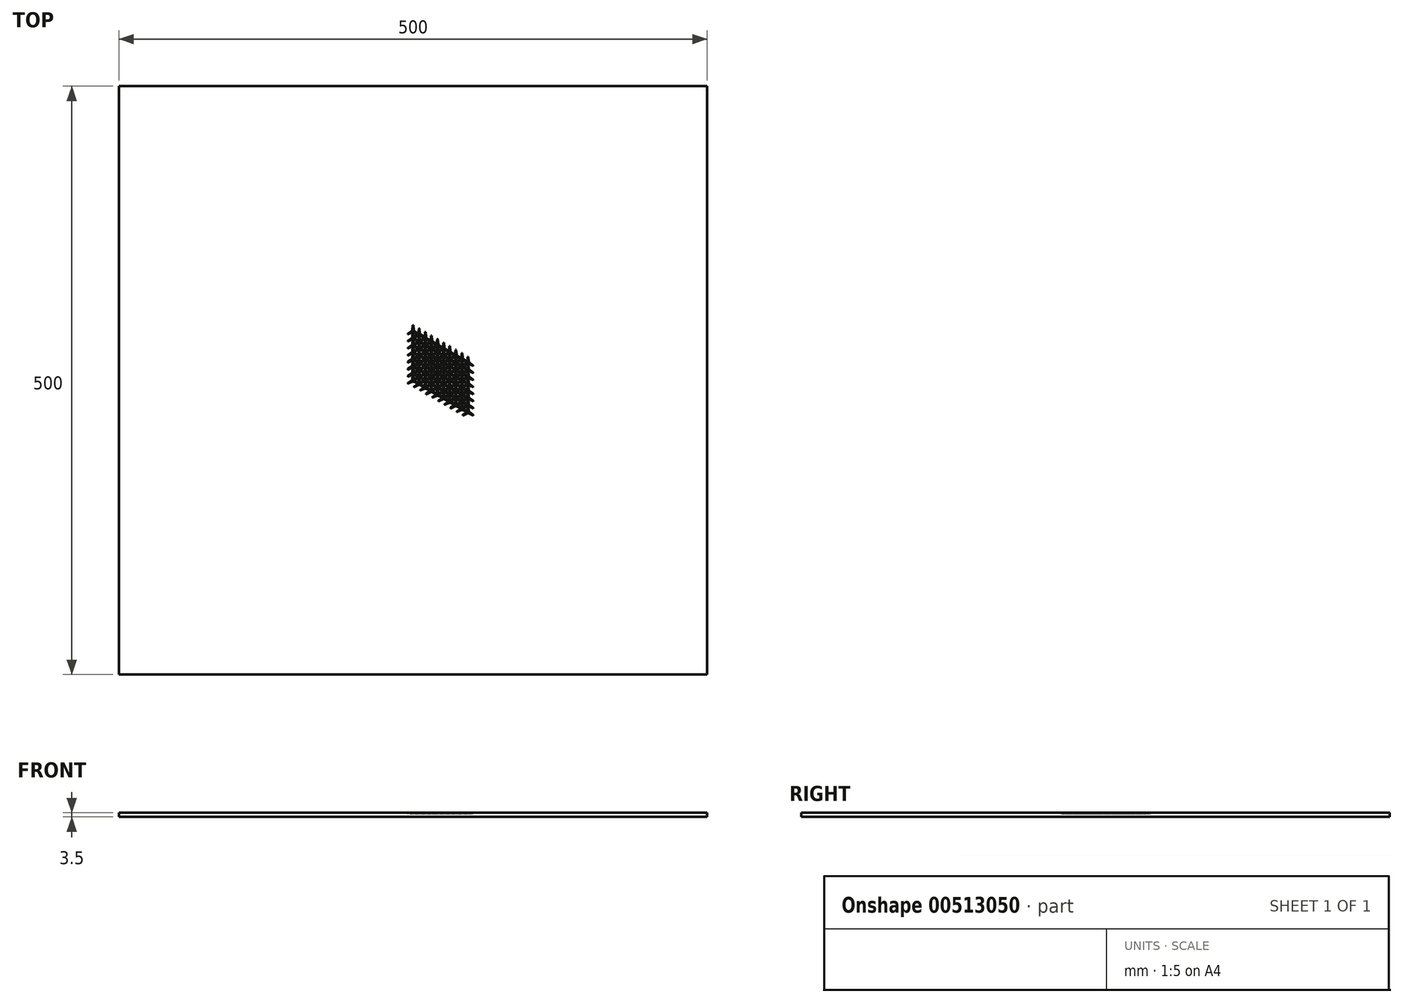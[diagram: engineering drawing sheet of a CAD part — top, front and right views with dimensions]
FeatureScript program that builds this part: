
annotation { "Feature Type Name" : "Feature", "Feature Type Description" : "" }
export const myFeature = defineFeature(function(context is Context, id is Id, definition is map)
    precondition{}
    {
        {
            var Q0;
            Q0=qCreatedBy(makeId("Top.planeOp"),FACE);
            var sketch = newSketch(context, id + "F0", { "sketchPlane" : qUnion([Q0])});
            skLineSegment(sketch, "E0", {"start": v(0, 0) * mm, "end": v(0, 250) * mm, "construction": true});
            skLineSegment(sketch, "E1", {"start": v(250, 0) * mm, "end": v(0, 0) * mm, "construction": true});
            skLineSegment(sketch, "E2.bottom", {"start": v(-250, 250) * mm, "end": v(250, 250) * mm});
            skLineSegment(sketch, "E2.top", {"start": v(-250, -250) * mm, "end": v(250, -250) * mm});
            skLineSegment(sketch, "E2.left", {"start": v(-250, 250) * mm, "end": v(-250, -250) * mm});
            skLineSegment(sketch, "E2.right", {"start": v(250, 250) * mm, "end": v(250, -250) * mm});
            skSolve(sketch);
        }
        {
            var Q0;
            Q0=makeQuery(id+"F0.imprint","IMPRINT",FACE,{"disambiguationData":[TD([[makeQuery(id+"F0.imprint","IMPRINT",EDGE,{"derivedFrom":sQuery(id+"F0.wireOp",EDGE,"E2.bottom")}),-1.0]])]});
            extrude(context, id + "F1", {"entities" : qUnion([Q0]), "depth" : 2.5 * mm});
        }
        {
            var Q0;
            Q0=makeQuery(id+"F1.opExtrude","CAP_FACE",FACE,{"disambiguationData":[OSD([sQuery(id+"F0.wireOp",EDGE,"E2.bottom"),sQuery(id+"F0.wireOp",EDGE,"E2.top"),sQuery(id+"F0.wireOp",EDGE,"E2.left"),sQuery(id+"F0.wireOp",EDGE,"E2.right")])],"isStart":false});
            var sketch = newSketch(context, id + "F2", { "sketchPlane" : qUnion([Q0])});
            skCircle(sketch, "E3", {"center": v(0, 0) * mm, "radius": 50 * mm, "construction": true});
            skLineSegment(sketch, "E4", {"start": v(0, 0) * mm, "end": v(0, 50) * mm, "construction": true});
            skLineSegment(sketch, "E5", {"start": v(0, 0) * mm, "end": v(43.3, -25) * mm, "construction": true});
            skLineSegment(sketch, "E6", {"start": v(0, 0) * mm, "end": v(-43.3, -25) * mm, "construction": true});
            skArc(sketch, "E7", {"start": v(0.5, 2.55) * mm, "mid": v(0, 3) * mm, "end": v(-0.5, 2.55) * mm});
            skCircle(sketch, "E8", {"center": v(0, 0) * mm, "radius": 0.75 * mm, "construction": true});
            skLineSegment(sketch, "E9", {"start": v(-0.5, 2.55) * mm, "end": v(-0.67, 0.86) * mm});
            skLineSegment(sketch, "E10", {"start": v(0.5, 2.55) * mm, "end": v(0.67, 0.86) * mm});
            skArc(sketch, "E11.1.0", {"start": v(-2.46, -0.84) * mm, "mid": v(-2.6, -1.5) * mm, "end": v(-1.96, -1.7) * mm});
            skLineSegment(sketch, "E11.1.1", {"start": v(-1.96, -1.7) * mm, "end": v(-0.41, -1) * mm});
            skLineSegment(sketch, "E11.1.2", {"start": v(-2.46, -0.84) * mm, "end": v(-1.08, 0.15) * mm});
            skArc(sketch, "E11.2.0", {"start": v(1.96, -1.7) * mm, "mid": v(2.6, -1.5) * mm, "end": v(2.46, -0.84) * mm});
            skLineSegment(sketch, "E11.2.1", {"start": v(2.46, -0.84) * mm, "end": v(1.08, 0.15) * mm});
            skLineSegment(sketch, "E11.2.2", {"start": v(1.96, -1.7) * mm, "end": v(0.41, -1) * mm});
            skPoint(sketch, "E12.newPointA", {"position": v(-0.74, 0.14) * mm});
            skPoint(sketch, "E12.newPointB", {"position": v(-0.45, 0.6) * mm});
            skArc(sketch, "E12.filletArc", {"start": v(-1.08, 0.15) * mm, "mid": v(-0.8, 0.46) * mm, "end": v(-0.67, 0.86) * mm});
            skPoint(sketch, "E13.newPointA", {"position": v(0.74, 0.1) * mm});
            skPoint(sketch, "E13.newPointB", {"position": v(0.5, 0.57) * mm});
            skArc(sketch, "E13.filletArc", {"start": v(0.67, 0.86) * mm, "mid": v(0.8, 0.46) * mm, "end": v(1.08, 0.15) * mm});
            skPoint(sketch, "E14.newPointA", {"position": v(-0.29, -0.7) * mm});
            skPoint(sketch, "E14.newPointB", {"position": v(0.25, -0.71) * mm});
            skArc(sketch, "E14.filletArc", {"start": v(0.41, -1) * mm, "mid": v(0, -0.92) * mm, "end": v(-0.41, -1) * mm});
            skPoint(sketch, "E15.0.1.0", {"position": v(0.25, 5.29) * mm});
            skLineSegment(sketch, "E15.0.1.1", {"start": v(2.46, 5.16) * mm, "end": v(1.08, 6.15) * mm});
            skLineSegment(sketch, "E15.0.1.2", {"start": v(1.96, 4.3) * mm, "end": v(0.41, 5) * mm});
            skArc(sketch, "E15.0.1.3", {"start": v(1.96, 4.3) * mm, "mid": v(2.6, 4.5) * mm, "end": v(2.46, 5.16) * mm});
            skLineSegment(sketch, "E15.0.1.4", {"start": v(-1.96, 4.3) * mm, "end": v(-0.41, 5) * mm});
            skArc(sketch, "E15.0.1.5", {"start": v(-2.46, 5.16) * mm, "mid": v(-2.6, 4.5) * mm, "end": v(-1.96, 4.3) * mm});
            skArc(sketch, "E15.0.1.6", {"start": v(0.5, 8.55) * mm, "mid": v(0, 9) * mm, "end": v(-0.5, 8.55) * mm});
            skPoint(sketch, "E15.0.1.7", {"position": v(0.74, 6.1) * mm});
            skPoint(sketch, "E15.0.1.8", {"position": v(-0.45, 6.6) * mm});
            skCircle(sketch, "E15.0.1.9", {"center": v(0, 6) * mm, "radius": 0.75 * mm, "construction": true});
            skPoint(sketch, "E15.0.1.10", {"position": v(0, 6) * mm});
            skLineSegment(sketch, "E15.0.1.11", {"start": v(0.5, 8.55) * mm, "end": v(0.67, 6.86) * mm});
            skPoint(sketch, "E15.0.1.12", {"position": v(-0.29, 5.3) * mm});
            skPoint(sketch, "E15.0.1.13", {"position": v(0.5, 6.57) * mm});
            skPoint(sketch, "E15.0.1.14", {"position": v(-0.74, 6.14) * mm});
            skLineSegment(sketch, "E15.0.1.15", {"start": v(-2.46, 5.16) * mm, "end": v(-1.08, 6.15) * mm});
            skLineSegment(sketch, "E15.0.1.16", {"start": v(-0.5, 8.55) * mm, "end": v(-0.67, 6.86) * mm});
            skArc(sketch, "E15.0.1.17", {"start": v(0.41, 5) * mm, "mid": v(0, 5.08) * mm, "end": v(-0.41, 5) * mm});
            skArc(sketch, "E15.0.1.18", {"start": v(-1.08, 6.15) * mm, "mid": v(-0.8, 6.46) * mm, "end": v(-0.67, 6.86) * mm});
            skArc(sketch, "E15.0.1.19", {"start": v(0.67, 6.86) * mm, "mid": v(0.8, 6.46) * mm, "end": v(1.08, 6.15) * mm});
            skPoint(sketch, "E15.1.0.0", {"position": v(5.44, -3.71) * mm});
            skLineSegment(sketch, "E15.1.0.1", {"start": v(7.65, -3.84) * mm, "end": v(6.27, -2.85) * mm});
            skLineSegment(sketch, "E15.1.0.2", {"start": v(7.16, -4.7) * mm, "end": v(5.6, -4) * mm});
            skArc(sketch, "E15.1.0.3", {"start": v(7.16, -4.7) * mm, "mid": v(7.8, -4.5) * mm, "end": v(7.65, -3.84) * mm});
            skLineSegment(sketch, "E15.1.0.4", {"start": v(3.24, -4.7) * mm, "end": v(4.79, -4) * mm});
            skArc(sketch, "E15.1.0.5", {"start": v(2.74, -3.84) * mm, "mid": v(2.6, -4.5) * mm, "end": v(3.24, -4.7) * mm});
            skArc(sketch, "E15.1.0.6", {"start": v(5.7, -0.45) * mm, "mid": v(5.2, 0) * mm, "end": v(4.7, -0.45) * mm});
            skPoint(sketch, "E15.1.0.7", {"position": v(5.94, -2.9) * mm});
            skPoint(sketch, "E15.1.0.8", {"position": v(4.74, -2.4) * mm});
            skCircle(sketch, "E15.1.0.9", {"center": v(5.2, -3) * mm, "radius": 0.75 * mm, "construction": true});
            skPoint(sketch, "E15.1.0.10", {"position": v(5.2, -3) * mm});
            skLineSegment(sketch, "E15.1.0.11", {"start": v(5.7, -0.45) * mm, "end": v(5.86, -2.14) * mm});
            skPoint(sketch, "E15.1.0.12", {"position": v(4.9, -3.7) * mm});
            skPoint(sketch, "E15.1.0.13", {"position": v(5.69, -2.43) * mm});
            skPoint(sketch, "E15.1.0.14", {"position": v(4.46, -2.86) * mm});
            skLineSegment(sketch, "E15.1.0.15", {"start": v(2.74, -3.84) * mm, "end": v(4.12, -2.85) * mm});
            skLineSegment(sketch, "E15.1.0.16", {"start": v(4.7, -0.45) * mm, "end": v(4.53, -2.14) * mm});
            skArc(sketch, "E15.1.0.17", {"start": v(5.6, -4) * mm, "mid": v(5.2, -3.92) * mm, "end": v(4.79, -4) * mm});
            skArc(sketch, "E15.1.0.18", {"start": v(4.12, -2.85) * mm, "mid": v(4.4, -2.54) * mm, "end": v(4.53, -2.14) * mm});
            skArc(sketch, "E15.1.0.19", {"start": v(5.86, -2.14) * mm, "mid": v(6, -2.54) * mm, "end": v(6.27, -2.85) * mm});
            skPoint(sketch, "E15.1.1.0", {"position": v(5.44, 2.29) * mm});
            skLineSegment(sketch, "E15.1.1.1", {"start": v(7.65, 2.16) * mm, "end": v(6.27, 3.15) * mm});
            skLineSegment(sketch, "E15.1.1.2", {"start": v(7.16, 1.3) * mm, "end": v(5.6, 2) * mm});
            skArc(sketch, "E15.1.1.3", {"start": v(7.16, 1.3) * mm, "mid": v(7.8, 1.5) * mm, "end": v(7.65, 2.16) * mm});
            skLineSegment(sketch, "E15.1.1.4", {"start": v(3.24, 1.3) * mm, "end": v(4.79, 2) * mm});
            skArc(sketch, "E15.1.1.5", {"start": v(2.74, 2.16) * mm, "mid": v(2.6, 1.5) * mm, "end": v(3.24, 1.3) * mm});
            skArc(sketch, "E15.1.1.6", {"start": v(5.7, 5.55) * mm, "mid": v(5.2, 6) * mm, "end": v(4.7, 5.55) * mm});
            skPoint(sketch, "E15.1.1.7", {"position": v(5.94, 3.1) * mm});
            skPoint(sketch, "E15.1.1.8", {"position": v(4.74, 3.6) * mm});
            skCircle(sketch, "E15.1.1.9", {"center": v(5.2, 3) * mm, "radius": 0.75 * mm, "construction": true});
            skPoint(sketch, "E15.1.1.10", {"position": v(5.2, 3) * mm});
            skLineSegment(sketch, "E15.1.1.11", {"start": v(5.7, 5.55) * mm, "end": v(5.86, 3.86) * mm});
            skPoint(sketch, "E15.1.1.12", {"position": v(4.9, 2.3) * mm});
            skPoint(sketch, "E15.1.1.13", {"position": v(5.69, 3.57) * mm});
            skPoint(sketch, "E15.1.1.14", {"position": v(4.46, 3.14) * mm});
            skLineSegment(sketch, "E15.1.1.15", {"start": v(2.74, 2.16) * mm, "end": v(4.12, 3.15) * mm});
            skLineSegment(sketch, "E15.1.1.16", {"start": v(4.7, 5.55) * mm, "end": v(4.53, 3.86) * mm});
            skArc(sketch, "E15.1.1.17", {"start": v(5.6, 2) * mm, "mid": v(5.2, 2.08) * mm, "end": v(4.79, 2) * mm});
            skArc(sketch, "E15.1.1.18", {"start": v(4.12, 3.15) * mm, "mid": v(4.4, 3.46) * mm, "end": v(4.53, 3.86) * mm});
            skArc(sketch, "E15.1.1.19", {"start": v(5.86, 3.86) * mm, "mid": v(6, 3.46) * mm, "end": v(6.27, 3.15) * mm});
            skLineSegment(sketch, "E15.direction1", {"start": v(0, 0) * mm, "end": v(5.2, -3) * mm, "construction": true});
            skLineSegment(sketch, "E15.direction2", {"start": v(0, 0) * mm, "end": v(0, 6) * mm, "construction": true});
            skPoint(sketch, "E16.0.0.2", {"position": v(0.25, 11.29) * mm});
            skLineSegment(sketch, "E16.1.0.2", {"start": v(2.46, 11.16) * mm, "end": v(1.08, 12.15) * mm});
            skLineSegment(sketch, "E16.4.0.2", {"start": v(1.96, 10.3) * mm, "end": v(0.41, 11) * mm});
            skArc(sketch, "E16.7.0.2", {"start": v(1.96, 10.3) * mm, "mid": v(2.6, 10.5) * mm, "end": v(2.46, 11.16) * mm});
            skLineSegment(sketch, "E16.11.0.2", {"start": v(-1.96, 10.3) * mm, "end": v(-0.41, 11) * mm});
            skArc(sketch, "E16.14.0.2", {"start": v(-2.46, 11.16) * mm, "mid": v(-2.6, 10.5) * mm, "end": v(-1.96, 10.3) * mm});
            skArc(sketch, "E16.18.0.2", {"start": v(0.5, 14.55) * mm, "mid": v(0, 15) * mm, "end": v(-0.5, 14.55) * mm});
            skPoint(sketch, "E16.22.0.2", {"position": v(0.74, 12.1) * mm});
            skPoint(sketch, "E16.23.0.2", {"position": v(-0.45, 12.6) * mm});
            skCircle(sketch, "E16.24.0.2", {"center": v(0, 12) * mm, "radius": 0.75 * mm, "construction": true});
            skPoint(sketch, "E16.26.0.2", {"position": v(0, 12) * mm});
            skLineSegment(sketch, "E16.27.0.2", {"start": v(0.5, 14.55) * mm, "end": v(0.67, 12.86) * mm});
            skPoint(sketch, "E16.30.0.2", {"position": v(-0.29, 11.3) * mm});
            skPoint(sketch, "E16.31.0.2", {"position": v(0.5, 12.57) * mm});
            skPoint(sketch, "E16.32.0.2", {"position": v(-0.74, 12.14) * mm});
            skLineSegment(sketch, "E16.33.0.2", {"start": v(-2.46, 11.16) * mm, "end": v(-1.08, 12.15) * mm});
            skLineSegment(sketch, "E16.36.0.2", {"start": v(-0.5, 14.55) * mm, "end": v(-0.67, 12.86) * mm});
            skArc(sketch, "E16.39.0.2", {"start": v(0.41, 11) * mm, "mid": v(0, 11.08) * mm, "end": v(-0.41, 11) * mm});
            skArc(sketch, "E16.43.0.2", {"start": v(-1.08, 12.15) * mm, "mid": v(-0.8, 12.46) * mm, "end": v(-0.67, 12.86) * mm});
            skArc(sketch, "E16.47.0.2", {"start": v(0.67, 12.86) * mm, "mid": v(0.8, 12.46) * mm, "end": v(1.08, 12.15) * mm});
            skPoint(sketch, "E16.0.0.3", {"position": v(0.25, 17.29) * mm});
            skLineSegment(sketch, "E16.1.0.3", {"start": v(2.46, 17.16) * mm, "end": v(1.08, 18.15) * mm});
            skLineSegment(sketch, "E16.4.0.3", {"start": v(1.96, 16.3) * mm, "end": v(0.41, 17) * mm});
            skArc(sketch, "E16.7.0.3", {"start": v(1.96, 16.3) * mm, "mid": v(2.6, 16.5) * mm, "end": v(2.46, 17.16) * mm});
            skLineSegment(sketch, "E16.11.0.3", {"start": v(-1.96, 16.3) * mm, "end": v(-0.41, 17) * mm});
            skArc(sketch, "E16.14.0.3", {"start": v(-2.46, 17.16) * mm, "mid": v(-2.6, 16.5) * mm, "end": v(-1.96, 16.3) * mm});
            skArc(sketch, "E16.18.0.3", {"start": v(0.5, 20.55) * mm, "mid": v(0, 21) * mm, "end": v(-0.5, 20.55) * mm});
            skPoint(sketch, "E16.22.0.3", {"position": v(0.74, 18.1) * mm});
            skPoint(sketch, "E16.23.0.3", {"position": v(-0.45, 18.6) * mm});
            skCircle(sketch, "E16.24.0.3", {"center": v(0, 18) * mm, "radius": 0.75 * mm, "construction": true});
            skPoint(sketch, "E16.26.0.3", {"position": v(0, 18) * mm});
            skLineSegment(sketch, "E16.27.0.3", {"start": v(0.5, 20.55) * mm, "end": v(0.67, 18.86) * mm});
            skPoint(sketch, "E16.30.0.3", {"position": v(-0.29, 17.3) * mm});
            skPoint(sketch, "E16.31.0.3", {"position": v(0.5, 18.57) * mm});
            skPoint(sketch, "E16.32.0.3", {"position": v(-0.74, 18.14) * mm});
            skLineSegment(sketch, "E16.33.0.3", {"start": v(-2.46, 17.16) * mm, "end": v(-1.08, 18.15) * mm});
            skLineSegment(sketch, "E16.36.0.3", {"start": v(-0.5, 20.55) * mm, "end": v(-0.67, 18.86) * mm});
            skArc(sketch, "E16.39.0.3", {"start": v(0.41, 17) * mm, "mid": v(0, 17.08) * mm, "end": v(-0.41, 17) * mm});
            skArc(sketch, "E16.43.0.3", {"start": v(-1.08, 18.15) * mm, "mid": v(-0.8, 18.46) * mm, "end": v(-0.67, 18.86) * mm});
            skArc(sketch, "E16.47.0.3", {"start": v(0.67, 18.86) * mm, "mid": v(0.8, 18.46) * mm, "end": v(1.08, 18.15) * mm});
            skPoint(sketch, "E16.0.0.4", {"position": v(0.25, 23.29) * mm});
            skLineSegment(sketch, "E16.1.0.4", {"start": v(2.46, 23.16) * mm, "end": v(1.08, 24.15) * mm});
            skLineSegment(sketch, "E16.4.0.4", {"start": v(1.96, 22.3) * mm, "end": v(0.41, 23) * mm});
            skArc(sketch, "E16.7.0.4", {"start": v(1.96, 22.3) * mm, "mid": v(2.6, 22.5) * mm, "end": v(2.46, 23.16) * mm});
            skLineSegment(sketch, "E16.11.0.4", {"start": v(-1.96, 22.3) * mm, "end": v(-0.41, 23) * mm});
            skArc(sketch, "E16.14.0.4", {"start": v(-2.46, 23.16) * mm, "mid": v(-2.6, 22.5) * mm, "end": v(-1.96, 22.3) * mm});
            skArc(sketch, "E16.18.0.4", {"start": v(0.5, 26.55) * mm, "mid": v(0, 27) * mm, "end": v(-0.5, 26.55) * mm});
            skPoint(sketch, "E16.22.0.4", {"position": v(0.74, 24.1) * mm});
            skPoint(sketch, "E16.23.0.4", {"position": v(-0.45, 24.6) * mm});
            skCircle(sketch, "E16.24.0.4", {"center": v(0, 24) * mm, "radius": 0.75 * mm, "construction": true});
            skPoint(sketch, "E16.26.0.4", {"position": v(0, 24) * mm});
            skLineSegment(sketch, "E16.27.0.4", {"start": v(0.5, 26.55) * mm, "end": v(0.67, 24.86) * mm});
            skPoint(sketch, "E16.30.0.4", {"position": v(-0.29, 23.3) * mm});
            skPoint(sketch, "E16.31.0.4", {"position": v(0.5, 24.57) * mm});
            skPoint(sketch, "E16.32.0.4", {"position": v(-0.74, 24.14) * mm});
            skLineSegment(sketch, "E16.33.0.4", {"start": v(-2.46, 23.16) * mm, "end": v(-1.08, 24.15) * mm});
            skLineSegment(sketch, "E16.36.0.4", {"start": v(-0.5, 26.55) * mm, "end": v(-0.67, 24.86) * mm});
            skArc(sketch, "E16.39.0.4", {"start": v(0.41, 23) * mm, "mid": v(0, 23.08) * mm, "end": v(-0.41, 23) * mm});
            skArc(sketch, "E16.43.0.4", {"start": v(-1.08, 24.15) * mm, "mid": v(-0.8, 24.46) * mm, "end": v(-0.67, 24.86) * mm});
            skArc(sketch, "E16.47.0.4", {"start": v(0.67, 24.86) * mm, "mid": v(0.8, 24.46) * mm, "end": v(1.08, 24.15) * mm});
            skPoint(sketch, "E16.0.0.5", {"position": v(0.25, 29.29) * mm});
            skLineSegment(sketch, "E16.1.0.5", {"start": v(2.46, 29.16) * mm, "end": v(1.08, 30.15) * mm});
            skLineSegment(sketch, "E16.4.0.5", {"start": v(1.96, 28.3) * mm, "end": v(0.41, 29) * mm});
            skArc(sketch, "E16.7.0.5", {"start": v(1.96, 28.3) * mm, "mid": v(2.6, 28.5) * mm, "end": v(2.46, 29.16) * mm});
            skLineSegment(sketch, "E16.11.0.5", {"start": v(-1.96, 28.3) * mm, "end": v(-0.41, 29) * mm});
            skArc(sketch, "E16.14.0.5", {"start": v(-2.46, 29.16) * mm, "mid": v(-2.6, 28.5) * mm, "end": v(-1.96, 28.3) * mm});
            skArc(sketch, "E16.18.0.5", {"start": v(0.5, 32.55) * mm, "mid": v(0, 33) * mm, "end": v(-0.5, 32.55) * mm});
            skPoint(sketch, "E16.22.0.5", {"position": v(0.74, 30.1) * mm});
            skPoint(sketch, "E16.23.0.5", {"position": v(-0.45, 30.6) * mm});
            skCircle(sketch, "E16.24.0.5", {"center": v(0, 30) * mm, "radius": 0.75 * mm, "construction": true});
            skPoint(sketch, "E16.26.0.5", {"position": v(0, 30) * mm});
            skLineSegment(sketch, "E16.27.0.5", {"start": v(0.5, 32.55) * mm, "end": v(0.67, 30.86) * mm});
            skPoint(sketch, "E16.30.0.5", {"position": v(-0.29, 29.3) * mm});
            skPoint(sketch, "E16.31.0.5", {"position": v(0.5, 30.57) * mm});
            skPoint(sketch, "E16.32.0.5", {"position": v(-0.74, 30.14) * mm});
            skLineSegment(sketch, "E16.33.0.5", {"start": v(-2.46, 29.16) * mm, "end": v(-1.08, 30.15) * mm});
            skLineSegment(sketch, "E16.36.0.5", {"start": v(-0.5, 32.55) * mm, "end": v(-0.67, 30.86) * mm});
            skArc(sketch, "E16.39.0.5", {"start": v(0.41, 29) * mm, "mid": v(0, 29.08) * mm, "end": v(-0.41, 29) * mm});
            skArc(sketch, "E16.43.0.5", {"start": v(-1.08, 30.15) * mm, "mid": v(-0.8, 30.46) * mm, "end": v(-0.67, 30.86) * mm});
            skArc(sketch, "E16.47.0.5", {"start": v(0.67, 30.86) * mm, "mid": v(0.8, 30.46) * mm, "end": v(1.08, 30.15) * mm});
            skPoint(sketch, "E16.0.0.6", {"position": v(0.25, 35.29) * mm});
            skLineSegment(sketch, "E16.1.0.6", {"start": v(2.46, 35.16) * mm, "end": v(1.08, 36.15) * mm});
            skLineSegment(sketch, "E16.4.0.6", {"start": v(1.96, 34.3) * mm, "end": v(0.41, 35) * mm});
            skArc(sketch, "E16.7.0.6", {"start": v(1.96, 34.3) * mm, "mid": v(2.6, 34.5) * mm, "end": v(2.46, 35.16) * mm});
            skLineSegment(sketch, "E16.11.0.6", {"start": v(-1.96, 34.3) * mm, "end": v(-0.41, 35) * mm});
            skArc(sketch, "E16.14.0.6", {"start": v(-2.46, 35.16) * mm, "mid": v(-2.6, 34.5) * mm, "end": v(-1.96, 34.3) * mm});
            skArc(sketch, "E16.18.0.6", {"start": v(0.5, 38.55) * mm, "mid": v(0, 39) * mm, "end": v(-0.5, 38.55) * mm});
            skPoint(sketch, "E16.22.0.6", {"position": v(0.74, 36.1) * mm});
            skPoint(sketch, "E16.23.0.6", {"position": v(-0.45, 36.6) * mm});
            skCircle(sketch, "E16.24.0.6", {"center": v(0, 36) * mm, "radius": 0.75 * mm, "construction": true});
            skPoint(sketch, "E16.26.0.6", {"position": v(0, 36) * mm});
            skLineSegment(sketch, "E16.27.0.6", {"start": v(0.5, 38.55) * mm, "end": v(0.67, 36.86) * mm});
            skPoint(sketch, "E16.30.0.6", {"position": v(-0.29, 35.3) * mm});
            skPoint(sketch, "E16.31.0.6", {"position": v(0.5, 36.57) * mm});
            skPoint(sketch, "E16.32.0.6", {"position": v(-0.74, 36.14) * mm});
            skLineSegment(sketch, "E16.33.0.6", {"start": v(-2.46, 35.16) * mm, "end": v(-1.08, 36.15) * mm});
            skLineSegment(sketch, "E16.36.0.6", {"start": v(-0.5, 38.55) * mm, "end": v(-0.67, 36.86) * mm});
            skArc(sketch, "E16.39.0.6", {"start": v(0.41, 35) * mm, "mid": v(0, 35.08) * mm, "end": v(-0.41, 35) * mm});
            skArc(sketch, "E16.43.0.6", {"start": v(-1.08, 36.15) * mm, "mid": v(-0.8, 36.46) * mm, "end": v(-0.67, 36.86) * mm});
            skArc(sketch, "E16.47.0.6", {"start": v(0.67, 36.86) * mm, "mid": v(0.8, 36.46) * mm, "end": v(1.08, 36.15) * mm});
            skPoint(sketch, "E16.0.0.7", {"position": v(0.25, 41.29) * mm});
            skLineSegment(sketch, "E16.1.0.7", {"start": v(2.46, 41.16) * mm, "end": v(1.08, 42.15) * mm});
            skLineSegment(sketch, "E16.4.0.7", {"start": v(1.96, 40.3) * mm, "end": v(0.41, 41) * mm});
            skArc(sketch, "E16.7.0.7", {"start": v(1.96, 40.3) * mm, "mid": v(2.6, 40.5) * mm, "end": v(2.46, 41.16) * mm});
            skLineSegment(sketch, "E16.11.0.7", {"start": v(-1.96, 40.3) * mm, "end": v(-0.41, 41) * mm});
            skArc(sketch, "E16.14.0.7", {"start": v(-2.46, 41.16) * mm, "mid": v(-2.6, 40.5) * mm, "end": v(-1.96, 40.3) * mm});
            skArc(sketch, "E16.18.0.7", {"start": v(0.5, 44.55) * mm, "mid": v(0, 45) * mm, "end": v(-0.5, 44.55) * mm});
            skPoint(sketch, "E16.22.0.7", {"position": v(0.74, 42.1) * mm});
            skPoint(sketch, "E16.23.0.7", {"position": v(-0.45, 42.6) * mm});
            skCircle(sketch, "E16.24.0.7", {"center": v(0, 42) * mm, "radius": 0.75 * mm, "construction": true});
            skPoint(sketch, "E16.26.0.7", {"position": v(0, 42) * mm});
            skLineSegment(sketch, "E16.27.0.7", {"start": v(0.5, 44.55) * mm, "end": v(0.67, 42.86) * mm});
            skPoint(sketch, "E16.30.0.7", {"position": v(-0.29, 41.3) * mm});
            skPoint(sketch, "E16.31.0.7", {"position": v(0.5, 42.57) * mm});
            skPoint(sketch, "E16.32.0.7", {"position": v(-0.74, 42.14) * mm});
            skLineSegment(sketch, "E16.33.0.7", {"start": v(-2.46, 41.16) * mm, "end": v(-1.08, 42.15) * mm});
            skLineSegment(sketch, "E16.36.0.7", {"start": v(-0.5, 44.55) * mm, "end": v(-0.67, 42.86) * mm});
            skArc(sketch, "E16.39.0.7", {"start": v(0.41, 41) * mm, "mid": v(0, 41.08) * mm, "end": v(-0.41, 41) * mm});
            skArc(sketch, "E16.43.0.7", {"start": v(-1.08, 42.15) * mm, "mid": v(-0.8, 42.46) * mm, "end": v(-0.67, 42.86) * mm});
            skArc(sketch, "E16.47.0.7", {"start": v(0.67, 42.86) * mm, "mid": v(0.8, 42.46) * mm, "end": v(1.08, 42.15) * mm});
            skPoint(sketch, "E16.0.1.2", {"position": v(5.44, 8.29) * mm});
            skLineSegment(sketch, "E16.1.1.2", {"start": v(7.65, 8.16) * mm, "end": v(6.27, 9.15) * mm});
            skLineSegment(sketch, "E16.4.1.2", {"start": v(7.16, 7.3) * mm, "end": v(5.6, 8) * mm});
            skArc(sketch, "E16.7.1.2", {"start": v(7.16, 7.3) * mm, "mid": v(7.8, 7.5) * mm, "end": v(7.65, 8.16) * mm});
            skLineSegment(sketch, "E16.11.1.2", {"start": v(3.24, 7.3) * mm, "end": v(4.79, 8) * mm});
            skArc(sketch, "E16.14.1.2", {"start": v(2.74, 8.16) * mm, "mid": v(2.6, 7.5) * mm, "end": v(3.24, 7.3) * mm});
            skArc(sketch, "E16.18.1.2", {"start": v(5.7, 11.55) * mm, "mid": v(5.2, 12) * mm, "end": v(4.7, 11.55) * mm});
            skPoint(sketch, "E16.22.1.2", {"position": v(5.94, 9.1) * mm});
            skPoint(sketch, "E16.23.1.2", {"position": v(4.74, 9.6) * mm});
            skCircle(sketch, "E16.24.1.2", {"center": v(5.2, 9) * mm, "radius": 0.75 * mm, "construction": true});
            skPoint(sketch, "E16.26.1.2", {"position": v(5.2, 9) * mm});
            skLineSegment(sketch, "E16.27.1.2", {"start": v(5.7, 11.55) * mm, "end": v(5.86, 9.86) * mm});
            skPoint(sketch, "E16.30.1.2", {"position": v(4.9, 8.3) * mm});
            skPoint(sketch, "E16.31.1.2", {"position": v(5.69, 9.57) * mm});
            skPoint(sketch, "E16.32.1.2", {"position": v(4.46, 9.14) * mm});
            skLineSegment(sketch, "E16.33.1.2", {"start": v(2.74, 8.16) * mm, "end": v(4.12, 9.15) * mm});
            skLineSegment(sketch, "E16.36.1.2", {"start": v(4.7, 11.55) * mm, "end": v(4.53, 9.86) * mm});
            skArc(sketch, "E16.39.1.2", {"start": v(5.6, 8) * mm, "mid": v(5.2, 8.08) * mm, "end": v(4.79, 8) * mm});
            skArc(sketch, "E16.43.1.2", {"start": v(4.12, 9.15) * mm, "mid": v(4.4, 9.46) * mm, "end": v(4.53, 9.86) * mm});
            skArc(sketch, "E16.47.1.2", {"start": v(5.86, 9.86) * mm, "mid": v(6, 9.46) * mm, "end": v(6.27, 9.15) * mm});
            skPoint(sketch, "E16.0.1.3", {"position": v(5.44, 14.29) * mm});
            skLineSegment(sketch, "E16.1.1.3", {"start": v(7.65, 14.16) * mm, "end": v(6.27, 15.15) * mm});
            skLineSegment(sketch, "E16.4.1.3", {"start": v(7.16, 13.3) * mm, "end": v(5.6, 14) * mm});
            skArc(sketch, "E16.7.1.3", {"start": v(7.16, 13.3) * mm, "mid": v(7.8, 13.5) * mm, "end": v(7.65, 14.16) * mm});
            skLineSegment(sketch, "E16.11.1.3", {"start": v(3.24, 13.3) * mm, "end": v(4.79, 14) * mm});
            skArc(sketch, "E16.14.1.3", {"start": v(2.74, 14.16) * mm, "mid": v(2.6, 13.5) * mm, "end": v(3.24, 13.3) * mm});
            skArc(sketch, "E16.18.1.3", {"start": v(5.7, 17.55) * mm, "mid": v(5.2, 18) * mm, "end": v(4.7, 17.55) * mm});
            skPoint(sketch, "E16.22.1.3", {"position": v(5.94, 15.1) * mm});
            skPoint(sketch, "E16.23.1.3", {"position": v(4.74, 15.6) * mm});
            skCircle(sketch, "E16.24.1.3", {"center": v(5.2, 15) * mm, "radius": 0.75 * mm, "construction": true});
            skPoint(sketch, "E16.26.1.3", {"position": v(5.2, 15) * mm});
            skLineSegment(sketch, "E16.27.1.3", {"start": v(5.7, 17.55) * mm, "end": v(5.86, 15.86) * mm});
            skPoint(sketch, "E16.30.1.3", {"position": v(4.9, 14.3) * mm});
            skPoint(sketch, "E16.31.1.3", {"position": v(5.69, 15.57) * mm});
            skPoint(sketch, "E16.32.1.3", {"position": v(4.46, 15.14) * mm});
            skLineSegment(sketch, "E16.33.1.3", {"start": v(2.74, 14.16) * mm, "end": v(4.12, 15.15) * mm});
            skLineSegment(sketch, "E16.36.1.3", {"start": v(4.7, 17.55) * mm, "end": v(4.53, 15.86) * mm});
            skArc(sketch, "E16.39.1.3", {"start": v(5.6, 14) * mm, "mid": v(5.2, 14.08) * mm, "end": v(4.79, 14) * mm});
            skArc(sketch, "E16.43.1.3", {"start": v(4.12, 15.15) * mm, "mid": v(4.4, 15.46) * mm, "end": v(4.53, 15.86) * mm});
            skArc(sketch, "E16.47.1.3", {"start": v(5.86, 15.86) * mm, "mid": v(6, 15.46) * mm, "end": v(6.27, 15.15) * mm});
            skPoint(sketch, "E16.0.1.4", {"position": v(5.44, 20.29) * mm});
            skLineSegment(sketch, "E16.1.1.4", {"start": v(7.65, 20.16) * mm, "end": v(6.27, 21.15) * mm});
            skLineSegment(sketch, "E16.4.1.4", {"start": v(7.16, 19.3) * mm, "end": v(5.6, 20) * mm});
            skArc(sketch, "E16.7.1.4", {"start": v(7.16, 19.3) * mm, "mid": v(7.8, 19.5) * mm, "end": v(7.65, 20.16) * mm});
            skLineSegment(sketch, "E16.11.1.4", {"start": v(3.24, 19.3) * mm, "end": v(4.79, 20) * mm});
            skArc(sketch, "E16.14.1.4", {"start": v(2.74, 20.16) * mm, "mid": v(2.6, 19.5) * mm, "end": v(3.24, 19.3) * mm});
            skArc(sketch, "E16.18.1.4", {"start": v(5.7, 23.55) * mm, "mid": v(5.2, 24) * mm, "end": v(4.7, 23.55) * mm});
            skPoint(sketch, "E16.22.1.4", {"position": v(5.94, 21.1) * mm});
            skPoint(sketch, "E16.23.1.4", {"position": v(4.74, 21.6) * mm});
            skCircle(sketch, "E16.24.1.4", {"center": v(5.2, 21) * mm, "radius": 0.75 * mm, "construction": true});
            skPoint(sketch, "E16.26.1.4", {"position": v(5.2, 21) * mm});
            skLineSegment(sketch, "E16.27.1.4", {"start": v(5.7, 23.55) * mm, "end": v(5.86, 21.86) * mm});
            skPoint(sketch, "E16.30.1.4", {"position": v(4.9, 20.3) * mm});
            skPoint(sketch, "E16.31.1.4", {"position": v(5.69, 21.57) * mm});
            skPoint(sketch, "E16.32.1.4", {"position": v(4.46, 21.14) * mm});
            skLineSegment(sketch, "E16.33.1.4", {"start": v(2.74, 20.16) * mm, "end": v(4.12, 21.15) * mm});
            skLineSegment(sketch, "E16.36.1.4", {"start": v(4.7, 23.55) * mm, "end": v(4.53, 21.86) * mm});
            skArc(sketch, "E16.39.1.4", {"start": v(5.6, 20) * mm, "mid": v(5.2, 20.08) * mm, "end": v(4.79, 20) * mm});
            skArc(sketch, "E16.43.1.4", {"start": v(4.12, 21.15) * mm, "mid": v(4.4, 21.46) * mm, "end": v(4.53, 21.86) * mm});
            skArc(sketch, "E16.47.1.4", {"start": v(5.86, 21.86) * mm, "mid": v(6, 21.46) * mm, "end": v(6.27, 21.15) * mm});
            skPoint(sketch, "E16.0.1.5", {"position": v(5.44, 26.29) * mm});
            skLineSegment(sketch, "E16.1.1.5", {"start": v(7.65, 26.16) * mm, "end": v(6.27, 27.15) * mm});
            skLineSegment(sketch, "E16.4.1.5", {"start": v(7.16, 25.3) * mm, "end": v(5.6, 26) * mm});
            skArc(sketch, "E16.7.1.5", {"start": v(7.16, 25.3) * mm, "mid": v(7.8, 25.5) * mm, "end": v(7.65, 26.16) * mm});
            skLineSegment(sketch, "E16.11.1.5", {"start": v(3.24, 25.3) * mm, "end": v(4.79, 26) * mm});
            skArc(sketch, "E16.14.1.5", {"start": v(2.74, 26.16) * mm, "mid": v(2.6, 25.5) * mm, "end": v(3.24, 25.3) * mm});
            skArc(sketch, "E16.18.1.5", {"start": v(5.7, 29.55) * mm, "mid": v(5.2, 30) * mm, "end": v(4.7, 29.55) * mm});
            skPoint(sketch, "E16.22.1.5", {"position": v(5.94, 27.1) * mm});
            skPoint(sketch, "E16.23.1.5", {"position": v(4.74, 27.6) * mm});
            skCircle(sketch, "E16.24.1.5", {"center": v(5.2, 27) * mm, "radius": 0.75 * mm, "construction": true});
            skPoint(sketch, "E16.26.1.5", {"position": v(5.2, 27) * mm});
            skLineSegment(sketch, "E16.27.1.5", {"start": v(5.7, 29.55) * mm, "end": v(5.86, 27.86) * mm});
            skPoint(sketch, "E16.30.1.5", {"position": v(4.9, 26.3) * mm});
            skPoint(sketch, "E16.31.1.5", {"position": v(5.69, 27.57) * mm});
            skPoint(sketch, "E16.32.1.5", {"position": v(4.46, 27.14) * mm});
            skLineSegment(sketch, "E16.33.1.5", {"start": v(2.74, 26.16) * mm, "end": v(4.12, 27.15) * mm});
            skLineSegment(sketch, "E16.36.1.5", {"start": v(4.7, 29.55) * mm, "end": v(4.53, 27.86) * mm});
            skArc(sketch, "E16.39.1.5", {"start": v(5.6, 26) * mm, "mid": v(5.2, 26.08) * mm, "end": v(4.79, 26) * mm});
            skArc(sketch, "E16.43.1.5", {"start": v(4.12, 27.15) * mm, "mid": v(4.4, 27.46) * mm, "end": v(4.53, 27.86) * mm});
            skArc(sketch, "E16.47.1.5", {"start": v(5.86, 27.86) * mm, "mid": v(6, 27.46) * mm, "end": v(6.27, 27.15) * mm});
            skPoint(sketch, "E16.0.1.6", {"position": v(5.44, 32.29) * mm});
            skLineSegment(sketch, "E16.1.1.6", {"start": v(7.65, 32.16) * mm, "end": v(6.27, 33.15) * mm});
            skLineSegment(sketch, "E16.4.1.6", {"start": v(7.16, 31.3) * mm, "end": v(5.6, 32) * mm});
            skArc(sketch, "E16.7.1.6", {"start": v(7.16, 31.3) * mm, "mid": v(7.8, 31.5) * mm, "end": v(7.65, 32.16) * mm});
            skLineSegment(sketch, "E16.11.1.6", {"start": v(3.24, 31.3) * mm, "end": v(4.79, 32) * mm});
            skArc(sketch, "E16.14.1.6", {"start": v(2.74, 32.16) * mm, "mid": v(2.6, 31.5) * mm, "end": v(3.24, 31.3) * mm});
            skArc(sketch, "E16.18.1.6", {"start": v(5.7, 35.55) * mm, "mid": v(5.2, 36) * mm, "end": v(4.7, 35.55) * mm});
            skPoint(sketch, "E16.22.1.6", {"position": v(5.94, 33.1) * mm});
            skPoint(sketch, "E16.23.1.6", {"position": v(4.74, 33.6) * mm});
            skCircle(sketch, "E16.24.1.6", {"center": v(5.2, 33) * mm, "radius": 0.75 * mm, "construction": true});
            skPoint(sketch, "E16.26.1.6", {"position": v(5.2, 33) * mm});
            skLineSegment(sketch, "E16.27.1.6", {"start": v(5.7, 35.55) * mm, "end": v(5.86, 33.86) * mm});
            skPoint(sketch, "E16.30.1.6", {"position": v(4.9, 32.3) * mm});
            skPoint(sketch, "E16.31.1.6", {"position": v(5.69, 33.57) * mm});
            skPoint(sketch, "E16.32.1.6", {"position": v(4.46, 33.14) * mm});
            skLineSegment(sketch, "E16.33.1.6", {"start": v(2.74, 32.16) * mm, "end": v(4.12, 33.15) * mm});
            skLineSegment(sketch, "E16.36.1.6", {"start": v(4.7, 35.55) * mm, "end": v(4.53, 33.86) * mm});
            skArc(sketch, "E16.39.1.6", {"start": v(5.6, 32) * mm, "mid": v(5.2, 32.08) * mm, "end": v(4.79, 32) * mm});
            skArc(sketch, "E16.43.1.6", {"start": v(4.12, 33.15) * mm, "mid": v(4.4, 33.46) * mm, "end": v(4.53, 33.86) * mm});
            skArc(sketch, "E16.47.1.6", {"start": v(5.86, 33.86) * mm, "mid": v(6, 33.46) * mm, "end": v(6.27, 33.15) * mm});
            skPoint(sketch, "E16.0.1.7", {"position": v(5.44, 38.29) * mm});
            skLineSegment(sketch, "E16.1.1.7", {"start": v(7.65, 38.16) * mm, "end": v(6.27, 39.15) * mm});
            skLineSegment(sketch, "E16.4.1.7", {"start": v(7.16, 37.3) * mm, "end": v(5.6, 38) * mm});
            skArc(sketch, "E16.7.1.7", {"start": v(7.16, 37.3) * mm, "mid": v(7.8, 37.5) * mm, "end": v(7.65, 38.16) * mm});
            skLineSegment(sketch, "E16.11.1.7", {"start": v(3.24, 37.3) * mm, "end": v(4.79, 38) * mm});
            skArc(sketch, "E16.14.1.7", {"start": v(2.74, 38.16) * mm, "mid": v(2.6, 37.5) * mm, "end": v(3.24, 37.3) * mm});
            skArc(sketch, "E16.18.1.7", {"start": v(5.7, 41.55) * mm, "mid": v(5.2, 42) * mm, "end": v(4.7, 41.55) * mm});
            skPoint(sketch, "E16.22.1.7", {"position": v(5.94, 39.1) * mm});
            skPoint(sketch, "E16.23.1.7", {"position": v(4.74, 39.6) * mm});
            skCircle(sketch, "E16.24.1.7", {"center": v(5.2, 39) * mm, "radius": 0.75 * mm, "construction": true});
            skPoint(sketch, "E16.26.1.7", {"position": v(5.2, 39) * mm});
            skLineSegment(sketch, "E16.27.1.7", {"start": v(5.7, 41.55) * mm, "end": v(5.86, 39.86) * mm});
            skPoint(sketch, "E16.30.1.7", {"position": v(4.9, 38.3) * mm});
            skPoint(sketch, "E16.31.1.7", {"position": v(5.69, 39.57) * mm});
            skPoint(sketch, "E16.32.1.7", {"position": v(4.46, 39.14) * mm});
            skLineSegment(sketch, "E16.33.1.7", {"start": v(2.74, 38.16) * mm, "end": v(4.12, 39.15) * mm});
            skLineSegment(sketch, "E16.36.1.7", {"start": v(4.7, 41.55) * mm, "end": v(4.53, 39.86) * mm});
            skArc(sketch, "E16.39.1.7", {"start": v(5.6, 38) * mm, "mid": v(5.2, 38.08) * mm, "end": v(4.79, 38) * mm});
            skArc(sketch, "E16.43.1.7", {"start": v(4.12, 39.15) * mm, "mid": v(4.4, 39.46) * mm, "end": v(4.53, 39.86) * mm});
            skArc(sketch, "E16.47.1.7", {"start": v(5.86, 39.86) * mm, "mid": v(6, 39.46) * mm, "end": v(6.27, 39.15) * mm});
            skPoint(sketch, "E17.0.2.0", {"position": v(10.64, -6.71) * mm});
            skLineSegment(sketch, "E17.1.2.0", {"start": v(12.85, -6.84) * mm, "end": v(11.47, -5.85) * mm});
            skLineSegment(sketch, "E17.4.2.0", {"start": v(12.35, -7.7) * mm, "end": v(10.8, -7) * mm});
            skArc(sketch, "E17.7.2.0", {"start": v(12.35, -7.7) * mm, "mid": v(13, -7.5) * mm, "end": v(12.85, -6.84) * mm});
            skLineSegment(sketch, "E17.11.2.0", {"start": v(8.43, -7.7) * mm, "end": v(9.98, -7) * mm});
            skArc(sketch, "E17.14.2.0", {"start": v(7.94, -6.84) * mm, "mid": v(7.8, -7.5) * mm, "end": v(8.43, -7.7) * mm});
            skArc(sketch, "E17.18.2.0", {"start": v(10.89, -3.45) * mm, "mid": v(10.4, -3) * mm, "end": v(9.9, -3.45) * mm});
            skPoint(sketch, "E17.22.2.0", {"position": v(11.14, -5.9) * mm});
            skPoint(sketch, "E17.23.2.0", {"position": v(9.94, -5.4) * mm});
            skCircle(sketch, "E17.24.2.0", {"center": v(10.4, -6) * mm, "radius": 0.75 * mm, "construction": true});
            skPoint(sketch, "E17.26.2.0", {"position": v(10.4, -6) * mm});
            skLineSegment(sketch, "E17.27.2.0", {"start": v(10.89, -3.45) * mm, "end": v(11.06, -5.14) * mm});
            skPoint(sketch, "E17.30.2.0", {"position": v(10.1, -6.7) * mm});
            skPoint(sketch, "E17.31.2.0", {"position": v(10.88, -5.43) * mm});
            skPoint(sketch, "E17.32.2.0", {"position": v(9.65, -5.86) * mm});
            skLineSegment(sketch, "E17.33.2.0", {"start": v(7.94, -6.84) * mm, "end": v(9.31, -5.85) * mm});
            skLineSegment(sketch, "E17.36.2.0", {"start": v(9.9, -3.45) * mm, "end": v(9.72, -5.14) * mm});
            skArc(sketch, "E17.39.2.0", {"start": v(10.8, -7) * mm, "mid": v(10.4, -6.92) * mm, "end": v(9.98, -7) * mm});
            skArc(sketch, "E17.43.2.0", {"start": v(9.31, -5.85) * mm, "mid": v(9.6, -5.54) * mm, "end": v(9.72, -5.14) * mm});
            skArc(sketch, "E17.47.2.0", {"start": v(11.06, -5.14) * mm, "mid": v(11.19, -5.54) * mm, "end": v(11.47, -5.85) * mm});
            skPoint(sketch, "E17.0.2.1", {"position": v(10.64, -0.71) * mm});
            skLineSegment(sketch, "E17.1.2.1", {"start": v(12.85, -0.84) * mm, "end": v(11.47, 0.15) * mm});
            skLineSegment(sketch, "E17.4.2.1", {"start": v(12.35, -1.7) * mm, "end": v(10.8, -1) * mm});
            skArc(sketch, "E17.7.2.1", {"start": v(12.35, -1.7) * mm, "mid": v(13, -1.5) * mm, "end": v(12.85, -0.84) * mm});
            skLineSegment(sketch, "E17.11.2.1", {"start": v(8.43, -1.7) * mm, "end": v(9.98, -1) * mm});
            skArc(sketch, "E17.14.2.1", {"start": v(7.94, -0.84) * mm, "mid": v(7.8, -1.5) * mm, "end": v(8.43, -1.7) * mm});
            skArc(sketch, "E17.18.2.1", {"start": v(10.89, 2.55) * mm, "mid": v(10.4, 3) * mm, "end": v(9.9, 2.55) * mm});
            skPoint(sketch, "E17.22.2.1", {"position": v(11.14, 0.1) * mm});
            skPoint(sketch, "E17.23.2.1", {"position": v(9.94, 0.6) * mm});
            skCircle(sketch, "E17.24.2.1", {"center": v(10.4, 0) * mm, "radius": 0.75 * mm, "construction": true});
            skPoint(sketch, "E17.26.2.1", {"position": v(10.4, 0) * mm});
            skLineSegment(sketch, "E17.27.2.1", {"start": v(10.89, 2.55) * mm, "end": v(11.06, 0.86) * mm});
            skPoint(sketch, "E17.30.2.1", {"position": v(10.1, -0.7) * mm});
            skPoint(sketch, "E17.31.2.1", {"position": v(10.88, 0.57) * mm});
            skPoint(sketch, "E17.32.2.1", {"position": v(9.65, 0.14) * mm});
            skLineSegment(sketch, "E17.33.2.1", {"start": v(7.94, -0.84) * mm, "end": v(9.31, 0.15) * mm});
            skLineSegment(sketch, "E17.36.2.1", {"start": v(9.9, 2.55) * mm, "end": v(9.72, 0.86) * mm});
            skArc(sketch, "E17.39.2.1", {"start": v(10.8, -1) * mm, "mid": v(10.4, -0.92) * mm, "end": v(9.98, -1) * mm});
            skArc(sketch, "E17.43.2.1", {"start": v(9.31, 0.15) * mm, "mid": v(9.6, 0.46) * mm, "end": v(9.72, 0.86) * mm});
            skArc(sketch, "E17.47.2.1", {"start": v(11.06, 0.86) * mm, "mid": v(11.19, 0.46) * mm, "end": v(11.47, 0.15) * mm});
            skPoint(sketch, "E17.0.2.2", {"position": v(10.64, 5.29) * mm});
            skLineSegment(sketch, "E17.1.2.2", {"start": v(12.85, 5.16) * mm, "end": v(11.47, 6.15) * mm});
            skLineSegment(sketch, "E17.4.2.2", {"start": v(12.35, 4.3) * mm, "end": v(10.8, 5) * mm});
            skArc(sketch, "E17.7.2.2", {"start": v(12.35, 4.3) * mm, "mid": v(13, 4.5) * mm, "end": v(12.85, 5.16) * mm});
            skLineSegment(sketch, "E17.11.2.2", {"start": v(8.43, 4.3) * mm, "end": v(9.98, 5) * mm});
            skArc(sketch, "E17.14.2.2", {"start": v(7.94, 5.16) * mm, "mid": v(7.8, 4.5) * mm, "end": v(8.43, 4.3) * mm});
            skArc(sketch, "E17.18.2.2", {"start": v(10.89, 8.55) * mm, "mid": v(10.4, 9) * mm, "end": v(9.9, 8.55) * mm});
            skPoint(sketch, "E17.22.2.2", {"position": v(11.14, 6.1) * mm});
            skPoint(sketch, "E17.23.2.2", {"position": v(9.94, 6.6) * mm});
            skCircle(sketch, "E17.24.2.2", {"center": v(10.4, 6) * mm, "radius": 0.75 * mm, "construction": true});
            skPoint(sketch, "E17.26.2.2", {"position": v(10.4, 6) * mm});
            skLineSegment(sketch, "E17.27.2.2", {"start": v(10.89, 8.55) * mm, "end": v(11.06, 6.86) * mm});
            skPoint(sketch, "E17.30.2.2", {"position": v(10.1, 5.3) * mm});
            skPoint(sketch, "E17.31.2.2", {"position": v(10.88, 6.57) * mm});
            skPoint(sketch, "E17.32.2.2", {"position": v(9.65, 6.14) * mm});
            skLineSegment(sketch, "E17.33.2.2", {"start": v(7.94, 5.16) * mm, "end": v(9.31, 6.15) * mm});
            skLineSegment(sketch, "E17.36.2.2", {"start": v(9.9, 8.55) * mm, "end": v(9.72, 6.86) * mm});
            skArc(sketch, "E17.39.2.2", {"start": v(10.8, 5) * mm, "mid": v(10.4, 5.08) * mm, "end": v(9.98, 5) * mm});
            skArc(sketch, "E17.43.2.2", {"start": v(9.31, 6.15) * mm, "mid": v(9.6, 6.46) * mm, "end": v(9.72, 6.86) * mm});
            skArc(sketch, "E17.47.2.2", {"start": v(11.06, 6.86) * mm, "mid": v(11.19, 6.46) * mm, "end": v(11.47, 6.15) * mm});
            skPoint(sketch, "E17.0.2.3", {"position": v(10.64, 11.29) * mm});
            skLineSegment(sketch, "E17.1.2.3", {"start": v(12.85, 11.16) * mm, "end": v(11.47, 12.15) * mm});
            skLineSegment(sketch, "E17.4.2.3", {"start": v(12.35, 10.3) * mm, "end": v(10.8, 11) * mm});
            skArc(sketch, "E17.7.2.3", {"start": v(12.35, 10.3) * mm, "mid": v(13, 10.5) * mm, "end": v(12.85, 11.16) * mm});
            skLineSegment(sketch, "E17.11.2.3", {"start": v(8.43, 10.3) * mm, "end": v(9.98, 11) * mm});
            skArc(sketch, "E17.14.2.3", {"start": v(7.94, 11.16) * mm, "mid": v(7.8, 10.5) * mm, "end": v(8.43, 10.3) * mm});
            skArc(sketch, "E17.18.2.3", {"start": v(10.89, 14.55) * mm, "mid": v(10.4, 15) * mm, "end": v(9.9, 14.55) * mm});
            skPoint(sketch, "E17.22.2.3", {"position": v(11.14, 12.1) * mm});
            skPoint(sketch, "E17.23.2.3", {"position": v(9.94, 12.6) * mm});
            skCircle(sketch, "E17.24.2.3", {"center": v(10.4, 12) * mm, "radius": 0.75 * mm, "construction": true});
            skPoint(sketch, "E17.26.2.3", {"position": v(10.4, 12) * mm});
            skLineSegment(sketch, "E17.27.2.3", {"start": v(10.89, 14.55) * mm, "end": v(11.06, 12.86) * mm});
            skPoint(sketch, "E17.30.2.3", {"position": v(10.1, 11.3) * mm});
            skPoint(sketch, "E17.31.2.3", {"position": v(10.88, 12.57) * mm});
            skPoint(sketch, "E17.32.2.3", {"position": v(9.65, 12.14) * mm});
            skLineSegment(sketch, "E17.33.2.3", {"start": v(7.94, 11.16) * mm, "end": v(9.31, 12.15) * mm});
            skLineSegment(sketch, "E17.36.2.3", {"start": v(9.9, 14.55) * mm, "end": v(9.72, 12.86) * mm});
            skArc(sketch, "E17.39.2.3", {"start": v(10.8, 11) * mm, "mid": v(10.4, 11.08) * mm, "end": v(9.98, 11) * mm});
            skArc(sketch, "E17.43.2.3", {"start": v(9.31, 12.15) * mm, "mid": v(9.6, 12.46) * mm, "end": v(9.72, 12.86) * mm});
            skArc(sketch, "E17.47.2.3", {"start": v(11.06, 12.86) * mm, "mid": v(11.19, 12.46) * mm, "end": v(11.47, 12.15) * mm});
            skPoint(sketch, "E17.0.2.4", {"position": v(10.64, 17.29) * mm});
            skLineSegment(sketch, "E17.1.2.4", {"start": v(12.85, 17.16) * mm, "end": v(11.47, 18.15) * mm});
            skLineSegment(sketch, "E17.4.2.4", {"start": v(12.35, 16.3) * mm, "end": v(10.8, 17) * mm});
            skArc(sketch, "E17.7.2.4", {"start": v(12.35, 16.3) * mm, "mid": v(13, 16.5) * mm, "end": v(12.85, 17.16) * mm});
            skLineSegment(sketch, "E17.11.2.4", {"start": v(8.43, 16.3) * mm, "end": v(9.98, 17) * mm});
            skArc(sketch, "E17.14.2.4", {"start": v(7.94, 17.16) * mm, "mid": v(7.8, 16.5) * mm, "end": v(8.43, 16.3) * mm});
            skArc(sketch, "E17.18.2.4", {"start": v(10.89, 20.55) * mm, "mid": v(10.4, 21) * mm, "end": v(9.9, 20.55) * mm});
            skPoint(sketch, "E17.22.2.4", {"position": v(11.14, 18.1) * mm});
            skPoint(sketch, "E17.23.2.4", {"position": v(9.94, 18.6) * mm});
            skCircle(sketch, "E17.24.2.4", {"center": v(10.4, 18) * mm, "radius": 0.75 * mm, "construction": true});
            skPoint(sketch, "E17.26.2.4", {"position": v(10.4, 18) * mm});
            skLineSegment(sketch, "E17.27.2.4", {"start": v(10.89, 20.55) * mm, "end": v(11.06, 18.86) * mm});
            skPoint(sketch, "E17.30.2.4", {"position": v(10.1, 17.3) * mm});
            skPoint(sketch, "E17.31.2.4", {"position": v(10.88, 18.57) * mm});
            skPoint(sketch, "E17.32.2.4", {"position": v(9.65, 18.14) * mm});
            skLineSegment(sketch, "E17.33.2.4", {"start": v(7.94, 17.16) * mm, "end": v(9.31, 18.15) * mm});
            skLineSegment(sketch, "E17.36.2.4", {"start": v(9.9, 20.55) * mm, "end": v(9.72, 18.86) * mm});
            skArc(sketch, "E17.39.2.4", {"start": v(10.8, 17) * mm, "mid": v(10.4, 17.08) * mm, "end": v(9.98, 17) * mm});
            skArc(sketch, "E17.43.2.4", {"start": v(9.31, 18.15) * mm, "mid": v(9.6, 18.46) * mm, "end": v(9.72, 18.86) * mm});
            skArc(sketch, "E17.47.2.4", {"start": v(11.06, 18.86) * mm, "mid": v(11.19, 18.46) * mm, "end": v(11.47, 18.15) * mm});
            skPoint(sketch, "E17.0.2.5", {"position": v(10.64, 23.29) * mm});
            skLineSegment(sketch, "E17.1.2.5", {"start": v(12.85, 23.16) * mm, "end": v(11.47, 24.15) * mm});
            skLineSegment(sketch, "E17.4.2.5", {"start": v(12.35, 22.3) * mm, "end": v(10.8, 23) * mm});
            skArc(sketch, "E17.7.2.5", {"start": v(12.35, 22.3) * mm, "mid": v(13, 22.5) * mm, "end": v(12.85, 23.16) * mm});
            skLineSegment(sketch, "E17.11.2.5", {"start": v(8.43, 22.3) * mm, "end": v(9.98, 23) * mm});
            skArc(sketch, "E17.14.2.5", {"start": v(7.94, 23.16) * mm, "mid": v(7.8, 22.5) * mm, "end": v(8.43, 22.3) * mm});
            skArc(sketch, "E17.18.2.5", {"start": v(10.89, 26.55) * mm, "mid": v(10.4, 27) * mm, "end": v(9.9, 26.55) * mm});
            skPoint(sketch, "E17.22.2.5", {"position": v(11.14, 24.1) * mm});
            skPoint(sketch, "E17.23.2.5", {"position": v(9.94, 24.6) * mm});
            skCircle(sketch, "E17.24.2.5", {"center": v(10.4, 24) * mm, "radius": 0.75 * mm, "construction": true});
            skPoint(sketch, "E17.26.2.5", {"position": v(10.4, 24) * mm});
            skLineSegment(sketch, "E17.27.2.5", {"start": v(10.89, 26.55) * mm, "end": v(11.06, 24.86) * mm});
            skPoint(sketch, "E17.30.2.5", {"position": v(10.1, 23.3) * mm});
            skPoint(sketch, "E17.31.2.5", {"position": v(10.88, 24.57) * mm});
            skPoint(sketch, "E17.32.2.5", {"position": v(9.65, 24.14) * mm});
            skLineSegment(sketch, "E17.33.2.5", {"start": v(7.94, 23.16) * mm, "end": v(9.31, 24.15) * mm});
            skLineSegment(sketch, "E17.36.2.5", {"start": v(9.9, 26.55) * mm, "end": v(9.72, 24.86) * mm});
            skArc(sketch, "E17.39.2.5", {"start": v(10.8, 23) * mm, "mid": v(10.4, 23.08) * mm, "end": v(9.98, 23) * mm});
            skArc(sketch, "E17.43.2.5", {"start": v(9.31, 24.15) * mm, "mid": v(9.6, 24.46) * mm, "end": v(9.72, 24.86) * mm});
            skArc(sketch, "E17.47.2.5", {"start": v(11.06, 24.86) * mm, "mid": v(11.19, 24.46) * mm, "end": v(11.47, 24.15) * mm});
            skPoint(sketch, "E17.0.2.6", {"position": v(10.64, 29.29) * mm});
            skLineSegment(sketch, "E17.1.2.6", {"start": v(12.85, 29.16) * mm, "end": v(11.47, 30.15) * mm});
            skLineSegment(sketch, "E17.4.2.6", {"start": v(12.35, 28.3) * mm, "end": v(10.8, 29) * mm});
            skArc(sketch, "E17.7.2.6", {"start": v(12.35, 28.3) * mm, "mid": v(13, 28.5) * mm, "end": v(12.85, 29.16) * mm});
            skLineSegment(sketch, "E17.11.2.6", {"start": v(8.43, 28.3) * mm, "end": v(9.98, 29) * mm});
            skArc(sketch, "E17.14.2.6", {"start": v(7.94, 29.16) * mm, "mid": v(7.8, 28.5) * mm, "end": v(8.43, 28.3) * mm});
            skArc(sketch, "E17.18.2.6", {"start": v(10.89, 32.55) * mm, "mid": v(10.4, 33) * mm, "end": v(9.9, 32.55) * mm});
            skPoint(sketch, "E17.22.2.6", {"position": v(11.14, 30.1) * mm});
            skPoint(sketch, "E17.23.2.6", {"position": v(9.94, 30.6) * mm});
            skCircle(sketch, "E17.24.2.6", {"center": v(10.4, 30) * mm, "radius": 0.75 * mm, "construction": true});
            skPoint(sketch, "E17.26.2.6", {"position": v(10.4, 30) * mm});
            skLineSegment(sketch, "E17.27.2.6", {"start": v(10.89, 32.55) * mm, "end": v(11.06, 30.86) * mm});
            skPoint(sketch, "E17.30.2.6", {"position": v(10.1, 29.3) * mm});
            skPoint(sketch, "E17.31.2.6", {"position": v(10.88, 30.57) * mm});
            skPoint(sketch, "E17.32.2.6", {"position": v(9.65, 30.14) * mm});
            skLineSegment(sketch, "E17.33.2.6", {"start": v(7.94, 29.16) * mm, "end": v(9.31, 30.15) * mm});
            skLineSegment(sketch, "E17.36.2.6", {"start": v(9.9, 32.55) * mm, "end": v(9.72, 30.86) * mm});
            skArc(sketch, "E17.39.2.6", {"start": v(10.8, 29) * mm, "mid": v(10.4, 29.08) * mm, "end": v(9.98, 29) * mm});
            skArc(sketch, "E17.43.2.6", {"start": v(9.31, 30.15) * mm, "mid": v(9.6, 30.46) * mm, "end": v(9.72, 30.86) * mm});
            skArc(sketch, "E17.47.2.6", {"start": v(11.06, 30.86) * mm, "mid": v(11.19, 30.46) * mm, "end": v(11.47, 30.15) * mm});
            skPoint(sketch, "E17.0.2.7", {"position": v(10.64, 35.29) * mm});
            skLineSegment(sketch, "E17.1.2.7", {"start": v(12.85, 35.16) * mm, "end": v(11.47, 36.15) * mm});
            skLineSegment(sketch, "E17.4.2.7", {"start": v(12.35, 34.3) * mm, "end": v(10.8, 35) * mm});
            skArc(sketch, "E17.7.2.7", {"start": v(12.35, 34.3) * mm, "mid": v(13, 34.5) * mm, "end": v(12.85, 35.16) * mm});
            skLineSegment(sketch, "E17.11.2.7", {"start": v(8.43, 34.3) * mm, "end": v(9.98, 35) * mm});
            skArc(sketch, "E17.14.2.7", {"start": v(7.94, 35.16) * mm, "mid": v(7.8, 34.5) * mm, "end": v(8.43, 34.3) * mm});
            skArc(sketch, "E17.18.2.7", {"start": v(10.89, 38.55) * mm, "mid": v(10.4, 39) * mm, "end": v(9.9, 38.55) * mm});
            skPoint(sketch, "E17.22.2.7", {"position": v(11.14, 36.1) * mm});
            skPoint(sketch, "E17.23.2.7", {"position": v(9.94, 36.6) * mm});
            skCircle(sketch, "E17.24.2.7", {"center": v(10.4, 36) * mm, "radius": 0.75 * mm, "construction": true});
            skPoint(sketch, "E17.26.2.7", {"position": v(10.4, 36) * mm});
            skLineSegment(sketch, "E17.27.2.7", {"start": v(10.89, 38.55) * mm, "end": v(11.06, 36.86) * mm});
            skPoint(sketch, "E17.30.2.7", {"position": v(10.1, 35.3) * mm});
            skPoint(sketch, "E17.31.2.7", {"position": v(10.88, 36.57) * mm});
            skPoint(sketch, "E17.32.2.7", {"position": v(9.65, 36.14) * mm});
            skLineSegment(sketch, "E17.33.2.7", {"start": v(7.94, 35.16) * mm, "end": v(9.31, 36.15) * mm});
            skLineSegment(sketch, "E17.36.2.7", {"start": v(9.9, 38.55) * mm, "end": v(9.72, 36.86) * mm});
            skArc(sketch, "E17.39.2.7", {"start": v(10.8, 35) * mm, "mid": v(10.4, 35.08) * mm, "end": v(9.98, 35) * mm});
            skArc(sketch, "E17.43.2.7", {"start": v(9.31, 36.15) * mm, "mid": v(9.6, 36.46) * mm, "end": v(9.72, 36.86) * mm});
            skArc(sketch, "E17.47.2.7", {"start": v(11.06, 36.86) * mm, "mid": v(11.19, 36.46) * mm, "end": v(11.47, 36.15) * mm});
            skPoint(sketch, "E17.0.3.0", {"position": v(15.84, -9.71) * mm});
            skLineSegment(sketch, "E17.1.3.0", {"start": v(18.05, -9.84) * mm, "end": v(16.67, -8.85) * mm});
            skLineSegment(sketch, "E17.4.3.0", {"start": v(17.55, -10.7) * mm, "end": v(16, -10) * mm});
            skArc(sketch, "E17.7.3.0", {"start": v(17.55, -10.7) * mm, "mid": v(18.19, -10.5) * mm, "end": v(18.05, -9.84) * mm});
            skLineSegment(sketch, "E17.11.3.0", {"start": v(13.63, -10.7) * mm, "end": v(15.18, -10) * mm});
            skArc(sketch, "E17.14.3.0", {"start": v(13.13, -9.84) * mm, "mid": v(13, -10.5) * mm, "end": v(13.63, -10.7) * mm});
            skArc(sketch, "E17.18.3.0", {"start": v(16.09, -6.45) * mm, "mid": v(15.59, -6) * mm, "end": v(15.1, -6.45) * mm});
            skPoint(sketch, "E17.22.3.0", {"position": v(16.33, -8.9) * mm});
            skPoint(sketch, "E17.23.3.0", {"position": v(15.13, -8.4) * mm});
            skCircle(sketch, "E17.24.3.0", {"center": v(15.59, -9) * mm, "radius": 0.75 * mm, "construction": true});
            skPoint(sketch, "E17.26.3.0", {"position": v(15.59, -9) * mm});
            skLineSegment(sketch, "E17.27.3.0", {"start": v(16.09, -6.45) * mm, "end": v(16.26, -8.14) * mm});
            skPoint(sketch, "E17.30.3.0", {"position": v(15.3, -9.7) * mm});
            skPoint(sketch, "E17.31.3.0", {"position": v(16.08, -8.43) * mm});
            skPoint(sketch, "E17.32.3.0", {"position": v(14.85, -8.86) * mm});
            skLineSegment(sketch, "E17.33.3.0", {"start": v(13.13, -9.84) * mm, "end": v(14.51, -8.85) * mm});
            skLineSegment(sketch, "E17.36.3.0", {"start": v(15.1, -6.45) * mm, "end": v(14.92, -8.14) * mm});
            skArc(sketch, "E17.39.3.0", {"start": v(16, -10) * mm, "mid": v(15.59, -9.92) * mm, "end": v(15.18, -10) * mm});
            skArc(sketch, "E17.43.3.0", {"start": v(14.51, -8.85) * mm, "mid": v(14.8, -8.54) * mm, "end": v(14.92, -8.14) * mm});
            skArc(sketch, "E17.47.3.0", {"start": v(16.26, -8.14) * mm, "mid": v(16.38, -8.54) * mm, "end": v(16.67, -8.85) * mm});
            skPoint(sketch, "E17.0.3.1", {"position": v(15.84, -3.71) * mm});
            skLineSegment(sketch, "E17.1.3.1", {"start": v(18.05, -3.84) * mm, "end": v(16.67, -2.85) * mm});
            skLineSegment(sketch, "E17.4.3.1", {"start": v(17.55, -4.7) * mm, "end": v(16, -4) * mm});
            skArc(sketch, "E17.7.3.1", {"start": v(17.55, -4.7) * mm, "mid": v(18.19, -4.5) * mm, "end": v(18.05, -3.84) * mm});
            skLineSegment(sketch, "E17.11.3.1", {"start": v(13.63, -4.7) * mm, "end": v(15.18, -4) * mm});
            skArc(sketch, "E17.14.3.1", {"start": v(13.13, -3.84) * mm, "mid": v(13, -4.5) * mm, "end": v(13.63, -4.7) * mm});
            skArc(sketch, "E17.18.3.1", {"start": v(16.09, -0.45) * mm, "mid": v(15.59, 0) * mm, "end": v(15.1, -0.45) * mm});
            skPoint(sketch, "E17.22.3.1", {"position": v(16.33, -2.9) * mm});
            skPoint(sketch, "E17.23.3.1", {"position": v(15.13, -2.4) * mm});
            skCircle(sketch, "E17.24.3.1", {"center": v(15.59, -3) * mm, "radius": 0.75 * mm, "construction": true});
            skPoint(sketch, "E17.26.3.1", {"position": v(15.59, -3) * mm});
            skLineSegment(sketch, "E17.27.3.1", {"start": v(16.09, -0.45) * mm, "end": v(16.26, -2.14) * mm});
            skPoint(sketch, "E17.30.3.1", {"position": v(15.3, -3.7) * mm});
            skPoint(sketch, "E17.31.3.1", {"position": v(16.08, -2.43) * mm});
            skPoint(sketch, "E17.32.3.1", {"position": v(14.85, -2.86) * mm});
            skLineSegment(sketch, "E17.33.3.1", {"start": v(13.13, -3.84) * mm, "end": v(14.51, -2.85) * mm});
            skLineSegment(sketch, "E17.36.3.1", {"start": v(15.1, -0.45) * mm, "end": v(14.92, -2.14) * mm});
            skArc(sketch, "E17.39.3.1", {"start": v(16, -4) * mm, "mid": v(15.59, -3.92) * mm, "end": v(15.18, -4) * mm});
            skArc(sketch, "E17.43.3.1", {"start": v(14.51, -2.85) * mm, "mid": v(14.8, -2.54) * mm, "end": v(14.92, -2.14) * mm});
            skArc(sketch, "E17.47.3.1", {"start": v(16.26, -2.14) * mm, "mid": v(16.38, -2.54) * mm, "end": v(16.67, -2.85) * mm});
            skPoint(sketch, "E17.0.3.2", {"position": v(15.84, 2.29) * mm});
            skLineSegment(sketch, "E17.1.3.2", {"start": v(18.05, 2.16) * mm, "end": v(16.67, 3.15) * mm});
            skLineSegment(sketch, "E17.4.3.2", {"start": v(17.55, 1.3) * mm, "end": v(16, 2) * mm});
            skArc(sketch, "E17.7.3.2", {"start": v(17.55, 1.3) * mm, "mid": v(18.19, 1.5) * mm, "end": v(18.05, 2.16) * mm});
            skLineSegment(sketch, "E17.11.3.2", {"start": v(13.63, 1.3) * mm, "end": v(15.18, 2) * mm});
            skArc(sketch, "E17.14.3.2", {"start": v(13.13, 2.16) * mm, "mid": v(13, 1.5) * mm, "end": v(13.63, 1.3) * mm});
            skArc(sketch, "E17.18.3.2", {"start": v(16.09, 5.55) * mm, "mid": v(15.59, 6) * mm, "end": v(15.1, 5.55) * mm});
            skPoint(sketch, "E17.22.3.2", {"position": v(16.33, 3.1) * mm});
            skPoint(sketch, "E17.23.3.2", {"position": v(15.13, 3.6) * mm});
            skCircle(sketch, "E17.24.3.2", {"center": v(15.59, 3) * mm, "radius": 0.75 * mm, "construction": true});
            skPoint(sketch, "E17.26.3.2", {"position": v(15.59, 3) * mm});
            skLineSegment(sketch, "E17.27.3.2", {"start": v(16.09, 5.55) * mm, "end": v(16.26, 3.86) * mm});
            skPoint(sketch, "E17.30.3.2", {"position": v(15.3, 2.3) * mm});
            skPoint(sketch, "E17.31.3.2", {"position": v(16.08, 3.57) * mm});
            skPoint(sketch, "E17.32.3.2", {"position": v(14.85, 3.14) * mm});
            skLineSegment(sketch, "E17.33.3.2", {"start": v(13.13, 2.16) * mm, "end": v(14.51, 3.15) * mm});
            skLineSegment(sketch, "E17.36.3.2", {"start": v(15.1, 5.55) * mm, "end": v(14.92, 3.86) * mm});
            skArc(sketch, "E17.39.3.2", {"start": v(16, 2) * mm, "mid": v(15.59, 2.08) * mm, "end": v(15.18, 2) * mm});
            skArc(sketch, "E17.43.3.2", {"start": v(14.51, 3.15) * mm, "mid": v(14.8, 3.46) * mm, "end": v(14.92, 3.86) * mm});
            skArc(sketch, "E17.47.3.2", {"start": v(16.26, 3.86) * mm, "mid": v(16.38, 3.46) * mm, "end": v(16.67, 3.15) * mm});
            skPoint(sketch, "E17.0.3.3", {"position": v(15.84, 8.29) * mm});
            skLineSegment(sketch, "E17.1.3.3", {"start": v(18.05, 8.16) * mm, "end": v(16.67, 9.15) * mm});
            skLineSegment(sketch, "E17.4.3.3", {"start": v(17.55, 7.3) * mm, "end": v(16, 8) * mm});
            skArc(sketch, "E17.7.3.3", {"start": v(17.55, 7.3) * mm, "mid": v(18.19, 7.5) * mm, "end": v(18.05, 8.16) * mm});
            skLineSegment(sketch, "E17.11.3.3", {"start": v(13.63, 7.3) * mm, "end": v(15.18, 8) * mm});
            skArc(sketch, "E17.14.3.3", {"start": v(13.13, 8.16) * mm, "mid": v(13, 7.5) * mm, "end": v(13.63, 7.3) * mm});
            skArc(sketch, "E17.18.3.3", {"start": v(16.09, 11.55) * mm, "mid": v(15.59, 12) * mm, "end": v(15.1, 11.55) * mm});
            skPoint(sketch, "E17.22.3.3", {"position": v(16.33, 9.1) * mm});
            skPoint(sketch, "E17.23.3.3", {"position": v(15.13, 9.6) * mm});
            skCircle(sketch, "E17.24.3.3", {"center": v(15.59, 9) * mm, "radius": 0.75 * mm, "construction": true});
            skPoint(sketch, "E17.26.3.3", {"position": v(15.59, 9) * mm});
            skLineSegment(sketch, "E17.27.3.3", {"start": v(16.09, 11.55) * mm, "end": v(16.26, 9.86) * mm});
            skPoint(sketch, "E17.30.3.3", {"position": v(15.3, 8.3) * mm});
            skPoint(sketch, "E17.31.3.3", {"position": v(16.08, 9.57) * mm});
            skPoint(sketch, "E17.32.3.3", {"position": v(14.85, 9.14) * mm});
            skLineSegment(sketch, "E17.33.3.3", {"start": v(13.13, 8.16) * mm, "end": v(14.51, 9.15) * mm});
            skLineSegment(sketch, "E17.36.3.3", {"start": v(15.1, 11.55) * mm, "end": v(14.92, 9.86) * mm});
            skArc(sketch, "E17.39.3.3", {"start": v(16, 8) * mm, "mid": v(15.59, 8.08) * mm, "end": v(15.18, 8) * mm});
            skArc(sketch, "E17.43.3.3", {"start": v(14.51, 9.15) * mm, "mid": v(14.8, 9.46) * mm, "end": v(14.92, 9.86) * mm});
            skArc(sketch, "E17.47.3.3", {"start": v(16.26, 9.86) * mm, "mid": v(16.38, 9.46) * mm, "end": v(16.67, 9.15) * mm});
            skPoint(sketch, "E17.0.3.4", {"position": v(15.84, 14.29) * mm});
            skLineSegment(sketch, "E17.1.3.4", {"start": v(18.05, 14.16) * mm, "end": v(16.67, 15.15) * mm});
            skLineSegment(sketch, "E17.4.3.4", {"start": v(17.55, 13.3) * mm, "end": v(16, 14) * mm});
            skArc(sketch, "E17.7.3.4", {"start": v(17.55, 13.3) * mm, "mid": v(18.19, 13.5) * mm, "end": v(18.05, 14.16) * mm});
            skLineSegment(sketch, "E17.11.3.4", {"start": v(13.63, 13.3) * mm, "end": v(15.18, 14) * mm});
            skArc(sketch, "E17.14.3.4", {"start": v(13.13, 14.16) * mm, "mid": v(13, 13.5) * mm, "end": v(13.63, 13.3) * mm});
            skArc(sketch, "E17.18.3.4", {"start": v(16.09, 17.55) * mm, "mid": v(15.59, 18) * mm, "end": v(15.1, 17.55) * mm});
            skPoint(sketch, "E17.22.3.4", {"position": v(16.33, 15.1) * mm});
            skPoint(sketch, "E17.23.3.4", {"position": v(15.13, 15.6) * mm});
            skCircle(sketch, "E17.24.3.4", {"center": v(15.59, 15) * mm, "radius": 0.75 * mm, "construction": true});
            skPoint(sketch, "E17.26.3.4", {"position": v(15.59, 15) * mm});
            skLineSegment(sketch, "E17.27.3.4", {"start": v(16.09, 17.55) * mm, "end": v(16.26, 15.86) * mm});
            skPoint(sketch, "E17.30.3.4", {"position": v(15.3, 14.3) * mm});
            skPoint(sketch, "E17.31.3.4", {"position": v(16.08, 15.57) * mm});
            skPoint(sketch, "E17.32.3.4", {"position": v(14.85, 15.14) * mm});
            skLineSegment(sketch, "E17.33.3.4", {"start": v(13.13, 14.16) * mm, "end": v(14.51, 15.15) * mm});
            skLineSegment(sketch, "E17.36.3.4", {"start": v(15.1, 17.55) * mm, "end": v(14.92, 15.86) * mm});
            skArc(sketch, "E17.39.3.4", {"start": v(16, 14) * mm, "mid": v(15.59, 14.08) * mm, "end": v(15.18, 14) * mm});
            skArc(sketch, "E17.43.3.4", {"start": v(14.51, 15.15) * mm, "mid": v(14.8, 15.46) * mm, "end": v(14.92, 15.86) * mm});
            skArc(sketch, "E17.47.3.4", {"start": v(16.26, 15.86) * mm, "mid": v(16.38, 15.46) * mm, "end": v(16.67, 15.15) * mm});
            skPoint(sketch, "E17.0.3.5", {"position": v(15.84, 20.29) * mm});
            skLineSegment(sketch, "E17.1.3.5", {"start": v(18.05, 20.16) * mm, "end": v(16.67, 21.15) * mm});
            skLineSegment(sketch, "E17.4.3.5", {"start": v(17.55, 19.3) * mm, "end": v(16, 20) * mm});
            skArc(sketch, "E17.7.3.5", {"start": v(17.55, 19.3) * mm, "mid": v(18.19, 19.5) * mm, "end": v(18.05, 20.16) * mm});
            skLineSegment(sketch, "E17.11.3.5", {"start": v(13.63, 19.3) * mm, "end": v(15.18, 20) * mm});
            skArc(sketch, "E17.14.3.5", {"start": v(13.13, 20.16) * mm, "mid": v(13, 19.5) * mm, "end": v(13.63, 19.3) * mm});
            skArc(sketch, "E17.18.3.5", {"start": v(16.09, 23.55) * mm, "mid": v(15.59, 24) * mm, "end": v(15.1, 23.55) * mm});
            skPoint(sketch, "E17.22.3.5", {"position": v(16.33, 21.1) * mm});
            skPoint(sketch, "E17.23.3.5", {"position": v(15.13, 21.6) * mm});
            skCircle(sketch, "E17.24.3.5", {"center": v(15.59, 21) * mm, "radius": 0.75 * mm, "construction": true});
            skPoint(sketch, "E17.26.3.5", {"position": v(15.59, 21) * mm});
            skLineSegment(sketch, "E17.27.3.5", {"start": v(16.09, 23.55) * mm, "end": v(16.26, 21.86) * mm});
            skPoint(sketch, "E17.30.3.5", {"position": v(15.3, 20.3) * mm});
            skPoint(sketch, "E17.31.3.5", {"position": v(16.08, 21.57) * mm});
            skPoint(sketch, "E17.32.3.5", {"position": v(14.85, 21.14) * mm});
            skLineSegment(sketch, "E17.33.3.5", {"start": v(13.13, 20.16) * mm, "end": v(14.51, 21.15) * mm});
            skLineSegment(sketch, "E17.36.3.5", {"start": v(15.1, 23.55) * mm, "end": v(14.92, 21.86) * mm});
            skArc(sketch, "E17.39.3.5", {"start": v(16, 20) * mm, "mid": v(15.59, 20.08) * mm, "end": v(15.18, 20) * mm});
            skArc(sketch, "E17.43.3.5", {"start": v(14.51, 21.15) * mm, "mid": v(14.8, 21.46) * mm, "end": v(14.92, 21.86) * mm});
            skArc(sketch, "E17.47.3.5", {"start": v(16.26, 21.86) * mm, "mid": v(16.38, 21.46) * mm, "end": v(16.67, 21.15) * mm});
            skPoint(sketch, "E17.0.3.6", {"position": v(15.84, 26.29) * mm});
            skLineSegment(sketch, "E17.1.3.6", {"start": v(18.05, 26.16) * mm, "end": v(16.67, 27.15) * mm});
            skLineSegment(sketch, "E17.4.3.6", {"start": v(17.55, 25.3) * mm, "end": v(16, 26) * mm});
            skArc(sketch, "E17.7.3.6", {"start": v(17.55, 25.3) * mm, "mid": v(18.19, 25.5) * mm, "end": v(18.05, 26.16) * mm});
            skLineSegment(sketch, "E17.11.3.6", {"start": v(13.63, 25.3) * mm, "end": v(15.18, 26) * mm});
            skArc(sketch, "E17.14.3.6", {"start": v(13.13, 26.16) * mm, "mid": v(13, 25.5) * mm, "end": v(13.63, 25.3) * mm});
            skArc(sketch, "E17.18.3.6", {"start": v(16.09, 29.55) * mm, "mid": v(15.59, 30) * mm, "end": v(15.1, 29.55) * mm});
            skPoint(sketch, "E17.22.3.6", {"position": v(16.33, 27.1) * mm});
            skPoint(sketch, "E17.23.3.6", {"position": v(15.13, 27.6) * mm});
            skCircle(sketch, "E17.24.3.6", {"center": v(15.59, 27) * mm, "radius": 0.75 * mm, "construction": true});
            skPoint(sketch, "E17.26.3.6", {"position": v(15.59, 27) * mm});
            skLineSegment(sketch, "E17.27.3.6", {"start": v(16.09, 29.55) * mm, "end": v(16.26, 27.86) * mm});
            skPoint(sketch, "E17.30.3.6", {"position": v(15.3, 26.3) * mm});
            skPoint(sketch, "E17.31.3.6", {"position": v(16.08, 27.57) * mm});
            skPoint(sketch, "E17.32.3.6", {"position": v(14.85, 27.14) * mm});
            skLineSegment(sketch, "E17.33.3.6", {"start": v(13.13, 26.16) * mm, "end": v(14.51, 27.15) * mm});
            skLineSegment(sketch, "E17.36.3.6", {"start": v(15.1, 29.55) * mm, "end": v(14.92, 27.86) * mm});
            skArc(sketch, "E17.39.3.6", {"start": v(16, 26) * mm, "mid": v(15.59, 26.08) * mm, "end": v(15.18, 26) * mm});
            skArc(sketch, "E17.43.3.6", {"start": v(14.51, 27.15) * mm, "mid": v(14.8, 27.46) * mm, "end": v(14.92, 27.86) * mm});
            skArc(sketch, "E17.47.3.6", {"start": v(16.26, 27.86) * mm, "mid": v(16.38, 27.46) * mm, "end": v(16.67, 27.15) * mm});
            skPoint(sketch, "E17.0.3.7", {"position": v(15.84, 32.29) * mm});
            skLineSegment(sketch, "E17.1.3.7", {"start": v(18.05, 32.16) * mm, "end": v(16.67, 33.15) * mm});
            skLineSegment(sketch, "E17.4.3.7", {"start": v(17.55, 31.3) * mm, "end": v(16, 32) * mm});
            skArc(sketch, "E17.7.3.7", {"start": v(17.55, 31.3) * mm, "mid": v(18.19, 31.5) * mm, "end": v(18.05, 32.16) * mm});
            skLineSegment(sketch, "E17.11.3.7", {"start": v(13.63, 31.3) * mm, "end": v(15.18, 32) * mm});
            skArc(sketch, "E17.14.3.7", {"start": v(13.13, 32.16) * mm, "mid": v(13, 31.5) * mm, "end": v(13.63, 31.3) * mm});
            skArc(sketch, "E17.18.3.7", {"start": v(16.09, 35.55) * mm, "mid": v(15.59, 36) * mm, "end": v(15.1, 35.55) * mm});
            skPoint(sketch, "E17.22.3.7", {"position": v(16.33, 33.1) * mm});
            skPoint(sketch, "E17.23.3.7", {"position": v(15.13, 33.6) * mm});
            skCircle(sketch, "E17.24.3.7", {"center": v(15.59, 33) * mm, "radius": 0.75 * mm, "construction": true});
            skPoint(sketch, "E17.26.3.7", {"position": v(15.59, 33) * mm});
            skLineSegment(sketch, "E17.27.3.7", {"start": v(16.09, 35.55) * mm, "end": v(16.26, 33.86) * mm});
            skPoint(sketch, "E17.30.3.7", {"position": v(15.3, 32.3) * mm});
            skPoint(sketch, "E17.31.3.7", {"position": v(16.08, 33.57) * mm});
            skPoint(sketch, "E17.32.3.7", {"position": v(14.85, 33.14) * mm});
            skLineSegment(sketch, "E17.33.3.7", {"start": v(13.13, 32.16) * mm, "end": v(14.51, 33.15) * mm});
            skLineSegment(sketch, "E17.36.3.7", {"start": v(15.1, 35.55) * mm, "end": v(14.92, 33.86) * mm});
            skArc(sketch, "E17.39.3.7", {"start": v(16, 32) * mm, "mid": v(15.59, 32.08) * mm, "end": v(15.18, 32) * mm});
            skArc(sketch, "E17.43.3.7", {"start": v(14.51, 33.15) * mm, "mid": v(14.8, 33.46) * mm, "end": v(14.92, 33.86) * mm});
            skArc(sketch, "E17.47.3.7", {"start": v(16.26, 33.86) * mm, "mid": v(16.38, 33.46) * mm, "end": v(16.67, 33.15) * mm});
            skPoint(sketch, "E17.0.4.0", {"position": v(21.03, -12.71) * mm});
            skLineSegment(sketch, "E17.1.4.0", {"start": v(23.24, -12.84) * mm, "end": v(21.86, -11.85) * mm});
            skLineSegment(sketch, "E17.4.4.0", {"start": v(22.74, -13.7) * mm, "end": v(21.2, -13) * mm});
            skArc(sketch, "E17.7.4.0", {"start": v(22.74, -13.7) * mm, "mid": v(23.38, -13.5) * mm, "end": v(23.24, -12.84) * mm});
            skLineSegment(sketch, "E17.11.4.0", {"start": v(18.82, -13.7) * mm, "end": v(20.37, -13) * mm});
            skArc(sketch, "E17.14.4.0", {"start": v(18.33, -12.84) * mm, "mid": v(18.19, -13.5) * mm, "end": v(18.82, -13.7) * mm});
            skArc(sketch, "E17.18.4.0", {"start": v(21.28, -9.45) * mm, "mid": v(20.78, -9) * mm, "end": v(20.29, -9.45) * mm});
            skPoint(sketch, "E17.22.4.0", {"position": v(21.53, -11.9) * mm});
            skPoint(sketch, "E17.23.4.0", {"position": v(20.33, -11.4) * mm});
            skCircle(sketch, "E17.24.4.0", {"center": v(20.78, -12) * mm, "radius": 0.75 * mm, "construction": true});
            skPoint(sketch, "E17.26.4.0", {"position": v(20.78, -12) * mm});
            skLineSegment(sketch, "E17.27.4.0", {"start": v(21.28, -9.45) * mm, "end": v(21.45, -11.14) * mm});
            skPoint(sketch, "E17.30.4.0", {"position": v(20.5, -12.7) * mm});
            skPoint(sketch, "E17.31.4.0", {"position": v(21.28, -11.43) * mm});
            skPoint(sketch, "E17.32.4.0", {"position": v(20.05, -11.86) * mm});
            skLineSegment(sketch, "E17.33.4.0", {"start": v(18.33, -12.84) * mm, "end": v(19.7, -11.85) * mm});
            skLineSegment(sketch, "E17.36.4.0", {"start": v(20.29, -9.45) * mm, "end": v(20.12, -11.14) * mm});
            skArc(sketch, "E17.39.4.0", {"start": v(21.2, -13) * mm, "mid": v(20.78, -12.92) * mm, "end": v(20.37, -13) * mm});
            skArc(sketch, "E17.43.4.0", {"start": v(19.7, -11.85) * mm, "mid": v(19.99, -11.54) * mm, "end": v(20.12, -11.14) * mm});
            skArc(sketch, "E17.47.4.0", {"start": v(21.45, -11.14) * mm, "mid": v(21.58, -11.54) * mm, "end": v(21.86, -11.85) * mm});
            skPoint(sketch, "E17.0.4.1", {"position": v(21.03, -6.71) * mm});
            skLineSegment(sketch, "E17.1.4.1", {"start": v(23.24, -6.84) * mm, "end": v(21.86, -5.85) * mm});
            skLineSegment(sketch, "E17.4.4.1", {"start": v(22.74, -7.7) * mm, "end": v(21.2, -7) * mm});
            skArc(sketch, "E17.7.4.1", {"start": v(22.74, -7.7) * mm, "mid": v(23.38, -7.5) * mm, "end": v(23.24, -6.84) * mm});
            skLineSegment(sketch, "E17.11.4.1", {"start": v(18.82, -7.7) * mm, "end": v(20.37, -7) * mm});
            skArc(sketch, "E17.14.4.1", {"start": v(18.33, -6.84) * mm, "mid": v(18.19, -7.5) * mm, "end": v(18.82, -7.7) * mm});
            skArc(sketch, "E17.18.4.1", {"start": v(21.28, -3.45) * mm, "mid": v(20.78, -3) * mm, "end": v(20.29, -3.45) * mm});
            skPoint(sketch, "E17.22.4.1", {"position": v(21.53, -5.9) * mm});
            skPoint(sketch, "E17.23.4.1", {"position": v(20.33, -5.4) * mm});
            skCircle(sketch, "E17.24.4.1", {"center": v(20.78, -6) * mm, "radius": 0.75 * mm, "construction": true});
            skPoint(sketch, "E17.26.4.1", {"position": v(20.78, -6) * mm});
            skLineSegment(sketch, "E17.27.4.1", {"start": v(21.28, -3.45) * mm, "end": v(21.45, -5.14) * mm});
            skPoint(sketch, "E17.30.4.1", {"position": v(20.5, -6.7) * mm});
            skPoint(sketch, "E17.31.4.1", {"position": v(21.28, -5.43) * mm});
            skPoint(sketch, "E17.32.4.1", {"position": v(20.05, -5.86) * mm});
            skLineSegment(sketch, "E17.33.4.1", {"start": v(18.33, -6.84) * mm, "end": v(19.7, -5.85) * mm});
            skLineSegment(sketch, "E17.36.4.1", {"start": v(20.29, -3.45) * mm, "end": v(20.12, -5.14) * mm});
            skArc(sketch, "E17.39.4.1", {"start": v(21.2, -7) * mm, "mid": v(20.78, -6.92) * mm, "end": v(20.37, -7) * mm});
            skArc(sketch, "E17.43.4.1", {"start": v(19.7, -5.85) * mm, "mid": v(19.99, -5.54) * mm, "end": v(20.12, -5.14) * mm});
            skArc(sketch, "E17.47.4.1", {"start": v(21.45, -5.14) * mm, "mid": v(21.58, -5.54) * mm, "end": v(21.86, -5.85) * mm});
            skPoint(sketch, "E17.0.4.2", {"position": v(21.03, -0.71) * mm});
            skLineSegment(sketch, "E17.1.4.2", {"start": v(23.24, -0.84) * mm, "end": v(21.86, 0.15) * mm});
            skLineSegment(sketch, "E17.4.4.2", {"start": v(22.74, -1.7) * mm, "end": v(21.2, -1) * mm});
            skArc(sketch, "E17.7.4.2", {"start": v(22.74, -1.7) * mm, "mid": v(23.38, -1.5) * mm, "end": v(23.24, -0.84) * mm});
            skLineSegment(sketch, "E17.11.4.2", {"start": v(18.82, -1.7) * mm, "end": v(20.37, -1) * mm});
            skArc(sketch, "E17.14.4.2", {"start": v(18.33, -0.84) * mm, "mid": v(18.19, -1.5) * mm, "end": v(18.82, -1.7) * mm});
            skArc(sketch, "E17.18.4.2", {"start": v(21.28, 2.55) * mm, "mid": v(20.78, 3) * mm, "end": v(20.29, 2.55) * mm});
            skPoint(sketch, "E17.22.4.2", {"position": v(21.53, 0.1) * mm});
            skPoint(sketch, "E17.23.4.2", {"position": v(20.33, 0.6) * mm});
            skCircle(sketch, "E17.24.4.2", {"center": v(20.78, 0) * mm, "radius": 0.75 * mm, "construction": true});
            skPoint(sketch, "E17.26.4.2", {"position": v(20.78, 0) * mm});
            skLineSegment(sketch, "E17.27.4.2", {"start": v(21.28, 2.55) * mm, "end": v(21.45, 0.86) * mm});
            skPoint(sketch, "E17.30.4.2", {"position": v(20.5, -0.7) * mm});
            skPoint(sketch, "E17.31.4.2", {"position": v(21.28, 0.57) * mm});
            skPoint(sketch, "E17.32.4.2", {"position": v(20.05, 0.14) * mm});
            skLineSegment(sketch, "E17.33.4.2", {"start": v(18.33, -0.84) * mm, "end": v(19.7, 0.15) * mm});
            skLineSegment(sketch, "E17.36.4.2", {"start": v(20.29, 2.55) * mm, "end": v(20.12, 0.86) * mm});
            skArc(sketch, "E17.39.4.2", {"start": v(21.2, -1) * mm, "mid": v(20.78, -0.92) * mm, "end": v(20.37, -1) * mm});
            skArc(sketch, "E17.43.4.2", {"start": v(19.7, 0.15) * mm, "mid": v(19.99, 0.46) * mm, "end": v(20.12, 0.86) * mm});
            skArc(sketch, "E17.47.4.2", {"start": v(21.45, 0.86) * mm, "mid": v(21.58, 0.46) * mm, "end": v(21.86, 0.15) * mm});
            skPoint(sketch, "E17.0.4.3", {"position": v(21.03, 5.29) * mm});
            skLineSegment(sketch, "E17.1.4.3", {"start": v(23.24, 5.16) * mm, "end": v(21.86, 6.15) * mm});
            skLineSegment(sketch, "E17.4.4.3", {"start": v(22.74, 4.3) * mm, "end": v(21.2, 5) * mm});
            skArc(sketch, "E17.7.4.3", {"start": v(22.74, 4.3) * mm, "mid": v(23.38, 4.5) * mm, "end": v(23.24, 5.16) * mm});
            skLineSegment(sketch, "E17.11.4.3", {"start": v(18.82, 4.3) * mm, "end": v(20.37, 5) * mm});
            skArc(sketch, "E17.14.4.3", {"start": v(18.33, 5.16) * mm, "mid": v(18.19, 4.5) * mm, "end": v(18.82, 4.3) * mm});
            skArc(sketch, "E17.18.4.3", {"start": v(21.28, 8.55) * mm, "mid": v(20.78, 9) * mm, "end": v(20.29, 8.55) * mm});
            skPoint(sketch, "E17.22.4.3", {"position": v(21.53, 6.1) * mm});
            skPoint(sketch, "E17.23.4.3", {"position": v(20.33, 6.6) * mm});
            skCircle(sketch, "E17.24.4.3", {"center": v(20.78, 6) * mm, "radius": 0.75 * mm, "construction": true});
            skPoint(sketch, "E17.26.4.3", {"position": v(20.78, 6) * mm});
            skLineSegment(sketch, "E17.27.4.3", {"start": v(21.28, 8.55) * mm, "end": v(21.45, 6.86) * mm});
            skPoint(sketch, "E17.30.4.3", {"position": v(20.5, 5.3) * mm});
            skPoint(sketch, "E17.31.4.3", {"position": v(21.28, 6.57) * mm});
            skPoint(sketch, "E17.32.4.3", {"position": v(20.05, 6.14) * mm});
            skLineSegment(sketch, "E17.33.4.3", {"start": v(18.33, 5.16) * mm, "end": v(19.7, 6.15) * mm});
            skLineSegment(sketch, "E17.36.4.3", {"start": v(20.29, 8.55) * mm, "end": v(20.12, 6.86) * mm});
            skArc(sketch, "E17.39.4.3", {"start": v(21.2, 5) * mm, "mid": v(20.78, 5.08) * mm, "end": v(20.37, 5) * mm});
            skArc(sketch, "E17.43.4.3", {"start": v(19.7, 6.15) * mm, "mid": v(19.99, 6.46) * mm, "end": v(20.12, 6.86) * mm});
            skArc(sketch, "E17.47.4.3", {"start": v(21.45, 6.86) * mm, "mid": v(21.58, 6.46) * mm, "end": v(21.86, 6.15) * mm});
            skPoint(sketch, "E17.0.4.4", {"position": v(21.03, 11.29) * mm});
            skLineSegment(sketch, "E17.1.4.4", {"start": v(23.24, 11.16) * mm, "end": v(21.86, 12.15) * mm});
            skLineSegment(sketch, "E17.4.4.4", {"start": v(22.74, 10.3) * mm, "end": v(21.2, 11) * mm});
            skArc(sketch, "E17.7.4.4", {"start": v(22.74, 10.3) * mm, "mid": v(23.38, 10.5) * mm, "end": v(23.24, 11.16) * mm});
            skLineSegment(sketch, "E17.11.4.4", {"start": v(18.82, 10.3) * mm, "end": v(20.37, 11) * mm});
            skArc(sketch, "E17.14.4.4", {"start": v(18.33, 11.16) * mm, "mid": v(18.19, 10.5) * mm, "end": v(18.82, 10.3) * mm});
            skArc(sketch, "E17.18.4.4", {"start": v(21.28, 14.55) * mm, "mid": v(20.78, 15) * mm, "end": v(20.29, 14.55) * mm});
            skPoint(sketch, "E17.22.4.4", {"position": v(21.53, 12.1) * mm});
            skPoint(sketch, "E17.23.4.4", {"position": v(20.33, 12.6) * mm});
            skCircle(sketch, "E17.24.4.4", {"center": v(20.78, 12) * mm, "radius": 0.75 * mm, "construction": true});
            skPoint(sketch, "E17.26.4.4", {"position": v(20.78, 12) * mm});
            skLineSegment(sketch, "E17.27.4.4", {"start": v(21.28, 14.55) * mm, "end": v(21.45, 12.86) * mm});
            skPoint(sketch, "E17.30.4.4", {"position": v(20.5, 11.3) * mm});
            skPoint(sketch, "E17.31.4.4", {"position": v(21.28, 12.57) * mm});
            skPoint(sketch, "E17.32.4.4", {"position": v(20.05, 12.14) * mm});
            skLineSegment(sketch, "E17.33.4.4", {"start": v(18.33, 11.16) * mm, "end": v(19.7, 12.15) * mm});
            skLineSegment(sketch, "E17.36.4.4", {"start": v(20.29, 14.55) * mm, "end": v(20.12, 12.86) * mm});
            skArc(sketch, "E17.39.4.4", {"start": v(21.2, 11) * mm, "mid": v(20.78, 11.08) * mm, "end": v(20.37, 11) * mm});
            skArc(sketch, "E17.43.4.4", {"start": v(19.7, 12.15) * mm, "mid": v(19.99, 12.46) * mm, "end": v(20.12, 12.86) * mm});
            skArc(sketch, "E17.47.4.4", {"start": v(21.45, 12.86) * mm, "mid": v(21.58, 12.46) * mm, "end": v(21.86, 12.15) * mm});
            skPoint(sketch, "E17.0.4.5", {"position": v(21.03, 17.29) * mm});
            skLineSegment(sketch, "E17.1.4.5", {"start": v(23.24, 17.16) * mm, "end": v(21.86, 18.15) * mm});
            skLineSegment(sketch, "E17.4.4.5", {"start": v(22.74, 16.3) * mm, "end": v(21.2, 17) * mm});
            skArc(sketch, "E17.7.4.5", {"start": v(22.74, 16.3) * mm, "mid": v(23.38, 16.5) * mm, "end": v(23.24, 17.16) * mm});
            skLineSegment(sketch, "E17.11.4.5", {"start": v(18.82, 16.3) * mm, "end": v(20.37, 17) * mm});
            skArc(sketch, "E17.14.4.5", {"start": v(18.33, 17.16) * mm, "mid": v(18.19, 16.5) * mm, "end": v(18.82, 16.3) * mm});
            skArc(sketch, "E17.18.4.5", {"start": v(21.28, 20.55) * mm, "mid": v(20.78, 21) * mm, "end": v(20.29, 20.55) * mm});
            skPoint(sketch, "E17.22.4.5", {"position": v(21.53, 18.1) * mm});
            skPoint(sketch, "E17.23.4.5", {"position": v(20.33, 18.6) * mm});
            skCircle(sketch, "E17.24.4.5", {"center": v(20.78, 18) * mm, "radius": 0.75 * mm, "construction": true});
            skPoint(sketch, "E17.26.4.5", {"position": v(20.78, 18) * mm});
            skLineSegment(sketch, "E17.27.4.5", {"start": v(21.28, 20.55) * mm, "end": v(21.45, 18.86) * mm});
            skPoint(sketch, "E17.30.4.5", {"position": v(20.5, 17.3) * mm});
            skPoint(sketch, "E17.31.4.5", {"position": v(21.28, 18.57) * mm});
            skPoint(sketch, "E17.32.4.5", {"position": v(20.05, 18.14) * mm});
            skLineSegment(sketch, "E17.33.4.5", {"start": v(18.33, 17.16) * mm, "end": v(19.7, 18.15) * mm});
            skLineSegment(sketch, "E17.36.4.5", {"start": v(20.29, 20.55) * mm, "end": v(20.12, 18.86) * mm});
            skArc(sketch, "E17.39.4.5", {"start": v(21.2, 17) * mm, "mid": v(20.78, 17.08) * mm, "end": v(20.37, 17) * mm});
            skArc(sketch, "E17.43.4.5", {"start": v(19.7, 18.15) * mm, "mid": v(19.99, 18.46) * mm, "end": v(20.12, 18.86) * mm});
            skArc(sketch, "E17.47.4.5", {"start": v(21.45, 18.86) * mm, "mid": v(21.58, 18.46) * mm, "end": v(21.86, 18.15) * mm});
            skPoint(sketch, "E17.0.4.6", {"position": v(21.03, 23.29) * mm});
            skLineSegment(sketch, "E17.1.4.6", {"start": v(23.24, 23.16) * mm, "end": v(21.86, 24.15) * mm});
            skLineSegment(sketch, "E17.4.4.6", {"start": v(22.74, 22.3) * mm, "end": v(21.2, 23) * mm});
            skArc(sketch, "E17.7.4.6", {"start": v(22.74, 22.3) * mm, "mid": v(23.38, 22.5) * mm, "end": v(23.24, 23.16) * mm});
            skLineSegment(sketch, "E17.11.4.6", {"start": v(18.82, 22.3) * mm, "end": v(20.37, 23) * mm});
            skArc(sketch, "E17.14.4.6", {"start": v(18.33, 23.16) * mm, "mid": v(18.19, 22.5) * mm, "end": v(18.82, 22.3) * mm});
            skArc(sketch, "E17.18.4.6", {"start": v(21.28, 26.55) * mm, "mid": v(20.78, 27) * mm, "end": v(20.29, 26.55) * mm});
            skPoint(sketch, "E17.22.4.6", {"position": v(21.53, 24.1) * mm});
            skPoint(sketch, "E17.23.4.6", {"position": v(20.33, 24.6) * mm});
            skCircle(sketch, "E17.24.4.6", {"center": v(20.78, 24) * mm, "radius": 0.75 * mm, "construction": true});
            skPoint(sketch, "E17.26.4.6", {"position": v(20.78, 24) * mm});
            skLineSegment(sketch, "E17.27.4.6", {"start": v(21.28, 26.55) * mm, "end": v(21.45, 24.86) * mm});
            skPoint(sketch, "E17.30.4.6", {"position": v(20.5, 23.3) * mm});
            skPoint(sketch, "E17.31.4.6", {"position": v(21.28, 24.57) * mm});
            skPoint(sketch, "E17.32.4.6", {"position": v(20.05, 24.14) * mm});
            skLineSegment(sketch, "E17.33.4.6", {"start": v(18.33, 23.16) * mm, "end": v(19.7, 24.15) * mm});
            skLineSegment(sketch, "E17.36.4.6", {"start": v(20.29, 26.55) * mm, "end": v(20.12, 24.86) * mm});
            skArc(sketch, "E17.39.4.6", {"start": v(21.2, 23) * mm, "mid": v(20.78, 23.08) * mm, "end": v(20.37, 23) * mm});
            skArc(sketch, "E17.43.4.6", {"start": v(19.7, 24.15) * mm, "mid": v(19.99, 24.46) * mm, "end": v(20.12, 24.86) * mm});
            skArc(sketch, "E17.47.4.6", {"start": v(21.45, 24.86) * mm, "mid": v(21.58, 24.46) * mm, "end": v(21.86, 24.15) * mm});
            skPoint(sketch, "E17.0.4.7", {"position": v(21.03, 29.29) * mm});
            skLineSegment(sketch, "E17.1.4.7", {"start": v(23.24, 29.16) * mm, "end": v(21.86, 30.15) * mm});
            skLineSegment(sketch, "E17.4.4.7", {"start": v(22.74, 28.3) * mm, "end": v(21.2, 29) * mm});
            skArc(sketch, "E17.7.4.7", {"start": v(22.74, 28.3) * mm, "mid": v(23.38, 28.5) * mm, "end": v(23.24, 29.16) * mm});
            skLineSegment(sketch, "E17.11.4.7", {"start": v(18.82, 28.3) * mm, "end": v(20.37, 29) * mm});
            skArc(sketch, "E17.14.4.7", {"start": v(18.33, 29.16) * mm, "mid": v(18.19, 28.5) * mm, "end": v(18.82, 28.3) * mm});
            skArc(sketch, "E17.18.4.7", {"start": v(21.28, 32.55) * mm, "mid": v(20.78, 33) * mm, "end": v(20.29, 32.55) * mm});
            skPoint(sketch, "E17.22.4.7", {"position": v(21.53, 30.1) * mm});
            skPoint(sketch, "E17.23.4.7", {"position": v(20.33, 30.6) * mm});
            skCircle(sketch, "E17.24.4.7", {"center": v(20.78, 30) * mm, "radius": 0.75 * mm, "construction": true});
            skPoint(sketch, "E17.26.4.7", {"position": v(20.78, 30) * mm});
            skLineSegment(sketch, "E17.27.4.7", {"start": v(21.28, 32.55) * mm, "end": v(21.45, 30.86) * mm});
            skPoint(sketch, "E17.30.4.7", {"position": v(20.5, 29.3) * mm});
            skPoint(sketch, "E17.31.4.7", {"position": v(21.28, 30.57) * mm});
            skPoint(sketch, "E17.32.4.7", {"position": v(20.05, 30.14) * mm});
            skLineSegment(sketch, "E17.33.4.7", {"start": v(18.33, 29.16) * mm, "end": v(19.7, 30.15) * mm});
            skLineSegment(sketch, "E17.36.4.7", {"start": v(20.29, 32.55) * mm, "end": v(20.12, 30.86) * mm});
            skArc(sketch, "E17.39.4.7", {"start": v(21.2, 29) * mm, "mid": v(20.78, 29.08) * mm, "end": v(20.37, 29) * mm});
            skArc(sketch, "E17.43.4.7", {"start": v(19.7, 30.15) * mm, "mid": v(19.99, 30.46) * mm, "end": v(20.12, 30.86) * mm});
            skArc(sketch, "E17.47.4.7", {"start": v(21.45, 30.86) * mm, "mid": v(21.58, 30.46) * mm, "end": v(21.86, 30.15) * mm});
            skPoint(sketch, "E17.0.5.0", {"position": v(26.23, -15.71) * mm});
            skLineSegment(sketch, "E17.1.5.0", {"start": v(28.44, -15.84) * mm, "end": v(27.06, -14.85) * mm});
            skLineSegment(sketch, "E17.4.5.0", {"start": v(27.94, -16.7) * mm, "end": v(26.4, -16) * mm});
            skArc(sketch, "E17.7.5.0", {"start": v(27.94, -16.7) * mm, "mid": v(28.58, -16.5) * mm, "end": v(28.44, -15.84) * mm});
            skLineSegment(sketch, "E17.11.5.0", {"start": v(24.02, -16.7) * mm, "end": v(25.57, -16) * mm});
            skArc(sketch, "E17.14.5.0", {"start": v(23.52, -15.84) * mm, "mid": v(23.38, -16.5) * mm, "end": v(24.02, -16.7) * mm});
            skArc(sketch, "E17.18.5.0", {"start": v(26.48, -12.45) * mm, "mid": v(25.98, -12) * mm, "end": v(25.48, -12.45) * mm});
            skPoint(sketch, "E17.22.5.0", {"position": v(26.72, -14.9) * mm});
            skPoint(sketch, "E17.23.5.0", {"position": v(25.53, -14.4) * mm});
            skCircle(sketch, "E17.24.5.0", {"center": v(25.98, -15) * mm, "radius": 0.75 * mm, "construction": true});
            skPoint(sketch, "E17.26.5.0", {"position": v(25.98, -15) * mm});
            skLineSegment(sketch, "E17.27.5.0", {"start": v(26.48, -12.45) * mm, "end": v(26.65, -14.14) * mm});
            skPoint(sketch, "E17.30.5.0", {"position": v(25.7, -15.7) * mm});
            skPoint(sketch, "E17.31.5.0", {"position": v(26.47, -14.43) * mm});
            skPoint(sketch, "E17.32.5.0", {"position": v(25.24, -14.86) * mm});
            skLineSegment(sketch, "E17.33.5.0", {"start": v(23.52, -15.84) * mm, "end": v(24.9, -14.85) * mm});
            skLineSegment(sketch, "E17.36.5.0", {"start": v(25.48, -12.45) * mm, "end": v(25.31, -14.14) * mm});
            skArc(sketch, "E17.39.5.0", {"start": v(26.4, -16) * mm, "mid": v(25.98, -15.92) * mm, "end": v(25.57, -16) * mm});
            skArc(sketch, "E17.43.5.0", {"start": v(24.9, -14.85) * mm, "mid": v(25.18, -14.54) * mm, "end": v(25.31, -14.14) * mm});
            skArc(sketch, "E17.47.5.0", {"start": v(26.65, -14.14) * mm, "mid": v(26.78, -14.54) * mm, "end": v(27.06, -14.85) * mm});
            skPoint(sketch, "E17.0.5.1", {"position": v(26.23, -9.71) * mm});
            skLineSegment(sketch, "E17.1.5.1", {"start": v(28.44, -9.84) * mm, "end": v(27.06, -8.85) * mm});
            skLineSegment(sketch, "E17.4.5.1", {"start": v(27.94, -10.7) * mm, "end": v(26.4, -10) * mm});
            skArc(sketch, "E17.7.5.1", {"start": v(27.94, -10.7) * mm, "mid": v(28.58, -10.5) * mm, "end": v(28.44, -9.84) * mm});
            skLineSegment(sketch, "E17.11.5.1", {"start": v(24.02, -10.7) * mm, "end": v(25.57, -10) * mm});
            skArc(sketch, "E17.14.5.1", {"start": v(23.52, -9.84) * mm, "mid": v(23.38, -10.5) * mm, "end": v(24.02, -10.7) * mm});
            skArc(sketch, "E17.18.5.1", {"start": v(26.48, -6.45) * mm, "mid": v(25.98, -6) * mm, "end": v(25.48, -6.45) * mm});
            skPoint(sketch, "E17.22.5.1", {"position": v(26.72, -8.9) * mm});
            skPoint(sketch, "E17.23.5.1", {"position": v(25.53, -8.4) * mm});
            skCircle(sketch, "E17.24.5.1", {"center": v(25.98, -9) * mm, "radius": 0.75 * mm, "construction": true});
            skPoint(sketch, "E17.26.5.1", {"position": v(25.98, -9) * mm});
            skLineSegment(sketch, "E17.27.5.1", {"start": v(26.48, -6.45) * mm, "end": v(26.65, -8.14) * mm});
            skPoint(sketch, "E17.30.5.1", {"position": v(25.7, -9.7) * mm});
            skPoint(sketch, "E17.31.5.1", {"position": v(26.47, -8.43) * mm});
            skPoint(sketch, "E17.32.5.1", {"position": v(25.24, -8.86) * mm});
            skLineSegment(sketch, "E17.33.5.1", {"start": v(23.52, -9.84) * mm, "end": v(24.9, -8.85) * mm});
            skLineSegment(sketch, "E17.36.5.1", {"start": v(25.48, -6.45) * mm, "end": v(25.31, -8.14) * mm});
            skArc(sketch, "E17.39.5.1", {"start": v(26.4, -10) * mm, "mid": v(25.98, -9.92) * mm, "end": v(25.57, -10) * mm});
            skArc(sketch, "E17.43.5.1", {"start": v(24.9, -8.85) * mm, "mid": v(25.18, -8.54) * mm, "end": v(25.31, -8.14) * mm});
            skArc(sketch, "E17.47.5.1", {"start": v(26.65, -8.14) * mm, "mid": v(26.78, -8.54) * mm, "end": v(27.06, -8.85) * mm});
            skPoint(sketch, "E17.0.5.2", {"position": v(26.23, -3.71) * mm});
            skLineSegment(sketch, "E17.1.5.2", {"start": v(28.44, -3.84) * mm, "end": v(27.06, -2.85) * mm});
            skLineSegment(sketch, "E17.4.5.2", {"start": v(27.94, -4.7) * mm, "end": v(26.4, -4) * mm});
            skArc(sketch, "E17.7.5.2", {"start": v(27.94, -4.7) * mm, "mid": v(28.58, -4.5) * mm, "end": v(28.44, -3.84) * mm});
            skLineSegment(sketch, "E17.11.5.2", {"start": v(24.02, -4.7) * mm, "end": v(25.57, -4) * mm});
            skArc(sketch, "E17.14.5.2", {"start": v(23.52, -3.84) * mm, "mid": v(23.38, -4.5) * mm, "end": v(24.02, -4.7) * mm});
            skArc(sketch, "E17.18.5.2", {"start": v(26.48, -0.45) * mm, "mid": v(25.98, 0) * mm, "end": v(25.48, -0.45) * mm});
            skPoint(sketch, "E17.22.5.2", {"position": v(26.72, -2.9) * mm});
            skPoint(sketch, "E17.23.5.2", {"position": v(25.53, -2.4) * mm});
            skCircle(sketch, "E17.24.5.2", {"center": v(25.98, -3) * mm, "radius": 0.75 * mm, "construction": true});
            skPoint(sketch, "E17.26.5.2", {"position": v(25.98, -3) * mm});
            skLineSegment(sketch, "E17.27.5.2", {"start": v(26.48, -0.45) * mm, "end": v(26.65, -2.14) * mm});
            skPoint(sketch, "E17.30.5.2", {"position": v(25.7, -3.7) * mm});
            skPoint(sketch, "E17.31.5.2", {"position": v(26.47, -2.43) * mm});
            skPoint(sketch, "E17.32.5.2", {"position": v(25.24, -2.86) * mm});
            skLineSegment(sketch, "E17.33.5.2", {"start": v(23.52, -3.84) * mm, "end": v(24.9, -2.85) * mm});
            skLineSegment(sketch, "E17.36.5.2", {"start": v(25.48, -0.45) * mm, "end": v(25.31, -2.14) * mm});
            skArc(sketch, "E17.39.5.2", {"start": v(26.4, -4) * mm, "mid": v(25.98, -3.92) * mm, "end": v(25.57, -4) * mm});
            skArc(sketch, "E17.43.5.2", {"start": v(24.9, -2.85) * mm, "mid": v(25.18, -2.54) * mm, "end": v(25.31, -2.14) * mm});
            skArc(sketch, "E17.47.5.2", {"start": v(26.65, -2.14) * mm, "mid": v(26.78, -2.54) * mm, "end": v(27.06, -2.85) * mm});
            skPoint(sketch, "E17.0.5.3", {"position": v(26.23, 2.29) * mm});
            skLineSegment(sketch, "E17.1.5.3", {"start": v(28.44, 2.16) * mm, "end": v(27.06, 3.15) * mm});
            skLineSegment(sketch, "E17.4.5.3", {"start": v(27.94, 1.3) * mm, "end": v(26.4, 2) * mm});
            skArc(sketch, "E17.7.5.3", {"start": v(27.94, 1.3) * mm, "mid": v(28.58, 1.5) * mm, "end": v(28.44, 2.16) * mm});
            skLineSegment(sketch, "E17.11.5.3", {"start": v(24.02, 1.3) * mm, "end": v(25.57, 2) * mm});
            skArc(sketch, "E17.14.5.3", {"start": v(23.52, 2.16) * mm, "mid": v(23.38, 1.5) * mm, "end": v(24.02, 1.3) * mm});
            skArc(sketch, "E17.18.5.3", {"start": v(26.48, 5.55) * mm, "mid": v(25.98, 6) * mm, "end": v(25.48, 5.55) * mm});
            skPoint(sketch, "E17.22.5.3", {"position": v(26.72, 3.1) * mm});
            skPoint(sketch, "E17.23.5.3", {"position": v(25.53, 3.6) * mm});
            skCircle(sketch, "E17.24.5.3", {"center": v(25.98, 3) * mm, "radius": 0.75 * mm, "construction": true});
            skPoint(sketch, "E17.26.5.3", {"position": v(25.98, 3) * mm});
            skLineSegment(sketch, "E17.27.5.3", {"start": v(26.48, 5.55) * mm, "end": v(26.65, 3.86) * mm});
            skPoint(sketch, "E17.30.5.3", {"position": v(25.7, 2.3) * mm});
            skPoint(sketch, "E17.31.5.3", {"position": v(26.47, 3.57) * mm});
            skPoint(sketch, "E17.32.5.3", {"position": v(25.24, 3.14) * mm});
            skLineSegment(sketch, "E17.33.5.3", {"start": v(23.52, 2.16) * mm, "end": v(24.9, 3.15) * mm});
            skLineSegment(sketch, "E17.36.5.3", {"start": v(25.48, 5.55) * mm, "end": v(25.31, 3.86) * mm});
            skArc(sketch, "E17.39.5.3", {"start": v(26.4, 2) * mm, "mid": v(25.98, 2.08) * mm, "end": v(25.57, 2) * mm});
            skArc(sketch, "E17.43.5.3", {"start": v(24.9, 3.15) * mm, "mid": v(25.18, 3.46) * mm, "end": v(25.31, 3.86) * mm});
            skArc(sketch, "E17.47.5.3", {"start": v(26.65, 3.86) * mm, "mid": v(26.78, 3.46) * mm, "end": v(27.06, 3.15) * mm});
            skPoint(sketch, "E17.0.5.4", {"position": v(26.23, 8.29) * mm});
            skLineSegment(sketch, "E17.1.5.4", {"start": v(28.44, 8.16) * mm, "end": v(27.06, 9.15) * mm});
            skLineSegment(sketch, "E17.4.5.4", {"start": v(27.94, 7.3) * mm, "end": v(26.4, 8) * mm});
            skArc(sketch, "E17.7.5.4", {"start": v(27.94, 7.3) * mm, "mid": v(28.58, 7.5) * mm, "end": v(28.44, 8.16) * mm});
            skLineSegment(sketch, "E17.11.5.4", {"start": v(24.02, 7.3) * mm, "end": v(25.57, 8) * mm});
            skArc(sketch, "E17.14.5.4", {"start": v(23.52, 8.16) * mm, "mid": v(23.38, 7.5) * mm, "end": v(24.02, 7.3) * mm});
            skArc(sketch, "E17.18.5.4", {"start": v(26.48, 11.55) * mm, "mid": v(25.98, 12) * mm, "end": v(25.48, 11.55) * mm});
            skPoint(sketch, "E17.22.5.4", {"position": v(26.72, 9.1) * mm});
            skPoint(sketch, "E17.23.5.4", {"position": v(25.53, 9.6) * mm});
            skCircle(sketch, "E17.24.5.4", {"center": v(25.98, 9) * mm, "radius": 0.75 * mm, "construction": true});
            skPoint(sketch, "E17.26.5.4", {"position": v(25.98, 9) * mm});
            skLineSegment(sketch, "E17.27.5.4", {"start": v(26.48, 11.55) * mm, "end": v(26.65, 9.86) * mm});
            skPoint(sketch, "E17.30.5.4", {"position": v(25.7, 8.3) * mm});
            skPoint(sketch, "E17.31.5.4", {"position": v(26.47, 9.57) * mm});
            skPoint(sketch, "E17.32.5.4", {"position": v(25.24, 9.14) * mm});
            skLineSegment(sketch, "E17.33.5.4", {"start": v(23.52, 8.16) * mm, "end": v(24.9, 9.15) * mm});
            skLineSegment(sketch, "E17.36.5.4", {"start": v(25.48, 11.55) * mm, "end": v(25.31, 9.86) * mm});
            skArc(sketch, "E17.39.5.4", {"start": v(26.4, 8) * mm, "mid": v(25.98, 8.08) * mm, "end": v(25.57, 8) * mm});
            skArc(sketch, "E17.43.5.4", {"start": v(24.9, 9.15) * mm, "mid": v(25.18, 9.46) * mm, "end": v(25.31, 9.86) * mm});
            skArc(sketch, "E17.47.5.4", {"start": v(26.65, 9.86) * mm, "mid": v(26.78, 9.46) * mm, "end": v(27.06, 9.15) * mm});
            skPoint(sketch, "E17.0.5.5", {"position": v(26.23, 14.29) * mm});
            skLineSegment(sketch, "E17.1.5.5", {"start": v(28.44, 14.16) * mm, "end": v(27.06, 15.15) * mm});
            skLineSegment(sketch, "E17.4.5.5", {"start": v(27.94, 13.3) * mm, "end": v(26.4, 14) * mm});
            skArc(sketch, "E17.7.5.5", {"start": v(27.94, 13.3) * mm, "mid": v(28.58, 13.5) * mm, "end": v(28.44, 14.16) * mm});
            skLineSegment(sketch, "E17.11.5.5", {"start": v(24.02, 13.3) * mm, "end": v(25.57, 14) * mm});
            skArc(sketch, "E17.14.5.5", {"start": v(23.52, 14.16) * mm, "mid": v(23.38, 13.5) * mm, "end": v(24.02, 13.3) * mm});
            skArc(sketch, "E17.18.5.5", {"start": v(26.48, 17.55) * mm, "mid": v(25.98, 18) * mm, "end": v(25.48, 17.55) * mm});
            skPoint(sketch, "E17.22.5.5", {"position": v(26.72, 15.1) * mm});
            skPoint(sketch, "E17.23.5.5", {"position": v(25.53, 15.6) * mm});
            skCircle(sketch, "E17.24.5.5", {"center": v(25.98, 15) * mm, "radius": 0.75 * mm, "construction": true});
            skPoint(sketch, "E17.26.5.5", {"position": v(25.98, 15) * mm});
            skLineSegment(sketch, "E17.27.5.5", {"start": v(26.48, 17.55) * mm, "end": v(26.65, 15.86) * mm});
            skPoint(sketch, "E17.30.5.5", {"position": v(25.7, 14.3) * mm});
            skPoint(sketch, "E17.31.5.5", {"position": v(26.47, 15.57) * mm});
            skPoint(sketch, "E17.32.5.5", {"position": v(25.24, 15.14) * mm});
            skLineSegment(sketch, "E17.33.5.5", {"start": v(23.52, 14.16) * mm, "end": v(24.9, 15.15) * mm});
            skLineSegment(sketch, "E17.36.5.5", {"start": v(25.48, 17.55) * mm, "end": v(25.31, 15.86) * mm});
            skArc(sketch, "E17.39.5.5", {"start": v(26.4, 14) * mm, "mid": v(25.98, 14.08) * mm, "end": v(25.57, 14) * mm});
            skArc(sketch, "E17.43.5.5", {"start": v(24.9, 15.15) * mm, "mid": v(25.18, 15.46) * mm, "end": v(25.31, 15.86) * mm});
            skArc(sketch, "E17.47.5.5", {"start": v(26.65, 15.86) * mm, "mid": v(26.78, 15.46) * mm, "end": v(27.06, 15.15) * mm});
            skPoint(sketch, "E17.0.5.6", {"position": v(26.23, 20.29) * mm});
            skLineSegment(sketch, "E17.1.5.6", {"start": v(28.44, 20.16) * mm, "end": v(27.06, 21.15) * mm});
            skLineSegment(sketch, "E17.4.5.6", {"start": v(27.94, 19.3) * mm, "end": v(26.4, 20) * mm});
            skArc(sketch, "E17.7.5.6", {"start": v(27.94, 19.3) * mm, "mid": v(28.58, 19.5) * mm, "end": v(28.44, 20.16) * mm});
            skLineSegment(sketch, "E17.11.5.6", {"start": v(24.02, 19.3) * mm, "end": v(25.57, 20) * mm});
            skArc(sketch, "E17.14.5.6", {"start": v(23.52, 20.16) * mm, "mid": v(23.38, 19.5) * mm, "end": v(24.02, 19.3) * mm});
            skArc(sketch, "E17.18.5.6", {"start": v(26.48, 23.55) * mm, "mid": v(25.98, 24) * mm, "end": v(25.48, 23.55) * mm});
            skPoint(sketch, "E17.22.5.6", {"position": v(26.72, 21.1) * mm});
            skPoint(sketch, "E17.23.5.6", {"position": v(25.53, 21.6) * mm});
            skCircle(sketch, "E17.24.5.6", {"center": v(25.98, 21) * mm, "radius": 0.75 * mm, "construction": true});
            skPoint(sketch, "E17.26.5.6", {"position": v(25.98, 21) * mm});
            skLineSegment(sketch, "E17.27.5.6", {"start": v(26.48, 23.55) * mm, "end": v(26.65, 21.86) * mm});
            skPoint(sketch, "E17.30.5.6", {"position": v(25.7, 20.3) * mm});
            skPoint(sketch, "E17.31.5.6", {"position": v(26.47, 21.57) * mm});
            skPoint(sketch, "E17.32.5.6", {"position": v(25.24, 21.14) * mm});
            skLineSegment(sketch, "E17.33.5.6", {"start": v(23.52, 20.16) * mm, "end": v(24.9, 21.15) * mm});
            skLineSegment(sketch, "E17.36.5.6", {"start": v(25.48, 23.55) * mm, "end": v(25.31, 21.86) * mm});
            skArc(sketch, "E17.39.5.6", {"start": v(26.4, 20) * mm, "mid": v(25.98, 20.08) * mm, "end": v(25.57, 20) * mm});
            skArc(sketch, "E17.43.5.6", {"start": v(24.9, 21.15) * mm, "mid": v(25.18, 21.46) * mm, "end": v(25.31, 21.86) * mm});
            skArc(sketch, "E17.47.5.6", {"start": v(26.65, 21.86) * mm, "mid": v(26.78, 21.46) * mm, "end": v(27.06, 21.15) * mm});
            skPoint(sketch, "E17.0.5.7", {"position": v(26.23, 26.29) * mm});
            skLineSegment(sketch, "E17.1.5.7", {"start": v(28.44, 26.16) * mm, "end": v(27.06, 27.15) * mm});
            skLineSegment(sketch, "E17.4.5.7", {"start": v(27.94, 25.3) * mm, "end": v(26.4, 26) * mm});
            skArc(sketch, "E17.7.5.7", {"start": v(27.94, 25.3) * mm, "mid": v(28.58, 25.5) * mm, "end": v(28.44, 26.16) * mm});
            skLineSegment(sketch, "E17.11.5.7", {"start": v(24.02, 25.3) * mm, "end": v(25.57, 26) * mm});
            skArc(sketch, "E17.14.5.7", {"start": v(23.52, 26.16) * mm, "mid": v(23.38, 25.5) * mm, "end": v(24.02, 25.3) * mm});
            skArc(sketch, "E17.18.5.7", {"start": v(26.48, 29.55) * mm, "mid": v(25.98, 30) * mm, "end": v(25.48, 29.55) * mm});
            skPoint(sketch, "E17.22.5.7", {"position": v(26.72, 27.1) * mm});
            skPoint(sketch, "E17.23.5.7", {"position": v(25.53, 27.6) * mm});
            skCircle(sketch, "E17.24.5.7", {"center": v(25.98, 27) * mm, "radius": 0.75 * mm, "construction": true});
            skPoint(sketch, "E17.26.5.7", {"position": v(25.98, 27) * mm});
            skLineSegment(sketch, "E17.27.5.7", {"start": v(26.48, 29.55) * mm, "end": v(26.65, 27.86) * mm});
            skPoint(sketch, "E17.30.5.7", {"position": v(25.7, 26.3) * mm});
            skPoint(sketch, "E17.31.5.7", {"position": v(26.47, 27.57) * mm});
            skPoint(sketch, "E17.32.5.7", {"position": v(25.24, 27.14) * mm});
            skLineSegment(sketch, "E17.33.5.7", {"start": v(23.52, 26.16) * mm, "end": v(24.9, 27.15) * mm});
            skLineSegment(sketch, "E17.36.5.7", {"start": v(25.48, 29.55) * mm, "end": v(25.31, 27.86) * mm});
            skArc(sketch, "E17.39.5.7", {"start": v(26.4, 26) * mm, "mid": v(25.98, 26.08) * mm, "end": v(25.57, 26) * mm});
            skArc(sketch, "E17.43.5.7", {"start": v(24.9, 27.15) * mm, "mid": v(25.18, 27.46) * mm, "end": v(25.31, 27.86) * mm});
            skArc(sketch, "E17.47.5.7", {"start": v(26.65, 27.86) * mm, "mid": v(26.78, 27.46) * mm, "end": v(27.06, 27.15) * mm});
            skPoint(sketch, "E17.0.6.0", {"position": v(31.42, -18.71) * mm});
            skLineSegment(sketch, "E17.1.6.0", {"start": v(33.63, -18.84) * mm, "end": v(32.26, -17.85) * mm});
            skLineSegment(sketch, "E17.4.6.0", {"start": v(33.14, -19.7) * mm, "end": v(31.59, -19) * mm});
            skArc(sketch, "E17.7.6.0", {"start": v(33.14, -19.7) * mm, "mid": v(33.77, -19.5) * mm, "end": v(33.63, -18.84) * mm});
            skLineSegment(sketch, "E17.11.6.0", {"start": v(29.22, -19.7) * mm, "end": v(30.77, -19) * mm});
            skArc(sketch, "E17.14.6.0", {"start": v(28.72, -18.84) * mm, "mid": v(28.58, -19.5) * mm, "end": v(29.22, -19.7) * mm});
            skArc(sketch, "E17.18.6.0", {"start": v(31.67, -15.45) * mm, "mid": v(31.18, -15) * mm, "end": v(30.68, -15.45) * mm});
            skPoint(sketch, "E17.22.6.0", {"position": v(31.92, -17.9) * mm});
            skPoint(sketch, "E17.23.6.0", {"position": v(30.72, -17.4) * mm});
            skCircle(sketch, "E17.24.6.0", {"center": v(31.18, -18) * mm, "radius": 0.75 * mm, "construction": true});
            skPoint(sketch, "E17.26.6.0", {"position": v(31.18, -18) * mm});
            skLineSegment(sketch, "E17.27.6.0", {"start": v(31.67, -15.45) * mm, "end": v(31.84, -17.14) * mm});
            skPoint(sketch, "E17.30.6.0", {"position": v(30.89, -18.7) * mm});
            skPoint(sketch, "E17.31.6.0", {"position": v(31.67, -17.43) * mm});
            skPoint(sketch, "E17.32.6.0", {"position": v(30.44, -17.86) * mm});
            skLineSegment(sketch, "E17.33.6.0", {"start": v(28.72, -18.84) * mm, "end": v(30.1, -17.85) * mm});
            skLineSegment(sketch, "E17.36.6.0", {"start": v(30.68, -15.45) * mm, "end": v(30.5, -17.14) * mm});
            skArc(sketch, "E17.39.6.0", {"start": v(31.59, -19) * mm, "mid": v(31.18, -18.92) * mm, "end": v(30.77, -19) * mm});
            skArc(sketch, "E17.43.6.0", {"start": v(30.1, -17.85) * mm, "mid": v(30.38, -17.54) * mm, "end": v(30.5, -17.14) * mm});
            skArc(sketch, "E17.47.6.0", {"start": v(31.84, -17.14) * mm, "mid": v(31.97, -17.54) * mm, "end": v(32.26, -17.85) * mm});
            skPoint(sketch, "E17.0.6.1", {"position": v(31.42, -12.71) * mm});
            skLineSegment(sketch, "E17.1.6.1", {"start": v(33.63, -12.84) * mm, "end": v(32.26, -11.85) * mm});
            skLineSegment(sketch, "E17.4.6.1", {"start": v(33.14, -13.7) * mm, "end": v(31.59, -13) * mm});
            skArc(sketch, "E17.7.6.1", {"start": v(33.14, -13.7) * mm, "mid": v(33.77, -13.5) * mm, "end": v(33.63, -12.84) * mm});
            skLineSegment(sketch, "E17.11.6.1", {"start": v(29.22, -13.7) * mm, "end": v(30.77, -13) * mm});
            skArc(sketch, "E17.14.6.1", {"start": v(28.72, -12.84) * mm, "mid": v(28.58, -13.5) * mm, "end": v(29.22, -13.7) * mm});
            skArc(sketch, "E17.18.6.1", {"start": v(31.67, -9.45) * mm, "mid": v(31.18, -9) * mm, "end": v(30.68, -9.45) * mm});
            skPoint(sketch, "E17.22.6.1", {"position": v(31.92, -11.9) * mm});
            skPoint(sketch, "E17.23.6.1", {"position": v(30.72, -11.4) * mm});
            skCircle(sketch, "E17.24.6.1", {"center": v(31.18, -12) * mm, "radius": 0.75 * mm, "construction": true});
            skPoint(sketch, "E17.26.6.1", {"position": v(31.18, -12) * mm});
            skLineSegment(sketch, "E17.27.6.1", {"start": v(31.67, -9.45) * mm, "end": v(31.84, -11.14) * mm});
            skPoint(sketch, "E17.30.6.1", {"position": v(30.89, -12.7) * mm});
            skPoint(sketch, "E17.31.6.1", {"position": v(31.67, -11.43) * mm});
            skPoint(sketch, "E17.32.6.1", {"position": v(30.44, -11.86) * mm});
            skLineSegment(sketch, "E17.33.6.1", {"start": v(28.72, -12.84) * mm, "end": v(30.1, -11.85) * mm});
            skLineSegment(sketch, "E17.36.6.1", {"start": v(30.68, -9.45) * mm, "end": v(30.5, -11.14) * mm});
            skArc(sketch, "E17.39.6.1", {"start": v(31.59, -13) * mm, "mid": v(31.18, -12.92) * mm, "end": v(30.77, -13) * mm});
            skArc(sketch, "E17.43.6.1", {"start": v(30.1, -11.85) * mm, "mid": v(30.38, -11.54) * mm, "end": v(30.5, -11.14) * mm});
            skArc(sketch, "E17.47.6.1", {"start": v(31.84, -11.14) * mm, "mid": v(31.97, -11.54) * mm, "end": v(32.26, -11.85) * mm});
            skPoint(sketch, "E17.0.6.2", {"position": v(31.42, -6.71) * mm});
            skLineSegment(sketch, "E17.1.6.2", {"start": v(33.63, -6.84) * mm, "end": v(32.26, -5.85) * mm});
            skLineSegment(sketch, "E17.4.6.2", {"start": v(33.14, -7.7) * mm, "end": v(31.59, -7) * mm});
            skArc(sketch, "E17.7.6.2", {"start": v(33.14, -7.7) * mm, "mid": v(33.77, -7.5) * mm, "end": v(33.63, -6.84) * mm});
            skLineSegment(sketch, "E17.11.6.2", {"start": v(29.22, -7.7) * mm, "end": v(30.77, -7) * mm});
            skArc(sketch, "E17.14.6.2", {"start": v(28.72, -6.84) * mm, "mid": v(28.58, -7.5) * mm, "end": v(29.22, -7.7) * mm});
            skArc(sketch, "E17.18.6.2", {"start": v(31.67, -3.45) * mm, "mid": v(31.18, -3) * mm, "end": v(30.68, -3.45) * mm});
            skPoint(sketch, "E17.22.6.2", {"position": v(31.92, -5.9) * mm});
            skPoint(sketch, "E17.23.6.2", {"position": v(30.72, -5.4) * mm});
            skCircle(sketch, "E17.24.6.2", {"center": v(31.18, -6) * mm, "radius": 0.75 * mm, "construction": true});
            skPoint(sketch, "E17.26.6.2", {"position": v(31.18, -6) * mm});
            skLineSegment(sketch, "E17.27.6.2", {"start": v(31.67, -3.45) * mm, "end": v(31.84, -5.14) * mm});
            skPoint(sketch, "E17.30.6.2", {"position": v(30.89, -6.7) * mm});
            skPoint(sketch, "E17.31.6.2", {"position": v(31.67, -5.43) * mm});
            skPoint(sketch, "E17.32.6.2", {"position": v(30.44, -5.86) * mm});
            skLineSegment(sketch, "E17.33.6.2", {"start": v(28.72, -6.84) * mm, "end": v(30.1, -5.85) * mm});
            skLineSegment(sketch, "E17.36.6.2", {"start": v(30.68, -3.45) * mm, "end": v(30.5, -5.14) * mm});
            skArc(sketch, "E17.39.6.2", {"start": v(31.59, -7) * mm, "mid": v(31.18, -6.92) * mm, "end": v(30.77, -7) * mm});
            skArc(sketch, "E17.43.6.2", {"start": v(30.1, -5.85) * mm, "mid": v(30.38, -5.54) * mm, "end": v(30.5, -5.14) * mm});
            skArc(sketch, "E17.47.6.2", {"start": v(31.84, -5.14) * mm, "mid": v(31.97, -5.54) * mm, "end": v(32.26, -5.85) * mm});
            skPoint(sketch, "E17.0.6.3", {"position": v(31.42, -0.71) * mm});
            skLineSegment(sketch, "E17.1.6.3", {"start": v(33.63, -0.84) * mm, "end": v(32.26, 0.15) * mm});
            skLineSegment(sketch, "E17.4.6.3", {"start": v(33.14, -1.7) * mm, "end": v(31.59, -1) * mm});
            skArc(sketch, "E17.7.6.3", {"start": v(33.14, -1.7) * mm, "mid": v(33.77, -1.5) * mm, "end": v(33.63, -0.84) * mm});
            skLineSegment(sketch, "E17.11.6.3", {"start": v(29.22, -1.7) * mm, "end": v(30.77, -1) * mm});
            skArc(sketch, "E17.14.6.3", {"start": v(28.72, -0.84) * mm, "mid": v(28.58, -1.5) * mm, "end": v(29.22, -1.7) * mm});
            skArc(sketch, "E17.18.6.3", {"start": v(31.67, 2.55) * mm, "mid": v(31.18, 3) * mm, "end": v(30.68, 2.55) * mm});
            skPoint(sketch, "E17.22.6.3", {"position": v(31.92, 0.1) * mm});
            skPoint(sketch, "E17.23.6.3", {"position": v(30.72, 0.6) * mm});
            skCircle(sketch, "E17.24.6.3", {"center": v(31.18, 0) * mm, "radius": 0.75 * mm, "construction": true});
            skPoint(sketch, "E17.26.6.3", {"position": v(31.18, 0) * mm});
            skLineSegment(sketch, "E17.27.6.3", {"start": v(31.67, 2.55) * mm, "end": v(31.84, 0.86) * mm});
            skPoint(sketch, "E17.30.6.3", {"position": v(30.89, -0.7) * mm});
            skPoint(sketch, "E17.31.6.3", {"position": v(31.67, 0.57) * mm});
            skPoint(sketch, "E17.32.6.3", {"position": v(30.44, 0.14) * mm});
            skLineSegment(sketch, "E17.33.6.3", {"start": v(28.72, -0.84) * mm, "end": v(30.1, 0.15) * mm});
            skLineSegment(sketch, "E17.36.6.3", {"start": v(30.68, 2.55) * mm, "end": v(30.5, 0.86) * mm});
            skArc(sketch, "E17.39.6.3", {"start": v(31.59, -1) * mm, "mid": v(31.18, -0.92) * mm, "end": v(30.77, -1) * mm});
            skArc(sketch, "E17.43.6.3", {"start": v(30.1, 0.15) * mm, "mid": v(30.38, 0.46) * mm, "end": v(30.5, 0.86) * mm});
            skArc(sketch, "E17.47.6.3", {"start": v(31.84, 0.86) * mm, "mid": v(31.97, 0.46) * mm, "end": v(32.26, 0.15) * mm});
            skPoint(sketch, "E17.0.6.4", {"position": v(31.42, 5.29) * mm});
            skLineSegment(sketch, "E17.1.6.4", {"start": v(33.63, 5.16) * mm, "end": v(32.26, 6.15) * mm});
            skLineSegment(sketch, "E17.4.6.4", {"start": v(33.14, 4.3) * mm, "end": v(31.59, 5) * mm});
            skArc(sketch, "E17.7.6.4", {"start": v(33.14, 4.3) * mm, "mid": v(33.77, 4.5) * mm, "end": v(33.63, 5.16) * mm});
            skLineSegment(sketch, "E17.11.6.4", {"start": v(29.22, 4.3) * mm, "end": v(30.77, 5) * mm});
            skArc(sketch, "E17.14.6.4", {"start": v(28.72, 5.16) * mm, "mid": v(28.58, 4.5) * mm, "end": v(29.22, 4.3) * mm});
            skArc(sketch, "E17.18.6.4", {"start": v(31.67, 8.55) * mm, "mid": v(31.18, 9) * mm, "end": v(30.68, 8.55) * mm});
            skPoint(sketch, "E17.22.6.4", {"position": v(31.92, 6.1) * mm});
            skPoint(sketch, "E17.23.6.4", {"position": v(30.72, 6.6) * mm});
            skCircle(sketch, "E17.24.6.4", {"center": v(31.18, 6) * mm, "radius": 0.75 * mm, "construction": true});
            skPoint(sketch, "E17.26.6.4", {"position": v(31.18, 6) * mm});
            skLineSegment(sketch, "E17.27.6.4", {"start": v(31.67, 8.55) * mm, "end": v(31.84, 6.86) * mm});
            skPoint(sketch, "E17.30.6.4", {"position": v(30.89, 5.3) * mm});
            skPoint(sketch, "E17.31.6.4", {"position": v(31.67, 6.57) * mm});
            skPoint(sketch, "E17.32.6.4", {"position": v(30.44, 6.14) * mm});
            skLineSegment(sketch, "E17.33.6.4", {"start": v(28.72, 5.16) * mm, "end": v(30.1, 6.15) * mm});
            skLineSegment(sketch, "E17.36.6.4", {"start": v(30.68, 8.55) * mm, "end": v(30.5, 6.86) * mm});
            skArc(sketch, "E17.39.6.4", {"start": v(31.59, 5) * mm, "mid": v(31.18, 5.08) * mm, "end": v(30.77, 5) * mm});
            skArc(sketch, "E17.43.6.4", {"start": v(30.1, 6.15) * mm, "mid": v(30.38, 6.46) * mm, "end": v(30.5, 6.86) * mm});
            skArc(sketch, "E17.47.6.4", {"start": v(31.84, 6.86) * mm, "mid": v(31.97, 6.46) * mm, "end": v(32.26, 6.15) * mm});
            skPoint(sketch, "E17.0.6.5", {"position": v(31.42, 11.29) * mm});
            skLineSegment(sketch, "E17.1.6.5", {"start": v(33.63, 11.16) * mm, "end": v(32.26, 12.15) * mm});
            skLineSegment(sketch, "E17.4.6.5", {"start": v(33.14, 10.3) * mm, "end": v(31.59, 11) * mm});
            skArc(sketch, "E17.7.6.5", {"start": v(33.14, 10.3) * mm, "mid": v(33.77, 10.5) * mm, "end": v(33.63, 11.16) * mm});
            skLineSegment(sketch, "E17.11.6.5", {"start": v(29.22, 10.3) * mm, "end": v(30.77, 11) * mm});
            skArc(sketch, "E17.14.6.5", {"start": v(28.72, 11.16) * mm, "mid": v(28.58, 10.5) * mm, "end": v(29.22, 10.3) * mm});
            skArc(sketch, "E17.18.6.5", {"start": v(31.67, 14.55) * mm, "mid": v(31.18, 15) * mm, "end": v(30.68, 14.55) * mm});
            skPoint(sketch, "E17.22.6.5", {"position": v(31.92, 12.1) * mm});
            skPoint(sketch, "E17.23.6.5", {"position": v(30.72, 12.6) * mm});
            skCircle(sketch, "E17.24.6.5", {"center": v(31.18, 12) * mm, "radius": 0.75 * mm, "construction": true});
            skPoint(sketch, "E17.26.6.5", {"position": v(31.18, 12) * mm});
            skLineSegment(sketch, "E17.27.6.5", {"start": v(31.67, 14.55) * mm, "end": v(31.84, 12.86) * mm});
            skPoint(sketch, "E17.30.6.5", {"position": v(30.89, 11.3) * mm});
            skPoint(sketch, "E17.31.6.5", {"position": v(31.67, 12.57) * mm});
            skPoint(sketch, "E17.32.6.5", {"position": v(30.44, 12.14) * mm});
            skLineSegment(sketch, "E17.33.6.5", {"start": v(28.72, 11.16) * mm, "end": v(30.1, 12.15) * mm});
            skLineSegment(sketch, "E17.36.6.5", {"start": v(30.68, 14.55) * mm, "end": v(30.5, 12.86) * mm});
            skArc(sketch, "E17.39.6.5", {"start": v(31.59, 11) * mm, "mid": v(31.18, 11.08) * mm, "end": v(30.77, 11) * mm});
            skArc(sketch, "E17.43.6.5", {"start": v(30.1, 12.15) * mm, "mid": v(30.38, 12.46) * mm, "end": v(30.5, 12.86) * mm});
            skArc(sketch, "E17.47.6.5", {"start": v(31.84, 12.86) * mm, "mid": v(31.97, 12.46) * mm, "end": v(32.26, 12.15) * mm});
            skPoint(sketch, "E17.0.6.6", {"position": v(31.42, 17.29) * mm});
            skLineSegment(sketch, "E17.1.6.6", {"start": v(33.63, 17.16) * mm, "end": v(32.26, 18.15) * mm});
            skLineSegment(sketch, "E17.4.6.6", {"start": v(33.14, 16.3) * mm, "end": v(31.59, 17) * mm});
            skArc(sketch, "E17.7.6.6", {"start": v(33.14, 16.3) * mm, "mid": v(33.77, 16.5) * mm, "end": v(33.63, 17.16) * mm});
            skLineSegment(sketch, "E17.11.6.6", {"start": v(29.22, 16.3) * mm, "end": v(30.77, 17) * mm});
            skArc(sketch, "E17.14.6.6", {"start": v(28.72, 17.16) * mm, "mid": v(28.58, 16.5) * mm, "end": v(29.22, 16.3) * mm});
            skArc(sketch, "E17.18.6.6", {"start": v(31.67, 20.55) * mm, "mid": v(31.18, 21) * mm, "end": v(30.68, 20.55) * mm});
            skPoint(sketch, "E17.22.6.6", {"position": v(31.92, 18.1) * mm});
            skPoint(sketch, "E17.23.6.6", {"position": v(30.72, 18.6) * mm});
            skCircle(sketch, "E17.24.6.6", {"center": v(31.18, 18) * mm, "radius": 0.75 * mm, "construction": true});
            skPoint(sketch, "E17.26.6.6", {"position": v(31.18, 18) * mm});
            skLineSegment(sketch, "E17.27.6.6", {"start": v(31.67, 20.55) * mm, "end": v(31.84, 18.86) * mm});
            skPoint(sketch, "E17.30.6.6", {"position": v(30.89, 17.3) * mm});
            skPoint(sketch, "E17.31.6.6", {"position": v(31.67, 18.57) * mm});
            skPoint(sketch, "E17.32.6.6", {"position": v(30.44, 18.14) * mm});
            skLineSegment(sketch, "E17.33.6.6", {"start": v(28.72, 17.16) * mm, "end": v(30.1, 18.15) * mm});
            skLineSegment(sketch, "E17.36.6.6", {"start": v(30.68, 20.55) * mm, "end": v(30.5, 18.86) * mm});
            skArc(sketch, "E17.39.6.6", {"start": v(31.59, 17) * mm, "mid": v(31.18, 17.08) * mm, "end": v(30.77, 17) * mm});
            skArc(sketch, "E17.43.6.6", {"start": v(30.1, 18.15) * mm, "mid": v(30.38, 18.46) * mm, "end": v(30.5, 18.86) * mm});
            skArc(sketch, "E17.47.6.6", {"start": v(31.84, 18.86) * mm, "mid": v(31.97, 18.46) * mm, "end": v(32.26, 18.15) * mm});
            skPoint(sketch, "E17.0.6.7", {"position": v(31.42, 23.29) * mm});
            skLineSegment(sketch, "E17.1.6.7", {"start": v(33.63, 23.16) * mm, "end": v(32.26, 24.15) * mm});
            skLineSegment(sketch, "E17.4.6.7", {"start": v(33.14, 22.3) * mm, "end": v(31.59, 23) * mm});
            skArc(sketch, "E17.7.6.7", {"start": v(33.14, 22.3) * mm, "mid": v(33.77, 22.5) * mm, "end": v(33.63, 23.16) * mm});
            skLineSegment(sketch, "E17.11.6.7", {"start": v(29.22, 22.3) * mm, "end": v(30.77, 23) * mm});
            skArc(sketch, "E17.14.6.7", {"start": v(28.72, 23.16) * mm, "mid": v(28.58, 22.5) * mm, "end": v(29.22, 22.3) * mm});
            skArc(sketch, "E17.18.6.7", {"start": v(31.67, 26.55) * mm, "mid": v(31.18, 27) * mm, "end": v(30.68, 26.55) * mm});
            skPoint(sketch, "E17.22.6.7", {"position": v(31.92, 24.1) * mm});
            skPoint(sketch, "E17.23.6.7", {"position": v(30.72, 24.6) * mm});
            skCircle(sketch, "E17.24.6.7", {"center": v(31.18, 24) * mm, "radius": 0.75 * mm, "construction": true});
            skPoint(sketch, "E17.26.6.7", {"position": v(31.18, 24) * mm});
            skLineSegment(sketch, "E17.27.6.7", {"start": v(31.67, 26.55) * mm, "end": v(31.84, 24.86) * mm});
            skPoint(sketch, "E17.30.6.7", {"position": v(30.89, 23.3) * mm});
            skPoint(sketch, "E17.31.6.7", {"position": v(31.67, 24.57) * mm});
            skPoint(sketch, "E17.32.6.7", {"position": v(30.44, 24.14) * mm});
            skLineSegment(sketch, "E17.33.6.7", {"start": v(28.72, 23.16) * mm, "end": v(30.1, 24.15) * mm});
            skLineSegment(sketch, "E17.36.6.7", {"start": v(30.68, 26.55) * mm, "end": v(30.5, 24.86) * mm});
            skArc(sketch, "E17.39.6.7", {"start": v(31.59, 23) * mm, "mid": v(31.18, 23.08) * mm, "end": v(30.77, 23) * mm});
            skArc(sketch, "E17.43.6.7", {"start": v(30.1, 24.15) * mm, "mid": v(30.38, 24.46) * mm, "end": v(30.5, 24.86) * mm});
            skArc(sketch, "E17.47.6.7", {"start": v(31.84, 24.86) * mm, "mid": v(31.97, 24.46) * mm, "end": v(32.26, 24.15) * mm});
            skPoint(sketch, "E17.0.7.0", {"position": v(36.62, -21.71) * mm});
            skLineSegment(sketch, "E17.1.7.0", {"start": v(38.83, -21.84) * mm, "end": v(37.45, -20.85) * mm});
            skLineSegment(sketch, "E17.4.7.0", {"start": v(38.33, -22.7) * mm, "end": v(36.78, -22) * mm});
            skArc(sketch, "E17.7.7.0", {"start": v(38.33, -22.7) * mm, "mid": v(38.97, -22.5) * mm, "end": v(38.83, -21.84) * mm});
            skLineSegment(sketch, "E17.11.7.0", {"start": v(34.41, -22.7) * mm, "end": v(35.96, -22) * mm});
            skArc(sketch, "E17.14.7.0", {"start": v(33.92, -21.84) * mm, "mid": v(33.77, -22.5) * mm, "end": v(34.41, -22.7) * mm});
            skArc(sketch, "E17.18.7.0", {"start": v(36.87, -18.45) * mm, "mid": v(36.37, -18) * mm, "end": v(35.88, -18.45) * mm});
            skPoint(sketch, "E17.22.7.0", {"position": v(37.12, -20.9) * mm});
            skPoint(sketch, "E17.23.7.0", {"position": v(35.92, -20.4) * mm});
            skCircle(sketch, "E17.24.7.0", {"center": v(36.37, -21) * mm, "radius": 0.75 * mm, "construction": true});
            skPoint(sketch, "E17.26.7.0", {"position": v(36.37, -21) * mm});
            skLineSegment(sketch, "E17.27.7.0", {"start": v(36.87, -18.45) * mm, "end": v(37.04, -20.14) * mm});
            skPoint(sketch, "E17.30.7.0", {"position": v(36.08, -21.7) * mm});
            skPoint(sketch, "E17.31.7.0", {"position": v(36.87, -20.43) * mm});
            skPoint(sketch, "E17.32.7.0", {"position": v(35.63, -20.86) * mm});
            skLineSegment(sketch, "E17.33.7.0", {"start": v(33.92, -21.84) * mm, "end": v(35.3, -20.85) * mm});
            skLineSegment(sketch, "E17.36.7.0", {"start": v(35.88, -18.45) * mm, "end": v(35.7, -20.14) * mm});
            skArc(sketch, "E17.39.7.0", {"start": v(36.78, -22) * mm, "mid": v(36.37, -21.92) * mm, "end": v(35.96, -22) * mm});
            skArc(sketch, "E17.43.7.0", {"start": v(35.3, -20.85) * mm, "mid": v(35.58, -20.54) * mm, "end": v(35.7, -20.14) * mm});
            skArc(sketch, "E17.47.7.0", {"start": v(37.04, -20.14) * mm, "mid": v(37.17, -20.54) * mm, "end": v(37.45, -20.85) * mm});
            skPoint(sketch, "E17.0.7.1", {"position": v(36.62, -15.71) * mm});
            skLineSegment(sketch, "E17.1.7.1", {"start": v(38.83, -15.84) * mm, "end": v(37.45, -14.85) * mm});
            skLineSegment(sketch, "E17.4.7.1", {"start": v(38.33, -16.7) * mm, "end": v(36.78, -16) * mm});
            skArc(sketch, "E17.7.7.1", {"start": v(38.33, -16.7) * mm, "mid": v(38.97, -16.5) * mm, "end": v(38.83, -15.84) * mm});
            skLineSegment(sketch, "E17.11.7.1", {"start": v(34.41, -16.7) * mm, "end": v(35.96, -16) * mm});
            skArc(sketch, "E17.14.7.1", {"start": v(33.92, -15.84) * mm, "mid": v(33.77, -16.5) * mm, "end": v(34.41, -16.7) * mm});
            skArc(sketch, "E17.18.7.1", {"start": v(36.87, -12.45) * mm, "mid": v(36.37, -12) * mm, "end": v(35.88, -12.45) * mm});
            skPoint(sketch, "E17.22.7.1", {"position": v(37.12, -14.9) * mm});
            skPoint(sketch, "E17.23.7.1", {"position": v(35.92, -14.4) * mm});
            skCircle(sketch, "E17.24.7.1", {"center": v(36.37, -15) * mm, "radius": 0.75 * mm, "construction": true});
            skPoint(sketch, "E17.26.7.1", {"position": v(36.37, -15) * mm});
            skLineSegment(sketch, "E17.27.7.1", {"start": v(36.87, -12.45) * mm, "end": v(37.04, -14.14) * mm});
            skPoint(sketch, "E17.30.7.1", {"position": v(36.08, -15.7) * mm});
            skPoint(sketch, "E17.31.7.1", {"position": v(36.87, -14.43) * mm});
            skPoint(sketch, "E17.32.7.1", {"position": v(35.63, -14.86) * mm});
            skLineSegment(sketch, "E17.33.7.1", {"start": v(33.92, -15.84) * mm, "end": v(35.3, -14.85) * mm});
            skLineSegment(sketch, "E17.36.7.1", {"start": v(35.88, -12.45) * mm, "end": v(35.7, -14.14) * mm});
            skArc(sketch, "E17.39.7.1", {"start": v(36.78, -16) * mm, "mid": v(36.37, -15.92) * mm, "end": v(35.96, -16) * mm});
            skArc(sketch, "E17.43.7.1", {"start": v(35.3, -14.85) * mm, "mid": v(35.58, -14.54) * mm, "end": v(35.7, -14.14) * mm});
            skArc(sketch, "E17.47.7.1", {"start": v(37.04, -14.14) * mm, "mid": v(37.17, -14.54) * mm, "end": v(37.45, -14.85) * mm});
            skPoint(sketch, "E17.0.7.2", {"position": v(36.62, -9.71) * mm});
            skLineSegment(sketch, "E17.1.7.2", {"start": v(38.83, -9.84) * mm, "end": v(37.45, -8.85) * mm});
            skLineSegment(sketch, "E17.4.7.2", {"start": v(38.33, -10.7) * mm, "end": v(36.78, -10) * mm});
            skArc(sketch, "E17.7.7.2", {"start": v(38.33, -10.7) * mm, "mid": v(38.97, -10.5) * mm, "end": v(38.83, -9.84) * mm});
            skLineSegment(sketch, "E17.11.7.2", {"start": v(34.41, -10.7) * mm, "end": v(35.96, -10) * mm});
            skArc(sketch, "E17.14.7.2", {"start": v(33.92, -9.84) * mm, "mid": v(33.77, -10.5) * mm, "end": v(34.41, -10.7) * mm});
            skArc(sketch, "E17.18.7.2", {"start": v(36.87, -6.45) * mm, "mid": v(36.37, -6) * mm, "end": v(35.88, -6.45) * mm});
            skPoint(sketch, "E17.22.7.2", {"position": v(37.12, -8.9) * mm});
            skPoint(sketch, "E17.23.7.2", {"position": v(35.92, -8.4) * mm});
            skCircle(sketch, "E17.24.7.2", {"center": v(36.37, -9) * mm, "radius": 0.75 * mm, "construction": true});
            skPoint(sketch, "E17.26.7.2", {"position": v(36.37, -9) * mm});
            skLineSegment(sketch, "E17.27.7.2", {"start": v(36.87, -6.45) * mm, "end": v(37.04, -8.14) * mm});
            skPoint(sketch, "E17.30.7.2", {"position": v(36.08, -9.7) * mm});
            skPoint(sketch, "E17.31.7.2", {"position": v(36.87, -8.43) * mm});
            skPoint(sketch, "E17.32.7.2", {"position": v(35.63, -8.86) * mm});
            skLineSegment(sketch, "E17.33.7.2", {"start": v(33.92, -9.84) * mm, "end": v(35.3, -8.85) * mm});
            skLineSegment(sketch, "E17.36.7.2", {"start": v(35.88, -6.45) * mm, "end": v(35.7, -8.14) * mm});
            skArc(sketch, "E17.39.7.2", {"start": v(36.78, -10) * mm, "mid": v(36.37, -9.92) * mm, "end": v(35.96, -10) * mm});
            skArc(sketch, "E17.43.7.2", {"start": v(35.3, -8.85) * mm, "mid": v(35.58, -8.54) * mm, "end": v(35.7, -8.14) * mm});
            skArc(sketch, "E17.47.7.2", {"start": v(37.04, -8.14) * mm, "mid": v(37.17, -8.54) * mm, "end": v(37.45, -8.85) * mm});
            skPoint(sketch, "E17.0.7.3", {"position": v(36.62, -3.71) * mm});
            skLineSegment(sketch, "E17.1.7.3", {"start": v(38.83, -3.84) * mm, "end": v(37.45, -2.85) * mm});
            skLineSegment(sketch, "E17.4.7.3", {"start": v(38.33, -4.7) * mm, "end": v(36.78, -4) * mm});
            skArc(sketch, "E17.7.7.3", {"start": v(38.33, -4.7) * mm, "mid": v(38.97, -4.5) * mm, "end": v(38.83, -3.84) * mm});
            skLineSegment(sketch, "E17.11.7.3", {"start": v(34.41, -4.7) * mm, "end": v(35.96, -4) * mm});
            skArc(sketch, "E17.14.7.3", {"start": v(33.92, -3.84) * mm, "mid": v(33.77, -4.5) * mm, "end": v(34.41, -4.7) * mm});
            skArc(sketch, "E17.18.7.3", {"start": v(36.87, -0.45) * mm, "mid": v(36.37, 0) * mm, "end": v(35.88, -0.45) * mm});
            skPoint(sketch, "E17.22.7.3", {"position": v(37.12, -2.9) * mm});
            skPoint(sketch, "E17.23.7.3", {"position": v(35.92, -2.4) * mm});
            skCircle(sketch, "E17.24.7.3", {"center": v(36.37, -3) * mm, "radius": 0.75 * mm, "construction": true});
            skPoint(sketch, "E17.26.7.3", {"position": v(36.37, -3) * mm});
            skLineSegment(sketch, "E17.27.7.3", {"start": v(36.87, -0.45) * mm, "end": v(37.04, -2.14) * mm});
            skPoint(sketch, "E17.30.7.3", {"position": v(36.08, -3.7) * mm});
            skPoint(sketch, "E17.31.7.3", {"position": v(36.87, -2.43) * mm});
            skPoint(sketch, "E17.32.7.3", {"position": v(35.63, -2.86) * mm});
            skLineSegment(sketch, "E17.33.7.3", {"start": v(33.92, -3.84) * mm, "end": v(35.3, -2.85) * mm});
            skLineSegment(sketch, "E17.36.7.3", {"start": v(35.88, -0.45) * mm, "end": v(35.7, -2.14) * mm});
            skArc(sketch, "E17.39.7.3", {"start": v(36.78, -4) * mm, "mid": v(36.37, -3.92) * mm, "end": v(35.96, -4) * mm});
            skArc(sketch, "E17.43.7.3", {"start": v(35.3, -2.85) * mm, "mid": v(35.58, -2.54) * mm, "end": v(35.7, -2.14) * mm});
            skArc(sketch, "E17.47.7.3", {"start": v(37.04, -2.14) * mm, "mid": v(37.17, -2.54) * mm, "end": v(37.45, -2.85) * mm});
            skPoint(sketch, "E17.0.7.4", {"position": v(36.62, 2.29) * mm});
            skLineSegment(sketch, "E17.1.7.4", {"start": v(38.83, 2.16) * mm, "end": v(37.45, 3.15) * mm});
            skLineSegment(sketch, "E17.4.7.4", {"start": v(38.33, 1.3) * mm, "end": v(36.78, 2) * mm});
            skArc(sketch, "E17.7.7.4", {"start": v(38.33, 1.3) * mm, "mid": v(38.97, 1.5) * mm, "end": v(38.83, 2.16) * mm});
            skLineSegment(sketch, "E17.11.7.4", {"start": v(34.41, 1.3) * mm, "end": v(35.96, 2) * mm});
            skArc(sketch, "E17.14.7.4", {"start": v(33.92, 2.16) * mm, "mid": v(33.77, 1.5) * mm, "end": v(34.41, 1.3) * mm});
            skArc(sketch, "E17.18.7.4", {"start": v(36.87, 5.55) * mm, "mid": v(36.37, 6) * mm, "end": v(35.88, 5.55) * mm});
            skPoint(sketch, "E17.22.7.4", {"position": v(37.12, 3.1) * mm});
            skPoint(sketch, "E17.23.7.4", {"position": v(35.92, 3.6) * mm});
            skCircle(sketch, "E17.24.7.4", {"center": v(36.37, 3) * mm, "radius": 0.75 * mm, "construction": true});
            skPoint(sketch, "E17.26.7.4", {"position": v(36.37, 3) * mm});
            skLineSegment(sketch, "E17.27.7.4", {"start": v(36.87, 5.55) * mm, "end": v(37.04, 3.86) * mm});
            skPoint(sketch, "E17.30.7.4", {"position": v(36.08, 2.3) * mm});
            skPoint(sketch, "E17.31.7.4", {"position": v(36.87, 3.57) * mm});
            skPoint(sketch, "E17.32.7.4", {"position": v(35.63, 3.14) * mm});
            skLineSegment(sketch, "E17.33.7.4", {"start": v(33.92, 2.16) * mm, "end": v(35.3, 3.15) * mm});
            skLineSegment(sketch, "E17.36.7.4", {"start": v(35.88, 5.55) * mm, "end": v(35.7, 3.86) * mm});
            skArc(sketch, "E17.39.7.4", {"start": v(36.78, 2) * mm, "mid": v(36.37, 2.08) * mm, "end": v(35.96, 2) * mm});
            skArc(sketch, "E17.43.7.4", {"start": v(35.3, 3.15) * mm, "mid": v(35.58, 3.46) * mm, "end": v(35.7, 3.86) * mm});
            skArc(sketch, "E17.47.7.4", {"start": v(37.04, 3.86) * mm, "mid": v(37.17, 3.46) * mm, "end": v(37.45, 3.15) * mm});
            skPoint(sketch, "E17.0.7.5", {"position": v(36.62, 8.29) * mm});
            skLineSegment(sketch, "E17.1.7.5", {"start": v(38.83, 8.16) * mm, "end": v(37.45, 9.15) * mm});
            skLineSegment(sketch, "E17.4.7.5", {"start": v(38.33, 7.3) * mm, "end": v(36.78, 8) * mm});
            skArc(sketch, "E17.7.7.5", {"start": v(38.33, 7.3) * mm, "mid": v(38.97, 7.5) * mm, "end": v(38.83, 8.16) * mm});
            skLineSegment(sketch, "E17.11.7.5", {"start": v(34.41, 7.3) * mm, "end": v(35.96, 8) * mm});
            skArc(sketch, "E17.14.7.5", {"start": v(33.92, 8.16) * mm, "mid": v(33.77, 7.5) * mm, "end": v(34.41, 7.3) * mm});
            skArc(sketch, "E17.18.7.5", {"start": v(36.87, 11.55) * mm, "mid": v(36.37, 12) * mm, "end": v(35.88, 11.55) * mm});
            skPoint(sketch, "E17.22.7.5", {"position": v(37.12, 9.1) * mm});
            skPoint(sketch, "E17.23.7.5", {"position": v(35.92, 9.6) * mm});
            skCircle(sketch, "E17.24.7.5", {"center": v(36.37, 9) * mm, "radius": 0.75 * mm, "construction": true});
            skPoint(sketch, "E17.26.7.5", {"position": v(36.37, 9) * mm});
            skLineSegment(sketch, "E17.27.7.5", {"start": v(36.87, 11.55) * mm, "end": v(37.04, 9.86) * mm});
            skPoint(sketch, "E17.30.7.5", {"position": v(36.08, 8.3) * mm});
            skPoint(sketch, "E17.31.7.5", {"position": v(36.87, 9.57) * mm});
            skPoint(sketch, "E17.32.7.5", {"position": v(35.63, 9.14) * mm});
            skLineSegment(sketch, "E17.33.7.5", {"start": v(33.92, 8.16) * mm, "end": v(35.3, 9.15) * mm});
            skLineSegment(sketch, "E17.36.7.5", {"start": v(35.88, 11.55) * mm, "end": v(35.7, 9.86) * mm});
            skArc(sketch, "E17.39.7.5", {"start": v(36.78, 8) * mm, "mid": v(36.37, 8.08) * mm, "end": v(35.96, 8) * mm});
            skArc(sketch, "E17.43.7.5", {"start": v(35.3, 9.15) * mm, "mid": v(35.58, 9.46) * mm, "end": v(35.7, 9.86) * mm});
            skArc(sketch, "E17.47.7.5", {"start": v(37.04, 9.86) * mm, "mid": v(37.17, 9.46) * mm, "end": v(37.45, 9.15) * mm});
            skPoint(sketch, "E17.0.7.6", {"position": v(36.62, 14.29) * mm});
            skLineSegment(sketch, "E17.1.7.6", {"start": v(38.83, 14.16) * mm, "end": v(37.45, 15.15) * mm});
            skLineSegment(sketch, "E17.4.7.6", {"start": v(38.33, 13.3) * mm, "end": v(36.78, 14) * mm});
            skArc(sketch, "E17.7.7.6", {"start": v(38.33, 13.3) * mm, "mid": v(38.97, 13.5) * mm, "end": v(38.83, 14.16) * mm});
            skLineSegment(sketch, "E17.11.7.6", {"start": v(34.41, 13.3) * mm, "end": v(35.96, 14) * mm});
            skArc(sketch, "E17.14.7.6", {"start": v(33.92, 14.16) * mm, "mid": v(33.77, 13.5) * mm, "end": v(34.41, 13.3) * mm});
            skArc(sketch, "E17.18.7.6", {"start": v(36.87, 17.55) * mm, "mid": v(36.37, 18) * mm, "end": v(35.88, 17.55) * mm});
            skPoint(sketch, "E17.22.7.6", {"position": v(37.12, 15.1) * mm});
            skPoint(sketch, "E17.23.7.6", {"position": v(35.92, 15.6) * mm});
            skCircle(sketch, "E17.24.7.6", {"center": v(36.37, 15) * mm, "radius": 0.75 * mm, "construction": true});
            skPoint(sketch, "E17.26.7.6", {"position": v(36.37, 15) * mm});
            skLineSegment(sketch, "E17.27.7.6", {"start": v(36.87, 17.55) * mm, "end": v(37.04, 15.86) * mm});
            skPoint(sketch, "E17.30.7.6", {"position": v(36.08, 14.3) * mm});
            skPoint(sketch, "E17.31.7.6", {"position": v(36.87, 15.57) * mm});
            skPoint(sketch, "E17.32.7.6", {"position": v(35.63, 15.14) * mm});
            skLineSegment(sketch, "E17.33.7.6", {"start": v(33.92, 14.16) * mm, "end": v(35.3, 15.15) * mm});
            skLineSegment(sketch, "E17.36.7.6", {"start": v(35.88, 17.55) * mm, "end": v(35.7, 15.86) * mm});
            skArc(sketch, "E17.39.7.6", {"start": v(36.78, 14) * mm, "mid": v(36.37, 14.08) * mm, "end": v(35.96, 14) * mm});
            skArc(sketch, "E17.43.7.6", {"start": v(35.3, 15.15) * mm, "mid": v(35.58, 15.46) * mm, "end": v(35.7, 15.86) * mm});
            skArc(sketch, "E17.47.7.6", {"start": v(37.04, 15.86) * mm, "mid": v(37.17, 15.46) * mm, "end": v(37.45, 15.15) * mm});
            skPoint(sketch, "E17.0.7.7", {"position": v(36.62, 20.29) * mm});
            skLineSegment(sketch, "E17.1.7.7", {"start": v(38.83, 20.16) * mm, "end": v(37.45, 21.15) * mm});
            skLineSegment(sketch, "E17.4.7.7", {"start": v(38.33, 19.3) * mm, "end": v(36.78, 20) * mm});
            skArc(sketch, "E17.7.7.7", {"start": v(38.33, 19.3) * mm, "mid": v(38.97, 19.5) * mm, "end": v(38.83, 20.16) * mm});
            skLineSegment(sketch, "E17.11.7.7", {"start": v(34.41, 19.3) * mm, "end": v(35.96, 20) * mm});
            skArc(sketch, "E17.14.7.7", {"start": v(33.92, 20.16) * mm, "mid": v(33.77, 19.5) * mm, "end": v(34.41, 19.3) * mm});
            skArc(sketch, "E17.18.7.7", {"start": v(36.87, 23.55) * mm, "mid": v(36.37, 24) * mm, "end": v(35.88, 23.55) * mm});
            skPoint(sketch, "E17.22.7.7", {"position": v(37.12, 21.1) * mm});
            skPoint(sketch, "E17.23.7.7", {"position": v(35.92, 21.6) * mm});
            skCircle(sketch, "E17.24.7.7", {"center": v(36.37, 21) * mm, "radius": 0.75 * mm, "construction": true});
            skPoint(sketch, "E17.26.7.7", {"position": v(36.37, 21) * mm});
            skLineSegment(sketch, "E17.27.7.7", {"start": v(36.87, 23.55) * mm, "end": v(37.04, 21.86) * mm});
            skPoint(sketch, "E17.30.7.7", {"position": v(36.08, 20.3) * mm});
            skPoint(sketch, "E17.31.7.7", {"position": v(36.87, 21.57) * mm});
            skPoint(sketch, "E17.32.7.7", {"position": v(35.63, 21.14) * mm});
            skLineSegment(sketch, "E17.33.7.7", {"start": v(33.92, 20.16) * mm, "end": v(35.3, 21.15) * mm});
            skLineSegment(sketch, "E17.36.7.7", {"start": v(35.88, 23.55) * mm, "end": v(35.7, 21.86) * mm});
            skArc(sketch, "E17.39.7.7", {"start": v(36.78, 20) * mm, "mid": v(36.37, 20.08) * mm, "end": v(35.96, 20) * mm});
            skArc(sketch, "E17.43.7.7", {"start": v(35.3, 21.15) * mm, "mid": v(35.58, 21.46) * mm, "end": v(35.7, 21.86) * mm});
            skArc(sketch, "E17.47.7.7", {"start": v(37.04, 21.86) * mm, "mid": v(37.17, 21.46) * mm, "end": v(37.45, 21.15) * mm});
            skPoint(sketch, "E17.0.8.0", {"position": v(41.82, -24.71) * mm});
            skLineSegment(sketch, "E17.1.8.0", {"start": v(44.03, -24.84) * mm, "end": v(42.65, -23.85) * mm});
            skLineSegment(sketch, "E17.4.8.0", {"start": v(43.53, -25.7) * mm, "end": v(41.98, -25) * mm});
            skArc(sketch, "E17.7.8.0", {"start": v(43.53, -25.7) * mm, "mid": v(44.17, -25.5) * mm, "end": v(44.03, -24.84) * mm});
            skLineSegment(sketch, "E17.11.8.0", {"start": v(39.6, -25.7) * mm, "end": v(41.16, -25) * mm});
            skArc(sketch, "E17.14.8.0", {"start": v(39.11, -24.84) * mm, "mid": v(38.97, -25.5) * mm, "end": v(39.6, -25.7) * mm});
            skArc(sketch, "E17.18.8.0", {"start": v(42.07, -21.45) * mm, "mid": v(41.57, -21) * mm, "end": v(41.07, -21.45) * mm});
            skPoint(sketch, "E17.22.8.0", {"position": v(42.31, -23.9) * mm});
            skPoint(sketch, "E17.23.8.0", {"position": v(41.11, -23.4) * mm});
            skCircle(sketch, "E17.24.8.0", {"center": v(41.57, -24) * mm, "radius": 0.75 * mm, "construction": true});
            skPoint(sketch, "E17.26.8.0", {"position": v(41.57, -24) * mm});
            skLineSegment(sketch, "E17.27.8.0", {"start": v(42.07, -21.45) * mm, "end": v(42.24, -23.14) * mm});
            skPoint(sketch, "E17.30.8.0", {"position": v(41.28, -24.7) * mm});
            skPoint(sketch, "E17.31.8.0", {"position": v(42.06, -23.43) * mm});
            skPoint(sketch, "E17.32.8.0", {"position": v(40.83, -23.86) * mm});
            skLineSegment(sketch, "E17.33.8.0", {"start": v(39.11, -24.84) * mm, "end": v(40.5, -23.85) * mm});
            skLineSegment(sketch, "E17.36.8.0", {"start": v(41.07, -21.45) * mm, "end": v(40.9, -23.14) * mm});
            skArc(sketch, "E17.39.8.0", {"start": v(41.98, -25) * mm, "mid": v(41.57, -24.92) * mm, "end": v(41.16, -25) * mm});
            skArc(sketch, "E17.43.8.0", {"start": v(40.5, -23.85) * mm, "mid": v(40.77, -23.54) * mm, "end": v(40.9, -23.14) * mm});
            skArc(sketch, "E17.47.8.0", {"start": v(42.24, -23.14) * mm, "mid": v(42.37, -23.54) * mm, "end": v(42.65, -23.85) * mm});
            skPoint(sketch, "E17.0.8.1", {"position": v(41.82, -18.71) * mm});
            skLineSegment(sketch, "E17.1.8.1", {"start": v(44.03, -18.84) * mm, "end": v(42.65, -17.85) * mm});
            skLineSegment(sketch, "E17.4.8.1", {"start": v(43.53, -19.7) * mm, "end": v(41.98, -19) * mm});
            skArc(sketch, "E17.7.8.1", {"start": v(43.53, -19.7) * mm, "mid": v(44.17, -19.5) * mm, "end": v(44.03, -18.84) * mm});
            skLineSegment(sketch, "E17.11.8.1", {"start": v(39.6, -19.7) * mm, "end": v(41.16, -19) * mm});
            skArc(sketch, "E17.14.8.1", {"start": v(39.11, -18.84) * mm, "mid": v(38.97, -19.5) * mm, "end": v(39.6, -19.7) * mm});
            skArc(sketch, "E17.18.8.1", {"start": v(42.07, -15.45) * mm, "mid": v(41.57, -15) * mm, "end": v(41.07, -15.45) * mm});
            skPoint(sketch, "E17.22.8.1", {"position": v(42.31, -17.9) * mm});
            skPoint(sketch, "E17.23.8.1", {"position": v(41.11, -17.4) * mm});
            skCircle(sketch, "E17.24.8.1", {"center": v(41.57, -18) * mm, "radius": 0.75 * mm, "construction": true});
            skPoint(sketch, "E17.26.8.1", {"position": v(41.57, -18) * mm});
            skLineSegment(sketch, "E17.27.8.1", {"start": v(42.07, -15.45) * mm, "end": v(42.24, -17.14) * mm});
            skPoint(sketch, "E17.30.8.1", {"position": v(41.28, -18.7) * mm});
            skPoint(sketch, "E17.31.8.1", {"position": v(42.06, -17.43) * mm});
            skPoint(sketch, "E17.32.8.1", {"position": v(40.83, -17.86) * mm});
            skLineSegment(sketch, "E17.33.8.1", {"start": v(39.11, -18.84) * mm, "end": v(40.5, -17.85) * mm});
            skLineSegment(sketch, "E17.36.8.1", {"start": v(41.07, -15.45) * mm, "end": v(40.9, -17.14) * mm});
            skArc(sketch, "E17.39.8.1", {"start": v(41.98, -19) * mm, "mid": v(41.57, -18.92) * mm, "end": v(41.16, -19) * mm});
            skArc(sketch, "E17.43.8.1", {"start": v(40.5, -17.85) * mm, "mid": v(40.77, -17.54) * mm, "end": v(40.9, -17.14) * mm});
            skArc(sketch, "E17.47.8.1", {"start": v(42.24, -17.14) * mm, "mid": v(42.37, -17.54) * mm, "end": v(42.65, -17.85) * mm});
            skPoint(sketch, "E17.0.8.2", {"position": v(41.82, -12.71) * mm});
            skLineSegment(sketch, "E17.1.8.2", {"start": v(44.03, -12.84) * mm, "end": v(42.65, -11.85) * mm});
            skLineSegment(sketch, "E17.4.8.2", {"start": v(43.53, -13.7) * mm, "end": v(41.98, -13) * mm});
            skArc(sketch, "E17.7.8.2", {"start": v(43.53, -13.7) * mm, "mid": v(44.17, -13.5) * mm, "end": v(44.03, -12.84) * mm});
            skLineSegment(sketch, "E17.11.8.2", {"start": v(39.6, -13.7) * mm, "end": v(41.16, -13) * mm});
            skArc(sketch, "E17.14.8.2", {"start": v(39.11, -12.84) * mm, "mid": v(38.97, -13.5) * mm, "end": v(39.6, -13.7) * mm});
            skArc(sketch, "E17.18.8.2", {"start": v(42.07, -9.45) * mm, "mid": v(41.57, -9) * mm, "end": v(41.07, -9.45) * mm});
            skPoint(sketch, "E17.22.8.2", {"position": v(42.31, -11.9) * mm});
            skPoint(sketch, "E17.23.8.2", {"position": v(41.11, -11.4) * mm});
            skCircle(sketch, "E17.24.8.2", {"center": v(41.57, -12) * mm, "radius": 0.75 * mm, "construction": true});
            skPoint(sketch, "E17.26.8.2", {"position": v(41.57, -12) * mm});
            skLineSegment(sketch, "E17.27.8.2", {"start": v(42.07, -9.45) * mm, "end": v(42.24, -11.14) * mm});
            skPoint(sketch, "E17.30.8.2", {"position": v(41.28, -12.7) * mm});
            skPoint(sketch, "E17.31.8.2", {"position": v(42.06, -11.43) * mm});
            skPoint(sketch, "E17.32.8.2", {"position": v(40.83, -11.86) * mm});
            skLineSegment(sketch, "E17.33.8.2", {"start": v(39.11, -12.84) * mm, "end": v(40.5, -11.85) * mm});
            skLineSegment(sketch, "E17.36.8.2", {"start": v(41.07, -9.45) * mm, "end": v(40.9, -11.14) * mm});
            skArc(sketch, "E17.39.8.2", {"start": v(41.98, -13) * mm, "mid": v(41.57, -12.92) * mm, "end": v(41.16, -13) * mm});
            skArc(sketch, "E17.43.8.2", {"start": v(40.5, -11.85) * mm, "mid": v(40.77, -11.54) * mm, "end": v(40.9, -11.14) * mm});
            skArc(sketch, "E17.47.8.2", {"start": v(42.24, -11.14) * mm, "mid": v(42.37, -11.54) * mm, "end": v(42.65, -11.85) * mm});
            skPoint(sketch, "E17.0.8.3", {"position": v(41.82, -6.71) * mm});
            skLineSegment(sketch, "E17.1.8.3", {"start": v(44.03, -6.84) * mm, "end": v(42.65, -5.85) * mm});
            skLineSegment(sketch, "E17.4.8.3", {"start": v(43.53, -7.7) * mm, "end": v(41.98, -7) * mm});
            skArc(sketch, "E17.7.8.3", {"start": v(43.53, -7.7) * mm, "mid": v(44.17, -7.5) * mm, "end": v(44.03, -6.84) * mm});
            skLineSegment(sketch, "E17.11.8.3", {"start": v(39.6, -7.7) * mm, "end": v(41.16, -7) * mm});
            skArc(sketch, "E17.14.8.3", {"start": v(39.11, -6.84) * mm, "mid": v(38.97, -7.5) * mm, "end": v(39.6, -7.7) * mm});
            skArc(sketch, "E17.18.8.3", {"start": v(42.07, -3.45) * mm, "mid": v(41.57, -3) * mm, "end": v(41.07, -3.45) * mm});
            skPoint(sketch, "E17.22.8.3", {"position": v(42.31, -5.9) * mm});
            skPoint(sketch, "E17.23.8.3", {"position": v(41.11, -5.4) * mm});
            skCircle(sketch, "E17.24.8.3", {"center": v(41.57, -6) * mm, "radius": 0.75 * mm, "construction": true});
            skPoint(sketch, "E17.26.8.3", {"position": v(41.57, -6) * mm});
            skLineSegment(sketch, "E17.27.8.3", {"start": v(42.07, -3.45) * mm, "end": v(42.24, -5.14) * mm});
            skPoint(sketch, "E17.30.8.3", {"position": v(41.28, -6.7) * mm});
            skPoint(sketch, "E17.31.8.3", {"position": v(42.06, -5.43) * mm});
            skPoint(sketch, "E17.32.8.3", {"position": v(40.83, -5.86) * mm});
            skLineSegment(sketch, "E17.33.8.3", {"start": v(39.11, -6.84) * mm, "end": v(40.5, -5.85) * mm});
            skLineSegment(sketch, "E17.36.8.3", {"start": v(41.07, -3.45) * mm, "end": v(40.9, -5.14) * mm});
            skArc(sketch, "E17.39.8.3", {"start": v(41.98, -7) * mm, "mid": v(41.57, -6.92) * mm, "end": v(41.16, -7) * mm});
            skArc(sketch, "E17.43.8.3", {"start": v(40.5, -5.85) * mm, "mid": v(40.77, -5.54) * mm, "end": v(40.9, -5.14) * mm});
            skArc(sketch, "E17.47.8.3", {"start": v(42.24, -5.14) * mm, "mid": v(42.37, -5.54) * mm, "end": v(42.65, -5.85) * mm});
            skPoint(sketch, "E17.0.8.4", {"position": v(41.82, -0.71) * mm});
            skLineSegment(sketch, "E17.1.8.4", {"start": v(44.03, -0.84) * mm, "end": v(42.65, 0.15) * mm});
            skLineSegment(sketch, "E17.4.8.4", {"start": v(43.53, -1.7) * mm, "end": v(41.98, -1) * mm});
            skArc(sketch, "E17.7.8.4", {"start": v(43.53, -1.7) * mm, "mid": v(44.17, -1.5) * mm, "end": v(44.03, -0.84) * mm});
            skLineSegment(sketch, "E17.11.8.4", {"start": v(39.6, -1.7) * mm, "end": v(41.16, -1) * mm});
            skArc(sketch, "E17.14.8.4", {"start": v(39.11, -0.84) * mm, "mid": v(38.97, -1.5) * mm, "end": v(39.6, -1.7) * mm});
            skArc(sketch, "E17.18.8.4", {"start": v(42.07, 2.55) * mm, "mid": v(41.57, 3) * mm, "end": v(41.07, 2.55) * mm});
            skPoint(sketch, "E17.22.8.4", {"position": v(42.31, 0.1) * mm});
            skPoint(sketch, "E17.23.8.4", {"position": v(41.11, 0.6) * mm});
            skCircle(sketch, "E17.24.8.4", {"center": v(41.57, 0) * mm, "radius": 0.75 * mm, "construction": true});
            skPoint(sketch, "E17.26.8.4", {"position": v(41.57, 0) * mm});
            skLineSegment(sketch, "E17.27.8.4", {"start": v(42.07, 2.55) * mm, "end": v(42.24, 0.86) * mm});
            skPoint(sketch, "E17.30.8.4", {"position": v(41.28, -0.7) * mm});
            skPoint(sketch, "E17.31.8.4", {"position": v(42.06, 0.57) * mm});
            skPoint(sketch, "E17.32.8.4", {"position": v(40.83, 0.14) * mm});
            skLineSegment(sketch, "E17.33.8.4", {"start": v(39.11, -0.84) * mm, "end": v(40.5, 0.15) * mm});
            skLineSegment(sketch, "E17.36.8.4", {"start": v(41.07, 2.55) * mm, "end": v(40.9, 0.86) * mm});
            skArc(sketch, "E17.39.8.4", {"start": v(41.98, -1) * mm, "mid": v(41.57, -0.92) * mm, "end": v(41.16, -1) * mm});
            skArc(sketch, "E17.43.8.4", {"start": v(40.5, 0.15) * mm, "mid": v(40.77, 0.46) * mm, "end": v(40.9, 0.86) * mm});
            skArc(sketch, "E17.47.8.4", {"start": v(42.24, 0.86) * mm, "mid": v(42.37, 0.46) * mm, "end": v(42.65, 0.15) * mm});
            skPoint(sketch, "E17.0.8.5", {"position": v(41.82, 5.29) * mm});
            skLineSegment(sketch, "E17.1.8.5", {"start": v(44.03, 5.16) * mm, "end": v(42.65, 6.15) * mm});
            skLineSegment(sketch, "E17.4.8.5", {"start": v(43.53, 4.3) * mm, "end": v(41.98, 5) * mm});
            skArc(sketch, "E17.7.8.5", {"start": v(43.53, 4.3) * mm, "mid": v(44.17, 4.5) * mm, "end": v(44.03, 5.16) * mm});
            skLineSegment(sketch, "E17.11.8.5", {"start": v(39.6, 4.3) * mm, "end": v(41.16, 5) * mm});
            skArc(sketch, "E17.14.8.5", {"start": v(39.11, 5.16) * mm, "mid": v(38.97, 4.5) * mm, "end": v(39.6, 4.3) * mm});
            skArc(sketch, "E17.18.8.5", {"start": v(42.07, 8.55) * mm, "mid": v(41.57, 9) * mm, "end": v(41.07, 8.55) * mm});
            skPoint(sketch, "E17.22.8.5", {"position": v(42.31, 6.1) * mm});
            skPoint(sketch, "E17.23.8.5", {"position": v(41.11, 6.6) * mm});
            skCircle(sketch, "E17.24.8.5", {"center": v(41.57, 6) * mm, "radius": 0.75 * mm, "construction": true});
            skPoint(sketch, "E17.26.8.5", {"position": v(41.57, 6) * mm});
            skLineSegment(sketch, "E17.27.8.5", {"start": v(42.07, 8.55) * mm, "end": v(42.24, 6.86) * mm});
            skPoint(sketch, "E17.30.8.5", {"position": v(41.28, 5.3) * mm});
            skPoint(sketch, "E17.31.8.5", {"position": v(42.06, 6.57) * mm});
            skPoint(sketch, "E17.32.8.5", {"position": v(40.83, 6.14) * mm});
            skLineSegment(sketch, "E17.33.8.5", {"start": v(39.11, 5.16) * mm, "end": v(40.5, 6.15) * mm});
            skLineSegment(sketch, "E17.36.8.5", {"start": v(41.07, 8.55) * mm, "end": v(40.9, 6.86) * mm});
            skArc(sketch, "E17.39.8.5", {"start": v(41.98, 5) * mm, "mid": v(41.57, 5.08) * mm, "end": v(41.16, 5) * mm});
            skArc(sketch, "E17.43.8.5", {"start": v(40.5, 6.15) * mm, "mid": v(40.77, 6.46) * mm, "end": v(40.9, 6.86) * mm});
            skArc(sketch, "E17.47.8.5", {"start": v(42.24, 6.86) * mm, "mid": v(42.37, 6.46) * mm, "end": v(42.65, 6.15) * mm});
            skPoint(sketch, "E17.0.8.6", {"position": v(41.82, 11.29) * mm});
            skLineSegment(sketch, "E17.1.8.6", {"start": v(44.03, 11.16) * mm, "end": v(42.65, 12.15) * mm});
            skLineSegment(sketch, "E17.4.8.6", {"start": v(43.53, 10.3) * mm, "end": v(41.98, 11) * mm});
            skArc(sketch, "E17.7.8.6", {"start": v(43.53, 10.3) * mm, "mid": v(44.17, 10.5) * mm, "end": v(44.03, 11.16) * mm});
            skLineSegment(sketch, "E17.11.8.6", {"start": v(39.6, 10.3) * mm, "end": v(41.16, 11) * mm});
            skArc(sketch, "E17.14.8.6", {"start": v(39.11, 11.16) * mm, "mid": v(38.97, 10.5) * mm, "end": v(39.6, 10.3) * mm});
            skArc(sketch, "E17.18.8.6", {"start": v(42.07, 14.55) * mm, "mid": v(41.57, 15) * mm, "end": v(41.07, 14.55) * mm});
            skPoint(sketch, "E17.22.8.6", {"position": v(42.31, 12.1) * mm});
            skPoint(sketch, "E17.23.8.6", {"position": v(41.11, 12.6) * mm});
            skCircle(sketch, "E17.24.8.6", {"center": v(41.57, 12) * mm, "radius": 0.75 * mm, "construction": true});
            skPoint(sketch, "E17.26.8.6", {"position": v(41.57, 12) * mm});
            skLineSegment(sketch, "E17.27.8.6", {"start": v(42.07, 14.55) * mm, "end": v(42.24, 12.86) * mm});
            skPoint(sketch, "E17.30.8.6", {"position": v(41.28, 11.3) * mm});
            skPoint(sketch, "E17.31.8.6", {"position": v(42.06, 12.57) * mm});
            skPoint(sketch, "E17.32.8.6", {"position": v(40.83, 12.14) * mm});
            skLineSegment(sketch, "E17.33.8.6", {"start": v(39.11, 11.16) * mm, "end": v(40.5, 12.15) * mm});
            skLineSegment(sketch, "E17.36.8.6", {"start": v(41.07, 14.55) * mm, "end": v(40.9, 12.86) * mm});
            skArc(sketch, "E17.39.8.6", {"start": v(41.98, 11) * mm, "mid": v(41.57, 11.08) * mm, "end": v(41.16, 11) * mm});
            skArc(sketch, "E17.43.8.6", {"start": v(40.5, 12.15) * mm, "mid": v(40.77, 12.46) * mm, "end": v(40.9, 12.86) * mm});
            skArc(sketch, "E17.47.8.6", {"start": v(42.24, 12.86) * mm, "mid": v(42.37, 12.46) * mm, "end": v(42.65, 12.15) * mm});
            skPoint(sketch, "E17.0.8.7", {"position": v(41.82, 17.29) * mm});
            skLineSegment(sketch, "E17.1.8.7", {"start": v(44.03, 17.16) * mm, "end": v(42.65, 18.15) * mm});
            skLineSegment(sketch, "E17.4.8.7", {"start": v(43.53, 16.3) * mm, "end": v(41.98, 17) * mm});
            skArc(sketch, "E17.7.8.7", {"start": v(43.53, 16.3) * mm, "mid": v(44.17, 16.5) * mm, "end": v(44.03, 17.16) * mm});
            skLineSegment(sketch, "E17.11.8.7", {"start": v(39.6, 16.3) * mm, "end": v(41.16, 17) * mm});
            skArc(sketch, "E17.14.8.7", {"start": v(39.11, 17.16) * mm, "mid": v(38.97, 16.5) * mm, "end": v(39.6, 16.3) * mm});
            skArc(sketch, "E17.18.8.7", {"start": v(42.07, 20.55) * mm, "mid": v(41.57, 21) * mm, "end": v(41.07, 20.55) * mm});
            skPoint(sketch, "E17.22.8.7", {"position": v(42.31, 18.1) * mm});
            skPoint(sketch, "E17.23.8.7", {"position": v(41.11, 18.6) * mm});
            skCircle(sketch, "E17.24.8.7", {"center": v(41.57, 18) * mm, "radius": 0.75 * mm, "construction": true});
            skPoint(sketch, "E17.26.8.7", {"position": v(41.57, 18) * mm});
            skLineSegment(sketch, "E17.27.8.7", {"start": v(42.07, 20.55) * mm, "end": v(42.24, 18.86) * mm});
            skPoint(sketch, "E17.30.8.7", {"position": v(41.28, 17.3) * mm});
            skPoint(sketch, "E17.31.8.7", {"position": v(42.06, 18.57) * mm});
            skPoint(sketch, "E17.32.8.7", {"position": v(40.83, 18.14) * mm});
            skLineSegment(sketch, "E17.33.8.7", {"start": v(39.11, 17.16) * mm, "end": v(40.5, 18.15) * mm});
            skLineSegment(sketch, "E17.36.8.7", {"start": v(41.07, 20.55) * mm, "end": v(40.9, 18.86) * mm});
            skArc(sketch, "E17.39.8.7", {"start": v(41.98, 17) * mm, "mid": v(41.57, 17.08) * mm, "end": v(41.16, 17) * mm});
            skArc(sketch, "E17.43.8.7", {"start": v(40.5, 18.15) * mm, "mid": v(40.77, 18.46) * mm, "end": v(40.9, 18.86) * mm});
            skArc(sketch, "E17.47.8.7", {"start": v(42.24, 18.86) * mm, "mid": v(42.37, 18.46) * mm, "end": v(42.65, 18.15) * mm});
            skPoint(sketch, "E17.0.9.0", {"position": v(47.01, -27.71) * mm});
            skLineSegment(sketch, "E17.1.9.0", {"start": v(49.22, -27.84) * mm, "end": v(47.84, -26.85) * mm});
            skLineSegment(sketch, "E17.4.9.0", {"start": v(48.72, -28.7) * mm, "end": v(47.18, -28) * mm});
            skArc(sketch, "E17.7.9.0", {"start": v(48.72, -28.7) * mm, "mid": v(49.36, -28.5) * mm, "end": v(49.22, -27.84) * mm});
            skLineSegment(sketch, "E17.11.9.0", {"start": v(44.8, -28.7) * mm, "end": v(46.35, -28) * mm});
            skArc(sketch, "E17.14.9.0", {"start": v(44.3, -27.84) * mm, "mid": v(44.17, -28.5) * mm, "end": v(44.8, -28.7) * mm});
            skArc(sketch, "E17.18.9.0", {"start": v(47.26, -24.45) * mm, "mid": v(46.77, -24) * mm, "end": v(46.27, -24.45) * mm});
            skPoint(sketch, "E17.22.9.0", {"position": v(47.5, -26.9) * mm});
            skPoint(sketch, "E17.23.9.0", {"position": v(46.31, -26.4) * mm});
            skCircle(sketch, "E17.24.9.0", {"center": v(46.77, -27) * mm, "radius": 0.75 * mm, "construction": true});
            skPoint(sketch, "E17.26.9.0", {"position": v(46.77, -27) * mm});
            skLineSegment(sketch, "E17.27.9.0", {"start": v(47.26, -24.45) * mm, "end": v(47.43, -26.14) * mm});
            skPoint(sketch, "E17.30.9.0", {"position": v(46.48, -27.7) * mm});
            skPoint(sketch, "E17.31.9.0", {"position": v(47.26, -26.43) * mm});
            skPoint(sketch, "E17.32.9.0", {"position": v(46.03, -26.86) * mm});
            skLineSegment(sketch, "E17.33.9.0", {"start": v(44.3, -27.84) * mm, "end": v(45.69, -26.85) * mm});
            skLineSegment(sketch, "E17.36.9.0", {"start": v(46.27, -24.45) * mm, "end": v(46.1, -26.14) * mm});
            skArc(sketch, "E17.39.9.0", {"start": v(47.18, -28) * mm, "mid": v(46.77, -27.92) * mm, "end": v(46.35, -28) * mm});
            skArc(sketch, "E17.43.9.0", {"start": v(45.69, -26.85) * mm, "mid": v(45.97, -26.54) * mm, "end": v(46.1, -26.14) * mm});
            skArc(sketch, "E17.47.9.0", {"start": v(47.43, -26.14) * mm, "mid": v(47.56, -26.54) * mm, "end": v(47.84, -26.85) * mm});
            skPoint(sketch, "E17.0.9.1", {"position": v(47.01, -21.71) * mm});
            skLineSegment(sketch, "E17.1.9.1", {"start": v(49.22, -21.84) * mm, "end": v(47.84, -20.85) * mm});
            skLineSegment(sketch, "E17.4.9.1", {"start": v(48.72, -22.7) * mm, "end": v(47.18, -22) * mm});
            skArc(sketch, "E17.7.9.1", {"start": v(48.72, -22.7) * mm, "mid": v(49.36, -22.5) * mm, "end": v(49.22, -21.84) * mm});
            skLineSegment(sketch, "E17.11.9.1", {"start": v(44.8, -22.7) * mm, "end": v(46.35, -22) * mm});
            skArc(sketch, "E17.14.9.1", {"start": v(44.3, -21.84) * mm, "mid": v(44.17, -22.5) * mm, "end": v(44.8, -22.7) * mm});
            skArc(sketch, "E17.18.9.1", {"start": v(47.26, -18.45) * mm, "mid": v(46.77, -18) * mm, "end": v(46.27, -18.45) * mm});
            skPoint(sketch, "E17.22.9.1", {"position": v(47.5, -20.9) * mm});
            skPoint(sketch, "E17.23.9.1", {"position": v(46.31, -20.4) * mm});
            skCircle(sketch, "E17.24.9.1", {"center": v(46.77, -21) * mm, "radius": 0.75 * mm, "construction": true});
            skPoint(sketch, "E17.26.9.1", {"position": v(46.77, -21) * mm});
            skLineSegment(sketch, "E17.27.9.1", {"start": v(47.26, -18.45) * mm, "end": v(47.43, -20.14) * mm});
            skPoint(sketch, "E17.30.9.1", {"position": v(46.48, -21.7) * mm});
            skPoint(sketch, "E17.31.9.1", {"position": v(47.26, -20.43) * mm});
            skPoint(sketch, "E17.32.9.1", {"position": v(46.03, -20.86) * mm});
            skLineSegment(sketch, "E17.33.9.1", {"start": v(44.3, -21.84) * mm, "end": v(45.69, -20.85) * mm});
            skLineSegment(sketch, "E17.36.9.1", {"start": v(46.27, -18.45) * mm, "end": v(46.1, -20.14) * mm});
            skArc(sketch, "E17.39.9.1", {"start": v(47.18, -22) * mm, "mid": v(46.77, -21.92) * mm, "end": v(46.35, -22) * mm});
            skArc(sketch, "E17.43.9.1", {"start": v(45.69, -20.85) * mm, "mid": v(45.97, -20.54) * mm, "end": v(46.1, -20.14) * mm});
            skArc(sketch, "E17.47.9.1", {"start": v(47.43, -20.14) * mm, "mid": v(47.56, -20.54) * mm, "end": v(47.84, -20.85) * mm});
            skPoint(sketch, "E17.0.9.2", {"position": v(47.01, -15.71) * mm});
            skLineSegment(sketch, "E17.1.9.2", {"start": v(49.22, -15.84) * mm, "end": v(47.84, -14.85) * mm});
            skLineSegment(sketch, "E17.4.9.2", {"start": v(48.72, -16.7) * mm, "end": v(47.18, -16) * mm});
            skArc(sketch, "E17.7.9.2", {"start": v(48.72, -16.7) * mm, "mid": v(49.36, -16.5) * mm, "end": v(49.22, -15.84) * mm});
            skLineSegment(sketch, "E17.11.9.2", {"start": v(44.8, -16.7) * mm, "end": v(46.35, -16) * mm});
            skArc(sketch, "E17.14.9.2", {"start": v(44.3, -15.84) * mm, "mid": v(44.17, -16.5) * mm, "end": v(44.8, -16.7) * mm});
            skArc(sketch, "E17.18.9.2", {"start": v(47.26, -12.45) * mm, "mid": v(46.77, -12) * mm, "end": v(46.27, -12.45) * mm});
            skPoint(sketch, "E17.22.9.2", {"position": v(47.5, -14.9) * mm});
            skPoint(sketch, "E17.23.9.2", {"position": v(46.31, -14.4) * mm});
            skCircle(sketch, "E17.24.9.2", {"center": v(46.77, -15) * mm, "radius": 0.75 * mm, "construction": true});
            skPoint(sketch, "E17.26.9.2", {"position": v(46.77, -15) * mm});
            skLineSegment(sketch, "E17.27.9.2", {"start": v(47.26, -12.45) * mm, "end": v(47.43, -14.14) * mm});
            skPoint(sketch, "E17.30.9.2", {"position": v(46.48, -15.7) * mm});
            skPoint(sketch, "E17.31.9.2", {"position": v(47.26, -14.43) * mm});
            skPoint(sketch, "E17.32.9.2", {"position": v(46.03, -14.86) * mm});
            skLineSegment(sketch, "E17.33.9.2", {"start": v(44.3, -15.84) * mm, "end": v(45.69, -14.85) * mm});
            skLineSegment(sketch, "E17.36.9.2", {"start": v(46.27, -12.45) * mm, "end": v(46.1, -14.14) * mm});
            skArc(sketch, "E17.39.9.2", {"start": v(47.18, -16) * mm, "mid": v(46.77, -15.92) * mm, "end": v(46.35, -16) * mm});
            skArc(sketch, "E17.43.9.2", {"start": v(45.69, -14.85) * mm, "mid": v(45.97, -14.54) * mm, "end": v(46.1, -14.14) * mm});
            skArc(sketch, "E17.47.9.2", {"start": v(47.43, -14.14) * mm, "mid": v(47.56, -14.54) * mm, "end": v(47.84, -14.85) * mm});
            skPoint(sketch, "E17.0.9.3", {"position": v(47.01, -9.71) * mm});
            skLineSegment(sketch, "E17.1.9.3", {"start": v(49.22, -9.84) * mm, "end": v(47.84, -8.85) * mm});
            skLineSegment(sketch, "E17.4.9.3", {"start": v(48.72, -10.7) * mm, "end": v(47.18, -10) * mm});
            skArc(sketch, "E17.7.9.3", {"start": v(48.72, -10.7) * mm, "mid": v(49.36, -10.5) * mm, "end": v(49.22, -9.84) * mm});
            skLineSegment(sketch, "E17.11.9.3", {"start": v(44.8, -10.7) * mm, "end": v(46.35, -10) * mm});
            skArc(sketch, "E17.14.9.3", {"start": v(44.3, -9.84) * mm, "mid": v(44.17, -10.5) * mm, "end": v(44.8, -10.7) * mm});
            skArc(sketch, "E17.18.9.3", {"start": v(47.26, -6.45) * mm, "mid": v(46.77, -6) * mm, "end": v(46.27, -6.45) * mm});
            skPoint(sketch, "E17.22.9.3", {"position": v(47.5, -8.9) * mm});
            skPoint(sketch, "E17.23.9.3", {"position": v(46.31, -8.4) * mm});
            skCircle(sketch, "E17.24.9.3", {"center": v(46.77, -9) * mm, "radius": 0.75 * mm, "construction": true});
            skPoint(sketch, "E17.26.9.3", {"position": v(46.77, -9) * mm});
            skLineSegment(sketch, "E17.27.9.3", {"start": v(47.26, -6.45) * mm, "end": v(47.43, -8.14) * mm});
            skPoint(sketch, "E17.30.9.3", {"position": v(46.48, -9.7) * mm});
            skPoint(sketch, "E17.31.9.3", {"position": v(47.26, -8.43) * mm});
            skPoint(sketch, "E17.32.9.3", {"position": v(46.03, -8.86) * mm});
            skLineSegment(sketch, "E17.33.9.3", {"start": v(44.3, -9.84) * mm, "end": v(45.69, -8.85) * mm});
            skLineSegment(sketch, "E17.36.9.3", {"start": v(46.27, -6.45) * mm, "end": v(46.1, -8.14) * mm});
            skArc(sketch, "E17.39.9.3", {"start": v(47.18, -10) * mm, "mid": v(46.77, -9.92) * mm, "end": v(46.35, -10) * mm});
            skArc(sketch, "E17.43.9.3", {"start": v(45.69, -8.85) * mm, "mid": v(45.97, -8.54) * mm, "end": v(46.1, -8.14) * mm});
            skArc(sketch, "E17.47.9.3", {"start": v(47.43, -8.14) * mm, "mid": v(47.56, -8.54) * mm, "end": v(47.84, -8.85) * mm});
            skPoint(sketch, "E17.0.9.4", {"position": v(47.01, -3.71) * mm});
            skLineSegment(sketch, "E17.1.9.4", {"start": v(49.22, -3.84) * mm, "end": v(47.84, -2.85) * mm});
            skLineSegment(sketch, "E17.4.9.4", {"start": v(48.72, -4.7) * mm, "end": v(47.18, -4) * mm});
            skArc(sketch, "E17.7.9.4", {"start": v(48.72, -4.7) * mm, "mid": v(49.36, -4.5) * mm, "end": v(49.22, -3.84) * mm});
            skLineSegment(sketch, "E17.11.9.4", {"start": v(44.8, -4.7) * mm, "end": v(46.35, -4) * mm});
            skArc(sketch, "E17.14.9.4", {"start": v(44.3, -3.84) * mm, "mid": v(44.17, -4.5) * mm, "end": v(44.8, -4.7) * mm});
            skArc(sketch, "E17.18.9.4", {"start": v(47.26, -0.45) * mm, "mid": v(46.77, 0) * mm, "end": v(46.27, -0.45) * mm});
            skPoint(sketch, "E17.22.9.4", {"position": v(47.5, -2.9) * mm});
            skPoint(sketch, "E17.23.9.4", {"position": v(46.31, -2.4) * mm});
            skCircle(sketch, "E17.24.9.4", {"center": v(46.77, -3) * mm, "radius": 0.75 * mm, "construction": true});
            skPoint(sketch, "E17.26.9.4", {"position": v(46.77, -3) * mm});
            skLineSegment(sketch, "E17.27.9.4", {"start": v(47.26, -0.45) * mm, "end": v(47.43, -2.14) * mm});
            skPoint(sketch, "E17.30.9.4", {"position": v(46.48, -3.7) * mm});
            skPoint(sketch, "E17.31.9.4", {"position": v(47.26, -2.43) * mm});
            skPoint(sketch, "E17.32.9.4", {"position": v(46.03, -2.86) * mm});
            skLineSegment(sketch, "E17.33.9.4", {"start": v(44.3, -3.84) * mm, "end": v(45.69, -2.85) * mm});
            skLineSegment(sketch, "E17.36.9.4", {"start": v(46.27, -0.45) * mm, "end": v(46.1, -2.14) * mm});
            skArc(sketch, "E17.39.9.4", {"start": v(47.18, -4) * mm, "mid": v(46.77, -3.92) * mm, "end": v(46.35, -4) * mm});
            skArc(sketch, "E17.43.9.4", {"start": v(45.69, -2.85) * mm, "mid": v(45.97, -2.54) * mm, "end": v(46.1, -2.14) * mm});
            skArc(sketch, "E17.47.9.4", {"start": v(47.43, -2.14) * mm, "mid": v(47.56, -2.54) * mm, "end": v(47.84, -2.85) * mm});
            skPoint(sketch, "E17.0.9.5", {"position": v(47.01, 2.29) * mm});
            skLineSegment(sketch, "E17.1.9.5", {"start": v(49.22, 2.16) * mm, "end": v(47.84, 3.15) * mm});
            skLineSegment(sketch, "E17.4.9.5", {"start": v(48.72, 1.3) * mm, "end": v(47.18, 2) * mm});
            skArc(sketch, "E17.7.9.5", {"start": v(48.72, 1.3) * mm, "mid": v(49.36, 1.5) * mm, "end": v(49.22, 2.16) * mm});
            skLineSegment(sketch, "E17.11.9.5", {"start": v(44.8, 1.3) * mm, "end": v(46.35, 2) * mm});
            skArc(sketch, "E17.14.9.5", {"start": v(44.3, 2.16) * mm, "mid": v(44.17, 1.5) * mm, "end": v(44.8, 1.3) * mm});
            skArc(sketch, "E17.18.9.5", {"start": v(47.26, 5.55) * mm, "mid": v(46.77, 6) * mm, "end": v(46.27, 5.55) * mm});
            skPoint(sketch, "E17.22.9.5", {"position": v(47.5, 3.1) * mm});
            skPoint(sketch, "E17.23.9.5", {"position": v(46.31, 3.6) * mm});
            skCircle(sketch, "E17.24.9.5", {"center": v(46.77, 3) * mm, "radius": 0.75 * mm, "construction": true});
            skPoint(sketch, "E17.26.9.5", {"position": v(46.77, 3) * mm});
            skLineSegment(sketch, "E17.27.9.5", {"start": v(47.26, 5.55) * mm, "end": v(47.43, 3.86) * mm});
            skPoint(sketch, "E17.30.9.5", {"position": v(46.48, 2.3) * mm});
            skPoint(sketch, "E17.31.9.5", {"position": v(47.26, 3.57) * mm});
            skPoint(sketch, "E17.32.9.5", {"position": v(46.03, 3.14) * mm});
            skLineSegment(sketch, "E17.33.9.5", {"start": v(44.3, 2.16) * mm, "end": v(45.69, 3.15) * mm});
            skLineSegment(sketch, "E17.36.9.5", {"start": v(46.27, 5.55) * mm, "end": v(46.1, 3.86) * mm});
            skArc(sketch, "E17.39.9.5", {"start": v(47.18, 2) * mm, "mid": v(46.77, 2.08) * mm, "end": v(46.35, 2) * mm});
            skArc(sketch, "E17.43.9.5", {"start": v(45.69, 3.15) * mm, "mid": v(45.97, 3.46) * mm, "end": v(46.1, 3.86) * mm});
            skArc(sketch, "E17.47.9.5", {"start": v(47.43, 3.86) * mm, "mid": v(47.56, 3.46) * mm, "end": v(47.84, 3.15) * mm});
            skPoint(sketch, "E17.0.9.6", {"position": v(47.01, 8.29) * mm});
            skLineSegment(sketch, "E17.1.9.6", {"start": v(49.22, 8.16) * mm, "end": v(47.84, 9.15) * mm});
            skLineSegment(sketch, "E17.4.9.6", {"start": v(48.72, 7.3) * mm, "end": v(47.18, 8) * mm});
            skArc(sketch, "E17.7.9.6", {"start": v(48.72, 7.3) * mm, "mid": v(49.36, 7.5) * mm, "end": v(49.22, 8.16) * mm});
            skLineSegment(sketch, "E17.11.9.6", {"start": v(44.8, 7.3) * mm, "end": v(46.35, 8) * mm});
            skArc(sketch, "E17.14.9.6", {"start": v(44.3, 8.16) * mm, "mid": v(44.17, 7.5) * mm, "end": v(44.8, 7.3) * mm});
            skArc(sketch, "E17.18.9.6", {"start": v(47.26, 11.55) * mm, "mid": v(46.77, 12) * mm, "end": v(46.27, 11.55) * mm});
            skPoint(sketch, "E17.22.9.6", {"position": v(47.5, 9.1) * mm});
            skPoint(sketch, "E17.23.9.6", {"position": v(46.31, 9.6) * mm});
            skCircle(sketch, "E17.24.9.6", {"center": v(46.77, 9) * mm, "radius": 0.75 * mm, "construction": true});
            skPoint(sketch, "E17.26.9.6", {"position": v(46.77, 9) * mm});
            skLineSegment(sketch, "E17.27.9.6", {"start": v(47.26, 11.55) * mm, "end": v(47.43, 9.86) * mm});
            skPoint(sketch, "E17.30.9.6", {"position": v(46.48, 8.3) * mm});
            skPoint(sketch, "E17.31.9.6", {"position": v(47.26, 9.57) * mm});
            skPoint(sketch, "E17.32.9.6", {"position": v(46.03, 9.14) * mm});
            skLineSegment(sketch, "E17.33.9.6", {"start": v(44.3, 8.16) * mm, "end": v(45.69, 9.15) * mm});
            skLineSegment(sketch, "E17.36.9.6", {"start": v(46.27, 11.55) * mm, "end": v(46.1, 9.86) * mm});
            skArc(sketch, "E17.39.9.6", {"start": v(47.18, 8) * mm, "mid": v(46.77, 8.08) * mm, "end": v(46.35, 8) * mm});
            skArc(sketch, "E17.43.9.6", {"start": v(45.69, 9.15) * mm, "mid": v(45.97, 9.46) * mm, "end": v(46.1, 9.86) * mm});
            skArc(sketch, "E17.47.9.6", {"start": v(47.43, 9.86) * mm, "mid": v(47.56, 9.46) * mm, "end": v(47.84, 9.15) * mm});
            skPoint(sketch, "E17.0.9.7", {"position": v(47.01, 14.29) * mm});
            skLineSegment(sketch, "E17.1.9.7", {"start": v(49.22, 14.16) * mm, "end": v(47.84, 15.15) * mm});
            skLineSegment(sketch, "E17.4.9.7", {"start": v(48.72, 13.3) * mm, "end": v(47.18, 14) * mm});
            skArc(sketch, "E17.7.9.7", {"start": v(48.72, 13.3) * mm, "mid": v(49.36, 13.5) * mm, "end": v(49.22, 14.16) * mm});
            skLineSegment(sketch, "E17.11.9.7", {"start": v(44.8, 13.3) * mm, "end": v(46.35, 14) * mm});
            skArc(sketch, "E17.14.9.7", {"start": v(44.3, 14.16) * mm, "mid": v(44.17, 13.5) * mm, "end": v(44.8, 13.3) * mm});
            skArc(sketch, "E17.18.9.7", {"start": v(47.26, 17.55) * mm, "mid": v(46.77, 18) * mm, "end": v(46.27, 17.55) * mm});
            skPoint(sketch, "E17.22.9.7", {"position": v(47.5, 15.1) * mm});
            skPoint(sketch, "E17.23.9.7", {"position": v(46.31, 15.6) * mm});
            skCircle(sketch, "E17.24.9.7", {"center": v(46.77, 15) * mm, "radius": 0.75 * mm, "construction": true});
            skPoint(sketch, "E17.26.9.7", {"position": v(46.77, 15) * mm});
            skLineSegment(sketch, "E17.27.9.7", {"start": v(47.26, 17.55) * mm, "end": v(47.43, 15.86) * mm});
            skPoint(sketch, "E17.30.9.7", {"position": v(46.48, 14.3) * mm});
            skPoint(sketch, "E17.31.9.7", {"position": v(47.26, 15.57) * mm});
            skPoint(sketch, "E17.32.9.7", {"position": v(46.03, 15.14) * mm});
            skLineSegment(sketch, "E17.33.9.7", {"start": v(44.3, 14.16) * mm, "end": v(45.69, 15.15) * mm});
            skLineSegment(sketch, "E17.36.9.7", {"start": v(46.27, 17.55) * mm, "end": v(46.1, 15.86) * mm});
            skArc(sketch, "E17.39.9.7", {"start": v(47.18, 14) * mm, "mid": v(46.77, 14.08) * mm, "end": v(46.35, 14) * mm});
            skArc(sketch, "E17.43.9.7", {"start": v(45.69, 15.15) * mm, "mid": v(45.97, 15.46) * mm, "end": v(46.1, 15.86) * mm});
            skArc(sketch, "E17.47.9.7", {"start": v(47.43, 15.86) * mm, "mid": v(47.56, 15.46) * mm, "end": v(47.84, 15.15) * mm});
            skSolve(sketch);
        }
        {
            var Q0;
            Q0=makeQuery(id+"F2.imprint","IMPRINT",FACE,{"disambiguationData":[TD([[makeQuery(id+"F2.imprint","IMPRINT",EDGE,{"derivedFrom":sQuery(id+"F2.wireOp",EDGE,"E7")}),-1.0]])]});
            extrude(context, id + "F3", {"entities" : qUnion([Q0]), "operationType" : NewBodyOperationType.ADD, "depth" : 1 * mm});
        }
        {
            var Q0;
            Q0=makeQuery(id+"F3.opExtrude","CAP_FACE",FACE,{"disambiguationData":[OSD([sQuery(id+"F0.wireOp",EDGE,"E2.bottom"),sQuery(id+"F0.wireOp",EDGE,"E2.top"),sQuery(id+"F0.wireOp",EDGE,"E2.left"),sQuery(id+"F0.wireOp",EDGE,"E2.right"),sQuery(id+"F2.wireOp",EDGE,"E7"),sQuery(id+"F2.wireOp",EDGE,"E9"),sQuery(id+"F2.wireOp",EDGE,"E10"),sQuery(id+"F2.wireOp",EDGE,"E11.1.0"),sQuery(id+"F2.wireOp",EDGE,"E11.1.1"),sQuery(id+"F2.wireOp",EDGE,"E11.1.2"),sQuery(id+"F2.wireOp",EDGE,"E11.2.0"),sQuery(id+"F2.wireOp",EDGE,"E11.2.1"),sQuery(id+"F2.wireOp",EDGE,"E11.2.2"),sQuery(id+"F2.wireOp",EDGE,"E12.filletArc"),sQuery(id+"F2.wireOp",EDGE,"E13.filletArc"),sQuery(id+"F2.wireOp",EDGE,"E14.filletArc"),sQuery(id+"F2.wireOp",EDGE,"E15.0.1.1"),sQuery(id+"F2.wireOp",EDGE,"E15.0.1.2"),sQuery(id+"F2.wireOp",EDGE,"E15.0.1.3"),sQuery(id+"F2.wireOp",EDGE,"E15.0.1.4"),sQuery(id+"F2.wireOp",EDGE,"E15.0.1.5"),sQuery(id+"F2.wireOp",EDGE,"E15.0.1.6"),sQuery(id+"F2.wireOp",EDGE,"E15.0.1.11"),sQuery(id+"F2.wireOp",EDGE,"E15.0.1.15"),sQuery(id+"F2.wireOp",EDGE,"E15.0.1.16"),sQuery(id+"F2.wireOp",EDGE,"E15.0.1.17"),sQuery(id+"F2.wireOp",EDGE,"E15.0.1.18"),sQuery(id+"F2.wireOp",EDGE,"E15.0.1.19"),sQuery(id+"F2.wireOp",EDGE,"E15.0.2.1"),sQuery(id+"F2.wireOp",EDGE,"E15.0.2.2"),sQuery(id+"F2.wireOp",EDGE,"E15.0.2.3"),sQuery(id+"F2.wireOp",EDGE,"E15.0.2.4"),sQuery(id+"F2.wireOp",EDGE,"E15.0.2.5"),sQuery(id+"F2.wireOp",EDGE,"E15.0.2.6"),sQuery(id+"F2.wireOp",EDGE,"E15.0.2.11"),sQuery(id+"F2.wireOp",EDGE,"E15.0.2.15"),sQuery(id+"F2.wireOp",EDGE,"E15.0.2.16"),sQuery(id+"F2.wireOp",EDGE,"E15.0.2.17"),sQuery(id+"F2.wireOp",EDGE,"E15.0.2.18"),sQuery(id+"F2.wireOp",EDGE,"E15.0.2.19"),sQuery(id+"F2.wireOp",EDGE,"E15.0.3.1"),sQuery(id+"F2.wireOp",EDGE,"E15.0.3.2"),sQuery(id+"F2.wireOp",EDGE,"E15.0.3.3"),sQuery(id+"F2.wireOp",EDGE,"E15.0.3.4"),sQuery(id+"F2.wireOp",EDGE,"E15.0.3.5"),sQuery(id+"F2.wireOp",EDGE,"E15.0.3.6"),sQuery(id+"F2.wireOp",EDGE,"E15.0.3.11"),sQuery(id+"F2.wireOp",EDGE,"E15.0.3.15"),sQuery(id+"F2.wireOp",EDGE,"E15.0.3.16"),sQuery(id+"F2.wireOp",EDGE,"E15.0.3.17"),sQuery(id+"F2.wireOp",EDGE,"E15.0.3.18"),sQuery(id+"F2.wireOp",EDGE,"E15.0.3.19"),sQuery(id+"F2.wireOp",EDGE,"E15.0.4.1"),sQuery(id+"F2.wireOp",EDGE,"E15.0.4.2"),sQuery(id+"F2.wireOp",EDGE,"E15.0.4.3"),sQuery(id+"F2.wireOp",EDGE,"E15.0.4.4"),sQuery(id+"F2.wireOp",EDGE,"E15.0.4.5"),sQuery(id+"F2.wireOp",EDGE,"E15.0.4.6"),sQuery(id+"F2.wireOp",EDGE,"E15.0.4.11"),sQuery(id+"F2.wireOp",EDGE,"E15.0.4.15"),sQuery(id+"F2.wireOp",EDGE,"E15.0.4.16"),sQuery(id+"F2.wireOp",EDGE,"E15.0.4.17"),sQuery(id+"F2.wireOp",EDGE,"E15.0.4.18"),sQuery(id+"F2.wireOp",EDGE,"E15.0.4.19"),sQuery(id+"F2.wireOp",EDGE,"E15.0.5.1"),sQuery(id+"F2.wireOp",EDGE,"E15.0.5.2"),sQuery(id+"F2.wireOp",EDGE,"E15.0.5.3"),sQuery(id+"F2.wireOp",EDGE,"E15.0.5.4"),sQuery(id+"F2.wireOp",EDGE,"E15.0.5.5"),sQuery(id+"F2.wireOp",EDGE,"E15.0.5.6"),sQuery(id+"F2.wireOp",EDGE,"E15.0.5.11"),sQuery(id+"F2.wireOp",EDGE,"E15.0.5.15"),sQuery(id+"F2.wireOp",EDGE,"E15.0.5.16"),sQuery(id+"F2.wireOp",EDGE,"E15.0.5.17"),sQuery(id+"F2.wireOp",EDGE,"E15.0.5.18"),sQuery(id+"F2.wireOp",EDGE,"E15.0.5.19"),sQuery(id+"F2.wireOp",EDGE,"E15.0.6.1"),sQuery(id+"F2.wireOp",EDGE,"E15.0.6.2"),sQuery(id+"F2.wireOp",EDGE,"E15.0.6.3"),sQuery(id+"F2.wireOp",EDGE,"E15.0.6.4"),sQuery(id+"F2.wireOp",EDGE,"E15.0.6.5"),sQuery(id+"F2.wireOp",EDGE,"E15.0.6.6"),sQuery(id+"F2.wireOp",EDGE,"E15.0.6.11"),sQuery(id+"F2.wireOp",EDGE,"E15.0.6.15"),sQuery(id+"F2.wireOp",EDGE,"E15.0.6.16"),sQuery(id+"F2.wireOp",EDGE,"E15.0.6.17"),sQuery(id+"F2.wireOp",EDGE,"E15.0.6.18"),sQuery(id+"F2.wireOp",EDGE,"E15.0.6.19"),sQuery(id+"F2.wireOp",EDGE,"E15.0.7.1"),sQuery(id+"F2.wireOp",EDGE,"E15.0.7.2"),sQuery(id+"F2.wireOp",EDGE,"E15.0.7.3"),sQuery(id+"F2.wireOp",EDGE,"E15.0.7.4"),sQuery(id+"F2.wireOp",EDGE,"E15.0.7.5"),sQuery(id+"F2.wireOp",EDGE,"E15.0.7.6"),sQuery(id+"F2.wireOp",EDGE,"E15.0.7.11"),sQuery(id+"F2.wireOp",EDGE,"E15.0.7.15"),sQuery(id+"F2.wireOp",EDGE,"E15.0.7.16"),sQuery(id+"F2.wireOp",EDGE,"E15.0.7.17"),sQuery(id+"F2.wireOp",EDGE,"E15.0.7.18"),sQuery(id+"F2.wireOp",EDGE,"E15.0.7.19"),sQuery(id+"F2.wireOp",EDGE,"E15.0.8.1"),sQuery(id+"F2.wireOp",EDGE,"E15.0.8.2"),sQuery(id+"F2.wireOp",EDGE,"E15.0.8.3"),sQuery(id+"F2.wireOp",EDGE,"E15.0.8.4"),sQuery(id+"F2.wireOp",EDGE,"E15.0.8.5"),sQuery(id+"F2.wireOp",EDGE,"E15.0.8.6"),sQuery(id+"F2.wireOp",EDGE,"E15.0.8.11"),sQuery(id+"F2.wireOp",EDGE,"E15.0.8.15"),sQuery(id+"F2.wireOp",EDGE,"E15.0.8.16"),sQuery(id+"F2.wireOp",EDGE,"E15.0.8.17"),sQuery(id+"F2.wireOp",EDGE,"E15.0.8.18"),sQuery(id+"F2.wireOp",EDGE,"E15.0.8.19"),sQuery(id+"F2.wireOp",EDGE,"E15.0.9.1"),sQuery(id+"F2.wireOp",EDGE,"E15.0.9.2"),sQuery(id+"F2.wireOp",EDGE,"E15.0.9.3"),sQuery(id+"F2.wireOp",EDGE,"E15.0.9.4"),sQuery(id+"F2.wireOp",EDGE,"E15.0.9.5"),sQuery(id+"F2.wireOp",EDGE,"E15.0.9.6"),sQuery(id+"F2.wireOp",EDGE,"E15.0.9.11"),sQuery(id+"F2.wireOp",EDGE,"E15.0.9.15"),sQuery(id+"F2.wireOp",EDGE,"E15.0.9.16"),sQuery(id+"F2.wireOp",EDGE,"E15.0.9.17"),sQuery(id+"F2.wireOp",EDGE,"E15.0.9.18"),sQuery(id+"F2.wireOp",EDGE,"E15.0.9.19"),sQuery(id+"F2.wireOp",EDGE,"E15.1.0.1"),sQuery(id+"F2.wireOp",EDGE,"E15.1.0.2"),sQuery(id+"F2.wireOp",EDGE,"E15.1.0.3"),sQuery(id+"F2.wireOp",EDGE,"E15.1.0.4"),sQuery(id+"F2.wireOp",EDGE,"E15.1.0.5"),sQuery(id+"F2.wireOp",EDGE,"E15.1.0.6"),sQuery(id+"F2.wireOp",EDGE,"E15.1.0.11"),sQuery(id+"F2.wireOp",EDGE,"E15.1.0.15"),sQuery(id+"F2.wireOp",EDGE,"E15.1.0.16"),sQuery(id+"F2.wireOp",EDGE,"E15.1.0.17"),sQuery(id+"F2.wireOp",EDGE,"E15.1.0.18"),sQuery(id+"F2.wireOp",EDGE,"E15.1.0.19"),sQuery(id+"F2.wireOp",EDGE,"E15.1.1.1"),sQuery(id+"F2.wireOp",EDGE,"E15.1.1.2"),sQuery(id+"F2.wireOp",EDGE,"E15.1.1.3"),sQuery(id+"F2.wireOp",EDGE,"E15.1.1.4"),sQuery(id+"F2.wireOp",EDGE,"E15.1.1.5"),sQuery(id+"F2.wireOp",EDGE,"E15.1.1.6"),sQuery(id+"F2.wireOp",EDGE,"E15.1.1.11"),sQuery(id+"F2.wireOp",EDGE,"E15.1.1.15"),sQuery(id+"F2.wireOp",EDGE,"E15.1.1.16"),sQuery(id+"F2.wireOp",EDGE,"E15.1.1.17"),sQuery(id+"F2.wireOp",EDGE,"E15.1.1.18"),sQuery(id+"F2.wireOp",EDGE,"E15.1.1.19"),sQuery(id+"F2.wireOp",EDGE,"E15.1.2.1"),sQuery(id+"F2.wireOp",EDGE,"E15.1.2.2"),sQuery(id+"F2.wireOp",EDGE,"E15.1.2.3"),sQuery(id+"F2.wireOp",EDGE,"E15.1.2.4"),sQuery(id+"F2.wireOp",EDGE,"E15.1.2.5"),sQuery(id+"F2.wireOp",EDGE,"E15.1.2.6"),sQuery(id+"F2.wireOp",EDGE,"E15.1.2.11"),sQuery(id+"F2.wireOp",EDGE,"E15.1.2.15"),sQuery(id+"F2.wireOp",EDGE,"E15.1.2.16"),sQuery(id+"F2.wireOp",EDGE,"E15.1.2.17"),sQuery(id+"F2.wireOp",EDGE,"E15.1.2.18"),sQuery(id+"F2.wireOp",EDGE,"E15.1.2.19"),sQuery(id+"F2.wireOp",EDGE,"E15.1.3.1"),sQuery(id+"F2.wireOp",EDGE,"E15.1.3.2"),sQuery(id+"F2.wireOp",EDGE,"E15.1.3.3"),sQuery(id+"F2.wireOp",EDGE,"E15.1.3.4"),sQuery(id+"F2.wireOp",EDGE,"E15.1.3.5"),sQuery(id+"F2.wireOp",EDGE,"E15.1.3.6"),sQuery(id+"F2.wireOp",EDGE,"E15.1.3.11"),sQuery(id+"F2.wireOp",EDGE,"E15.1.3.15"),sQuery(id+"F2.wireOp",EDGE,"E15.1.3.16"),sQuery(id+"F2.wireOp",EDGE,"E15.1.3.17"),sQuery(id+"F2.wireOp",EDGE,"E15.1.3.18"),sQuery(id+"F2.wireOp",EDGE,"E15.1.3.19"),sQuery(id+"F2.wireOp",EDGE,"E15.1.4.1"),sQuery(id+"F2.wireOp",EDGE,"E15.1.4.2"),sQuery(id+"F2.wireOp",EDGE,"E15.1.4.3"),sQuery(id+"F2.wireOp",EDGE,"E15.1.4.4"),sQuery(id+"F2.wireOp",EDGE,"E15.1.4.5"),sQuery(id+"F2.wireOp",EDGE,"E15.1.4.6"),sQuery(id+"F2.wireOp",EDGE,"E15.1.4.11"),sQuery(id+"F2.wireOp",EDGE,"E15.1.4.15"),sQuery(id+"F2.wireOp",EDGE,"E15.1.4.16"),sQuery(id+"F2.wireOp",EDGE,"E15.1.4.17"),sQuery(id+"F2.wireOp",EDGE,"E15.1.4.18"),sQuery(id+"F2.wireOp",EDGE,"E15.1.4.19"),sQuery(id+"F2.wireOp",EDGE,"E15.1.5.1"),sQuery(id+"F2.wireOp",EDGE,"E15.1.5.2"),sQuery(id+"F2.wireOp",EDGE,"E15.1.5.3"),sQuery(id+"F2.wireOp",EDGE,"E15.1.5.4"),sQuery(id+"F2.wireOp",EDGE,"E15.1.5.5"),sQuery(id+"F2.wireOp",EDGE,"E15.1.5.6"),sQuery(id+"F2.wireOp",EDGE,"E15.1.5.11"),sQuery(id+"F2.wireOp",EDGE,"E15.1.5.15"),sQuery(id+"F2.wireOp",EDGE,"E15.1.5.16"),sQuery(id+"F2.wireOp",EDGE,"E15.1.5.17"),sQuery(id+"F2.wireOp",EDGE,"E15.1.5.18"),sQuery(id+"F2.wireOp",EDGE,"E15.1.5.19"),sQuery(id+"F2.wireOp",EDGE,"E15.1.6.1"),sQuery(id+"F2.wireOp",EDGE,"E15.1.6.2"),sQuery(id+"F2.wireOp",EDGE,"E15.1.6.3"),sQuery(id+"F2.wireOp",EDGE,"E15.1.6.4"),sQuery(id+"F2.wireOp",EDGE,"E15.1.6.5"),sQuery(id+"F2.wireOp",EDGE,"E15.1.6.6"),sQuery(id+"F2.wireOp",EDGE,"E15.1.6.11"),sQuery(id+"F2.wireOp",EDGE,"E15.1.6.15"),sQuery(id+"F2.wireOp",EDGE,"E15.1.6.16"),sQuery(id+"F2.wireOp",EDGE,"E15.1.6.17"),sQuery(id+"F2.wireOp",EDGE,"E15.1.6.18"),sQuery(id+"F2.wireOp",EDGE,"E15.1.6.19"),sQuery(id+"F2.wireOp",EDGE,"E15.1.7.1"),sQuery(id+"F2.wireOp",EDGE,"E15.1.7.2"),sQuery(id+"F2.wireOp",EDGE,"E15.1.7.3"),sQuery(id+"F2.wireOp",EDGE,"E15.1.7.4"),sQuery(id+"F2.wireOp",EDGE,"E15.1.7.5"),sQuery(id+"F2.wireOp",EDGE,"E15.1.7.6"),sQuery(id+"F2.wireOp",EDGE,"E15.1.7.11"),sQuery(id+"F2.wireOp",EDGE,"E15.1.7.15"),sQuery(id+"F2.wireOp",EDGE,"E15.1.7.16"),sQuery(id+"F2.wireOp",EDGE,"E15.1.7.17"),sQuery(id+"F2.wireOp",EDGE,"E15.1.7.18"),sQuery(id+"F2.wireOp",EDGE,"E15.1.7.19"),sQuery(id+"F2.wireOp",EDGE,"E15.1.8.1"),sQuery(id+"F2.wireOp",EDGE,"E15.1.8.2"),sQuery(id+"F2.wireOp",EDGE,"E15.1.8.3"),sQuery(id+"F2.wireOp",EDGE,"E15.1.8.4"),sQuery(id+"F2.wireOp",EDGE,"E15.1.8.5"),sQuery(id+"F2.wireOp",EDGE,"E15.1.8.6"),sQuery(id+"F2.wireOp",EDGE,"E15.1.8.11"),sQuery(id+"F2.wireOp",EDGE,"E15.1.8.15"),sQuery(id+"F2.wireOp",EDGE,"E15.1.8.16"),sQuery(id+"F2.wireOp",EDGE,"E15.1.8.17"),sQuery(id+"F2.wireOp",EDGE,"E15.1.8.18"),sQuery(id+"F2.wireOp",EDGE,"E15.1.8.19"),sQuery(id+"F2.wireOp",EDGE,"E15.1.9.1"),sQuery(id+"F2.wireOp",EDGE,"E15.1.9.2"),sQuery(id+"F2.wireOp",EDGE,"E15.1.9.3"),sQuery(id+"F2.wireOp",EDGE,"E15.1.9.4"),sQuery(id+"F2.wireOp",EDGE,"E15.1.9.5"),sQuery(id+"F2.wireOp",EDGE,"E15.1.9.6"),sQuery(id+"F2.wireOp",EDGE,"E15.1.9.11"),sQuery(id+"F2.wireOp",EDGE,"E15.1.9.15"),sQuery(id+"F2.wireOp",EDGE,"E15.1.9.16"),sQuery(id+"F2.wireOp",EDGE,"E15.1.9.17"),sQuery(id+"F2.wireOp",EDGE,"E15.1.9.18"),sQuery(id+"F2.wireOp",EDGE,"E15.1.9.19"),sQuery(id+"F2.wireOp",EDGE,"E15.2.0.1"),sQuery(id+"F2.wireOp",EDGE,"E15.2.0.2"),sQuery(id+"F2.wireOp",EDGE,"E15.2.0.3"),sQuery(id+"F2.wireOp",EDGE,"E15.2.0.4"),sQuery(id+"F2.wireOp",EDGE,"E15.2.0.5"),sQuery(id+"F2.wireOp",EDGE,"E15.2.0.6"),sQuery(id+"F2.wireOp",EDGE,"E15.2.0.11"),sQuery(id+"F2.wireOp",EDGE,"E15.2.0.15"),sQuery(id+"F2.wireOp",EDGE,"E15.2.0.16"),sQuery(id+"F2.wireOp",EDGE,"E15.2.0.17"),sQuery(id+"F2.wireOp",EDGE,"E15.2.0.18"),sQuery(id+"F2.wireOp",EDGE,"E15.2.0.19"),sQuery(id+"F2.wireOp",EDGE,"E15.2.1.1"),sQuery(id+"F2.wireOp",EDGE,"E15.2.1.2"),sQuery(id+"F2.wireOp",EDGE,"E15.2.1.3"),sQuery(id+"F2.wireOp",EDGE,"E15.2.1.4"),sQuery(id+"F2.wireOp",EDGE,"E15.2.1.5"),sQuery(id+"F2.wireOp",EDGE,"E15.2.1.6"),sQuery(id+"F2.wireOp",EDGE,"E15.2.1.11"),sQuery(id+"F2.wireOp",EDGE,"E15.2.1.15"),sQuery(id+"F2.wireOp",EDGE,"E15.2.1.16"),sQuery(id+"F2.wireOp",EDGE,"E15.2.1.17"),sQuery(id+"F2.wireOp",EDGE,"E15.2.1.18"),sQuery(id+"F2.wireOp",EDGE,"E15.2.1.19"),sQuery(id+"F2.wireOp",EDGE,"E15.2.2.1"),sQuery(id+"F2.wireOp",EDGE,"E15.2.2.2"),sQuery(id+"F2.wireOp",EDGE,"E15.2.2.3"),sQuery(id+"F2.wireOp",EDGE,"E15.2.2.4"),sQuery(id+"F2.wireOp",EDGE,"E15.2.2.5"),sQuery(id+"F2.wireOp",EDGE,"E15.2.2.6"),sQuery(id+"F2.wireOp",EDGE,"E15.2.2.11"),sQuery(id+"F2.wireOp",EDGE,"E15.2.2.15"),sQuery(id+"F2.wireOp",EDGE,"E15.2.2.16"),sQuery(id+"F2.wireOp",EDGE,"E15.2.2.17"),sQuery(id+"F2.wireOp",EDGE,"E15.2.2.18"),sQuery(id+"F2.wireOp",EDGE,"E15.2.2.19"),sQuery(id+"F2.wireOp",EDGE,"E15.2.3.1"),sQuery(id+"F2.wireOp",EDGE,"E15.2.3.2"),sQuery(id+"F2.wireOp",EDGE,"E15.2.3.3"),sQuery(id+"F2.wireOp",EDGE,"E15.2.3.4"),sQuery(id+"F2.wireOp",EDGE,"E15.2.3.5"),sQuery(id+"F2.wireOp",EDGE,"E15.2.3.6"),sQuery(id+"F2.wireOp",EDGE,"E15.2.3.11"),sQuery(id+"F2.wireOp",EDGE,"E15.2.3.15"),sQuery(id+"F2.wireOp",EDGE,"E15.2.3.16"),sQuery(id+"F2.wireOp",EDGE,"E15.2.3.17"),sQuery(id+"F2.wireOp",EDGE,"E15.2.3.18"),sQuery(id+"F2.wireOp",EDGE,"E15.2.3.19"),sQuery(id+"F2.wireOp",EDGE,"E15.2.4.1"),sQuery(id+"F2.wireOp",EDGE,"E15.2.4.2"),sQuery(id+"F2.wireOp",EDGE,"E15.2.4.3"),sQuery(id+"F2.wireOp",EDGE,"E15.2.4.4"),sQuery(id+"F2.wireOp",EDGE,"E15.2.4.5"),sQuery(id+"F2.wireOp",EDGE,"E15.2.4.6"),sQuery(id+"F2.wireOp",EDGE,"E15.2.4.11"),sQuery(id+"F2.wireOp",EDGE,"E15.2.4.15"),sQuery(id+"F2.wireOp",EDGE,"E15.2.4.16"),sQuery(id+"F2.wireOp",EDGE,"E15.2.4.17"),sQuery(id+"F2.wireOp",EDGE,"E15.2.4.18"),sQuery(id+"F2.wireOp",EDGE,"E15.2.4.19"),sQuery(id+"F2.wireOp",EDGE,"E15.2.5.1"),sQuery(id+"F2.wireOp",EDGE,"E15.2.5.2"),sQuery(id+"F2.wireOp",EDGE,"E15.2.5.3"),sQuery(id+"F2.wireOp",EDGE,"E15.2.5.4"),sQuery(id+"F2.wireOp",EDGE,"E15.2.5.5"),sQuery(id+"F2.wireOp",EDGE,"E15.2.5.6"),sQuery(id+"F2.wireOp",EDGE,"E15.2.5.11"),sQuery(id+"F2.wireOp",EDGE,"E15.2.5.15"),sQuery(id+"F2.wireOp",EDGE,"E15.2.5.16"),sQuery(id+"F2.wireOp",EDGE,"E15.2.5.17"),sQuery(id+"F2.wireOp",EDGE,"E15.2.5.18"),sQuery(id+"F2.wireOp",EDGE,"E15.2.5.19"),sQuery(id+"F2.wireOp",EDGE,"E15.2.6.1"),sQuery(id+"F2.wireOp",EDGE,"E15.2.6.2"),sQuery(id+"F2.wireOp",EDGE,"E15.2.6.3"),sQuery(id+"F2.wireOp",EDGE,"E15.2.6.4"),sQuery(id+"F2.wireOp",EDGE,"E15.2.6.5"),sQuery(id+"F2.wireOp",EDGE,"E15.2.6.6"),sQuery(id+"F2.wireOp",EDGE,"E15.2.6.11"),sQuery(id+"F2.wireOp",EDGE,"E15.2.6.15"),sQuery(id+"F2.wireOp",EDGE,"E15.2.6.16"),sQuery(id+"F2.wireOp",EDGE,"E15.2.6.17"),sQuery(id+"F2.wireOp",EDGE,"E15.2.6.18"),sQuery(id+"F2.wireOp",EDGE,"E15.2.6.19"),sQuery(id+"F2.wireOp",EDGE,"E15.2.7.1"),sQuery(id+"F2.wireOp",EDGE,"E15.2.7.2"),sQuery(id+"F2.wireOp",EDGE,"E15.2.7.3"),sQuery(id+"F2.wireOp",EDGE,"E15.2.7.4"),sQuery(id+"F2.wireOp",EDGE,"E15.2.7.5"),sQuery(id+"F2.wireOp",EDGE,"E15.2.7.6"),sQuery(id+"F2.wireOp",EDGE,"E15.2.7.11"),sQuery(id+"F2.wireOp",EDGE,"E15.2.7.15"),sQuery(id+"F2.wireOp",EDGE,"E15.2.7.16"),sQuery(id+"F2.wireOp",EDGE,"E15.2.7.17"),sQuery(id+"F2.wireOp",EDGE,"E15.2.7.18"),sQuery(id+"F2.wireOp",EDGE,"E15.2.7.19"),sQuery(id+"F2.wireOp",EDGE,"E15.2.8.1"),sQuery(id+"F2.wireOp",EDGE,"E15.2.8.2"),sQuery(id+"F2.wireOp",EDGE,"E15.2.8.3"),sQuery(id+"F2.wireOp",EDGE,"E15.2.8.4"),sQuery(id+"F2.wireOp",EDGE,"E15.2.8.5"),sQuery(id+"F2.wireOp",EDGE,"E15.2.8.6"),sQuery(id+"F2.wireOp",EDGE,"E15.2.8.11"),sQuery(id+"F2.wireOp",EDGE,"E15.2.8.15"),sQuery(id+"F2.wireOp",EDGE,"E15.2.8.16"),sQuery(id+"F2.wireOp",EDGE,"E15.2.8.17"),sQuery(id+"F2.wireOp",EDGE,"E15.2.8.18"),sQuery(id+"F2.wireOp",EDGE,"E15.2.8.19"),sQuery(id+"F2.wireOp",EDGE,"E15.2.9.1"),sQuery(id+"F2.wireOp",EDGE,"E15.2.9.2"),sQuery(id+"F2.wireOp",EDGE,"E15.2.9.3"),sQuery(id+"F2.wireOp",EDGE,"E15.2.9.4"),sQuery(id+"F2.wireOp",EDGE,"E15.2.9.5"),sQuery(id+"F2.wireOp",EDGE,"E15.2.9.6"),sQuery(id+"F2.wireOp",EDGE,"E15.2.9.11"),sQuery(id+"F2.wireOp",EDGE,"E15.2.9.15"),sQuery(id+"F2.wireOp",EDGE,"E15.2.9.16"),sQuery(id+"F2.wireOp",EDGE,"E15.2.9.17"),sQuery(id+"F2.wireOp",EDGE,"E15.2.9.18"),sQuery(id+"F2.wireOp",EDGE,"E15.2.9.19"),sQuery(id+"F2.wireOp",EDGE,"f79f6195-6e67-4fcd-a5d6-908ccd97d016.1.3.0"),sQuery(id+"F2.wireOp",EDGE,"f79f6195-6e67-4fcd-a5d6-908ccd97d016.4.3.0"),sQuery(id+"F2.wireOp",EDGE,"f79f6195-6e67-4fcd-a5d6-908ccd97d016.7.3.0"),sQuery(id+"F2.wireOp",EDGE,"f79f6195-6e67-4fcd-a5d6-908ccd97d016.11.3.0"),sQuery(id+"F2.wireOp",EDGE,"f79f6195-6e67-4fcd-a5d6-908ccd97d016.14.3.0"),sQuery(id+"F2.wireOp",EDGE,"f79f6195-6e67-4fcd-a5d6-908ccd97d016.18.3.0"),sQuery(id+"F2.wireOp",EDGE,"f79f6195-6e67-4fcd-a5d6-908ccd97d016.27.3.0"),sQuery(id+"F2.wireOp",EDGE,"f79f6195-6e67-4fcd-a5d6-908ccd97d016.33.3.0"),sQuery(id+"F2.wireOp",EDGE,"f79f6195-6e67-4fcd-a5d6-908ccd97d016.36.3.0"),sQuery(id+"F2.wireOp",EDGE,"f79f6195-6e67-4fcd-a5d6-908ccd97d016.39.3.0"),sQuery(id+"F2.wireOp",EDGE,"f79f6195-6e67-4fcd-a5d6-908ccd97d016.43.3.0"),sQuery(id+"F2.wireOp",EDGE,"f79f6195-6e67-4fcd-a5d6-908ccd97d016.47.3.0"),sQuery(id+"F2.wireOp",EDGE,"f79f6195-6e67-4fcd-a5d6-908ccd97d016.1.3.1"),sQuery(id+"F2.wireOp",EDGE,"f79f6195-6e67-4fcd-a5d6-908ccd97d016.4.3.1"),sQuery(id+"F2.wireOp",EDGE,"f79f6195-6e67-4fcd-a5d6-908ccd97d016.7.3.1"),sQuery(id+"F2.wireOp",EDGE,"f79f6195-6e67-4fcd-a5d6-908ccd97d016.11.3.1"),sQuery(id+"F2.wireOp",EDGE,"f79f6195-6e67-4fcd-a5d6-908ccd97d016.14.3.1"),sQuery(id+"F2.wireOp",EDGE,"f79f6195-6e67-4fcd-a5d6-908ccd97d016.18.3.1"),sQuery(id+"F2.wireOp",EDGE,"f79f6195-6e67-4fcd-a5d6-908ccd97d016.27.3.1"),sQuery(id+"F2.wireOp",EDGE,"f79f6195-6e67-4fcd-a5d6-908ccd97d016.33.3.1"),sQuery(id+"F2.wireOp",EDGE,"f79f6195-6e67-4fcd-a5d6-908ccd97d016.36.3.1"),sQuery(id+"F2.wireOp",EDGE,"f79f6195-6e67-4fcd-a5d6-908ccd97d016.39.3.1"),sQuery(id+"F2.wireOp",EDGE,"f79f6195-6e67-4fcd-a5d6-908ccd97d016.43.3.1"),sQuery(id+"F2.wireOp",EDGE,"f79f6195-6e67-4fcd-a5d6-908ccd97d016.47.3.1"),sQuery(id+"F2.wireOp",EDGE,"f79f6195-6e67-4fcd-a5d6-908ccd97d016.1.3.2"),sQuery(id+"F2.wireOp",EDGE,"f79f6195-6e67-4fcd-a5d6-908ccd97d016.4.3.2"),sQuery(id+"F2.wireOp",EDGE,"f79f6195-6e67-4fcd-a5d6-908ccd97d016.7.3.2"),sQuery(id+"F2.wireOp",EDGE,"f79f6195-6e67-4fcd-a5d6-908ccd97d016.11.3.2"),sQuery(id+"F2.wireOp",EDGE,"f79f6195-6e67-4fcd-a5d6-908ccd97d016.14.3.2"),sQuery(id+"F2.wireOp",EDGE,"f79f6195-6e67-4fcd-a5d6-908ccd97d016.18.3.2"),sQuery(id+"F2.wireOp",EDGE,"f79f6195-6e67-4fcd-a5d6-908ccd97d016.27.3.2"),sQuery(id+"F2.wireOp",EDGE,"f79f6195-6e67-4fcd-a5d6-908ccd97d016.33.3.2"),sQuery(id+"F2.wireOp",EDGE,"f79f6195-6e67-4fcd-a5d6-908ccd97d016.36.3.2"),sQuery(id+"F2.wireOp",EDGE,"f79f6195-6e67-4fcd-a5d6-908ccd97d016.39.3.2"),sQuery(id+"F2.wireOp",EDGE,"f79f6195-6e67-4fcd-a5d6-908ccd97d016.43.3.2"),sQuery(id+"F2.wireOp",EDGE,"f79f6195-6e67-4fcd-a5d6-908ccd97d016.47.3.2"),sQuery(id+"F2.wireOp",EDGE,"f79f6195-6e67-4fcd-a5d6-908ccd97d016.1.3.3"),sQuery(id+"F2.wireOp",EDGE,"f79f6195-6e67-4fcd-a5d6-908ccd97d016.4.3.3"),sQuery(id+"F2.wireOp",EDGE,"f79f6195-6e67-4fcd-a5d6-908ccd97d016.7.3.3"),sQuery(id+"F2.wireOp",EDGE,"f79f6195-6e67-4fcd-a5d6-908ccd97d016.11.3.3"),sQuery(id+"F2.wireOp",EDGE,"f79f6195-6e67-4fcd-a5d6-908ccd97d016.14.3.3"),sQuery(id+"F2.wireOp",EDGE,"f79f6195-6e67-4fcd-a5d6-908ccd97d016.18.3.3"),sQuery(id+"F2.wireOp",EDGE,"f79f6195-6e67-4fcd-a5d6-908ccd97d016.27.3.3"),sQuery(id+"F2.wireOp",EDGE,"f79f6195-6e67-4fcd-a5d6-908ccd97d016.33.3.3"),sQuery(id+"F2.wireOp",EDGE,"f79f6195-6e67-4fcd-a5d6-908ccd97d016.36.3.3"),sQuery(id+"F2.wireOp",EDGE,"f79f6195-6e67-4fcd-a5d6-908ccd97d016.39.3.3"),sQuery(id+"F2.wireOp",EDGE,"f79f6195-6e67-4fcd-a5d6-908ccd97d016.43.3.3"),sQuery(id+"F2.wireOp",EDGE,"f79f6195-6e67-4fcd-a5d6-908ccd97d016.47.3.3"),sQuery(id+"F2.wireOp",EDGE,"f79f6195-6e67-4fcd-a5d6-908ccd97d016.1.3.4"),sQuery(id+"F2.wireOp",EDGE,"f79f6195-6e67-4fcd-a5d6-908ccd97d016.4.3.4"),sQuery(id+"F2.wireOp",EDGE,"f79f6195-6e67-4fcd-a5d6-908ccd97d016.7.3.4"),sQuery(id+"F2.wireOp",EDGE,"f79f6195-6e67-4fcd-a5d6-908ccd97d016.11.3.4"),sQuery(id+"F2.wireOp",EDGE,"f79f6195-6e67-4fcd-a5d6-908ccd97d016.14.3.4"),sQuery(id+"F2.wireOp",EDGE,"f79f6195-6e67-4fcd-a5d6-908ccd97d016.18.3.4"),sQuery(id+"F2.wireOp",EDGE,"f79f6195-6e67-4fcd-a5d6-908ccd97d016.27.3.4"),sQuery(id+"F2.wireOp",EDGE,"f79f6195-6e67-4fcd-a5d6-908ccd97d016.33.3.4"),sQuery(id+"F2.wireOp",EDGE,"f79f6195-6e67-4fcd-a5d6-908ccd97d016.36.3.4"),sQuery(id+"F2.wireOp",EDGE,"f79f6195-6e67-4fcd-a5d6-908ccd97d016.39.3.4"),sQuery(id+"F2.wireOp",EDGE,"f79f6195-6e67-4fcd-a5d6-908ccd97d016.43.3.4"),sQuery(id+"F2.wireOp",EDGE,"f79f6195-6e67-4fcd-a5d6-908ccd97d016.47.3.4"),sQuery(id+"F2.wireOp",EDGE,"f79f6195-6e67-4fcd-a5d6-908ccd97d016.1.3.5"),sQuery(id+"F2.wireOp",EDGE,"f79f6195-6e67-4fcd-a5d6-908ccd97d016.4.3.5"),sQuery(id+"F2.wireOp",EDGE,"f79f6195-6e67-4fcd-a5d6-908ccd97d016.7.3.5"),sQuery(id+"F2.wireOp",EDGE,"f79f6195-6e67-4fcd-a5d6-908ccd97d016.11.3.5"),sQuery(id+"F2.wireOp",EDGE,"f79f6195-6e67-4fcd-a5d6-908ccd97d016.14.3.5"),sQuery(id+"F2.wireOp",EDGE,"f79f6195-6e67-4fcd-a5d6-908ccd97d016.18.3.5"),sQuery(id+"F2.wireOp",EDGE,"f79f6195-6e67-4fcd-a5d6-908ccd97d016.27.3.5"),sQuery(id+"F2.wireOp",EDGE,"f79f6195-6e67-4fcd-a5d6-908ccd97d016.33.3.5"),sQuery(id+"F2.wireOp",EDGE,"f79f6195-6e67-4fcd-a5d6-908ccd97d016.36.3.5"),sQuery(id+"F2.wireOp",EDGE,"f79f6195-6e67-4fcd-a5d6-908ccd97d016.39.3.5"),sQuery(id+"F2.wireOp",EDGE,"f79f6195-6e67-4fcd-a5d6-908ccd97d016.43.3.5"),sQuery(id+"F2.wireOp",EDGE,"f79f6195-6e67-4fcd-a5d6-908ccd97d016.47.3.5"),sQuery(id+"F2.wireOp",EDGE,"f79f6195-6e67-4fcd-a5d6-908ccd97d016.1.3.6"),sQuery(id+"F2.wireOp",EDGE,"f79f6195-6e67-4fcd-a5d6-908ccd97d016.4.3.6"),sQuery(id+"F2.wireOp",EDGE,"f79f6195-6e67-4fcd-a5d6-908ccd97d016.7.3.6"),sQuery(id+"F2.wireOp",EDGE,"f79f6195-6e67-4fcd-a5d6-908ccd97d016.11.3.6"),sQuery(id+"F2.wireOp",EDGE,"f79f6195-6e67-4fcd-a5d6-908ccd97d016.14.3.6"),sQuery(id+"F2.wireOp",EDGE,"f79f6195-6e67-4fcd-a5d6-908ccd97d016.18.3.6"),sQuery(id+"F2.wireOp",EDGE,"f79f6195-6e67-4fcd-a5d6-908ccd97d016.27.3.6"),sQuery(id+"F2.wireOp",EDGE,"f79f6195-6e67-4fcd-a5d6-908ccd97d016.33.3.6"),sQuery(id+"F2.wireOp",EDGE,"f79f6195-6e67-4fcd-a5d6-908ccd97d016.36.3.6"),sQuery(id+"F2.wireOp",EDGE,"f79f6195-6e67-4fcd-a5d6-908ccd97d016.39.3.6"),sQuery(id+"F2.wireOp",EDGE,"f79f6195-6e67-4fcd-a5d6-908ccd97d016.43.3.6"),sQuery(id+"F2.wireOp",EDGE,"f79f6195-6e67-4fcd-a5d6-908ccd97d016.47.3.6"),sQuery(id+"F2.wireOp",EDGE,"f79f6195-6e67-4fcd-a5d6-908ccd97d016.1.3.7"),sQuery(id+"F2.wireOp",EDGE,"f79f6195-6e67-4fcd-a5d6-908ccd97d016.4.3.7"),sQuery(id+"F2.wireOp",EDGE,"f79f6195-6e67-4fcd-a5d6-908ccd97d016.7.3.7"),sQuery(id+"F2.wireOp",EDGE,"f79f6195-6e67-4fcd-a5d6-908ccd97d016.11.3.7"),sQuery(id+"F2.wireOp",EDGE,"f79f6195-6e67-4fcd-a5d6-908ccd97d016.14.3.7"),sQuery(id+"F2.wireOp",EDGE,"f79f6195-6e67-4fcd-a5d6-908ccd97d016.18.3.7"),sQuery(id+"F2.wireOp",EDGE,"f79f6195-6e67-4fcd-a5d6-908ccd97d016.27.3.7"),sQuery(id+"F2.wireOp",EDGE,"f79f6195-6e67-4fcd-a5d6-908ccd97d016.33.3.7"),sQuery(id+"F2.wireOp",EDGE,"f79f6195-6e67-4fcd-a5d6-908ccd97d016.36.3.7"),sQuery(id+"F2.wireOp",EDGE,"f79f6195-6e67-4fcd-a5d6-908ccd97d016.39.3.7"),sQuery(id+"F2.wireOp",EDGE,"f79f6195-6e67-4fcd-a5d6-908ccd97d016.43.3.7"),sQuery(id+"F2.wireOp",EDGE,"f79f6195-6e67-4fcd-a5d6-908ccd97d016.47.3.7"),sQuery(id+"F2.wireOp",EDGE,"f79f6195-6e67-4fcd-a5d6-908ccd97d016.1.3.8"),sQuery(id+"F2.wireOp",EDGE,"f79f6195-6e67-4fcd-a5d6-908ccd97d016.4.3.8"),sQuery(id+"F2.wireOp",EDGE,"f79f6195-6e67-4fcd-a5d6-908ccd97d016.7.3.8"),sQuery(id+"F2.wireOp",EDGE,"f79f6195-6e67-4fcd-a5d6-908ccd97d016.11.3.8"),sQuery(id+"F2.wireOp",EDGE,"f79f6195-6e67-4fcd-a5d6-908ccd97d016.14.3.8"),sQuery(id+"F2.wireOp",EDGE,"f79f6195-6e67-4fcd-a5d6-908ccd97d016.18.3.8"),sQuery(id+"F2.wireOp",EDGE,"f79f6195-6e67-4fcd-a5d6-908ccd97d016.27.3.8"),sQuery(id+"F2.wireOp",EDGE,"f79f6195-6e67-4fcd-a5d6-908ccd97d016.33.3.8"),sQuery(id+"F2.wireOp",EDGE,"f79f6195-6e67-4fcd-a5d6-908ccd97d016.36.3.8"),sQuery(id+"F2.wireOp",EDGE,"f79f6195-6e67-4fcd-a5d6-908ccd97d016.39.3.8"),sQuery(id+"F2.wireOp",EDGE,"f79f6195-6e67-4fcd-a5d6-908ccd97d016.43.3.8"),sQuery(id+"F2.wireOp",EDGE,"f79f6195-6e67-4fcd-a5d6-908ccd97d016.47.3.8"),sQuery(id+"F2.wireOp",EDGE,"f79f6195-6e67-4fcd-a5d6-908ccd97d016.1.3.9"),sQuery(id+"F2.wireOp",EDGE,"f79f6195-6e67-4fcd-a5d6-908ccd97d016.4.3.9"),sQuery(id+"F2.wireOp",EDGE,"f79f6195-6e67-4fcd-a5d6-908ccd97d016.7.3.9"),sQuery(id+"F2.wireOp",EDGE,"f79f6195-6e67-4fcd-a5d6-908ccd97d016.11.3.9"),sQuery(id+"F2.wireOp",EDGE,"f79f6195-6e67-4fcd-a5d6-908ccd97d016.14.3.9"),sQuery(id+"F2.wireOp",EDGE,"f79f6195-6e67-4fcd-a5d6-908ccd97d016.18.3.9"),sQuery(id+"F2.wireOp",EDGE,"f79f6195-6e67-4fcd-a5d6-908ccd97d016.27.3.9"),sQuery(id+"F2.wireOp",EDGE,"f79f6195-6e67-4fcd-a5d6-908ccd97d016.33.3.9"),sQuery(id+"F2.wireOp",EDGE,"f79f6195-6e67-4fcd-a5d6-908ccd97d016.36.3.9"),sQuery(id+"F2.wireOp",EDGE,"f79f6195-6e67-4fcd-a5d6-908ccd97d016.39.3.9"),sQuery(id+"F2.wireOp",EDGE,"f79f6195-6e67-4fcd-a5d6-908ccd97d016.43.3.9"),sQuery(id+"F2.wireOp",EDGE,"f79f6195-6e67-4fcd-a5d6-908ccd97d016.47.3.9"),sQuery(id+"F2.wireOp",EDGE,"f79f6195-6e67-4fcd-a5d6-908ccd97d016.1.4.0"),sQuery(id+"F2.wireOp",EDGE,"f79f6195-6e67-4fcd-a5d6-908ccd97d016.4.4.0"),sQuery(id+"F2.wireOp",EDGE,"f79f6195-6e67-4fcd-a5d6-908ccd97d016.7.4.0"),sQuery(id+"F2.wireOp",EDGE,"f79f6195-6e67-4fcd-a5d6-908ccd97d016.11.4.0"),sQuery(id+"F2.wireOp",EDGE,"f79f6195-6e67-4fcd-a5d6-908ccd97d016.14.4.0"),sQuery(id+"F2.wireOp",EDGE,"f79f6195-6e67-4fcd-a5d6-908ccd97d016.18.4.0"),sQuery(id+"F2.wireOp",EDGE,"f79f6195-6e67-4fcd-a5d6-908ccd97d016.27.4.0"),sQuery(id+"F2.wireOp",EDGE,"f79f6195-6e67-4fcd-a5d6-908ccd97d016.33.4.0"),sQuery(id+"F2.wireOp",EDGE,"f79f6195-6e67-4fcd-a5d6-908ccd97d016.36.4.0"),sQuery(id+"F2.wireOp",EDGE,"f79f6195-6e67-4fcd-a5d6-908ccd97d016.39.4.0"),sQuery(id+"F2.wireOp",EDGE,"f79f6195-6e67-4fcd-a5d6-908ccd97d016.43.4.0"),sQuery(id+"F2.wireOp",EDGE,"f79f6195-6e67-4fcd-a5d6-908ccd97d016.47.4.0"),sQuery(id+"F2.wireOp",EDGE,"f79f6195-6e67-4fcd-a5d6-908ccd97d016.1.4.1"),sQuery(id+"F2.wireOp",EDGE,"f79f6195-6e67-4fcd-a5d6-908ccd97d016.4.4.1"),sQuery(id+"F2.wireOp",EDGE,"f79f6195-6e67-4fcd-a5d6-908ccd97d016.7.4.1"),sQuery(id+"F2.wireOp",EDGE,"f79f6195-6e67-4fcd-a5d6-908ccd97d016.11.4.1"),sQuery(id+"F2.wireOp",EDGE,"f79f6195-6e67-4fcd-a5d6-908ccd97d016.14.4.1"),sQuery(id+"F2.wireOp",EDGE,"f79f6195-6e67-4fcd-a5d6-908ccd97d016.18.4.1"),sQuery(id+"F2.wireOp",EDGE,"f79f6195-6e67-4fcd-a5d6-908ccd97d016.27.4.1"),sQuery(id+"F2.wireOp",EDGE,"f79f6195-6e67-4fcd-a5d6-908ccd97d016.33.4.1"),sQuery(id+"F2.wireOp",EDGE,"f79f6195-6e67-4fcd-a5d6-908ccd97d016.36.4.1"),sQuery(id+"F2.wireOp",EDGE,"f79f6195-6e67-4fcd-a5d6-908ccd97d016.39.4.1"),sQuery(id+"F2.wireOp",EDGE,"f79f6195-6e67-4fcd-a5d6-908ccd97d016.43.4.1"),sQuery(id+"F2.wireOp",EDGE,"f79f6195-6e67-4fcd-a5d6-908ccd97d016.47.4.1"),sQuery(id+"F2.wireOp",EDGE,"f79f6195-6e67-4fcd-a5d6-908ccd97d016.1.4.2"),sQuery(id+"F2.wireOp",EDGE,"f79f6195-6e67-4fcd-a5d6-908ccd97d016.4.4.2"),sQuery(id+"F2.wireOp",EDGE,"f79f6195-6e67-4fcd-a5d6-908ccd97d016.7.4.2"),sQuery(id+"F2.wireOp",EDGE,"f79f6195-6e67-4fcd-a5d6-908ccd97d016.11.4.2"),sQuery(id+"F2.wireOp",EDGE,"f79f6195-6e67-4fcd-a5d6-908ccd97d016.14.4.2"),sQuery(id+"F2.wireOp",EDGE,"f79f6195-6e67-4fcd-a5d6-908ccd97d016.18.4.2"),sQuery(id+"F2.wireOp",EDGE,"f79f6195-6e67-4fcd-a5d6-908ccd97d016.27.4.2"),sQuery(id+"F2.wireOp",EDGE,"f79f6195-6e67-4fcd-a5d6-908ccd97d016.33.4.2"),sQuery(id+"F2.wireOp",EDGE,"f79f6195-6e67-4fcd-a5d6-908ccd97d016.36.4.2"),sQuery(id+"F2.wireOp",EDGE,"f79f6195-6e67-4fcd-a5d6-908ccd97d016.39.4.2"),sQuery(id+"F2.wireOp",EDGE,"f79f6195-6e67-4fcd-a5d6-908ccd97d016.43.4.2"),sQuery(id+"F2.wireOp",EDGE,"f79f6195-6e67-4fcd-a5d6-908ccd97d016.47.4.2"),sQuery(id+"F2.wireOp",EDGE,"f79f6195-6e67-4fcd-a5d6-908ccd97d016.1.4.3"),sQuery(id+"F2.wireOp",EDGE,"f79f6195-6e67-4fcd-a5d6-908ccd97d016.4.4.3"),sQuery(id+"F2.wireOp",EDGE,"f79f6195-6e67-4fcd-a5d6-908ccd97d016.7.4.3"),sQuery(id+"F2.wireOp",EDGE,"f79f6195-6e67-4fcd-a5d6-908ccd97d016.11.4.3"),sQuery(id+"F2.wireOp",EDGE,"f79f6195-6e67-4fcd-a5d6-908ccd97d016.14.4.3"),sQuery(id+"F2.wireOp",EDGE,"f79f6195-6e67-4fcd-a5d6-908ccd97d016.18.4.3"),sQuery(id+"F2.wireOp",EDGE,"f79f6195-6e67-4fcd-a5d6-908ccd97d016.27.4.3"),sQuery(id+"F2.wireOp",EDGE,"f79f6195-6e67-4fcd-a5d6-908ccd97d016.33.4.3"),sQuery(id+"F2.wireOp",EDGE,"f79f6195-6e67-4fcd-a5d6-908ccd97d016.36.4.3"),sQuery(id+"F2.wireOp",EDGE,"f79f6195-6e67-4fcd-a5d6-908ccd97d016.39.4.3"),sQuery(id+"F2.wireOp",EDGE,"f79f6195-6e67-4fcd-a5d6-908ccd97d016.43.4.3"),sQuery(id+"F2.wireOp",EDGE,"f79f6195-6e67-4fcd-a5d6-908ccd97d016.47.4.3"),sQuery(id+"F2.wireOp",EDGE,"f79f6195-6e67-4fcd-a5d6-908ccd97d016.1.4.4"),sQuery(id+"F2.wireOp",EDGE,"f79f6195-6e67-4fcd-a5d6-908ccd97d016.4.4.4"),sQuery(id+"F2.wireOp",EDGE,"f79f6195-6e67-4fcd-a5d6-908ccd97d016.7.4.4"),sQuery(id+"F2.wireOp",EDGE,"f79f6195-6e67-4fcd-a5d6-908ccd97d016.11.4.4"),sQuery(id+"F2.wireOp",EDGE,"f79f6195-6e67-4fcd-a5d6-908ccd97d016.14.4.4"),sQuery(id+"F2.wireOp",EDGE,"f79f6195-6e67-4fcd-a5d6-908ccd97d016.18.4.4"),sQuery(id+"F2.wireOp",EDGE,"f79f6195-6e67-4fcd-a5d6-908ccd97d016.27.4.4"),sQuery(id+"F2.wireOp",EDGE,"f79f6195-6e67-4fcd-a5d6-908ccd97d016.33.4.4"),sQuery(id+"F2.wireOp",EDGE,"f79f6195-6e67-4fcd-a5d6-908ccd97d016.36.4.4"),sQuery(id+"F2.wireOp",EDGE,"f79f6195-6e67-4fcd-a5d6-908ccd97d016.39.4.4"),sQuery(id+"F2.wireOp",EDGE,"f79f6195-6e67-4fcd-a5d6-908ccd97d016.43.4.4"),sQuery(id+"F2.wireOp",EDGE,"f79f6195-6e67-4fcd-a5d6-908ccd97d016.47.4.4"),sQuery(id+"F2.wireOp",EDGE,"f79f6195-6e67-4fcd-a5d6-908ccd97d016.1.4.5"),sQuery(id+"F2.wireOp",EDGE,"f79f6195-6e67-4fcd-a5d6-908ccd97d016.4.4.5"),sQuery(id+"F2.wireOp",EDGE,"f79f6195-6e67-4fcd-a5d6-908ccd97d016.7.4.5"),sQuery(id+"F2.wireOp",EDGE,"f79f6195-6e67-4fcd-a5d6-908ccd97d016.11.4.5"),sQuery(id+"F2.wireOp",EDGE,"f79f6195-6e67-4fcd-a5d6-908ccd97d016.14.4.5"),sQuery(id+"F2.wireOp",EDGE,"f79f6195-6e67-4fcd-a5d6-908ccd97d016.18.4.5"),sQuery(id+"F2.wireOp",EDGE,"f79f6195-6e67-4fcd-a5d6-908ccd97d016.27.4.5"),sQuery(id+"F2.wireOp",EDGE,"f79f6195-6e67-4fcd-a5d6-908ccd97d016.33.4.5"),sQuery(id+"F2.wireOp",EDGE,"f79f6195-6e67-4fcd-a5d6-908ccd97d016.36.4.5"),sQuery(id+"F2.wireOp",EDGE,"f79f6195-6e67-4fcd-a5d6-908ccd97d016.39.4.5"),sQuery(id+"F2.wireOp",EDGE,"f79f6195-6e67-4fcd-a5d6-908ccd97d016.43.4.5"),sQuery(id+"F2.wireOp",EDGE,"f79f6195-6e67-4fcd-a5d6-908ccd97d016.47.4.5"),sQuery(id+"F2.wireOp",EDGE,"f79f6195-6e67-4fcd-a5d6-908ccd97d016.1.4.6"),sQuery(id+"F2.wireOp",EDGE,"f79f6195-6e67-4fcd-a5d6-908ccd97d016.4.4.6"),sQuery(id+"F2.wireOp",EDGE,"f79f6195-6e67-4fcd-a5d6-908ccd97d016.7.4.6"),sQuery(id+"F2.wireOp",EDGE,"f79f6195-6e67-4fcd-a5d6-908ccd97d016.11.4.6"),sQuery(id+"F2.wireOp",EDGE,"f79f6195-6e67-4fcd-a5d6-908ccd97d016.14.4.6"),sQuery(id+"F2.wireOp",EDGE,"f79f6195-6e67-4fcd-a5d6-908ccd97d016.18.4.6"),sQuery(id+"F2.wireOp",EDGE,"f79f6195-6e67-4fcd-a5d6-908ccd97d016.27.4.6"),sQuery(id+"F2.wireOp",EDGE,"f79f6195-6e67-4fcd-a5d6-908ccd97d016.33.4.6"),sQuery(id+"F2.wireOp",EDGE,"f79f6195-6e67-4fcd-a5d6-908ccd97d016.36.4.6"),sQuery(id+"F2.wireOp",EDGE,"f79f6195-6e67-4fcd-a5d6-908ccd97d016.39.4.6"),sQuery(id+"F2.wireOp",EDGE,"f79f6195-6e67-4fcd-a5d6-908ccd97d016.43.4.6"),sQuery(id+"F2.wireOp",EDGE,"f79f6195-6e67-4fcd-a5d6-908ccd97d016.47.4.6"),sQuery(id+"F2.wireOp",EDGE,"f79f6195-6e67-4fcd-a5d6-908ccd97d016.1.4.7"),sQuery(id+"F2.wireOp",EDGE,"f79f6195-6e67-4fcd-a5d6-908ccd97d016.4.4.7"),sQuery(id+"F2.wireOp",EDGE,"f79f6195-6e67-4fcd-a5d6-908ccd97d016.7.4.7"),sQuery(id+"F2.wireOp",EDGE,"f79f6195-6e67-4fcd-a5d6-908ccd97d016.11.4.7"),sQuery(id+"F2.wireOp",EDGE,"f79f6195-6e67-4fcd-a5d6-908ccd97d016.14.4.7"),sQuery(id+"F2.wireOp",EDGE,"f79f6195-6e67-4fcd-a5d6-908ccd97d016.18.4.7"),sQuery(id+"F2.wireOp",EDGE,"f79f6195-6e67-4fcd-a5d6-908ccd97d016.27.4.7"),sQuery(id+"F2.wireOp",EDGE,"f79f6195-6e67-4fcd-a5d6-908ccd97d016.33.4.7"),sQuery(id+"F2.wireOp",EDGE,"f79f6195-6e67-4fcd-a5d6-908ccd97d016.36.4.7"),sQuery(id+"F2.wireOp",EDGE,"f79f6195-6e67-4fcd-a5d6-908ccd97d016.39.4.7"),sQuery(id+"F2.wireOp",EDGE,"f79f6195-6e67-4fcd-a5d6-908ccd97d016.43.4.7"),sQuery(id+"F2.wireOp",EDGE,"f79f6195-6e67-4fcd-a5d6-908ccd97d016.47.4.7"),sQuery(id+"F2.wireOp",EDGE,"f79f6195-6e67-4fcd-a5d6-908ccd97d016.1.4.8"),sQuery(id+"F2.wireOp",EDGE,"f79f6195-6e67-4fcd-a5d6-908ccd97d016.4.4.8"),sQuery(id+"F2.wireOp",EDGE,"f79f6195-6e67-4fcd-a5d6-908ccd97d016.7.4.8"),sQuery(id+"F2.wireOp",EDGE,"f79f6195-6e67-4fcd-a5d6-908ccd97d016.11.4.8"),sQuery(id+"F2.wireOp",EDGE,"f79f6195-6e67-4fcd-a5d6-908ccd97d016.14.4.8"),sQuery(id+"F2.wireOp",EDGE,"f79f6195-6e67-4fcd-a5d6-908ccd97d016.18.4.8"),sQuery(id+"F2.wireOp",EDGE,"f79f6195-6e67-4fcd-a5d6-908ccd97d016.27.4.8"),sQuery(id+"F2.wireOp",EDGE,"f79f6195-6e67-4fcd-a5d6-908ccd97d016.33.4.8"),sQuery(id+"F2.wireOp",EDGE,"f79f6195-6e67-4fcd-a5d6-908ccd97d016.36.4.8"),sQuery(id+"F2.wireOp",EDGE,"f79f6195-6e67-4fcd-a5d6-908ccd97d016.39.4.8"),sQuery(id+"F2.wireOp",EDGE,"f79f6195-6e67-4fcd-a5d6-908ccd97d016.43.4.8"),sQuery(id+"F2.wireOp",EDGE,"f79f6195-6e67-4fcd-a5d6-908ccd97d016.47.4.8"),sQuery(id+"F2.wireOp",EDGE,"f79f6195-6e67-4fcd-a5d6-908ccd97d016.1.4.9"),sQuery(id+"F2.wireOp",EDGE,"f79f6195-6e67-4fcd-a5d6-908ccd97d016.4.4.9"),sQuery(id+"F2.wireOp",EDGE,"f79f6195-6e67-4fcd-a5d6-908ccd97d016.7.4.9"),sQuery(id+"F2.wireOp",EDGE,"f79f6195-6e67-4fcd-a5d6-908ccd97d016.11.4.9"),sQuery(id+"F2.wireOp",EDGE,"f79f6195-6e67-4fcd-a5d6-908ccd97d016.14.4.9"),sQuery(id+"F2.wireOp",EDGE,"f79f6195-6e67-4fcd-a5d6-908ccd97d016.18.4.9"),sQuery(id+"F2.wireOp",EDGE,"f79f6195-6e67-4fcd-a5d6-908ccd97d016.27.4.9"),sQuery(id+"F2.wireOp",EDGE,"f79f6195-6e67-4fcd-a5d6-908ccd97d016.33.4.9"),sQuery(id+"F2.wireOp",EDGE,"f79f6195-6e67-4fcd-a5d6-908ccd97d016.36.4.9"),sQuery(id+"F2.wireOp",EDGE,"f79f6195-6e67-4fcd-a5d6-908ccd97d016.39.4.9"),sQuery(id+"F2.wireOp",EDGE,"f79f6195-6e67-4fcd-a5d6-908ccd97d016.43.4.9"),sQuery(id+"F2.wireOp",EDGE,"f79f6195-6e67-4fcd-a5d6-908ccd97d016.47.4.9"),sQuery(id+"F2.wireOp",EDGE,"f79f6195-6e67-4fcd-a5d6-908ccd97d016.1.5.0"),sQuery(id+"F2.wireOp",EDGE,"f79f6195-6e67-4fcd-a5d6-908ccd97d016.4.5.0"),sQuery(id+"F2.wireOp",EDGE,"f79f6195-6e67-4fcd-a5d6-908ccd97d016.7.5.0"),sQuery(id+"F2.wireOp",EDGE,"f79f6195-6e67-4fcd-a5d6-908ccd97d016.11.5.0"),sQuery(id+"F2.wireOp",EDGE,"f79f6195-6e67-4fcd-a5d6-908ccd97d016.14.5.0"),sQuery(id+"F2.wireOp",EDGE,"f79f6195-6e67-4fcd-a5d6-908ccd97d016.18.5.0"),sQuery(id+"F2.wireOp",EDGE,"f79f6195-6e67-4fcd-a5d6-908ccd97d016.27.5.0"),sQuery(id+"F2.wireOp",EDGE,"f79f6195-6e67-4fcd-a5d6-908ccd97d016.33.5.0"),sQuery(id+"F2.wireOp",EDGE,"f79f6195-6e67-4fcd-a5d6-908ccd97d016.36.5.0"),sQuery(id+"F2.wireOp",EDGE,"f79f6195-6e67-4fcd-a5d6-908ccd97d016.39.5.0"),sQuery(id+"F2.wireOp",EDGE,"f79f6195-6e67-4fcd-a5d6-908ccd97d016.43.5.0"),sQuery(id+"F2.wireOp",EDGE,"f79f6195-6e67-4fcd-a5d6-908ccd97d016.47.5.0"),sQuery(id+"F2.wireOp",EDGE,"f79f6195-6e67-4fcd-a5d6-908ccd97d016.1.5.1"),sQuery(id+"F2.wireOp",EDGE,"f79f6195-6e67-4fcd-a5d6-908ccd97d016.4.5.1"),sQuery(id+"F2.wireOp",EDGE,"f79f6195-6e67-4fcd-a5d6-908ccd97d016.7.5.1"),sQuery(id+"F2.wireOp",EDGE,"f79f6195-6e67-4fcd-a5d6-908ccd97d016.11.5.1"),sQuery(id+"F2.wireOp",EDGE,"f79f6195-6e67-4fcd-a5d6-908ccd97d016.14.5.1"),sQuery(id+"F2.wireOp",EDGE,"f79f6195-6e67-4fcd-a5d6-908ccd97d016.18.5.1"),sQuery(id+"F2.wireOp",EDGE,"f79f6195-6e67-4fcd-a5d6-908ccd97d016.27.5.1"),sQuery(id+"F2.wireOp",EDGE,"f79f6195-6e67-4fcd-a5d6-908ccd97d016.33.5.1"),sQuery(id+"F2.wireOp",EDGE,"f79f6195-6e67-4fcd-a5d6-908ccd97d016.36.5.1"),sQuery(id+"F2.wireOp",EDGE,"f79f6195-6e67-4fcd-a5d6-908ccd97d016.39.5.1"),sQuery(id+"F2.wireOp",EDGE,"f79f6195-6e67-4fcd-a5d6-908ccd97d016.43.5.1"),sQuery(id+"F2.wireOp",EDGE,"f79f6195-6e67-4fcd-a5d6-908ccd97d016.47.5.1"),sQuery(id+"F2.wireOp",EDGE,"f79f6195-6e67-4fcd-a5d6-908ccd97d016.1.5.2"),sQuery(id+"F2.wireOp",EDGE,"f79f6195-6e67-4fcd-a5d6-908ccd97d016.4.5.2"),sQuery(id+"F2.wireOp",EDGE,"f79f6195-6e67-4fcd-a5d6-908ccd97d016.7.5.2"),sQuery(id+"F2.wireOp",EDGE,"f79f6195-6e67-4fcd-a5d6-908ccd97d016.11.5.2"),sQuery(id+"F2.wireOp",EDGE,"f79f6195-6e67-4fcd-a5d6-908ccd97d016.14.5.2"),sQuery(id+"F2.wireOp",EDGE,"f79f6195-6e67-4fcd-a5d6-908ccd97d016.18.5.2"),sQuery(id+"F2.wireOp",EDGE,"f79f6195-6e67-4fcd-a5d6-908ccd97d016.27.5.2"),sQuery(id+"F2.wireOp",EDGE,"f79f6195-6e67-4fcd-a5d6-908ccd97d016.33.5.2"),sQuery(id+"F2.wireOp",EDGE,"f79f6195-6e67-4fcd-a5d6-908ccd97d016.36.5.2"),sQuery(id+"F2.wireOp",EDGE,"f79f6195-6e67-4fcd-a5d6-908ccd97d016.39.5.2"),sQuery(id+"F2.wireOp",EDGE,"f79f6195-6e67-4fcd-a5d6-908ccd97d016.43.5.2"),sQuery(id+"F2.wireOp",EDGE,"f79f6195-6e67-4fcd-a5d6-908ccd97d016.47.5.2"),sQuery(id+"F2.wireOp",EDGE,"f79f6195-6e67-4fcd-a5d6-908ccd97d016.1.5.3"),sQuery(id+"F2.wireOp",EDGE,"f79f6195-6e67-4fcd-a5d6-908ccd97d016.4.5.3"),sQuery(id+"F2.wireOp",EDGE,"f79f6195-6e67-4fcd-a5d6-908ccd97d016.7.5.3"),sQuery(id+"F2.wireOp",EDGE,"f79f6195-6e67-4fcd-a5d6-908ccd97d016.11.5.3"),sQuery(id+"F2.wireOp",EDGE,"f79f6195-6e67-4fcd-a5d6-908ccd97d016.14.5.3"),sQuery(id+"F2.wireOp",EDGE,"f79f6195-6e67-4fcd-a5d6-908ccd97d016.18.5.3"),sQuery(id+"F2.wireOp",EDGE,"f79f6195-6e67-4fcd-a5d6-908ccd97d016.27.5.3"),sQuery(id+"F2.wireOp",EDGE,"f79f6195-6e67-4fcd-a5d6-908ccd97d016.33.5.3"),sQuery(id+"F2.wireOp",EDGE,"f79f6195-6e67-4fcd-a5d6-908ccd97d016.36.5.3"),sQuery(id+"F2.wireOp",EDGE,"f79f6195-6e67-4fcd-a5d6-908ccd97d016.39.5.3"),sQuery(id+"F2.wireOp",EDGE,"f79f6195-6e67-4fcd-a5d6-908ccd97d016.43.5.3"),sQuery(id+"F2.wireOp",EDGE,"f79f6195-6e67-4fcd-a5d6-908ccd97d016.47.5.3"),sQuery(id+"F2.wireOp",EDGE,"f79f6195-6e67-4fcd-a5d6-908ccd97d016.1.5.4"),sQuery(id+"F2.wireOp",EDGE,"f79f6195-6e67-4fcd-a5d6-908ccd97d016.4.5.4"),sQuery(id+"F2.wireOp",EDGE,"f79f6195-6e67-4fcd-a5d6-908ccd97d016.7.5.4"),sQuery(id+"F2.wireOp",EDGE,"f79f6195-6e67-4fcd-a5d6-908ccd97d016.11.5.4"),sQuery(id+"F2.wireOp",EDGE,"f79f6195-6e67-4fcd-a5d6-908ccd97d016.14.5.4"),sQuery(id+"F2.wireOp",EDGE,"f79f6195-6e67-4fcd-a5d6-908ccd97d016.18.5.4"),sQuery(id+"F2.wireOp",EDGE,"f79f6195-6e67-4fcd-a5d6-908ccd97d016.27.5.4"),sQuery(id+"F2.wireOp",EDGE,"f79f6195-6e67-4fcd-a5d6-908ccd97d016.33.5.4"),sQuery(id+"F2.wireOp",EDGE,"f79f6195-6e67-4fcd-a5d6-908ccd97d016.36.5.4"),sQuery(id+"F2.wireOp",EDGE,"f79f6195-6e67-4fcd-a5d6-908ccd97d016.39.5.4"),sQuery(id+"F2.wireOp",EDGE,"f79f6195-6e67-4fcd-a5d6-908ccd97d016.43.5.4"),sQuery(id+"F2.wireOp",EDGE,"f79f6195-6e67-4fcd-a5d6-908ccd97d016.47.5.4"),sQuery(id+"F2.wireOp",EDGE,"f79f6195-6e67-4fcd-a5d6-908ccd97d016.1.5.5"),sQuery(id+"F2.wireOp",EDGE,"f79f6195-6e67-4fcd-a5d6-908ccd97d016.4.5.5"),sQuery(id+"F2.wireOp",EDGE,"f79f6195-6e67-4fcd-a5d6-908ccd97d016.7.5.5"),sQuery(id+"F2.wireOp",EDGE,"f79f6195-6e67-4fcd-a5d6-908ccd97d016.11.5.5"),sQuery(id+"F2.wireOp",EDGE,"f79f6195-6e67-4fcd-a5d6-908ccd97d016.14.5.5"),sQuery(id+"F2.wireOp",EDGE,"f79f6195-6e67-4fcd-a5d6-908ccd97d016.18.5.5"),sQuery(id+"F2.wireOp",EDGE,"f79f6195-6e67-4fcd-a5d6-908ccd97d016.27.5.5"),sQuery(id+"F2.wireOp",EDGE,"f79f6195-6e67-4fcd-a5d6-908ccd97d016.33.5.5"),sQuery(id+"F2.wireOp",EDGE,"f79f6195-6e67-4fcd-a5d6-908ccd97d016.36.5.5"),sQuery(id+"F2.wireOp",EDGE,"f79f6195-6e67-4fcd-a5d6-908ccd97d016.39.5.5"),sQuery(id+"F2.wireOp",EDGE,"f79f6195-6e67-4fcd-a5d6-908ccd97d016.43.5.5"),sQuery(id+"F2.wireOp",EDGE,"f79f6195-6e67-4fcd-a5d6-908ccd97d016.47.5.5"),sQuery(id+"F2.wireOp",EDGE,"f79f6195-6e67-4fcd-a5d6-908ccd97d016.1.5.6"),sQuery(id+"F2.wireOp",EDGE,"f79f6195-6e67-4fcd-a5d6-908ccd97d016.4.5.6"),sQuery(id+"F2.wireOp",EDGE,"f79f6195-6e67-4fcd-a5d6-908ccd97d016.7.5.6"),sQuery(id+"F2.wireOp",EDGE,"f79f6195-6e67-4fcd-a5d6-908ccd97d016.11.5.6"),sQuery(id+"F2.wireOp",EDGE,"f79f6195-6e67-4fcd-a5d6-908ccd97d016.14.5.6"),sQuery(id+"F2.wireOp",EDGE,"f79f6195-6e67-4fcd-a5d6-908ccd97d016.18.5.6"),sQuery(id+"F2.wireOp",EDGE,"f79f6195-6e67-4fcd-a5d6-908ccd97d016.27.5.6"),sQuery(id+"F2.wireOp",EDGE,"f79f6195-6e67-4fcd-a5d6-908ccd97d016.33.5.6"),sQuery(id+"F2.wireOp",EDGE,"f79f6195-6e67-4fcd-a5d6-908ccd97d016.36.5.6"),sQuery(id+"F2.wireOp",EDGE,"f79f6195-6e67-4fcd-a5d6-908ccd97d016.39.5.6"),sQuery(id+"F2.wireOp",EDGE,"f79f6195-6e67-4fcd-a5d6-908ccd97d016.43.5.6"),sQuery(id+"F2.wireOp",EDGE,"f79f6195-6e67-4fcd-a5d6-908ccd97d016.47.5.6"),sQuery(id+"F2.wireOp",EDGE,"f79f6195-6e67-4fcd-a5d6-908ccd97d016.1.5.7"),sQuery(id+"F2.wireOp",EDGE,"f79f6195-6e67-4fcd-a5d6-908ccd97d016.4.5.7"),sQuery(id+"F2.wireOp",EDGE,"f79f6195-6e67-4fcd-a5d6-908ccd97d016.7.5.7"),sQuery(id+"F2.wireOp",EDGE,"f79f6195-6e67-4fcd-a5d6-908ccd97d016.11.5.7"),sQuery(id+"F2.wireOp",EDGE,"f79f6195-6e67-4fcd-a5d6-908ccd97d016.14.5.7"),sQuery(id+"F2.wireOp",EDGE,"f79f6195-6e67-4fcd-a5d6-908ccd97d016.18.5.7"),sQuery(id+"F2.wireOp",EDGE,"f79f6195-6e67-4fcd-a5d6-908ccd97d016.27.5.7"),sQuery(id+"F2.wireOp",EDGE,"f79f6195-6e67-4fcd-a5d6-908ccd97d016.33.5.7"),sQuery(id+"F2.wireOp",EDGE,"f79f6195-6e67-4fcd-a5d6-908ccd97d016.36.5.7"),sQuery(id+"F2.wireOp",EDGE,"f79f6195-6e67-4fcd-a5d6-908ccd97d016.39.5.7"),sQuery(id+"F2.wireOp",EDGE,"f79f6195-6e67-4fcd-a5d6-908ccd97d016.43.5.7"),sQuery(id+"F2.wireOp",EDGE,"f79f6195-6e67-4fcd-a5d6-908ccd97d016.47.5.7"),sQuery(id+"F2.wireOp",EDGE,"f79f6195-6e67-4fcd-a5d6-908ccd97d016.1.5.8"),sQuery(id+"F2.wireOp",EDGE,"f79f6195-6e67-4fcd-a5d6-908ccd97d016.4.5.8"),sQuery(id+"F2.wireOp",EDGE,"f79f6195-6e67-4fcd-a5d6-908ccd97d016.7.5.8"),sQuery(id+"F2.wireOp",EDGE,"f79f6195-6e67-4fcd-a5d6-908ccd97d016.11.5.8"),sQuery(id+"F2.wireOp",EDGE,"f79f6195-6e67-4fcd-a5d6-908ccd97d016.14.5.8"),sQuery(id+"F2.wireOp",EDGE,"f79f6195-6e67-4fcd-a5d6-908ccd97d016.18.5.8"),sQuery(id+"F2.wireOp",EDGE,"f79f6195-6e67-4fcd-a5d6-908ccd97d016.27.5.8"),sQuery(id+"F2.wireOp",EDGE,"f79f6195-6e67-4fcd-a5d6-908ccd97d016.33.5.8"),sQuery(id+"F2.wireOp",EDGE,"f79f6195-6e67-4fcd-a5d6-908ccd97d016.36.5.8"),sQuery(id+"F2.wireOp",EDGE,"f79f6195-6e67-4fcd-a5d6-908ccd97d016.39.5.8"),sQuery(id+"F2.wireOp",EDGE,"f79f6195-6e67-4fcd-a5d6-908ccd97d016.43.5.8"),sQuery(id+"F2.wireOp",EDGE,"f79f6195-6e67-4fcd-a5d6-908ccd97d016.47.5.8"),sQuery(id+"F2.wireOp",EDGE,"f79f6195-6e67-4fcd-a5d6-908ccd97d016.1.5.9"),sQuery(id+"F2.wireOp",EDGE,"f79f6195-6e67-4fcd-a5d6-908ccd97d016.4.5.9"),sQuery(id+"F2.wireOp",EDGE,"f79f6195-6e67-4fcd-a5d6-908ccd97d016.7.5.9"),sQuery(id+"F2.wireOp",EDGE,"f79f6195-6e67-4fcd-a5d6-908ccd97d016.11.5.9"),sQuery(id+"F2.wireOp",EDGE,"f79f6195-6e67-4fcd-a5d6-908ccd97d016.14.5.9"),sQuery(id+"F2.wireOp",EDGE,"f79f6195-6e67-4fcd-a5d6-908ccd97d016.18.5.9"),sQuery(id+"F2.wireOp",EDGE,"f79f6195-6e67-4fcd-a5d6-908ccd97d016.27.5.9"),sQuery(id+"F2.wireOp",EDGE,"f79f6195-6e67-4fcd-a5d6-908ccd97d016.33.5.9"),sQuery(id+"F2.wireOp",EDGE,"f79f6195-6e67-4fcd-a5d6-908ccd97d016.36.5.9"),sQuery(id+"F2.wireOp",EDGE,"f79f6195-6e67-4fcd-a5d6-908ccd97d016.39.5.9"),sQuery(id+"F2.wireOp",EDGE,"f79f6195-6e67-4fcd-a5d6-908ccd97d016.43.5.9"),sQuery(id+"F2.wireOp",EDGE,"f79f6195-6e67-4fcd-a5d6-908ccd97d016.47.5.9"),sQuery(id+"F2.wireOp",EDGE,"f79f6195-6e67-4fcd-a5d6-908ccd97d016.1.6.0"),sQuery(id+"F2.wireOp",EDGE,"f79f6195-6e67-4fcd-a5d6-908ccd97d016.4.6.0"),sQuery(id+"F2.wireOp",EDGE,"f79f6195-6e67-4fcd-a5d6-908ccd97d016.7.6.0"),sQuery(id+"F2.wireOp",EDGE,"f79f6195-6e67-4fcd-a5d6-908ccd97d016.11.6.0"),sQuery(id+"F2.wireOp",EDGE,"f79f6195-6e67-4fcd-a5d6-908ccd97d016.14.6.0"),sQuery(id+"F2.wireOp",EDGE,"f79f6195-6e67-4fcd-a5d6-908ccd97d016.18.6.0"),sQuery(id+"F2.wireOp",EDGE,"f79f6195-6e67-4fcd-a5d6-908ccd97d016.27.6.0"),sQuery(id+"F2.wireOp",EDGE,"f79f6195-6e67-4fcd-a5d6-908ccd97d016.33.6.0"),sQuery(id+"F2.wireOp",EDGE,"f79f6195-6e67-4fcd-a5d6-908ccd97d016.36.6.0"),sQuery(id+"F2.wireOp",EDGE,"f79f6195-6e67-4fcd-a5d6-908ccd97d016.39.6.0"),sQuery(id+"F2.wireOp",EDGE,"f79f6195-6e67-4fcd-a5d6-908ccd97d016.43.6.0"),sQuery(id+"F2.wireOp",EDGE,"f79f6195-6e67-4fcd-a5d6-908ccd97d016.47.6.0"),sQuery(id+"F2.wireOp",EDGE,"f79f6195-6e67-4fcd-a5d6-908ccd97d016.1.6.1"),sQuery(id+"F2.wireOp",EDGE,"f79f6195-6e67-4fcd-a5d6-908ccd97d016.4.6.1"),sQuery(id+"F2.wireOp",EDGE,"f79f6195-6e67-4fcd-a5d6-908ccd97d016.7.6.1"),sQuery(id+"F2.wireOp",EDGE,"f79f6195-6e67-4fcd-a5d6-908ccd97d016.11.6.1"),sQuery(id+"F2.wireOp",EDGE,"f79f6195-6e67-4fcd-a5d6-908ccd97d016.14.6.1"),sQuery(id+"F2.wireOp",EDGE,"f79f6195-6e67-4fcd-a5d6-908ccd97d016.18.6.1"),sQuery(id+"F2.wireOp",EDGE,"f79f6195-6e67-4fcd-a5d6-908ccd97d016.27.6.1"),sQuery(id+"F2.wireOp",EDGE,"f79f6195-6e67-4fcd-a5d6-908ccd97d016.33.6.1"),sQuery(id+"F2.wireOp",EDGE,"f79f6195-6e67-4fcd-a5d6-908ccd97d016.36.6.1"),sQuery(id+"F2.wireOp",EDGE,"f79f6195-6e67-4fcd-a5d6-908ccd97d016.39.6.1"),sQuery(id+"F2.wireOp",EDGE,"f79f6195-6e67-4fcd-a5d6-908ccd97d016.43.6.1"),sQuery(id+"F2.wireOp",EDGE,"f79f6195-6e67-4fcd-a5d6-908ccd97d016.47.6.1"),sQuery(id+"F2.wireOp",EDGE,"f79f6195-6e67-4fcd-a5d6-908ccd97d016.1.6.2"),sQuery(id+"F2.wireOp",EDGE,"f79f6195-6e67-4fcd-a5d6-908ccd97d016.4.6.2"),sQuery(id+"F2.wireOp",EDGE,"f79f6195-6e67-4fcd-a5d6-908ccd97d016.7.6.2"),sQuery(id+"F2.wireOp",EDGE,"f79f6195-6e67-4fcd-a5d6-908ccd97d016.11.6.2"),sQuery(id+"F2.wireOp",EDGE,"f79f6195-6e67-4fcd-a5d6-908ccd97d016.14.6.2"),sQuery(id+"F2.wireOp",EDGE,"f79f6195-6e67-4fcd-a5d6-908ccd97d016.18.6.2"),sQuery(id+"F2.wireOp",EDGE,"f79f6195-6e67-4fcd-a5d6-908ccd97d016.27.6.2"),sQuery(id+"F2.wireOp",EDGE,"f79f6195-6e67-4fcd-a5d6-908ccd97d016.33.6.2"),sQuery(id+"F2.wireOp",EDGE,"f79f6195-6e67-4fcd-a5d6-908ccd97d016.36.6.2"),sQuery(id+"F2.wireOp",EDGE,"f79f6195-6e67-4fcd-a5d6-908ccd97d016.39.6.2"),sQuery(id+"F2.wireOp",EDGE,"f79f6195-6e67-4fcd-a5d6-908ccd97d016.43.6.2"),sQuery(id+"F2.wireOp",EDGE,"f79f6195-6e67-4fcd-a5d6-908ccd97d016.47.6.2"),sQuery(id+"F2.wireOp",EDGE,"f79f6195-6e67-4fcd-a5d6-908ccd97d016.1.6.3"),sQuery(id+"F2.wireOp",EDGE,"f79f6195-6e67-4fcd-a5d6-908ccd97d016.4.6.3"),sQuery(id+"F2.wireOp",EDGE,"f79f6195-6e67-4fcd-a5d6-908ccd97d016.7.6.3"),sQuery(id+"F2.wireOp",EDGE,"f79f6195-6e67-4fcd-a5d6-908ccd97d016.11.6.3"),sQuery(id+"F2.wireOp",EDGE,"f79f6195-6e67-4fcd-a5d6-908ccd97d016.14.6.3"),sQuery(id+"F2.wireOp",EDGE,"f79f6195-6e67-4fcd-a5d6-908ccd97d016.18.6.3"),sQuery(id+"F2.wireOp",EDGE,"f79f6195-6e67-4fcd-a5d6-908ccd97d016.27.6.3"),sQuery(id+"F2.wireOp",EDGE,"f79f6195-6e67-4fcd-a5d6-908ccd97d016.33.6.3"),sQuery(id+"F2.wireOp",EDGE,"f79f6195-6e67-4fcd-a5d6-908ccd97d016.36.6.3"),sQuery(id+"F2.wireOp",EDGE,"f79f6195-6e67-4fcd-a5d6-908ccd97d016.39.6.3"),sQuery(id+"F2.wireOp",EDGE,"f79f6195-6e67-4fcd-a5d6-908ccd97d016.43.6.3"),sQuery(id+"F2.wireOp",EDGE,"f79f6195-6e67-4fcd-a5d6-908ccd97d016.47.6.3"),sQuery(id+"F2.wireOp",EDGE,"f79f6195-6e67-4fcd-a5d6-908ccd97d016.1.6.4"),sQuery(id+"F2.wireOp",EDGE,"f79f6195-6e67-4fcd-a5d6-908ccd97d016.4.6.4"),sQuery(id+"F2.wireOp",EDGE,"f79f6195-6e67-4fcd-a5d6-908ccd97d016.7.6.4"),sQuery(id+"F2.wireOp",EDGE,"f79f6195-6e67-4fcd-a5d6-908ccd97d016.11.6.4"),sQuery(id+"F2.wireOp",EDGE,"f79f6195-6e67-4fcd-a5d6-908ccd97d016.14.6.4"),sQuery(id+"F2.wireOp",EDGE,"f79f6195-6e67-4fcd-a5d6-908ccd97d016.18.6.4"),sQuery(id+"F2.wireOp",EDGE,"f79f6195-6e67-4fcd-a5d6-908ccd97d016.27.6.4"),sQuery(id+"F2.wireOp",EDGE,"f79f6195-6e67-4fcd-a5d6-908ccd97d016.33.6.4"),sQuery(id+"F2.wireOp",EDGE,"f79f6195-6e67-4fcd-a5d6-908ccd97d016.36.6.4"),sQuery(id+"F2.wireOp",EDGE,"f79f6195-6e67-4fcd-a5d6-908ccd97d016.39.6.4"),sQuery(id+"F2.wireOp",EDGE,"f79f6195-6e67-4fcd-a5d6-908ccd97d016.43.6.4"),sQuery(id+"F2.wireOp",EDGE,"f79f6195-6e67-4fcd-a5d6-908ccd97d016.47.6.4"),sQuery(id+"F2.wireOp",EDGE,"f79f6195-6e67-4fcd-a5d6-908ccd97d016.1.6.5"),sQuery(id+"F2.wireOp",EDGE,"f79f6195-6e67-4fcd-a5d6-908ccd97d016.4.6.5"),sQuery(id+"F2.wireOp",EDGE,"f79f6195-6e67-4fcd-a5d6-908ccd97d016.7.6.5"),sQuery(id+"F2.wireOp",EDGE,"f79f6195-6e67-4fcd-a5d6-908ccd97d016.11.6.5"),sQuery(id+"F2.wireOp",EDGE,"f79f6195-6e67-4fcd-a5d6-908ccd97d016.14.6.5"),sQuery(id+"F2.wireOp",EDGE,"f79f6195-6e67-4fcd-a5d6-908ccd97d016.18.6.5"),sQuery(id+"F2.wireOp",EDGE,"f79f6195-6e67-4fcd-a5d6-908ccd97d016.27.6.5"),sQuery(id+"F2.wireOp",EDGE,"f79f6195-6e67-4fcd-a5d6-908ccd97d016.33.6.5"),sQuery(id+"F2.wireOp",EDGE,"f79f6195-6e67-4fcd-a5d6-908ccd97d016.36.6.5"),sQuery(id+"F2.wireOp",EDGE,"f79f6195-6e67-4fcd-a5d6-908ccd97d016.39.6.5"),sQuery(id+"F2.wireOp",EDGE,"f79f6195-6e67-4fcd-a5d6-908ccd97d016.43.6.5"),sQuery(id+"F2.wireOp",EDGE,"f79f6195-6e67-4fcd-a5d6-908ccd97d016.47.6.5"),sQuery(id+"F2.wireOp",EDGE,"f79f6195-6e67-4fcd-a5d6-908ccd97d016.1.6.6"),sQuery(id+"F2.wireOp",EDGE,"f79f6195-6e67-4fcd-a5d6-908ccd97d016.4.6.6"),sQuery(id+"F2.wireOp",EDGE,"f79f6195-6e67-4fcd-a5d6-908ccd97d016.7.6.6"),sQuery(id+"F2.wireOp",EDGE,"f79f6195-6e67-4fcd-a5d6-908ccd97d016.11.6.6"),sQuery(id+"F2.wireOp",EDGE,"f79f6195-6e67-4fcd-a5d6-908ccd97d016.14.6.6"),sQuery(id+"F2.wireOp",EDGE,"f79f6195-6e67-4fcd-a5d6-908ccd97d016.18.6.6"),sQuery(id+"F2.wireOp",EDGE,"f79f6195-6e67-4fcd-a5d6-908ccd97d016.27.6.6"),sQuery(id+"F2.wireOp",EDGE,"f79f6195-6e67-4fcd-a5d6-908ccd97d016.33.6.6"),sQuery(id+"F2.wireOp",EDGE,"f79f6195-6e67-4fcd-a5d6-908ccd97d016.36.6.6"),sQuery(id+"F2.wireOp",EDGE,"f79f6195-6e67-4fcd-a5d6-908ccd97d016.39.6.6"),sQuery(id+"F2.wireOp",EDGE,"f79f6195-6e67-4fcd-a5d6-908ccd97d016.43.6.6"),sQuery(id+"F2.wireOp",EDGE,"f79f6195-6e67-4fcd-a5d6-908ccd97d016.47.6.6"),sQuery(id+"F2.wireOp",EDGE,"f79f6195-6e67-4fcd-a5d6-908ccd97d016.1.6.7"),sQuery(id+"F2.wireOp",EDGE,"f79f6195-6e67-4fcd-a5d6-908ccd97d016.4.6.7"),sQuery(id+"F2.wireOp",EDGE,"f79f6195-6e67-4fcd-a5d6-908ccd97d016.7.6.7"),sQuery(id+"F2.wireOp",EDGE,"f79f6195-6e67-4fcd-a5d6-908ccd97d016.11.6.7"),sQuery(id+"F2.wireOp",EDGE,"f79f6195-6e67-4fcd-a5d6-908ccd97d016.14.6.7"),sQuery(id+"F2.wireOp",EDGE,"f79f6195-6e67-4fcd-a5d6-908ccd97d016.18.6.7"),sQuery(id+"F2.wireOp",EDGE,"f79f6195-6e67-4fcd-a5d6-908ccd97d016.27.6.7"),sQuery(id+"F2.wireOp",EDGE,"f79f6195-6e67-4fcd-a5d6-908ccd97d016.33.6.7"),sQuery(id+"F2.wireOp",EDGE,"f79f6195-6e67-4fcd-a5d6-908ccd97d016.36.6.7"),sQuery(id+"F2.wireOp",EDGE,"f79f6195-6e67-4fcd-a5d6-908ccd97d016.39.6.7"),sQuery(id+"F2.wireOp",EDGE,"f79f6195-6e67-4fcd-a5d6-908ccd97d016.43.6.7"),sQuery(id+"F2.wireOp",EDGE,"f79f6195-6e67-4fcd-a5d6-908ccd97d016.47.6.7"),sQuery(id+"F2.wireOp",EDGE,"f79f6195-6e67-4fcd-a5d6-908ccd97d016.1.6.8"),sQuery(id+"F2.wireOp",EDGE,"f79f6195-6e67-4fcd-a5d6-908ccd97d016.4.6.8"),sQuery(id+"F2.wireOp",EDGE,"f79f6195-6e67-4fcd-a5d6-908ccd97d016.7.6.8"),sQuery(id+"F2.wireOp",EDGE,"f79f6195-6e67-4fcd-a5d6-908ccd97d016.11.6.8"),sQuery(id+"F2.wireOp",EDGE,"f79f6195-6e67-4fcd-a5d6-908ccd97d016.14.6.8"),sQuery(id+"F2.wireOp",EDGE,"f79f6195-6e67-4fcd-a5d6-908ccd97d016.18.6.8"),sQuery(id+"F2.wireOp",EDGE,"f79f6195-6e67-4fcd-a5d6-908ccd97d016.27.6.8"),sQuery(id+"F2.wireOp",EDGE,"f79f6195-6e67-4fcd-a5d6-908ccd97d016.33.6.8"),sQuery(id+"F2.wireOp",EDGE,"f79f6195-6e67-4fcd-a5d6-908ccd97d016.36.6.8"),sQuery(id+"F2.wireOp",EDGE,"f79f6195-6e67-4fcd-a5d6-908ccd97d016.39.6.8"),sQuery(id+"F2.wireOp",EDGE,"f79f6195-6e67-4fcd-a5d6-908ccd97d016.43.6.8"),sQuery(id+"F2.wireOp",EDGE,"f79f6195-6e67-4fcd-a5d6-908ccd97d016.47.6.8"),sQuery(id+"F2.wireOp",EDGE,"f79f6195-6e67-4fcd-a5d6-908ccd97d016.1.6.9"),sQuery(id+"F2.wireOp",EDGE,"f79f6195-6e67-4fcd-a5d6-908ccd97d016.4.6.9"),sQuery(id+"F2.wireOp",EDGE,"f79f6195-6e67-4fcd-a5d6-908ccd97d016.7.6.9"),sQuery(id+"F2.wireOp",EDGE,"f79f6195-6e67-4fcd-a5d6-908ccd97d016.11.6.9"),sQuery(id+"F2.wireOp",EDGE,"f79f6195-6e67-4fcd-a5d6-908ccd97d016.14.6.9"),sQuery(id+"F2.wireOp",EDGE,"f79f6195-6e67-4fcd-a5d6-908ccd97d016.18.6.9"),sQuery(id+"F2.wireOp",EDGE,"f79f6195-6e67-4fcd-a5d6-908ccd97d016.27.6.9"),sQuery(id+"F2.wireOp",EDGE,"f79f6195-6e67-4fcd-a5d6-908ccd97d016.33.6.9"),sQuery(id+"F2.wireOp",EDGE,"f79f6195-6e67-4fcd-a5d6-908ccd97d016.36.6.9"),sQuery(id+"F2.wireOp",EDGE,"f79f6195-6e67-4fcd-a5d6-908ccd97d016.39.6.9"),sQuery(id+"F2.wireOp",EDGE,"f79f6195-6e67-4fcd-a5d6-908ccd97d016.43.6.9"),sQuery(id+"F2.wireOp",EDGE,"f79f6195-6e67-4fcd-a5d6-908ccd97d016.47.6.9"),sQuery(id+"F2.wireOp",EDGE,"f79f6195-6e67-4fcd-a5d6-908ccd97d016.1.7.0"),sQuery(id+"F2.wireOp",EDGE,"f79f6195-6e67-4fcd-a5d6-908ccd97d016.4.7.0"),sQuery(id+"F2.wireOp",EDGE,"f79f6195-6e67-4fcd-a5d6-908ccd97d016.7.7.0"),sQuery(id+"F2.wireOp",EDGE,"f79f6195-6e67-4fcd-a5d6-908ccd97d016.11.7.0"),sQuery(id+"F2.wireOp",EDGE,"f79f6195-6e67-4fcd-a5d6-908ccd97d016.14.7.0"),sQuery(id+"F2.wireOp",EDGE,"f79f6195-6e67-4fcd-a5d6-908ccd97d016.18.7.0"),sQuery(id+"F2.wireOp",EDGE,"f79f6195-6e67-4fcd-a5d6-908ccd97d016.27.7.0"),sQuery(id+"F2.wireOp",EDGE,"f79f6195-6e67-4fcd-a5d6-908ccd97d016.33.7.0"),sQuery(id+"F2.wireOp",EDGE,"f79f6195-6e67-4fcd-a5d6-908ccd97d016.36.7.0"),sQuery(id+"F2.wireOp",EDGE,"f79f6195-6e67-4fcd-a5d6-908ccd97d016.39.7.0"),sQuery(id+"F2.wireOp",EDGE,"f79f6195-6e67-4fcd-a5d6-908ccd97d016.43.7.0"),sQuery(id+"F2.wireOp",EDGE,"f79f6195-6e67-4fcd-a5d6-908ccd97d016.47.7.0"),sQuery(id+"F2.wireOp",EDGE,"f79f6195-6e67-4fcd-a5d6-908ccd97d016.1.7.1"),sQuery(id+"F2.wireOp",EDGE,"f79f6195-6e67-4fcd-a5d6-908ccd97d016.4.7.1"),sQuery(id+"F2.wireOp",EDGE,"f79f6195-6e67-4fcd-a5d6-908ccd97d016.7.7.1"),sQuery(id+"F2.wireOp",EDGE,"f79f6195-6e67-4fcd-a5d6-908ccd97d016.11.7.1"),sQuery(id+"F2.wireOp",EDGE,"f79f6195-6e67-4fcd-a5d6-908ccd97d016.14.7.1"),sQuery(id+"F2.wireOp",EDGE,"f79f6195-6e67-4fcd-a5d6-908ccd97d016.18.7.1"),sQuery(id+"F2.wireOp",EDGE,"f79f6195-6e67-4fcd-a5d6-908ccd97d016.27.7.1"),sQuery(id+"F2.wireOp",EDGE,"f79f6195-6e67-4fcd-a5d6-908ccd97d016.33.7.1"),sQuery(id+"F2.wireOp",EDGE,"f79f6195-6e67-4fcd-a5d6-908ccd97d016.36.7.1"),sQuery(id+"F2.wireOp",EDGE,"f79f6195-6e67-4fcd-a5d6-908ccd97d016.39.7.1"),sQuery(id+"F2.wireOp",EDGE,"f79f6195-6e67-4fcd-a5d6-908ccd97d016.43.7.1"),sQuery(id+"F2.wireOp",EDGE,"f79f6195-6e67-4fcd-a5d6-908ccd97d016.47.7.1"),sQuery(id+"F2.wireOp",EDGE,"f79f6195-6e67-4fcd-a5d6-908ccd97d016.1.7.2"),sQuery(id+"F2.wireOp",EDGE,"f79f6195-6e67-4fcd-a5d6-908ccd97d016.4.7.2"),sQuery(id+"F2.wireOp",EDGE,"f79f6195-6e67-4fcd-a5d6-908ccd97d016.7.7.2"),sQuery(id+"F2.wireOp",EDGE,"f79f6195-6e67-4fcd-a5d6-908ccd97d016.11.7.2"),sQuery(id+"F2.wireOp",EDGE,"f79f6195-6e67-4fcd-a5d6-908ccd97d016.14.7.2"),sQuery(id+"F2.wireOp",EDGE,"f79f6195-6e67-4fcd-a5d6-908ccd97d016.18.7.2"),sQuery(id+"F2.wireOp",EDGE,"f79f6195-6e67-4fcd-a5d6-908ccd97d016.27.7.2"),sQuery(id+"F2.wireOp",EDGE,"f79f6195-6e67-4fcd-a5d6-908ccd97d016.33.7.2"),sQuery(id+"F2.wireOp",EDGE,"f79f6195-6e67-4fcd-a5d6-908ccd97d016.36.7.2"),sQuery(id+"F2.wireOp",EDGE,"f79f6195-6e67-4fcd-a5d6-908ccd97d016.39.7.2"),sQuery(id+"F2.wireOp",EDGE,"f79f6195-6e67-4fcd-a5d6-908ccd97d016.43.7.2"),sQuery(id+"F2.wireOp",EDGE,"f79f6195-6e67-4fcd-a5d6-908ccd97d016.47.7.2"),sQuery(id+"F2.wireOp",EDGE,"f79f6195-6e67-4fcd-a5d6-908ccd97d016.1.7.3"),sQuery(id+"F2.wireOp",EDGE,"f79f6195-6e67-4fcd-a5d6-908ccd97d016.4.7.3"),sQuery(id+"F2.wireOp",EDGE,"f79f6195-6e67-4fcd-a5d6-908ccd97d016.7.7.3"),sQuery(id+"F2.wireOp",EDGE,"f79f6195-6e67-4fcd-a5d6-908ccd97d016.11.7.3"),sQuery(id+"F2.wireOp",EDGE,"f79f6195-6e67-4fcd-a5d6-908ccd97d016.14.7.3"),sQuery(id+"F2.wireOp",EDGE,"f79f6195-6e67-4fcd-a5d6-908ccd97d016.18.7.3"),sQuery(id+"F2.wireOp",EDGE,"f79f6195-6e67-4fcd-a5d6-908ccd97d016.27.7.3"),sQuery(id+"F2.wireOp",EDGE,"f79f6195-6e67-4fcd-a5d6-908ccd97d016.33.7.3"),sQuery(id+"F2.wireOp",EDGE,"f79f6195-6e67-4fcd-a5d6-908ccd97d016.36.7.3"),sQuery(id+"F2.wireOp",EDGE,"f79f6195-6e67-4fcd-a5d6-908ccd97d016.39.7.3"),sQuery(id+"F2.wireOp",EDGE,"f79f6195-6e67-4fcd-a5d6-908ccd97d016.43.7.3"),sQuery(id+"F2.wireOp",EDGE,"f79f6195-6e67-4fcd-a5d6-908ccd97d016.47.7.3"),sQuery(id+"F2.wireOp",EDGE,"f79f6195-6e67-4fcd-a5d6-908ccd97d016.1.7.4"),sQuery(id+"F2.wireOp",EDGE,"f79f6195-6e67-4fcd-a5d6-908ccd97d016.4.7.4"),sQuery(id+"F2.wireOp",EDGE,"f79f6195-6e67-4fcd-a5d6-908ccd97d016.7.7.4"),sQuery(id+"F2.wireOp",EDGE,"f79f6195-6e67-4fcd-a5d6-908ccd97d016.11.7.4"),sQuery(id+"F2.wireOp",EDGE,"f79f6195-6e67-4fcd-a5d6-908ccd97d016.14.7.4"),sQuery(id+"F2.wireOp",EDGE,"f79f6195-6e67-4fcd-a5d6-908ccd97d016.18.7.4"),sQuery(id+"F2.wireOp",EDGE,"f79f6195-6e67-4fcd-a5d6-908ccd97d016.27.7.4"),sQuery(id+"F2.wireOp",EDGE,"f79f6195-6e67-4fcd-a5d6-908ccd97d016.33.7.4"),sQuery(id+"F2.wireOp",EDGE,"f79f6195-6e67-4fcd-a5d6-908ccd97d016.36.7.4"),sQuery(id+"F2.wireOp",EDGE,"f79f6195-6e67-4fcd-a5d6-908ccd97d016.39.7.4"),sQuery(id+"F2.wireOp",EDGE,"f79f6195-6e67-4fcd-a5d6-908ccd97d016.43.7.4"),sQuery(id+"F2.wireOp",EDGE,"f79f6195-6e67-4fcd-a5d6-908ccd97d016.47.7.4"),sQuery(id+"F2.wireOp",EDGE,"f79f6195-6e67-4fcd-a5d6-908ccd97d016.1.7.5"),sQuery(id+"F2.wireOp",EDGE,"f79f6195-6e67-4fcd-a5d6-908ccd97d016.4.7.5"),sQuery(id+"F2.wireOp",EDGE,"f79f6195-6e67-4fcd-a5d6-908ccd97d016.7.7.5"),sQuery(id+"F2.wireOp",EDGE,"f79f6195-6e67-4fcd-a5d6-908ccd97d016.11.7.5"),sQuery(id+"F2.wireOp",EDGE,"f79f6195-6e67-4fcd-a5d6-908ccd97d016.14.7.5"),sQuery(id+"F2.wireOp",EDGE,"f79f6195-6e67-4fcd-a5d6-908ccd97d016.18.7.5"),sQuery(id+"F2.wireOp",EDGE,"f79f6195-6e67-4fcd-a5d6-908ccd97d016.27.7.5"),sQuery(id+"F2.wireOp",EDGE,"f79f6195-6e67-4fcd-a5d6-908ccd97d016.33.7.5"),sQuery(id+"F2.wireOp",EDGE,"f79f6195-6e67-4fcd-a5d6-908ccd97d016.36.7.5"),sQuery(id+"F2.wireOp",EDGE,"f79f6195-6e67-4fcd-a5d6-908ccd97d016.39.7.5"),sQuery(id+"F2.wireOp",EDGE,"f79f6195-6e67-4fcd-a5d6-908ccd97d016.43.7.5"),sQuery(id+"F2.wireOp",EDGE,"f79f6195-6e67-4fcd-a5d6-908ccd97d016.47.7.5"),sQuery(id+"F2.wireOp",EDGE,"f79f6195-6e67-4fcd-a5d6-908ccd97d016.1.7.6"),sQuery(id+"F2.wireOp",EDGE,"f79f6195-6e67-4fcd-a5d6-908ccd97d016.4.7.6"),sQuery(id+"F2.wireOp",EDGE,"f79f6195-6e67-4fcd-a5d6-908ccd97d016.7.7.6"),sQuery(id+"F2.wireOp",EDGE,"f79f6195-6e67-4fcd-a5d6-908ccd97d016.11.7.6"),sQuery(id+"F2.wireOp",EDGE,"f79f6195-6e67-4fcd-a5d6-908ccd97d016.14.7.6"),sQuery(id+"F2.wireOp",EDGE,"f79f6195-6e67-4fcd-a5d6-908ccd97d016.18.7.6"),sQuery(id+"F2.wireOp",EDGE,"f79f6195-6e67-4fcd-a5d6-908ccd97d016.27.7.6"),sQuery(id+"F2.wireOp",EDGE,"f79f6195-6e67-4fcd-a5d6-908ccd97d016.33.7.6"),sQuery(id+"F2.wireOp",EDGE,"f79f6195-6e67-4fcd-a5d6-908ccd97d016.36.7.6"),sQuery(id+"F2.wireOp",EDGE,"f79f6195-6e67-4fcd-a5d6-908ccd97d016.39.7.6"),sQuery(id+"F2.wireOp",EDGE,"f79f6195-6e67-4fcd-a5d6-908ccd97d016.43.7.6"),sQuery(id+"F2.wireOp",EDGE,"f79f6195-6e67-4fcd-a5d6-908ccd97d016.47.7.6"),sQuery(id+"F2.wireOp",EDGE,"f79f6195-6e67-4fcd-a5d6-908ccd97d016.1.7.7"),sQuery(id+"F2.wireOp",EDGE,"f79f6195-6e67-4fcd-a5d6-908ccd97d016.4.7.7"),sQuery(id+"F2.wireOp",EDGE,"f79f6195-6e67-4fcd-a5d6-908ccd97d016.7.7.7"),sQuery(id+"F2.wireOp",EDGE,"f79f6195-6e67-4fcd-a5d6-908ccd97d016.11.7.7"),sQuery(id+"F2.wireOp",EDGE,"f79f6195-6e67-4fcd-a5d6-908ccd97d016.14.7.7"),sQuery(id+"F2.wireOp",EDGE,"f79f6195-6e67-4fcd-a5d6-908ccd97d016.18.7.7"),sQuery(id+"F2.wireOp",EDGE,"f79f6195-6e67-4fcd-a5d6-908ccd97d016.27.7.7"),sQuery(id+"F2.wireOp",EDGE,"f79f6195-6e67-4fcd-a5d6-908ccd97d016.33.7.7"),sQuery(id+"F2.wireOp",EDGE,"f79f6195-6e67-4fcd-a5d6-908ccd97d016.36.7.7"),sQuery(id+"F2.wireOp",EDGE,"f79f6195-6e67-4fcd-a5d6-908ccd97d016.39.7.7"),sQuery(id+"F2.wireOp",EDGE,"f79f6195-6e67-4fcd-a5d6-908ccd97d016.43.7.7"),sQuery(id+"F2.wireOp",EDGE,"f79f6195-6e67-4fcd-a5d6-908ccd97d016.47.7.7"),sQuery(id+"F2.wireOp",EDGE,"f79f6195-6e67-4fcd-a5d6-908ccd97d016.1.7.8"),sQuery(id+"F2.wireOp",EDGE,"f79f6195-6e67-4fcd-a5d6-908ccd97d016.4.7.8"),sQuery(id+"F2.wireOp",EDGE,"f79f6195-6e67-4fcd-a5d6-908ccd97d016.7.7.8"),sQuery(id+"F2.wireOp",EDGE,"f79f6195-6e67-4fcd-a5d6-908ccd97d016.11.7.8"),sQuery(id+"F2.wireOp",EDGE,"f79f6195-6e67-4fcd-a5d6-908ccd97d016.14.7.8"),sQuery(id+"F2.wireOp",EDGE,"f79f6195-6e67-4fcd-a5d6-908ccd97d016.18.7.8"),sQuery(id+"F2.wireOp",EDGE,"f79f6195-6e67-4fcd-a5d6-908ccd97d016.27.7.8"),sQuery(id+"F2.wireOp",EDGE,"f79f6195-6e67-4fcd-a5d6-908ccd97d016.33.7.8"),sQuery(id+"F2.wireOp",EDGE,"f79f6195-6e67-4fcd-a5d6-908ccd97d016.36.7.8"),sQuery(id+"F2.wireOp",EDGE,"f79f6195-6e67-4fcd-a5d6-908ccd97d016.39.7.8"),sQuery(id+"F2.wireOp",EDGE,"f79f6195-6e67-4fcd-a5d6-908ccd97d016.43.7.8"),sQuery(id+"F2.wireOp",EDGE,"f79f6195-6e67-4fcd-a5d6-908ccd97d016.47.7.8"),sQuery(id+"F2.wireOp",EDGE,"f79f6195-6e67-4fcd-a5d6-908ccd97d016.1.7.9"),sQuery(id+"F2.wireOp",EDGE,"f79f6195-6e67-4fcd-a5d6-908ccd97d016.4.7.9"),sQuery(id+"F2.wireOp",EDGE,"f79f6195-6e67-4fcd-a5d6-908ccd97d016.7.7.9"),sQuery(id+"F2.wireOp",EDGE,"f79f6195-6e67-4fcd-a5d6-908ccd97d016.11.7.9"),sQuery(id+"F2.wireOp",EDGE,"f79f6195-6e67-4fcd-a5d6-908ccd97d016.14.7.9"),sQuery(id+"F2.wireOp",EDGE,"f79f6195-6e67-4fcd-a5d6-908ccd97d016.18.7.9"),sQuery(id+"F2.wireOp",EDGE,"f79f6195-6e67-4fcd-a5d6-908ccd97d016.27.7.9"),sQuery(id+"F2.wireOp",EDGE,"f79f6195-6e67-4fcd-a5d6-908ccd97d016.33.7.9"),sQuery(id+"F2.wireOp",EDGE,"f79f6195-6e67-4fcd-a5d6-908ccd97d016.36.7.9"),sQuery(id+"F2.wireOp",EDGE,"f79f6195-6e67-4fcd-a5d6-908ccd97d016.39.7.9"),sQuery(id+"F2.wireOp",EDGE,"f79f6195-6e67-4fcd-a5d6-908ccd97d016.43.7.9"),sQuery(id+"F2.wireOp",EDGE,"f79f6195-6e67-4fcd-a5d6-908ccd97d016.47.7.9"),sQuery(id+"F2.wireOp",EDGE,"f79f6195-6e67-4fcd-a5d6-908ccd97d016.1.8.0"),sQuery(id+"F2.wireOp",EDGE,"f79f6195-6e67-4fcd-a5d6-908ccd97d016.4.8.0"),sQuery(id+"F2.wireOp",EDGE,"f79f6195-6e67-4fcd-a5d6-908ccd97d016.7.8.0"),sQuery(id+"F2.wireOp",EDGE,"f79f6195-6e67-4fcd-a5d6-908ccd97d016.11.8.0"),sQuery(id+"F2.wireOp",EDGE,"f79f6195-6e67-4fcd-a5d6-908ccd97d016.14.8.0"),sQuery(id+"F2.wireOp",EDGE,"f79f6195-6e67-4fcd-a5d6-908ccd97d016.18.8.0"),sQuery(id+"F2.wireOp",EDGE,"f79f6195-6e67-4fcd-a5d6-908ccd97d016.27.8.0"),sQuery(id+"F2.wireOp",EDGE,"f79f6195-6e67-4fcd-a5d6-908ccd97d016.33.8.0"),sQuery(id+"F2.wireOp",EDGE,"f79f6195-6e67-4fcd-a5d6-908ccd97d016.36.8.0"),sQuery(id+"F2.wireOp",EDGE,"f79f6195-6e67-4fcd-a5d6-908ccd97d016.39.8.0"),sQuery(id+"F2.wireOp",EDGE,"f79f6195-6e67-4fcd-a5d6-908ccd97d016.43.8.0"),sQuery(id+"F2.wireOp",EDGE,"f79f6195-6e67-4fcd-a5d6-908ccd97d016.47.8.0"),sQuery(id+"F2.wireOp",EDGE,"f79f6195-6e67-4fcd-a5d6-908ccd97d016.1.8.1"),sQuery(id+"F2.wireOp",EDGE,"f79f6195-6e67-4fcd-a5d6-908ccd97d016.4.8.1"),sQuery(id+"F2.wireOp",EDGE,"f79f6195-6e67-4fcd-a5d6-908ccd97d016.7.8.1"),sQuery(id+"F2.wireOp",EDGE,"f79f6195-6e67-4fcd-a5d6-908ccd97d016.11.8.1"),sQuery(id+"F2.wireOp",EDGE,"f79f6195-6e67-4fcd-a5d6-908ccd97d016.14.8.1"),sQuery(id+"F2.wireOp",EDGE,"f79f6195-6e67-4fcd-a5d6-908ccd97d016.18.8.1"),sQuery(id+"F2.wireOp",EDGE,"f79f6195-6e67-4fcd-a5d6-908ccd97d016.27.8.1"),sQuery(id+"F2.wireOp",EDGE,"f79f6195-6e67-4fcd-a5d6-908ccd97d016.33.8.1"),sQuery(id+"F2.wireOp",EDGE,"f79f6195-6e67-4fcd-a5d6-908ccd97d016.36.8.1"),sQuery(id+"F2.wireOp",EDGE,"f79f6195-6e67-4fcd-a5d6-908ccd97d016.39.8.1"),sQuery(id+"F2.wireOp",EDGE,"f79f6195-6e67-4fcd-a5d6-908ccd97d016.43.8.1"),sQuery(id+"F2.wireOp",EDGE,"f79f6195-6e67-4fcd-a5d6-908ccd97d016.47.8.1"),sQuery(id+"F2.wireOp",EDGE,"f79f6195-6e67-4fcd-a5d6-908ccd97d016.1.8.2"),sQuery(id+"F2.wireOp",EDGE,"f79f6195-6e67-4fcd-a5d6-908ccd97d016.4.8.2"),sQuery(id+"F2.wireOp",EDGE,"f79f6195-6e67-4fcd-a5d6-908ccd97d016.7.8.2"),sQuery(id+"F2.wireOp",EDGE,"f79f6195-6e67-4fcd-a5d6-908ccd97d016.11.8.2"),sQuery(id+"F2.wireOp",EDGE,"f79f6195-6e67-4fcd-a5d6-908ccd97d016.14.8.2"),sQuery(id+"F2.wireOp",EDGE,"f79f6195-6e67-4fcd-a5d6-908ccd97d016.18.8.2"),sQuery(id+"F2.wireOp",EDGE,"f79f6195-6e67-4fcd-a5d6-908ccd97d016.27.8.2"),sQuery(id+"F2.wireOp",EDGE,"f79f6195-6e67-4fcd-a5d6-908ccd97d016.33.8.2"),sQuery(id+"F2.wireOp",EDGE,"f79f6195-6e67-4fcd-a5d6-908ccd97d016.36.8.2"),sQuery(id+"F2.wireOp",EDGE,"f79f6195-6e67-4fcd-a5d6-908ccd97d016.39.8.2"),sQuery(id+"F2.wireOp",EDGE,"f79f6195-6e67-4fcd-a5d6-908ccd97d016.43.8.2"),sQuery(id+"F2.wireOp",EDGE,"f79f6195-6e67-4fcd-a5d6-908ccd97d016.47.8.2"),sQuery(id+"F2.wireOp",EDGE,"f79f6195-6e67-4fcd-a5d6-908ccd97d016.1.8.3"),sQuery(id+"F2.wireOp",EDGE,"f79f6195-6e67-4fcd-a5d6-908ccd97d016.4.8.3"),sQuery(id+"F2.wireOp",EDGE,"f79f6195-6e67-4fcd-a5d6-908ccd97d016.7.8.3"),sQuery(id+"F2.wireOp",EDGE,"f79f6195-6e67-4fcd-a5d6-908ccd97d016.11.8.3"),sQuery(id+"F2.wireOp",EDGE,"f79f6195-6e67-4fcd-a5d6-908ccd97d016.14.8.3"),sQuery(id+"F2.wireOp",EDGE,"f79f6195-6e67-4fcd-a5d6-908ccd97d016.18.8.3"),sQuery(id+"F2.wireOp",EDGE,"f79f6195-6e67-4fcd-a5d6-908ccd97d016.27.8.3"),sQuery(id+"F2.wireOp",EDGE,"f79f6195-6e67-4fcd-a5d6-908ccd97d016.33.8.3"),sQuery(id+"F2.wireOp",EDGE,"f79f6195-6e67-4fcd-a5d6-908ccd97d016.36.8.3"),sQuery(id+"F2.wireOp",EDGE,"f79f6195-6e67-4fcd-a5d6-908ccd97d016.39.8.3"),sQuery(id+"F2.wireOp",EDGE,"f79f6195-6e67-4fcd-a5d6-908ccd97d016.43.8.3"),sQuery(id+"F2.wireOp",EDGE,"f79f6195-6e67-4fcd-a5d6-908ccd97d016.47.8.3"),sQuery(id+"F2.wireOp",EDGE,"f79f6195-6e67-4fcd-a5d6-908ccd97d016.1.8.4"),sQuery(id+"F2.wireOp",EDGE,"f79f6195-6e67-4fcd-a5d6-908ccd97d016.4.8.4"),sQuery(id+"F2.wireOp",EDGE,"f79f6195-6e67-4fcd-a5d6-908ccd97d016.7.8.4"),sQuery(id+"F2.wireOp",EDGE,"f79f6195-6e67-4fcd-a5d6-908ccd97d016.11.8.4"),sQuery(id+"F2.wireOp",EDGE,"f79f6195-6e67-4fcd-a5d6-908ccd97d016.14.8.4"),sQuery(id+"F2.wireOp",EDGE,"f79f6195-6e67-4fcd-a5d6-908ccd97d016.18.8.4"),sQuery(id+"F2.wireOp",EDGE,"f79f6195-6e67-4fcd-a5d6-908ccd97d016.27.8.4"),sQuery(id+"F2.wireOp",EDGE,"f79f6195-6e67-4fcd-a5d6-908ccd97d016.33.8.4"),sQuery(id+"F2.wireOp",EDGE,"f79f6195-6e67-4fcd-a5d6-908ccd97d016.36.8.4"),sQuery(id+"F2.wireOp",EDGE,"f79f6195-6e67-4fcd-a5d6-908ccd97d016.39.8.4"),sQuery(id+"F2.wireOp",EDGE,"f79f6195-6e67-4fcd-a5d6-908ccd97d016.43.8.4"),sQuery(id+"F2.wireOp",EDGE,"f79f6195-6e67-4fcd-a5d6-908ccd97d016.47.8.4"),sQuery(id+"F2.wireOp",EDGE,"f79f6195-6e67-4fcd-a5d6-908ccd97d016.1.8.5"),sQuery(id+"F2.wireOp",EDGE,"f79f6195-6e67-4fcd-a5d6-908ccd97d016.4.8.5"),sQuery(id+"F2.wireOp",EDGE,"f79f6195-6e67-4fcd-a5d6-908ccd97d016.7.8.5"),sQuery(id+"F2.wireOp",EDGE,"f79f6195-6e67-4fcd-a5d6-908ccd97d016.11.8.5"),sQuery(id+"F2.wireOp",EDGE,"f79f6195-6e67-4fcd-a5d6-908ccd97d016.14.8.5"),sQuery(id+"F2.wireOp",EDGE,"f79f6195-6e67-4fcd-a5d6-908ccd97d016.18.8.5"),sQuery(id+"F2.wireOp",EDGE,"f79f6195-6e67-4fcd-a5d6-908ccd97d016.27.8.5"),sQuery(id+"F2.wireOp",EDGE,"f79f6195-6e67-4fcd-a5d6-908ccd97d016.33.8.5"),sQuery(id+"F2.wireOp",EDGE,"f79f6195-6e67-4fcd-a5d6-908ccd97d016.36.8.5"),sQuery(id+"F2.wireOp",EDGE,"f79f6195-6e67-4fcd-a5d6-908ccd97d016.39.8.5"),sQuery(id+"F2.wireOp",EDGE,"f79f6195-6e67-4fcd-a5d6-908ccd97d016.43.8.5"),sQuery(id+"F2.wireOp",EDGE,"f79f6195-6e67-4fcd-a5d6-908ccd97d016.47.8.5"),sQuery(id+"F2.wireOp",EDGE,"f79f6195-6e67-4fcd-a5d6-908ccd97d016.1.8.6"),sQuery(id+"F2.wireOp",EDGE,"f79f6195-6e67-4fcd-a5d6-908ccd97d016.4.8.6"),sQuery(id+"F2.wireOp",EDGE,"f79f6195-6e67-4fcd-a5d6-908ccd97d016.7.8.6"),sQuery(id+"F2.wireOp",EDGE,"f79f6195-6e67-4fcd-a5d6-908ccd97d016.11.8.6"),sQuery(id+"F2.wireOp",EDGE,"f79f6195-6e67-4fcd-a5d6-908ccd97d016.14.8.6"),sQuery(id+"F2.wireOp",EDGE,"f79f6195-6e67-4fcd-a5d6-908ccd97d016.18.8.6"),sQuery(id+"F2.wireOp",EDGE,"f79f6195-6e67-4fcd-a5d6-908ccd97d016.27.8.6"),sQuery(id+"F2.wireOp",EDGE,"f79f6195-6e67-4fcd-a5d6-908ccd97d016.33.8.6"),sQuery(id+"F2.wireOp",EDGE,"f79f6195-6e67-4fcd-a5d6-908ccd97d016.36.8.6"),sQuery(id+"F2.wireOp",EDGE,"f79f6195-6e67-4fcd-a5d6-908ccd97d016.39.8.6"),sQuery(id+"F2.wireOp",EDGE,"f79f6195-6e67-4fcd-a5d6-908ccd97d016.43.8.6"),sQuery(id+"F2.wireOp",EDGE,"f79f6195-6e67-4fcd-a5d6-908ccd97d016.47.8.6"),sQuery(id+"F2.wireOp",EDGE,"f79f6195-6e67-4fcd-a5d6-908ccd97d016.1.8.7"),sQuery(id+"F2.wireOp",EDGE,"f79f6195-6e67-4fcd-a5d6-908ccd97d016.4.8.7"),sQuery(id+"F2.wireOp",EDGE,"f79f6195-6e67-4fcd-a5d6-908ccd97d016.7.8.7"),sQuery(id+"F2.wireOp",EDGE,"f79f6195-6e67-4fcd-a5d6-908ccd97d016.11.8.7"),sQuery(id+"F2.wireOp",EDGE,"f79f6195-6e67-4fcd-a5d6-908ccd97d016.14.8.7"),sQuery(id+"F2.wireOp",EDGE,"f79f6195-6e67-4fcd-a5d6-908ccd97d016.18.8.7"),sQuery(id+"F2.wireOp",EDGE,"f79f6195-6e67-4fcd-a5d6-908ccd97d016.27.8.7"),sQuery(id+"F2.wireOp",EDGE,"f79f6195-6e67-4fcd-a5d6-908ccd97d016.33.8.7"),sQuery(id+"F2.wireOp",EDGE,"f79f6195-6e67-4fcd-a5d6-908ccd97d016.36.8.7"),sQuery(id+"F2.wireOp",EDGE,"f79f6195-6e67-4fcd-a5d6-908ccd97d016.39.8.7"),sQuery(id+"F2.wireOp",EDGE,"f79f6195-6e67-4fcd-a5d6-908ccd97d016.43.8.7"),sQuery(id+"F2.wireOp",EDGE,"f79f6195-6e67-4fcd-a5d6-908ccd97d016.47.8.7"),sQuery(id+"F2.wireOp",EDGE,"f79f6195-6e67-4fcd-a5d6-908ccd97d016.1.8.8"),sQuery(id+"F2.wireOp",EDGE,"f79f6195-6e67-4fcd-a5d6-908ccd97d016.4.8.8"),sQuery(id+"F2.wireOp",EDGE,"f79f6195-6e67-4fcd-a5d6-908ccd97d016.7.8.8"),sQuery(id+"F2.wireOp",EDGE,"f79f6195-6e67-4fcd-a5d6-908ccd97d016.11.8.8"),sQuery(id+"F2.wireOp",EDGE,"f79f6195-6e67-4fcd-a5d6-908ccd97d016.14.8.8"),sQuery(id+"F2.wireOp",EDGE,"f79f6195-6e67-4fcd-a5d6-908ccd97d016.18.8.8"),sQuery(id+"F2.wireOp",EDGE,"f79f6195-6e67-4fcd-a5d6-908ccd97d016.27.8.8"),sQuery(id+"F2.wireOp",EDGE,"f79f6195-6e67-4fcd-a5d6-908ccd97d016.33.8.8"),sQuery(id+"F2.wireOp",EDGE,"f79f6195-6e67-4fcd-a5d6-908ccd97d016.36.8.8"),sQuery(id+"F2.wireOp",EDGE,"f79f6195-6e67-4fcd-a5d6-908ccd97d016.39.8.8"),sQuery(id+"F2.wireOp",EDGE,"f79f6195-6e67-4fcd-a5d6-908ccd97d016.43.8.8"),sQuery(id+"F2.wireOp",EDGE,"f79f6195-6e67-4fcd-a5d6-908ccd97d016.47.8.8"),sQuery(id+"F2.wireOp",EDGE,"f79f6195-6e67-4fcd-a5d6-908ccd97d016.1.8.9"),sQuery(id+"F2.wireOp",EDGE,"f79f6195-6e67-4fcd-a5d6-908ccd97d016.4.8.9"),sQuery(id+"F2.wireOp",EDGE,"f79f6195-6e67-4fcd-a5d6-908ccd97d016.7.8.9"),sQuery(id+"F2.wireOp",EDGE,"f79f6195-6e67-4fcd-a5d6-908ccd97d016.11.8.9"),sQuery(id+"F2.wireOp",EDGE,"f79f6195-6e67-4fcd-a5d6-908ccd97d016.14.8.9"),sQuery(id+"F2.wireOp",EDGE,"f79f6195-6e67-4fcd-a5d6-908ccd97d016.18.8.9"),sQuery(id+"F2.wireOp",EDGE,"f79f6195-6e67-4fcd-a5d6-908ccd97d016.27.8.9"),sQuery(id+"F2.wireOp",EDGE,"f79f6195-6e67-4fcd-a5d6-908ccd97d016.33.8.9"),sQuery(id+"F2.wireOp",EDGE,"f79f6195-6e67-4fcd-a5d6-908ccd97d016.36.8.9"),sQuery(id+"F2.wireOp",EDGE,"f79f6195-6e67-4fcd-a5d6-908ccd97d016.39.8.9"),sQuery(id+"F2.wireOp",EDGE,"f79f6195-6e67-4fcd-a5d6-908ccd97d016.43.8.9"),sQuery(id+"F2.wireOp",EDGE,"f79f6195-6e67-4fcd-a5d6-908ccd97d016.47.8.9"),sQuery(id+"F2.wireOp",EDGE,"f79f6195-6e67-4fcd-a5d6-908ccd97d016.1.9.0"),sQuery(id+"F2.wireOp",EDGE,"f79f6195-6e67-4fcd-a5d6-908ccd97d016.4.9.0"),sQuery(id+"F2.wireOp",EDGE,"f79f6195-6e67-4fcd-a5d6-908ccd97d016.7.9.0"),sQuery(id+"F2.wireOp",EDGE,"f79f6195-6e67-4fcd-a5d6-908ccd97d016.11.9.0"),sQuery(id+"F2.wireOp",EDGE,"f79f6195-6e67-4fcd-a5d6-908ccd97d016.14.9.0"),sQuery(id+"F2.wireOp",EDGE,"f79f6195-6e67-4fcd-a5d6-908ccd97d016.18.9.0"),sQuery(id+"F2.wireOp",EDGE,"f79f6195-6e67-4fcd-a5d6-908ccd97d016.27.9.0"),sQuery(id+"F2.wireOp",EDGE,"f79f6195-6e67-4fcd-a5d6-908ccd97d016.33.9.0"),sQuery(id+"F2.wireOp",EDGE,"f79f6195-6e67-4fcd-a5d6-908ccd97d016.36.9.0"),sQuery(id+"F2.wireOp",EDGE,"f79f6195-6e67-4fcd-a5d6-908ccd97d016.39.9.0"),sQuery(id+"F2.wireOp",EDGE,"f79f6195-6e67-4fcd-a5d6-908ccd97d016.43.9.0"),sQuery(id+"F2.wireOp",EDGE,"f79f6195-6e67-4fcd-a5d6-908ccd97d016.47.9.0"),sQuery(id+"F2.wireOp",EDGE,"f79f6195-6e67-4fcd-a5d6-908ccd97d016.1.9.1"),sQuery(id+"F2.wireOp",EDGE,"f79f6195-6e67-4fcd-a5d6-908ccd97d016.4.9.1"),sQuery(id+"F2.wireOp",EDGE,"f79f6195-6e67-4fcd-a5d6-908ccd97d016.7.9.1"),sQuery(id+"F2.wireOp",EDGE,"f79f6195-6e67-4fcd-a5d6-908ccd97d016.11.9.1"),sQuery(id+"F2.wireOp",EDGE,"f79f6195-6e67-4fcd-a5d6-908ccd97d016.14.9.1"),sQuery(id+"F2.wireOp",EDGE,"f79f6195-6e67-4fcd-a5d6-908ccd97d016.18.9.1"),sQuery(id+"F2.wireOp",EDGE,"f79f6195-6e67-4fcd-a5d6-908ccd97d016.27.9.1"),sQuery(id+"F2.wireOp",EDGE,"f79f6195-6e67-4fcd-a5d6-908ccd97d016.33.9.1"),sQuery(id+"F2.wireOp",EDGE,"f79f6195-6e67-4fcd-a5d6-908ccd97d016.36.9.1"),sQuery(id+"F2.wireOp",EDGE,"f79f6195-6e67-4fcd-a5d6-908ccd97d016.39.9.1"),sQuery(id+"F2.wireOp",EDGE,"f79f6195-6e67-4fcd-a5d6-908ccd97d016.43.9.1"),sQuery(id+"F2.wireOp",EDGE,"f79f6195-6e67-4fcd-a5d6-908ccd97d016.47.9.1"),sQuery(id+"F2.wireOp",EDGE,"f79f6195-6e67-4fcd-a5d6-908ccd97d016.1.9.2"),sQuery(id+"F2.wireOp",EDGE,"f79f6195-6e67-4fcd-a5d6-908ccd97d016.4.9.2"),sQuery(id+"F2.wireOp",EDGE,"f79f6195-6e67-4fcd-a5d6-908ccd97d016.7.9.2"),sQuery(id+"F2.wireOp",EDGE,"f79f6195-6e67-4fcd-a5d6-908ccd97d016.11.9.2"),sQuery(id+"F2.wireOp",EDGE,"f79f6195-6e67-4fcd-a5d6-908ccd97d016.14.9.2"),sQuery(id+"F2.wireOp",EDGE,"f79f6195-6e67-4fcd-a5d6-908ccd97d016.18.9.2"),sQuery(id+"F2.wireOp",EDGE,"f79f6195-6e67-4fcd-a5d6-908ccd97d016.27.9.2"),sQuery(id+"F2.wireOp",EDGE,"f79f6195-6e67-4fcd-a5d6-908ccd97d016.33.9.2"),sQuery(id+"F2.wireOp",EDGE,"f79f6195-6e67-4fcd-a5d6-908ccd97d016.36.9.2"),sQuery(id+"F2.wireOp",EDGE,"f79f6195-6e67-4fcd-a5d6-908ccd97d016.39.9.2"),sQuery(id+"F2.wireOp",EDGE,"f79f6195-6e67-4fcd-a5d6-908ccd97d016.43.9.2"),sQuery(id+"F2.wireOp",EDGE,"f79f6195-6e67-4fcd-a5d6-908ccd97d016.47.9.2"),sQuery(id+"F2.wireOp",EDGE,"f79f6195-6e67-4fcd-a5d6-908ccd97d016.1.9.3"),sQuery(id+"F2.wireOp",EDGE,"f79f6195-6e67-4fcd-a5d6-908ccd97d016.4.9.3"),sQuery(id+"F2.wireOp",EDGE,"f79f6195-6e67-4fcd-a5d6-908ccd97d016.7.9.3"),sQuery(id+"F2.wireOp",EDGE,"f79f6195-6e67-4fcd-a5d6-908ccd97d016.11.9.3"),sQuery(id+"F2.wireOp",EDGE,"f79f6195-6e67-4fcd-a5d6-908ccd97d016.14.9.3"),sQuery(id+"F2.wireOp",EDGE,"f79f6195-6e67-4fcd-a5d6-908ccd97d016.18.9.3"),sQuery(id+"F2.wireOp",EDGE,"f79f6195-6e67-4fcd-a5d6-908ccd97d016.27.9.3"),sQuery(id+"F2.wireOp",EDGE,"f79f6195-6e67-4fcd-a5d6-908ccd97d016.33.9.3"),sQuery(id+"F2.wireOp",EDGE,"f79f6195-6e67-4fcd-a5d6-908ccd97d016.36.9.3"),sQuery(id+"F2.wireOp",EDGE,"f79f6195-6e67-4fcd-a5d6-908ccd97d016.39.9.3"),sQuery(id+"F2.wireOp",EDGE,"f79f6195-6e67-4fcd-a5d6-908ccd97d016.43.9.3"),sQuery(id+"F2.wireOp",EDGE,"f79f6195-6e67-4fcd-a5d6-908ccd97d016.47.9.3"),sQuery(id+"F2.wireOp",EDGE,"f79f6195-6e67-4fcd-a5d6-908ccd97d016.1.9.4"),sQuery(id+"F2.wireOp",EDGE,"f79f6195-6e67-4fcd-a5d6-908ccd97d016.4.9.4"),sQuery(id+"F2.wireOp",EDGE,"f79f6195-6e67-4fcd-a5d6-908ccd97d016.7.9.4"),sQuery(id+"F2.wireOp",EDGE,"f79f6195-6e67-4fcd-a5d6-908ccd97d016.11.9.4"),sQuery(id+"F2.wireOp",EDGE,"f79f6195-6e67-4fcd-a5d6-908ccd97d016.14.9.4"),sQuery(id+"F2.wireOp",EDGE,"f79f6195-6e67-4fcd-a5d6-908ccd97d016.18.9.4"),sQuery(id+"F2.wireOp",EDGE,"f79f6195-6e67-4fcd-a5d6-908ccd97d016.27.9.4"),sQuery(id+"F2.wireOp",EDGE,"f79f6195-6e67-4fcd-a5d6-908ccd97d016.33.9.4"),sQuery(id+"F2.wireOp",EDGE,"f79f6195-6e67-4fcd-a5d6-908ccd97d016.36.9.4"),sQuery(id+"F2.wireOp",EDGE,"f79f6195-6e67-4fcd-a5d6-908ccd97d016.39.9.4"),sQuery(id+"F2.wireOp",EDGE,"f79f6195-6e67-4fcd-a5d6-908ccd97d016.43.9.4"),sQuery(id+"F2.wireOp",EDGE,"f79f6195-6e67-4fcd-a5d6-908ccd97d016.47.9.4"),sQuery(id+"F2.wireOp",EDGE,"f79f6195-6e67-4fcd-a5d6-908ccd97d016.1.9.5"),sQuery(id+"F2.wireOp",EDGE,"f79f6195-6e67-4fcd-a5d6-908ccd97d016.4.9.5"),sQuery(id+"F2.wireOp",EDGE,"f79f6195-6e67-4fcd-a5d6-908ccd97d016.7.9.5"),sQuery(id+"F2.wireOp",EDGE,"f79f6195-6e67-4fcd-a5d6-908ccd97d016.11.9.5"),sQuery(id+"F2.wireOp",EDGE,"f79f6195-6e67-4fcd-a5d6-908ccd97d016.14.9.5"),sQuery(id+"F2.wireOp",EDGE,"f79f6195-6e67-4fcd-a5d6-908ccd97d016.18.9.5"),sQuery(id+"F2.wireOp",EDGE,"f79f6195-6e67-4fcd-a5d6-908ccd97d016.27.9.5"),sQuery(id+"F2.wireOp",EDGE,"f79f6195-6e67-4fcd-a5d6-908ccd97d016.33.9.5"),sQuery(id+"F2.wireOp",EDGE,"f79f6195-6e67-4fcd-a5d6-908ccd97d016.36.9.5"),sQuery(id+"F2.wireOp",EDGE,"f79f6195-6e67-4fcd-a5d6-908ccd97d016.39.9.5"),sQuery(id+"F2.wireOp",EDGE,"f79f6195-6e67-4fcd-a5d6-908ccd97d016.43.9.5"),sQuery(id+"F2.wireOp",EDGE,"f79f6195-6e67-4fcd-a5d6-908ccd97d016.47.9.5"),sQuery(id+"F2.wireOp",EDGE,"f79f6195-6e67-4fcd-a5d6-908ccd97d016.1.9.6"),sQuery(id+"F2.wireOp",EDGE,"f79f6195-6e67-4fcd-a5d6-908ccd97d016.4.9.6"),sQuery(id+"F2.wireOp",EDGE,"f79f6195-6e67-4fcd-a5d6-908ccd97d016.7.9.6"),sQuery(id+"F2.wireOp",EDGE,"f79f6195-6e67-4fcd-a5d6-908ccd97d016.11.9.6"),sQuery(id+"F2.wireOp",EDGE,"f79f6195-6e67-4fcd-a5d6-908ccd97d016.14.9.6"),sQuery(id+"F2.wireOp",EDGE,"f79f6195-6e67-4fcd-a5d6-908ccd97d016.18.9.6"),sQuery(id+"F2.wireOp",EDGE,"f79f6195-6e67-4fcd-a5d6-908ccd97d016.27.9.6"),sQuery(id+"F2.wireOp",EDGE,"f79f6195-6e67-4fcd-a5d6-908ccd97d016.33.9.6"),sQuery(id+"F2.wireOp",EDGE,"f79f6195-6e67-4fcd-a5d6-908ccd97d016.36.9.6"),sQuery(id+"F2.wireOp",EDGE,"f79f6195-6e67-4fcd-a5d6-908ccd97d016.39.9.6"),sQuery(id+"F2.wireOp",EDGE,"f79f6195-6e67-4fcd-a5d6-908ccd97d016.43.9.6"),sQuery(id+"F2.wireOp",EDGE,"f79f6195-6e67-4fcd-a5d6-908ccd97d016.47.9.6"),sQuery(id+"F2.wireOp",EDGE,"f79f6195-6e67-4fcd-a5d6-908ccd97d016.1.9.7"),sQuery(id+"F2.wireOp",EDGE,"f79f6195-6e67-4fcd-a5d6-908ccd97d016.4.9.7"),sQuery(id+"F2.wireOp",EDGE,"f79f6195-6e67-4fcd-a5d6-908ccd97d016.7.9.7"),sQuery(id+"F2.wireOp",EDGE,"f79f6195-6e67-4fcd-a5d6-908ccd97d016.11.9.7"),sQuery(id+"F2.wireOp",EDGE,"f79f6195-6e67-4fcd-a5d6-908ccd97d016.14.9.7"),sQuery(id+"F2.wireOp",EDGE,"f79f6195-6e67-4fcd-a5d6-908ccd97d016.18.9.7"),sQuery(id+"F2.wireOp",EDGE,"f79f6195-6e67-4fcd-a5d6-908ccd97d016.27.9.7"),sQuery(id+"F2.wireOp",EDGE,"f79f6195-6e67-4fcd-a5d6-908ccd97d016.33.9.7"),sQuery(id+"F2.wireOp",EDGE,"f79f6195-6e67-4fcd-a5d6-908ccd97d016.36.9.7"),sQuery(id+"F2.wireOp",EDGE,"f79f6195-6e67-4fcd-a5d6-908ccd97d016.39.9.7"),sQuery(id+"F2.wireOp",EDGE,"f79f6195-6e67-4fcd-a5d6-908ccd97d016.43.9.7"),sQuery(id+"F2.wireOp",EDGE,"f79f6195-6e67-4fcd-a5d6-908ccd97d016.47.9.7"),sQuery(id+"F2.wireOp",EDGE,"f79f6195-6e67-4fcd-a5d6-908ccd97d016.1.9.8"),sQuery(id+"F2.wireOp",EDGE,"f79f6195-6e67-4fcd-a5d6-908ccd97d016.4.9.8"),sQuery(id+"F2.wireOp",EDGE,"f79f6195-6e67-4fcd-a5d6-908ccd97d016.7.9.8"),sQuery(id+"F2.wireOp",EDGE,"f79f6195-6e67-4fcd-a5d6-908ccd97d016.11.9.8"),sQuery(id+"F2.wireOp",EDGE,"f79f6195-6e67-4fcd-a5d6-908ccd97d016.14.9.8"),sQuery(id+"F2.wireOp",EDGE,"f79f6195-6e67-4fcd-a5d6-908ccd97d016.18.9.8"),sQuery(id+"F2.wireOp",EDGE,"f79f6195-6e67-4fcd-a5d6-908ccd97d016.27.9.8"),sQuery(id+"F2.wireOp",EDGE,"f79f6195-6e67-4fcd-a5d6-908ccd97d016.33.9.8"),sQuery(id+"F2.wireOp",EDGE,"f79f6195-6e67-4fcd-a5d6-908ccd97d016.36.9.8"),sQuery(id+"F2.wireOp",EDGE,"f79f6195-6e67-4fcd-a5d6-908ccd97d016.39.9.8"),sQuery(id+"F2.wireOp",EDGE,"f79f6195-6e67-4fcd-a5d6-908ccd97d016.43.9.8"),sQuery(id+"F2.wireOp",EDGE,"f79f6195-6e67-4fcd-a5d6-908ccd97d016.47.9.8"),sQuery(id+"F2.wireOp",EDGE,"f79f6195-6e67-4fcd-a5d6-908ccd97d016.1.9.9"),sQuery(id+"F2.wireOp",EDGE,"f79f6195-6e67-4fcd-a5d6-908ccd97d016.4.9.9"),sQuery(id+"F2.wireOp",EDGE,"f79f6195-6e67-4fcd-a5d6-908ccd97d016.7.9.9"),sQuery(id+"F2.wireOp",EDGE,"f79f6195-6e67-4fcd-a5d6-908ccd97d016.11.9.9"),sQuery(id+"F2.wireOp",EDGE,"f79f6195-6e67-4fcd-a5d6-908ccd97d016.14.9.9"),sQuery(id+"F2.wireOp",EDGE,"f79f6195-6e67-4fcd-a5d6-908ccd97d016.18.9.9"),sQuery(id+"F2.wireOp",EDGE,"f79f6195-6e67-4fcd-a5d6-908ccd97d016.27.9.9"),sQuery(id+"F2.wireOp",EDGE,"f79f6195-6e67-4fcd-a5d6-908ccd97d016.33.9.9"),sQuery(id+"F2.wireOp",EDGE,"f79f6195-6e67-4fcd-a5d6-908ccd97d016.36.9.9"),sQuery(id+"F2.wireOp",EDGE,"f79f6195-6e67-4fcd-a5d6-908ccd97d016.39.9.9"),sQuery(id+"F2.wireOp",EDGE,"f79f6195-6e67-4fcd-a5d6-908ccd97d016.43.9.9"),sQuery(id+"F2.wireOp",EDGE,"f79f6195-6e67-4fcd-a5d6-908ccd97d016.47.9.9")])],"isStart":false});
            var sketch = newSketch(context, id + "F4", { "sketchPlane" : qUnion([Q0])});
            skLineSegment(sketch, "E18", {"start": v(0, 0) * mm, "end": v(0, 5.08) * mm, "construction": true});
            skArc(sketch, "E19.0", {"start": v(0.25, 5.05) * mm, "mid": v(0, 5.08) * mm, "end": v(-0.25, 5.05) * mm});
            skArc(sketch, "E20.0", {"start": v(0.5, 2.55) * mm, "mid": v(0, 3) * mm, "end": v(-0.5, 2.55) * mm});
            skPoint(sketch, "E21.orphan", {"position": v(0.5, 2.55) * mm});
            skPoint(sketch, "E22.orphan", {"position": v(-0.5, 2.55) * mm});
            skLineSegment(sketch, "E23.direction2", {"start": v(0, 0) * mm, "end": v(0, 5.34) * mm, "construction": true});
            skLineSegment(sketch, "E24", {"start": v(-0.5, 2.55) * mm, "end": v(-0.25, 5.05) * mm});
            skLineSegment(sketch, "E25.MirrorCS", {"start": v(0.5, 2.55) * mm, "end": v(0.25, 5.05) * mm});
            skLineSegment(sketch, "E26.1.0", {"start": v(-2.46, -0.84) * mm, "end": v(-4.5, -2.31) * mm});
            skLineSegment(sketch, "E26.1.1", {"start": v(0, 0) * mm, "end": v(-4.63, -2.67) * mm, "construction": true});
            skPoint(sketch, "E26.1.2", {"position": v(-2.46, -0.84) * mm});
            skPoint(sketch, "E26.1.3", {"position": v(-2.46, -0.84) * mm});
            skArc(sketch, "E26.1.4", {"start": v(-4.5, -2.31) * mm, "mid": v(-4.4, -2.54) * mm, "end": v(-4.25, -2.74) * mm});
            skLineSegment(sketch, "E26.1.5", {"start": v(0, 0) * mm, "end": v(-4.4, -2.54) * mm, "construction": true});
            skPoint(sketch, "E26.1.6", {"position": v(-1.96, -1.7) * mm});
            skLineSegment(sketch, "E26.1.7", {"start": v(-1.96, -1.7) * mm, "end": v(-4.25, -2.74) * mm});
            skArc(sketch, "E26.1.8", {"start": v(-2.46, -0.84) * mm, "mid": v(-2.6, -1.5) * mm, "end": v(-1.96, -1.7) * mm});
            skLineSegment(sketch, "E26.2.0", {"start": v(1.96, -1.7) * mm, "end": v(4.25, -2.74) * mm});
            skLineSegment(sketch, "E26.2.1", {"start": v(0, 0) * mm, "end": v(4.63, -2.67) * mm, "construction": true});
            skPoint(sketch, "E26.2.2", {"position": v(1.96, -1.7) * mm});
            skPoint(sketch, "E26.2.3", {"position": v(1.96, -1.7) * mm});
            skArc(sketch, "E26.2.4", {"start": v(4.25, -2.74) * mm, "mid": v(4.4, -2.54) * mm, "end": v(4.5, -2.31) * mm});
            skLineSegment(sketch, "E26.2.5", {"start": v(0, 0) * mm, "end": v(4.4, -2.54) * mm, "construction": true});
            skPoint(sketch, "E26.2.6", {"position": v(2.46, -0.84) * mm});
            skLineSegment(sketch, "E26.2.7", {"start": v(2.46, -0.84) * mm, "end": v(4.5, -2.31) * mm});
            skArc(sketch, "E26.2.8", {"start": v(1.96, -1.7) * mm, "mid": v(2.6, -1.5) * mm, "end": v(2.46, -0.84) * mm});
            skPoint(sketch, "E26.center", {"position": v(0, 0) * mm});
            skPoint(sketch, "E27.0.1.0", {"position": v(-0.5, 8.55) * mm});
            skLineSegment(sketch, "E27.0.1.1", {"start": v(0, 6) * mm, "end": v(-4.63, 3.33) * mm, "construction": true});
            skLineSegment(sketch, "E27.0.1.2", {"start": v(2.46, 5.16) * mm, "end": v(4.5, 3.69) * mm});
            skPoint(sketch, "E27.0.1.3", {"position": v(0.5, 8.55) * mm});
            skArc(sketch, "E27.0.1.4", {"start": v(-2.46, 5.16) * mm, "mid": v(-2.6, 4.5) * mm, "end": v(-1.96, 4.3) * mm});
            skLineSegment(sketch, "E27.0.1.5", {"start": v(0, 6) * mm, "end": v(0, 11.08) * mm, "construction": true});
            skLineSegment(sketch, "E27.0.1.6", {"start": v(0, 6) * mm, "end": v(4.4, 3.46) * mm, "construction": true});
            skLineSegment(sketch, "E27.0.1.7", {"start": v(-0.5, 8.55) * mm, "end": v(-0.25, 11.05) * mm});
            skLineSegment(sketch, "E27.0.1.8", {"start": v(0, 6) * mm, "end": v(4.63, 3.33) * mm, "construction": true});
            skPoint(sketch, "E27.0.1.9", {"position": v(2.46, 5.16) * mm});
            skPoint(sketch, "E27.0.1.10", {"position": v(-2.46, 5.16) * mm});
            skPoint(sketch, "E27.0.1.11", {"position": v(0, 6) * mm});
            skLineSegment(sketch, "E27.0.1.12", {"start": v(0, 6) * mm, "end": v(-4.4, 3.46) * mm, "construction": true});
            skArc(sketch, "E27.0.1.13", {"start": v(1.96, 4.3) * mm, "mid": v(2.6, 4.5) * mm, "end": v(2.46, 5.16) * mm});
            skPoint(sketch, "E27.0.1.14", {"position": v(-1.96, 4.3) * mm});
            skLineSegment(sketch, "E27.0.1.15", {"start": v(-1.96, 4.3) * mm, "end": v(-4.25, 3.26) * mm});
            skLineSegment(sketch, "E27.0.1.16", {"start": v(-2.46, 5.16) * mm, "end": v(-4.5, 3.69) * mm});
            skPoint(sketch, "E27.0.1.17", {"position": v(1.96, 4.3) * mm});
            skLineSegment(sketch, "E27.0.1.18", {"start": v(0.5, 8.55) * mm, "end": v(0.25, 11.05) * mm});
            skLineSegment(sketch, "E27.0.1.19", {"start": v(1.96, 4.3) * mm, "end": v(4.25, 3.26) * mm});
            skArc(sketch, "E27.0.1.20", {"start": v(0.5, 8.55) * mm, "mid": v(0, 9) * mm, "end": v(-0.5, 8.55) * mm});
            skPoint(sketch, "E27.0.1.21", {"position": v(1.96, 4.3) * mm});
            skPoint(sketch, "E27.0.1.22", {"position": v(0.5, 8.55) * mm});
            skPoint(sketch, "E27.0.1.23", {"position": v(-2.46, 5.16) * mm});
            skArc(sketch, "E27.0.1.24", {"start": v(-4.5, 3.69) * mm, "mid": v(-4.4, 3.46) * mm, "end": v(-4.25, 3.26) * mm});
            skArc(sketch, "E27.0.1.25", {"start": v(4.25, 3.26) * mm, "mid": v(4.4, 3.46) * mm, "end": v(4.5, 3.69) * mm});
            skArc(sketch, "E27.0.1.26", {"start": v(0.25, 11.05) * mm, "mid": v(0, 11.08) * mm, "end": v(-0.25, 11.05) * mm});
            skLineSegment(sketch, "E27.0.1.27", {"start": v(0, 6) * mm, "end": v(0, 11.34) * mm, "construction": true});
            skPoint(sketch, "E27.1.0.0", {"position": v(4.7, -0.45) * mm});
            skLineSegment(sketch, "E27.1.0.1", {"start": v(5.2, -3) * mm, "end": v(0.57, -5.67) * mm, "construction": true});
            skLineSegment(sketch, "E27.1.0.2", {"start": v(7.65, -3.84) * mm, "end": v(9.7, -5.31) * mm});
            skPoint(sketch, "E27.1.0.3", {"position": v(5.7, -0.45) * mm});
            skArc(sketch, "E27.1.0.4", {"start": v(2.74, -3.84) * mm, "mid": v(2.6, -4.5) * mm, "end": v(3.24, -4.7) * mm});
            skLineSegment(sketch, "E27.1.0.5", {"start": v(5.2, -3) * mm, "end": v(5.2, 2.08) * mm, "construction": true});
            skLineSegment(sketch, "E27.1.0.6", {"start": v(5.2, -3) * mm, "end": v(9.6, -5.54) * mm, "construction": true});
            skLineSegment(sketch, "E27.1.0.7", {"start": v(4.7, -0.45) * mm, "end": v(4.95, 2.05) * mm});
            skLineSegment(sketch, "E27.1.0.8", {"start": v(5.2, -3) * mm, "end": v(9.82, -5.67) * mm, "construction": true});
            skPoint(sketch, "E27.1.0.9", {"position": v(7.65, -3.84) * mm});
            skPoint(sketch, "E27.1.0.10", {"position": v(2.74, -3.84) * mm});
            skPoint(sketch, "E27.1.0.11", {"position": v(5.2, -3) * mm});
            skLineSegment(sketch, "E27.1.0.12", {"start": v(5.2, -3) * mm, "end": v(0.8, -5.54) * mm, "construction": true});
            skArc(sketch, "E27.1.0.13", {"start": v(7.16, -4.7) * mm, "mid": v(7.8, -4.5) * mm, "end": v(7.65, -3.84) * mm});
            skPoint(sketch, "E27.1.0.14", {"position": v(3.24, -4.7) * mm});
            skLineSegment(sketch, "E27.1.0.15", {"start": v(3.24, -4.7) * mm, "end": v(0.95, -5.74) * mm});
            skLineSegment(sketch, "E27.1.0.16", {"start": v(2.74, -3.84) * mm, "end": v(0.7, -5.31) * mm});
            skPoint(sketch, "E27.1.0.17", {"position": v(7.16, -4.7) * mm});
            skLineSegment(sketch, "E27.1.0.18", {"start": v(5.7, -0.45) * mm, "end": v(5.44, 2.05) * mm});
            skLineSegment(sketch, "E27.1.0.19", {"start": v(7.16, -4.7) * mm, "end": v(9.45, -5.74) * mm});
            skArc(sketch, "E27.1.0.20", {"start": v(5.7, -0.45) * mm, "mid": v(5.2, 0) * mm, "end": v(4.7, -0.45) * mm});
            skPoint(sketch, "E27.1.0.21", {"position": v(7.16, -4.7) * mm});
            skPoint(sketch, "E27.1.0.22", {"position": v(5.7, -0.45) * mm});
            skPoint(sketch, "E27.1.0.23", {"position": v(2.74, -3.84) * mm});
            skArc(sketch, "E27.1.0.24", {"start": v(0.7, -5.31) * mm, "mid": v(0.8, -5.54) * mm, "end": v(0.95, -5.74) * mm});
            skArc(sketch, "E27.1.0.25", {"start": v(9.45, -5.74) * mm, "mid": v(9.6, -5.54) * mm, "end": v(9.7, -5.31) * mm});
            skArc(sketch, "E27.1.0.26", {"start": v(5.44, 2.05) * mm, "mid": v(5.2, 2.08) * mm, "end": v(4.95, 2.05) * mm});
            skLineSegment(sketch, "E27.1.0.27", {"start": v(5.2, -3) * mm, "end": v(5.2, 2.34) * mm, "construction": true});
            skPoint(sketch, "E27.1.1.0", {"position": v(4.7, 5.55) * mm});
            skLineSegment(sketch, "E27.1.1.1", {"start": v(5.2, 3) * mm, "end": v(0.57, 0.33) * mm, "construction": true});
            skLineSegment(sketch, "E27.1.1.2", {"start": v(7.65, 2.16) * mm, "end": v(9.7, 0.69) * mm});
            skPoint(sketch, "E27.1.1.3", {"position": v(5.7, 5.55) * mm});
            skArc(sketch, "E27.1.1.4", {"start": v(2.74, 2.16) * mm, "mid": v(2.6, 1.5) * mm, "end": v(3.24, 1.3) * mm});
            skLineSegment(sketch, "E27.1.1.5", {"start": v(5.2, 3) * mm, "end": v(5.2, 8.08) * mm, "construction": true});
            skLineSegment(sketch, "E27.1.1.6", {"start": v(5.2, 3) * mm, "end": v(9.6, 0.46) * mm, "construction": true});
            skLineSegment(sketch, "E27.1.1.7", {"start": v(4.7, 5.55) * mm, "end": v(4.95, 8.05) * mm});
            skLineSegment(sketch, "E27.1.1.8", {"start": v(5.2, 3) * mm, "end": v(9.82, 0.33) * mm, "construction": true});
            skPoint(sketch, "E27.1.1.9", {"position": v(7.65, 2.16) * mm});
            skPoint(sketch, "E27.1.1.10", {"position": v(2.74, 2.16) * mm});
            skPoint(sketch, "E27.1.1.11", {"position": v(5.2, 3) * mm});
            skLineSegment(sketch, "E27.1.1.12", {"start": v(5.2, 3) * mm, "end": v(0.8, 0.46) * mm, "construction": true});
            skArc(sketch, "E27.1.1.13", {"start": v(7.16, 1.3) * mm, "mid": v(7.8, 1.5) * mm, "end": v(7.65, 2.16) * mm});
            skPoint(sketch, "E27.1.1.14", {"position": v(3.24, 1.3) * mm});
            skLineSegment(sketch, "E27.1.1.15", {"start": v(3.24, 1.3) * mm, "end": v(0.95, 0.26) * mm});
            skLineSegment(sketch, "E27.1.1.16", {"start": v(2.74, 2.16) * mm, "end": v(0.7, 0.69) * mm});
            skPoint(sketch, "E27.1.1.17", {"position": v(7.16, 1.3) * mm});
            skLineSegment(sketch, "E27.1.1.18", {"start": v(5.7, 5.55) * mm, "end": v(5.44, 8.05) * mm});
            skLineSegment(sketch, "E27.1.1.19", {"start": v(7.16, 1.3) * mm, "end": v(9.45, 0.26) * mm});
            skArc(sketch, "E27.1.1.20", {"start": v(5.7, 5.55) * mm, "mid": v(5.2, 6) * mm, "end": v(4.7, 5.55) * mm});
            skPoint(sketch, "E27.1.1.21", {"position": v(7.16, 1.3) * mm});
            skPoint(sketch, "E27.1.1.22", {"position": v(5.7, 5.55) * mm});
            skPoint(sketch, "E27.1.1.23", {"position": v(2.74, 2.16) * mm});
            skArc(sketch, "E27.1.1.24", {"start": v(0.7, 0.69) * mm, "mid": v(0.8, 0.46) * mm, "end": v(0.95, 0.26) * mm});
            skArc(sketch, "E27.1.1.25", {"start": v(9.45, 0.26) * mm, "mid": v(9.6, 0.46) * mm, "end": v(9.7, 0.69) * mm});
            skArc(sketch, "E27.1.1.26", {"start": v(5.44, 8.05) * mm, "mid": v(5.2, 8.08) * mm, "end": v(4.95, 8.05) * mm});
            skLineSegment(sketch, "E27.1.1.27", {"start": v(5.2, 3) * mm, "end": v(5.2, 8.34) * mm, "construction": true});
            skLineSegment(sketch, "E27.direction1", {"start": v(0, 0) * mm, "end": v(5.2, -3) * mm, "construction": true});
            skLineSegment(sketch, "E27.direction2", {"start": v(0, 0) * mm, "end": v(0, 6) * mm, "construction": true});
            skPoint(sketch, "E28.0.2.0", {"position": v(9.9, -3.45) * mm});
            skLineSegment(sketch, "E28.1.2.0", {"start": v(10.4, -6) * mm, "end": v(5.77, -8.67) * mm, "construction": true});
            skLineSegment(sketch, "E28.4.2.0", {"start": v(12.85, -6.84) * mm, "end": v(14.89, -8.31) * mm});
            skPoint(sketch, "E28.7.2.0", {"position": v(10.89, -3.45) * mm});
            skArc(sketch, "E28.8.2.0", {"start": v(7.94, -6.84) * mm, "mid": v(7.8, -7.5) * mm, "end": v(8.43, -7.7) * mm});
            skLineSegment(sketch, "E28.12.2.0", {"start": v(10.4, -6) * mm, "end": v(10.4, -0.92) * mm, "construction": true});
            skLineSegment(sketch, "E28.15.2.0", {"start": v(10.4, -6) * mm, "end": v(14.8, -8.54) * mm, "construction": true});
            skLineSegment(sketch, "E28.18.2.0", {"start": v(9.9, -3.45) * mm, "end": v(10.15, -0.95) * mm});
            skLineSegment(sketch, "E28.21.2.0", {"start": v(10.4, -6) * mm, "end": v(15.02, -8.67) * mm, "construction": true});
            skPoint(sketch, "E28.24.2.0", {"position": v(12.85, -6.84) * mm});
            skPoint(sketch, "E28.25.2.0", {"position": v(7.94, -6.84) * mm});
            skPoint(sketch, "E28.26.2.0", {"position": v(10.4, -6) * mm});
            skLineSegment(sketch, "E28.27.2.0", {"start": v(10.4, -6) * mm, "end": v(6, -8.54) * mm, "construction": true});
            skArc(sketch, "E28.30.2.0", {"start": v(12.35, -7.7) * mm, "mid": v(13, -7.5) * mm, "end": v(12.85, -6.84) * mm});
            skPoint(sketch, "E28.34.2.0", {"position": v(8.43, -7.7) * mm});
            skLineSegment(sketch, "E28.35.2.0", {"start": v(8.43, -7.7) * mm, "end": v(6.14, -8.74) * mm});
            skLineSegment(sketch, "E28.38.2.0", {"start": v(7.94, -6.84) * mm, "end": v(5.9, -8.31) * mm});
            skPoint(sketch, "E28.41.2.0", {"position": v(12.35, -7.7) * mm});
            skLineSegment(sketch, "E28.42.2.0", {"start": v(10.89, -3.45) * mm, "end": v(10.64, -0.95) * mm});
            skLineSegment(sketch, "E28.45.2.0", {"start": v(12.35, -7.7) * mm, "end": v(14.64, -8.74) * mm});
            skArc(sketch, "E28.48.2.0", {"start": v(10.89, -3.45) * mm, "mid": v(10.4, -3) * mm, "end": v(9.9, -3.45) * mm});
            skPoint(sketch, "E28.52.2.0", {"position": v(12.35, -7.7) * mm});
            skPoint(sketch, "E28.53.2.0", {"position": v(10.89, -3.45) * mm});
            skPoint(sketch, "E28.54.2.0", {"position": v(7.94, -6.84) * mm});
            skArc(sketch, "E28.55.2.0", {"start": v(5.9, -8.31) * mm, "mid": v(6, -8.54) * mm, "end": v(6.14, -8.74) * mm});
            skArc(sketch, "E28.59.2.0", {"start": v(14.64, -8.74) * mm, "mid": v(14.8, -8.54) * mm, "end": v(14.89, -8.31) * mm});
            skArc(sketch, "E28.63.2.0", {"start": v(10.64, -0.95) * mm, "mid": v(10.4, -0.92) * mm, "end": v(10.15, -0.95) * mm});
            skLineSegment(sketch, "E28.67.2.0", {"start": v(10.4, -6) * mm, "end": v(10.4, -0.66) * mm, "construction": true});
            skPoint(sketch, "E28.0.2.1", {"position": v(9.9, 2.55) * mm});
            skLineSegment(sketch, "E28.1.2.1", {"start": v(10.4, 0) * mm, "end": v(5.77, -2.67) * mm, "construction": true});
            skLineSegment(sketch, "E28.4.2.1", {"start": v(12.85, -0.84) * mm, "end": v(14.89, -2.31) * mm});
            skPoint(sketch, "E28.7.2.1", {"position": v(10.89, 2.55) * mm});
            skArc(sketch, "E28.8.2.1", {"start": v(7.94, -0.84) * mm, "mid": v(7.8, -1.5) * mm, "end": v(8.43, -1.7) * mm});
            skLineSegment(sketch, "E28.12.2.1", {"start": v(10.4, 0) * mm, "end": v(10.4, 5.08) * mm, "construction": true});
            skLineSegment(sketch, "E28.15.2.1", {"start": v(10.4, 0) * mm, "end": v(14.8, -2.54) * mm, "construction": true});
            skLineSegment(sketch, "E28.18.2.1", {"start": v(9.9, 2.55) * mm, "end": v(10.15, 5.05) * mm});
            skLineSegment(sketch, "E28.21.2.1", {"start": v(10.4, 0) * mm, "end": v(15.02, -2.67) * mm, "construction": true});
            skPoint(sketch, "E28.24.2.1", {"position": v(12.85, -0.84) * mm});
            skPoint(sketch, "E28.25.2.1", {"position": v(7.94, -0.84) * mm});
            skPoint(sketch, "E28.26.2.1", {"position": v(10.4, 0) * mm});
            skLineSegment(sketch, "E28.27.2.1", {"start": v(10.4, 0) * mm, "end": v(6, -2.54) * mm, "construction": true});
            skArc(sketch, "E28.30.2.1", {"start": v(12.35, -1.7) * mm, "mid": v(13, -1.5) * mm, "end": v(12.85, -0.84) * mm});
            skPoint(sketch, "E28.34.2.1", {"position": v(8.43, -1.7) * mm});
            skLineSegment(sketch, "E28.35.2.1", {"start": v(8.43, -1.7) * mm, "end": v(6.14, -2.74) * mm});
            skLineSegment(sketch, "E28.38.2.1", {"start": v(7.94, -0.84) * mm, "end": v(5.9, -2.31) * mm});
            skPoint(sketch, "E28.41.2.1", {"position": v(12.35, -1.7) * mm});
            skLineSegment(sketch, "E28.42.2.1", {"start": v(10.89, 2.55) * mm, "end": v(10.64, 5.05) * mm});
            skLineSegment(sketch, "E28.45.2.1", {"start": v(12.35, -1.7) * mm, "end": v(14.64, -2.74) * mm});
            skArc(sketch, "E28.48.2.1", {"start": v(10.89, 2.55) * mm, "mid": v(10.4, 3) * mm, "end": v(9.9, 2.55) * mm});
            skPoint(sketch, "E28.52.2.1", {"position": v(12.35, -1.7) * mm});
            skPoint(sketch, "E28.53.2.1", {"position": v(10.89, 2.55) * mm});
            skPoint(sketch, "E28.54.2.1", {"position": v(7.94, -0.84) * mm});
            skArc(sketch, "E28.55.2.1", {"start": v(5.9, -2.31) * mm, "mid": v(6, -2.54) * mm, "end": v(6.14, -2.74) * mm});
            skArc(sketch, "E28.59.2.1", {"start": v(14.64, -2.74) * mm, "mid": v(14.8, -2.54) * mm, "end": v(14.89, -2.31) * mm});
            skArc(sketch, "E28.63.2.1", {"start": v(10.64, 5.05) * mm, "mid": v(10.4, 5.08) * mm, "end": v(10.15, 5.05) * mm});
            skLineSegment(sketch, "E28.67.2.1", {"start": v(10.4, 0) * mm, "end": v(10.4, 5.34) * mm, "construction": true});
            skPoint(sketch, "E28.0.3.0", {"position": v(15.1, -6.45) * mm});
            skLineSegment(sketch, "E28.1.3.0", {"start": v(15.59, -9) * mm, "end": v(10.96, -11.67) * mm, "construction": true});
            skLineSegment(sketch, "E28.4.3.0", {"start": v(18.05, -9.84) * mm, "end": v(20.08, -11.31) * mm});
            skPoint(sketch, "E28.7.3.0", {"position": v(16.09, -6.45) * mm});
            skArc(sketch, "E28.8.3.0", {"start": v(13.13, -9.84) * mm, "mid": v(13, -10.5) * mm, "end": v(13.63, -10.7) * mm});
            skLineSegment(sketch, "E28.12.3.0", {"start": v(15.59, -9) * mm, "end": v(15.59, -3.92) * mm, "construction": true});
            skLineSegment(sketch, "E28.15.3.0", {"start": v(15.59, -9) * mm, "end": v(19.99, -11.54) * mm, "construction": true});
            skLineSegment(sketch, "E28.18.3.0", {"start": v(15.1, -6.45) * mm, "end": v(15.34, -3.95) * mm});
            skLineSegment(sketch, "E28.21.3.0", {"start": v(15.59, -9) * mm, "end": v(20.22, -11.67) * mm, "construction": true});
            skPoint(sketch, "E28.24.3.0", {"position": v(18.05, -9.84) * mm});
            skPoint(sketch, "E28.25.3.0", {"position": v(13.13, -9.84) * mm});
            skPoint(sketch, "E28.26.3.0", {"position": v(15.59, -9) * mm});
            skLineSegment(sketch, "E28.27.3.0", {"start": v(15.59, -9) * mm, "end": v(11.19, -11.54) * mm, "construction": true});
            skArc(sketch, "E28.30.3.0", {"start": v(17.55, -10.7) * mm, "mid": v(18.19, -10.5) * mm, "end": v(18.05, -9.84) * mm});
            skPoint(sketch, "E28.34.3.0", {"position": v(13.63, -10.7) * mm});
            skLineSegment(sketch, "E28.35.3.0", {"start": v(13.63, -10.7) * mm, "end": v(11.34, -11.74) * mm});
            skLineSegment(sketch, "E28.38.3.0", {"start": v(13.13, -9.84) * mm, "end": v(11.1, -11.31) * mm});
            skPoint(sketch, "E28.41.3.0", {"position": v(17.55, -10.7) * mm});
            skLineSegment(sketch, "E28.42.3.0", {"start": v(16.09, -6.45) * mm, "end": v(15.83, -3.95) * mm});
            skLineSegment(sketch, "E28.45.3.0", {"start": v(17.55, -10.7) * mm, "end": v(19.84, -11.74) * mm});
            skArc(sketch, "E28.48.3.0", {"start": v(16.09, -6.45) * mm, "mid": v(15.59, -6) * mm, "end": v(15.1, -6.45) * mm});
            skPoint(sketch, "E28.52.3.0", {"position": v(17.55, -10.7) * mm});
            skPoint(sketch, "E28.53.3.0", {"position": v(16.09, -6.45) * mm});
            skPoint(sketch, "E28.54.3.0", {"position": v(13.13, -9.84) * mm});
            skArc(sketch, "E28.55.3.0", {"start": v(11.1, -11.31) * mm, "mid": v(11.19, -11.54) * mm, "end": v(11.34, -11.74) * mm});
            skArc(sketch, "E28.59.3.0", {"start": v(19.84, -11.74) * mm, "mid": v(19.99, -11.54) * mm, "end": v(20.08, -11.31) * mm});
            skArc(sketch, "E28.63.3.0", {"start": v(15.83, -3.95) * mm, "mid": v(15.59, -3.92) * mm, "end": v(15.34, -3.95) * mm});
            skLineSegment(sketch, "E28.67.3.0", {"start": v(15.59, -9) * mm, "end": v(15.59, -3.66) * mm, "construction": true});
            skPoint(sketch, "E28.0.3.1", {"position": v(15.1, -0.45) * mm});
            skLineSegment(sketch, "E28.1.3.1", {"start": v(15.59, -3) * mm, "end": v(10.96, -5.67) * mm, "construction": true});
            skLineSegment(sketch, "E28.4.3.1", {"start": v(18.05, -3.84) * mm, "end": v(20.08, -5.31) * mm});
            skPoint(sketch, "E28.7.3.1", {"position": v(16.09, -0.45) * mm});
            skArc(sketch, "E28.8.3.1", {"start": v(13.13, -3.84) * mm, "mid": v(13, -4.5) * mm, "end": v(13.63, -4.7) * mm});
            skLineSegment(sketch, "E28.12.3.1", {"start": v(15.59, -3) * mm, "end": v(15.59, 2.08) * mm, "construction": true});
            skLineSegment(sketch, "E28.15.3.1", {"start": v(15.59, -3) * mm, "end": v(19.99, -5.54) * mm, "construction": true});
            skLineSegment(sketch, "E28.18.3.1", {"start": v(15.1, -0.45) * mm, "end": v(15.34, 2.05) * mm});
            skLineSegment(sketch, "E28.21.3.1", {"start": v(15.59, -3) * mm, "end": v(20.22, -5.67) * mm, "construction": true});
            skPoint(sketch, "E28.24.3.1", {"position": v(18.05, -3.84) * mm});
            skPoint(sketch, "E28.25.3.1", {"position": v(13.13, -3.84) * mm});
            skPoint(sketch, "E28.26.3.1", {"position": v(15.59, -3) * mm});
            skLineSegment(sketch, "E28.27.3.1", {"start": v(15.59, -3) * mm, "end": v(11.19, -5.54) * mm, "construction": true});
            skArc(sketch, "E28.30.3.1", {"start": v(17.55, -4.7) * mm, "mid": v(18.19, -4.5) * mm, "end": v(18.05, -3.84) * mm});
            skPoint(sketch, "E28.34.3.1", {"position": v(13.63, -4.7) * mm});
            skLineSegment(sketch, "E28.35.3.1", {"start": v(13.63, -4.7) * mm, "end": v(11.34, -5.74) * mm});
            skLineSegment(sketch, "E28.38.3.1", {"start": v(13.13, -3.84) * mm, "end": v(11.1, -5.31) * mm});
            skPoint(sketch, "E28.41.3.1", {"position": v(17.55, -4.7) * mm});
            skLineSegment(sketch, "E28.42.3.1", {"start": v(16.09, -0.45) * mm, "end": v(15.83, 2.05) * mm});
            skLineSegment(sketch, "E28.45.3.1", {"start": v(17.55, -4.7) * mm, "end": v(19.84, -5.74) * mm});
            skArc(sketch, "E28.48.3.1", {"start": v(16.09, -0.45) * mm, "mid": v(15.59, 0) * mm, "end": v(15.1, -0.45) * mm});
            skPoint(sketch, "E28.52.3.1", {"position": v(17.55, -4.7) * mm});
            skPoint(sketch, "E28.53.3.1", {"position": v(16.09, -0.45) * mm});
            skPoint(sketch, "E28.54.3.1", {"position": v(13.13, -3.84) * mm});
            skArc(sketch, "E28.55.3.1", {"start": v(11.1, -5.31) * mm, "mid": v(11.19, -5.54) * mm, "end": v(11.34, -5.74) * mm});
            skArc(sketch, "E28.59.3.1", {"start": v(19.84, -5.74) * mm, "mid": v(19.99, -5.54) * mm, "end": v(20.08, -5.31) * mm});
            skArc(sketch, "E28.63.3.1", {"start": v(15.83, 2.05) * mm, "mid": v(15.59, 2.08) * mm, "end": v(15.34, 2.05) * mm});
            skLineSegment(sketch, "E28.67.3.1", {"start": v(15.59, -3) * mm, "end": v(15.59, 2.34) * mm, "construction": true});
            skPoint(sketch, "E28.0.4.0", {"position": v(20.29, -9.45) * mm});
            skLineSegment(sketch, "E28.1.4.0", {"start": v(20.78, -12) * mm, "end": v(16.16, -14.67) * mm, "construction": true});
            skLineSegment(sketch, "E28.4.4.0", {"start": v(23.24, -12.84) * mm, "end": v(25.28, -14.31) * mm});
            skPoint(sketch, "E28.7.4.0", {"position": v(21.28, -9.45) * mm});
            skArc(sketch, "E28.8.4.0", {"start": v(18.33, -12.84) * mm, "mid": v(18.19, -13.5) * mm, "end": v(18.82, -13.7) * mm});
            skLineSegment(sketch, "E28.12.4.0", {"start": v(20.78, -12) * mm, "end": v(20.78, -6.92) * mm, "construction": true});
            skLineSegment(sketch, "E28.15.4.0", {"start": v(20.78, -12) * mm, "end": v(25.18, -14.54) * mm, "construction": true});
            skLineSegment(sketch, "E28.18.4.0", {"start": v(20.29, -9.45) * mm, "end": v(20.54, -6.95) * mm});
            skLineSegment(sketch, "E28.21.4.0", {"start": v(20.78, -12) * mm, "end": v(25.41, -14.67) * mm, "construction": true});
            skPoint(sketch, "E28.24.4.0", {"position": v(23.24, -12.84) * mm});
            skPoint(sketch, "E28.25.4.0", {"position": v(18.33, -12.84) * mm});
            skPoint(sketch, "E28.26.4.0", {"position": v(20.78, -12) * mm});
            skLineSegment(sketch, "E28.27.4.0", {"start": v(20.78, -12) * mm, "end": v(16.38, -14.54) * mm, "construction": true});
            skArc(sketch, "E28.30.4.0", {"start": v(22.74, -13.7) * mm, "mid": v(23.38, -13.5) * mm, "end": v(23.24, -12.84) * mm});
            skPoint(sketch, "E28.34.4.0", {"position": v(18.82, -13.7) * mm});
            skLineSegment(sketch, "E28.35.4.0", {"start": v(18.82, -13.7) * mm, "end": v(16.53, -14.74) * mm});
            skLineSegment(sketch, "E28.38.4.0", {"start": v(18.33, -12.84) * mm, "end": v(16.29, -14.31) * mm});
            skPoint(sketch, "E28.41.4.0", {"position": v(22.74, -13.7) * mm});
            skLineSegment(sketch, "E28.42.4.0", {"start": v(21.28, -9.45) * mm, "end": v(21.03, -6.95) * mm});
            skLineSegment(sketch, "E28.45.4.0", {"start": v(22.74, -13.7) * mm, "end": v(25.03, -14.74) * mm});
            skArc(sketch, "E28.48.4.0", {"start": v(21.28, -9.45) * mm, "mid": v(20.78, -9) * mm, "end": v(20.29, -9.45) * mm});
            skPoint(sketch, "E28.52.4.0", {"position": v(22.74, -13.7) * mm});
            skPoint(sketch, "E28.53.4.0", {"position": v(21.28, -9.45) * mm});
            skPoint(sketch, "E28.54.4.0", {"position": v(18.33, -12.84) * mm});
            skArc(sketch, "E28.55.4.0", {"start": v(16.29, -14.31) * mm, "mid": v(16.38, -14.54) * mm, "end": v(16.53, -14.74) * mm});
            skArc(sketch, "E28.59.4.0", {"start": v(25.03, -14.74) * mm, "mid": v(25.18, -14.54) * mm, "end": v(25.28, -14.31) * mm});
            skArc(sketch, "E28.63.4.0", {"start": v(21.03, -6.95) * mm, "mid": v(20.78, -6.92) * mm, "end": v(20.54, -6.95) * mm});
            skLineSegment(sketch, "E28.67.4.0", {"start": v(20.78, -12) * mm, "end": v(20.78, -6.66) * mm, "construction": true});
            skPoint(sketch, "E28.0.4.1", {"position": v(20.29, -3.45) * mm});
            skLineSegment(sketch, "E28.1.4.1", {"start": v(20.78, -6) * mm, "end": v(16.16, -8.67) * mm, "construction": true});
            skLineSegment(sketch, "E28.4.4.1", {"start": v(23.24, -6.84) * mm, "end": v(25.28, -8.31) * mm});
            skPoint(sketch, "E28.7.4.1", {"position": v(21.28, -3.45) * mm});
            skArc(sketch, "E28.8.4.1", {"start": v(18.33, -6.84) * mm, "mid": v(18.19, -7.5) * mm, "end": v(18.82, -7.7) * mm});
            skLineSegment(sketch, "E28.12.4.1", {"start": v(20.78, -6) * mm, "end": v(20.78, -0.92) * mm, "construction": true});
            skLineSegment(sketch, "E28.15.4.1", {"start": v(20.78, -6) * mm, "end": v(25.18, -8.54) * mm, "construction": true});
            skLineSegment(sketch, "E28.18.4.1", {"start": v(20.29, -3.45) * mm, "end": v(20.54, -0.95) * mm});
            skLineSegment(sketch, "E28.21.4.1", {"start": v(20.78, -6) * mm, "end": v(25.41, -8.67) * mm, "construction": true});
            skPoint(sketch, "E28.24.4.1", {"position": v(23.24, -6.84) * mm});
            skPoint(sketch, "E28.25.4.1", {"position": v(18.33, -6.84) * mm});
            skPoint(sketch, "E28.26.4.1", {"position": v(20.78, -6) * mm});
            skLineSegment(sketch, "E28.27.4.1", {"start": v(20.78, -6) * mm, "end": v(16.38, -8.54) * mm, "construction": true});
            skArc(sketch, "E28.30.4.1", {"start": v(22.74, -7.7) * mm, "mid": v(23.38, -7.5) * mm, "end": v(23.24, -6.84) * mm});
            skPoint(sketch, "E28.34.4.1", {"position": v(18.82, -7.7) * mm});
            skLineSegment(sketch, "E28.35.4.1", {"start": v(18.82, -7.7) * mm, "end": v(16.53, -8.74) * mm});
            skLineSegment(sketch, "E28.38.4.1", {"start": v(18.33, -6.84) * mm, "end": v(16.29, -8.31) * mm});
            skPoint(sketch, "E28.41.4.1", {"position": v(22.74, -7.7) * mm});
            skLineSegment(sketch, "E28.42.4.1", {"start": v(21.28, -3.45) * mm, "end": v(21.03, -0.95) * mm});
            skLineSegment(sketch, "E28.45.4.1", {"start": v(22.74, -7.7) * mm, "end": v(25.03, -8.74) * mm});
            skArc(sketch, "E28.48.4.1", {"start": v(21.28, -3.45) * mm, "mid": v(20.78, -3) * mm, "end": v(20.29, -3.45) * mm});
            skPoint(sketch, "E28.52.4.1", {"position": v(22.74, -7.7) * mm});
            skPoint(sketch, "E28.53.4.1", {"position": v(21.28, -3.45) * mm});
            skPoint(sketch, "E28.54.4.1", {"position": v(18.33, -6.84) * mm});
            skArc(sketch, "E28.55.4.1", {"start": v(16.29, -8.31) * mm, "mid": v(16.38, -8.54) * mm, "end": v(16.53, -8.74) * mm});
            skArc(sketch, "E28.59.4.1", {"start": v(25.03, -8.74) * mm, "mid": v(25.18, -8.54) * mm, "end": v(25.28, -8.31) * mm});
            skArc(sketch, "E28.63.4.1", {"start": v(21.03, -0.95) * mm, "mid": v(20.78, -0.92) * mm, "end": v(20.54, -0.95) * mm});
            skLineSegment(sketch, "E28.67.4.1", {"start": v(20.78, -6) * mm, "end": v(20.78, -0.66) * mm, "construction": true});
            skPoint(sketch, "E28.0.5.0", {"position": v(25.48, -12.45) * mm});
            skLineSegment(sketch, "E28.1.5.0", {"start": v(25.98, -15) * mm, "end": v(21.35, -17.67) * mm, "construction": true});
            skLineSegment(sketch, "E28.4.5.0", {"start": v(28.44, -15.84) * mm, "end": v(30.48, -17.31) * mm});
            skPoint(sketch, "E28.7.5.0", {"position": v(26.48, -12.45) * mm});
            skArc(sketch, "E28.8.5.0", {"start": v(23.52, -15.84) * mm, "mid": v(23.38, -16.5) * mm, "end": v(24.02, -16.7) * mm});
            skLineSegment(sketch, "E28.12.5.0", {"start": v(25.98, -15) * mm, "end": v(25.98, -9.92) * mm, "construction": true});
            skLineSegment(sketch, "E28.15.5.0", {"start": v(25.98, -15) * mm, "end": v(30.38, -17.54) * mm, "construction": true});
            skLineSegment(sketch, "E28.18.5.0", {"start": v(25.48, -12.45) * mm, "end": v(25.73, -9.95) * mm});
            skLineSegment(sketch, "E28.21.5.0", {"start": v(25.98, -15) * mm, "end": v(30.6, -17.67) * mm, "construction": true});
            skPoint(sketch, "E28.24.5.0", {"position": v(28.44, -15.84) * mm});
            skPoint(sketch, "E28.25.5.0", {"position": v(23.52, -15.84) * mm});
            skPoint(sketch, "E28.26.5.0", {"position": v(25.98, -15) * mm});
            skLineSegment(sketch, "E28.27.5.0", {"start": v(25.98, -15) * mm, "end": v(21.58, -17.54) * mm, "construction": true});
            skArc(sketch, "E28.30.5.0", {"start": v(27.94, -16.7) * mm, "mid": v(28.58, -16.5) * mm, "end": v(28.44, -15.84) * mm});
            skPoint(sketch, "E28.34.5.0", {"position": v(24.02, -16.7) * mm});
            skLineSegment(sketch, "E28.35.5.0", {"start": v(24.02, -16.7) * mm, "end": v(21.73, -17.74) * mm});
            skLineSegment(sketch, "E28.38.5.0", {"start": v(23.52, -15.84) * mm, "end": v(21.48, -17.31) * mm});
            skPoint(sketch, "E28.41.5.0", {"position": v(27.94, -16.7) * mm});
            skLineSegment(sketch, "E28.42.5.0", {"start": v(26.48, -12.45) * mm, "end": v(26.23, -9.95) * mm});
            skLineSegment(sketch, "E28.45.5.0", {"start": v(27.94, -16.7) * mm, "end": v(30.23, -17.74) * mm});
            skArc(sketch, "E28.48.5.0", {"start": v(26.48, -12.45) * mm, "mid": v(25.98, -12) * mm, "end": v(25.48, -12.45) * mm});
            skPoint(sketch, "E28.52.5.0", {"position": v(27.94, -16.7) * mm});
            skPoint(sketch, "E28.53.5.0", {"position": v(26.48, -12.45) * mm});
            skPoint(sketch, "E28.54.5.0", {"position": v(23.52, -15.84) * mm});
            skArc(sketch, "E28.55.5.0", {"start": v(21.48, -17.31) * mm, "mid": v(21.58, -17.54) * mm, "end": v(21.73, -17.74) * mm});
            skArc(sketch, "E28.59.5.0", {"start": v(30.23, -17.74) * mm, "mid": v(30.38, -17.54) * mm, "end": v(30.48, -17.31) * mm});
            skArc(sketch, "E28.63.5.0", {"start": v(26.23, -9.95) * mm, "mid": v(25.98, -9.92) * mm, "end": v(25.73, -9.95) * mm});
            skLineSegment(sketch, "E28.67.5.0", {"start": v(25.98, -15) * mm, "end": v(25.98, -9.66) * mm, "construction": true});
            skPoint(sketch, "E28.0.5.1", {"position": v(25.48, -6.45) * mm});
            skLineSegment(sketch, "E28.1.5.1", {"start": v(25.98, -9) * mm, "end": v(21.35, -11.67) * mm, "construction": true});
            skLineSegment(sketch, "E28.4.5.1", {"start": v(28.44, -9.84) * mm, "end": v(30.48, -11.31) * mm});
            skPoint(sketch, "E28.7.5.1", {"position": v(26.48, -6.45) * mm});
            skArc(sketch, "E28.8.5.1", {"start": v(23.52, -9.84) * mm, "mid": v(23.38, -10.5) * mm, "end": v(24.02, -10.7) * mm});
            skLineSegment(sketch, "E28.12.5.1", {"start": v(25.98, -9) * mm, "end": v(25.98, -3.92) * mm, "construction": true});
            skLineSegment(sketch, "E28.15.5.1", {"start": v(25.98, -9) * mm, "end": v(30.38, -11.54) * mm, "construction": true});
            skLineSegment(sketch, "E28.18.5.1", {"start": v(25.48, -6.45) * mm, "end": v(25.73, -3.95) * mm});
            skLineSegment(sketch, "E28.21.5.1", {"start": v(25.98, -9) * mm, "end": v(30.6, -11.67) * mm, "construction": true});
            skPoint(sketch, "E28.24.5.1", {"position": v(28.44, -9.84) * mm});
            skPoint(sketch, "E28.25.5.1", {"position": v(23.52, -9.84) * mm});
            skPoint(sketch, "E28.26.5.1", {"position": v(25.98, -9) * mm});
            skLineSegment(sketch, "E28.27.5.1", {"start": v(25.98, -9) * mm, "end": v(21.58, -11.54) * mm, "construction": true});
            skArc(sketch, "E28.30.5.1", {"start": v(27.94, -10.7) * mm, "mid": v(28.58, -10.5) * mm, "end": v(28.44, -9.84) * mm});
            skPoint(sketch, "E28.34.5.1", {"position": v(24.02, -10.7) * mm});
            skLineSegment(sketch, "E28.35.5.1", {"start": v(24.02, -10.7) * mm, "end": v(21.73, -11.74) * mm});
            skLineSegment(sketch, "E28.38.5.1", {"start": v(23.52, -9.84) * mm, "end": v(21.48, -11.31) * mm});
            skPoint(sketch, "E28.41.5.1", {"position": v(27.94, -10.7) * mm});
            skLineSegment(sketch, "E28.42.5.1", {"start": v(26.48, -6.45) * mm, "end": v(26.23, -3.95) * mm});
            skLineSegment(sketch, "E28.45.5.1", {"start": v(27.94, -10.7) * mm, "end": v(30.23, -11.74) * mm});
            skArc(sketch, "E28.48.5.1", {"start": v(26.48, -6.45) * mm, "mid": v(25.98, -6) * mm, "end": v(25.48, -6.45) * mm});
            skPoint(sketch, "E28.52.5.1", {"position": v(27.94, -10.7) * mm});
            skPoint(sketch, "E28.53.5.1", {"position": v(26.48, -6.45) * mm});
            skPoint(sketch, "E28.54.5.1", {"position": v(23.52, -9.84) * mm});
            skArc(sketch, "E28.55.5.1", {"start": v(21.48, -11.31) * mm, "mid": v(21.58, -11.54) * mm, "end": v(21.73, -11.74) * mm});
            skArc(sketch, "E28.59.5.1", {"start": v(30.23, -11.74) * mm, "mid": v(30.38, -11.54) * mm, "end": v(30.48, -11.31) * mm});
            skArc(sketch, "E28.63.5.1", {"start": v(26.23, -3.95) * mm, "mid": v(25.98, -3.92) * mm, "end": v(25.73, -3.95) * mm});
            skLineSegment(sketch, "E28.67.5.1", {"start": v(25.98, -9) * mm, "end": v(25.98, -3.66) * mm, "construction": true});
            skPoint(sketch, "E28.0.6.0", {"position": v(30.68, -15.45) * mm});
            skLineSegment(sketch, "E28.1.6.0", {"start": v(31.18, -18) * mm, "end": v(26.55, -20.67) * mm, "construction": true});
            skLineSegment(sketch, "E28.4.6.0", {"start": v(33.63, -18.84) * mm, "end": v(35.67, -20.31) * mm});
            skPoint(sketch, "E28.7.6.0", {"position": v(31.67, -15.45) * mm});
            skArc(sketch, "E28.8.6.0", {"start": v(28.72, -18.84) * mm, "mid": v(28.58, -19.5) * mm, "end": v(29.22, -19.7) * mm});
            skLineSegment(sketch, "E28.12.6.0", {"start": v(31.18, -18) * mm, "end": v(31.18, -12.92) * mm, "construction": true});
            skLineSegment(sketch, "E28.15.6.0", {"start": v(31.18, -18) * mm, "end": v(35.58, -20.54) * mm, "construction": true});
            skLineSegment(sketch, "E28.18.6.0", {"start": v(30.68, -15.45) * mm, "end": v(30.93, -12.95) * mm});
            skLineSegment(sketch, "E28.21.6.0", {"start": v(31.18, -18) * mm, "end": v(35.8, -20.67) * mm, "construction": true});
            skPoint(sketch, "E28.24.6.0", {"position": v(33.63, -18.84) * mm});
            skPoint(sketch, "E28.25.6.0", {"position": v(28.72, -18.84) * mm});
            skPoint(sketch, "E28.26.6.0", {"position": v(31.18, -18) * mm});
            skLineSegment(sketch, "E28.27.6.0", {"start": v(31.18, -18) * mm, "end": v(26.78, -20.54) * mm, "construction": true});
            skArc(sketch, "E28.30.6.0", {"start": v(33.14, -19.7) * mm, "mid": v(33.77, -19.5) * mm, "end": v(33.63, -18.84) * mm});
            skPoint(sketch, "E28.34.6.0", {"position": v(29.22, -19.7) * mm});
            skLineSegment(sketch, "E28.35.6.0", {"start": v(29.22, -19.7) * mm, "end": v(26.93, -20.74) * mm});
            skLineSegment(sketch, "E28.38.6.0", {"start": v(28.72, -18.84) * mm, "end": v(26.68, -20.31) * mm});
            skPoint(sketch, "E28.41.6.0", {"position": v(33.14, -19.7) * mm});
            skLineSegment(sketch, "E28.42.6.0", {"start": v(31.67, -15.45) * mm, "end": v(31.42, -12.95) * mm});
            skLineSegment(sketch, "E28.45.6.0", {"start": v(33.14, -19.7) * mm, "end": v(35.43, -20.74) * mm});
            skArc(sketch, "E28.48.6.0", {"start": v(31.67, -15.45) * mm, "mid": v(31.18, -15) * mm, "end": v(30.68, -15.45) * mm});
            skPoint(sketch, "E28.52.6.0", {"position": v(33.14, -19.7) * mm});
            skPoint(sketch, "E28.53.6.0", {"position": v(31.67, -15.45) * mm});
            skPoint(sketch, "E28.54.6.0", {"position": v(28.72, -18.84) * mm});
            skArc(sketch, "E28.55.6.0", {"start": v(26.68, -20.31) * mm, "mid": v(26.78, -20.54) * mm, "end": v(26.93, -20.74) * mm});
            skArc(sketch, "E28.59.6.0", {"start": v(35.43, -20.74) * mm, "mid": v(35.58, -20.54) * mm, "end": v(35.67, -20.31) * mm});
            skArc(sketch, "E28.63.6.0", {"start": v(31.42, -12.95) * mm, "mid": v(31.18, -12.92) * mm, "end": v(30.93, -12.95) * mm});
            skLineSegment(sketch, "E28.67.6.0", {"start": v(31.18, -18) * mm, "end": v(31.18, -12.66) * mm, "construction": true});
            skPoint(sketch, "E28.0.6.1", {"position": v(30.68, -9.45) * mm});
            skLineSegment(sketch, "E28.1.6.1", {"start": v(31.18, -12) * mm, "end": v(26.55, -14.67) * mm, "construction": true});
            skLineSegment(sketch, "E28.4.6.1", {"start": v(33.63, -12.84) * mm, "end": v(35.67, -14.31) * mm});
            skPoint(sketch, "E28.7.6.1", {"position": v(31.67, -9.45) * mm});
            skArc(sketch, "E28.8.6.1", {"start": v(28.72, -12.84) * mm, "mid": v(28.58, -13.5) * mm, "end": v(29.22, -13.7) * mm});
            skLineSegment(sketch, "E28.12.6.1", {"start": v(31.18, -12) * mm, "end": v(31.18, -6.92) * mm, "construction": true});
            skLineSegment(sketch, "E28.15.6.1", {"start": v(31.18, -12) * mm, "end": v(35.58, -14.54) * mm, "construction": true});
            skLineSegment(sketch, "E28.18.6.1", {"start": v(30.68, -9.45) * mm, "end": v(30.93, -6.95) * mm});
            skLineSegment(sketch, "E28.21.6.1", {"start": v(31.18, -12) * mm, "end": v(35.8, -14.67) * mm, "construction": true});
            skPoint(sketch, "E28.24.6.1", {"position": v(33.63, -12.84) * mm});
            skPoint(sketch, "E28.25.6.1", {"position": v(28.72, -12.84) * mm});
            skPoint(sketch, "E28.26.6.1", {"position": v(31.18, -12) * mm});
            skLineSegment(sketch, "E28.27.6.1", {"start": v(31.18, -12) * mm, "end": v(26.78, -14.54) * mm, "construction": true});
            skArc(sketch, "E28.30.6.1", {"start": v(33.14, -13.7) * mm, "mid": v(33.77, -13.5) * mm, "end": v(33.63, -12.84) * mm});
            skPoint(sketch, "E28.34.6.1", {"position": v(29.22, -13.7) * mm});
            skLineSegment(sketch, "E28.35.6.1", {"start": v(29.22, -13.7) * mm, "end": v(26.93, -14.74) * mm});
            skLineSegment(sketch, "E28.38.6.1", {"start": v(28.72, -12.84) * mm, "end": v(26.68, -14.31) * mm});
            skPoint(sketch, "E28.41.6.1", {"position": v(33.14, -13.7) * mm});
            skLineSegment(sketch, "E28.42.6.1", {"start": v(31.67, -9.45) * mm, "end": v(31.42, -6.95) * mm});
            skLineSegment(sketch, "E28.45.6.1", {"start": v(33.14, -13.7) * mm, "end": v(35.43, -14.74) * mm});
            skArc(sketch, "E28.48.6.1", {"start": v(31.67, -9.45) * mm, "mid": v(31.18, -9) * mm, "end": v(30.68, -9.45) * mm});
            skPoint(sketch, "E28.52.6.1", {"position": v(33.14, -13.7) * mm});
            skPoint(sketch, "E28.53.6.1", {"position": v(31.67, -9.45) * mm});
            skPoint(sketch, "E28.54.6.1", {"position": v(28.72, -12.84) * mm});
            skArc(sketch, "E28.55.6.1", {"start": v(26.68, -14.31) * mm, "mid": v(26.78, -14.54) * mm, "end": v(26.93, -14.74) * mm});
            skArc(sketch, "E28.59.6.1", {"start": v(35.43, -14.74) * mm, "mid": v(35.58, -14.54) * mm, "end": v(35.67, -14.31) * mm});
            skArc(sketch, "E28.63.6.1", {"start": v(31.42, -6.95) * mm, "mid": v(31.18, -6.92) * mm, "end": v(30.93, -6.95) * mm});
            skLineSegment(sketch, "E28.67.6.1", {"start": v(31.18, -12) * mm, "end": v(31.18, -6.66) * mm, "construction": true});
            skPoint(sketch, "E28.0.7.0", {"position": v(35.88, -18.45) * mm});
            skLineSegment(sketch, "E28.1.7.0", {"start": v(36.37, -21) * mm, "end": v(31.75, -23.67) * mm, "construction": true});
            skLineSegment(sketch, "E28.4.7.0", {"start": v(38.83, -21.84) * mm, "end": v(40.87, -23.31) * mm});
            skPoint(sketch, "E28.7.7.0", {"position": v(36.87, -18.45) * mm});
            skArc(sketch, "E28.8.7.0", {"start": v(33.92, -21.84) * mm, "mid": v(33.77, -22.5) * mm, "end": v(34.41, -22.7) * mm});
            skLineSegment(sketch, "E28.12.7.0", {"start": v(36.37, -21) * mm, "end": v(36.37, -15.92) * mm, "construction": true});
            skLineSegment(sketch, "E28.15.7.0", {"start": v(36.37, -21) * mm, "end": v(40.77, -23.54) * mm, "construction": true});
            skLineSegment(sketch, "E28.18.7.0", {"start": v(35.88, -18.45) * mm, "end": v(36.13, -15.95) * mm});
            skLineSegment(sketch, "E28.21.7.0", {"start": v(36.37, -21) * mm, "end": v(41, -23.67) * mm, "construction": true});
            skPoint(sketch, "E28.24.7.0", {"position": v(38.83, -21.84) * mm});
            skPoint(sketch, "E28.25.7.0", {"position": v(33.92, -21.84) * mm});
            skPoint(sketch, "E28.26.7.0", {"position": v(36.37, -21) * mm});
            skLineSegment(sketch, "E28.27.7.0", {"start": v(36.37, -21) * mm, "end": v(31.97, -23.54) * mm, "construction": true});
            skArc(sketch, "E28.30.7.0", {"start": v(38.33, -22.7) * mm, "mid": v(38.97, -22.5) * mm, "end": v(38.83, -21.84) * mm});
            skPoint(sketch, "E28.34.7.0", {"position": v(34.41, -22.7) * mm});
            skLineSegment(sketch, "E28.35.7.0", {"start": v(34.41, -22.7) * mm, "end": v(32.12, -23.74) * mm});
            skLineSegment(sketch, "E28.38.7.0", {"start": v(33.92, -21.84) * mm, "end": v(31.88, -23.31) * mm});
            skPoint(sketch, "E28.41.7.0", {"position": v(38.33, -22.7) * mm});
            skLineSegment(sketch, "E28.42.7.0", {"start": v(36.87, -18.45) * mm, "end": v(36.62, -15.95) * mm});
            skLineSegment(sketch, "E28.45.7.0", {"start": v(38.33, -22.7) * mm, "end": v(40.62, -23.74) * mm});
            skArc(sketch, "E28.48.7.0", {"start": v(36.87, -18.45) * mm, "mid": v(36.37, -18) * mm, "end": v(35.88, -18.45) * mm});
            skPoint(sketch, "E28.52.7.0", {"position": v(38.33, -22.7) * mm});
            skPoint(sketch, "E28.53.7.0", {"position": v(36.87, -18.45) * mm});
            skPoint(sketch, "E28.54.7.0", {"position": v(33.92, -21.84) * mm});
            skArc(sketch, "E28.55.7.0", {"start": v(31.88, -23.31) * mm, "mid": v(31.97, -23.54) * mm, "end": v(32.12, -23.74) * mm});
            skArc(sketch, "E28.59.7.0", {"start": v(40.62, -23.74) * mm, "mid": v(40.77, -23.54) * mm, "end": v(40.87, -23.31) * mm});
            skArc(sketch, "E28.63.7.0", {"start": v(36.62, -15.95) * mm, "mid": v(36.37, -15.92) * mm, "end": v(36.13, -15.95) * mm});
            skLineSegment(sketch, "E28.67.7.0", {"start": v(36.37, -21) * mm, "end": v(36.37, -15.66) * mm, "construction": true});
            skPoint(sketch, "E28.0.7.1", {"position": v(35.88, -12.45) * mm});
            skLineSegment(sketch, "E28.1.7.1", {"start": v(36.37, -15) * mm, "end": v(31.75, -17.67) * mm, "construction": true});
            skLineSegment(sketch, "E28.4.7.1", {"start": v(38.83, -15.84) * mm, "end": v(40.87, -17.31) * mm});
            skPoint(sketch, "E28.7.7.1", {"position": v(36.87, -12.45) * mm});
            skArc(sketch, "E28.8.7.1", {"start": v(33.92, -15.84) * mm, "mid": v(33.77, -16.5) * mm, "end": v(34.41, -16.7) * mm});
            skLineSegment(sketch, "E28.12.7.1", {"start": v(36.37, -15) * mm, "end": v(36.37, -9.92) * mm, "construction": true});
            skLineSegment(sketch, "E28.15.7.1", {"start": v(36.37, -15) * mm, "end": v(40.77, -17.54) * mm, "construction": true});
            skLineSegment(sketch, "E28.18.7.1", {"start": v(35.88, -12.45) * mm, "end": v(36.13, -9.95) * mm});
            skLineSegment(sketch, "E28.21.7.1", {"start": v(36.37, -15) * mm, "end": v(41, -17.67) * mm, "construction": true});
            skPoint(sketch, "E28.24.7.1", {"position": v(38.83, -15.84) * mm});
            skPoint(sketch, "E28.25.7.1", {"position": v(33.92, -15.84) * mm});
            skPoint(sketch, "E28.26.7.1", {"position": v(36.37, -15) * mm});
            skLineSegment(sketch, "E28.27.7.1", {"start": v(36.37, -15) * mm, "end": v(31.97, -17.54) * mm, "construction": true});
            skArc(sketch, "E28.30.7.1", {"start": v(38.33, -16.7) * mm, "mid": v(38.97, -16.5) * mm, "end": v(38.83, -15.84) * mm});
            skPoint(sketch, "E28.34.7.1", {"position": v(34.41, -16.7) * mm});
            skLineSegment(sketch, "E28.35.7.1", {"start": v(34.41, -16.7) * mm, "end": v(32.12, -17.74) * mm});
            skLineSegment(sketch, "E28.38.7.1", {"start": v(33.92, -15.84) * mm, "end": v(31.88, -17.31) * mm});
            skPoint(sketch, "E28.41.7.1", {"position": v(38.33, -16.7) * mm});
            skLineSegment(sketch, "E28.42.7.1", {"start": v(36.87, -12.45) * mm, "end": v(36.62, -9.95) * mm});
            skLineSegment(sketch, "E28.45.7.1", {"start": v(38.33, -16.7) * mm, "end": v(40.62, -17.74) * mm});
            skArc(sketch, "E28.48.7.1", {"start": v(36.87, -12.45) * mm, "mid": v(36.37, -12) * mm, "end": v(35.88, -12.45) * mm});
            skPoint(sketch, "E28.52.7.1", {"position": v(38.33, -16.7) * mm});
            skPoint(sketch, "E28.53.7.1", {"position": v(36.87, -12.45) * mm});
            skPoint(sketch, "E28.54.7.1", {"position": v(33.92, -15.84) * mm});
            skArc(sketch, "E28.55.7.1", {"start": v(31.88, -17.31) * mm, "mid": v(31.97, -17.54) * mm, "end": v(32.12, -17.74) * mm});
            skArc(sketch, "E28.59.7.1", {"start": v(40.62, -17.74) * mm, "mid": v(40.77, -17.54) * mm, "end": v(40.87, -17.31) * mm});
            skArc(sketch, "E28.63.7.1", {"start": v(36.62, -9.95) * mm, "mid": v(36.37, -9.92) * mm, "end": v(36.13, -9.95) * mm});
            skLineSegment(sketch, "E28.67.7.1", {"start": v(36.37, -15) * mm, "end": v(36.37, -9.66) * mm, "construction": true});
            skPoint(sketch, "E28.0.8.0", {"position": v(41.07, -21.45) * mm});
            skLineSegment(sketch, "E28.1.8.0", {"start": v(41.57, -24) * mm, "end": v(36.94, -26.67) * mm, "construction": true});
            skLineSegment(sketch, "E28.4.8.0", {"start": v(44.03, -24.84) * mm, "end": v(46.07, -26.31) * mm});
            skPoint(sketch, "E28.7.8.0", {"position": v(42.07, -21.45) * mm});
            skArc(sketch, "E28.8.8.0", {"start": v(39.11, -24.84) * mm, "mid": v(38.97, -25.5) * mm, "end": v(39.6, -25.7) * mm});
            skLineSegment(sketch, "E28.12.8.0", {"start": v(41.57, -24) * mm, "end": v(41.57, -18.92) * mm, "construction": true});
            skLineSegment(sketch, "E28.15.8.0", {"start": v(41.57, -24) * mm, "end": v(45.97, -26.54) * mm, "construction": true});
            skLineSegment(sketch, "E28.18.8.0", {"start": v(41.07, -21.45) * mm, "end": v(41.32, -18.95) * mm});
            skLineSegment(sketch, "E28.21.8.0", {"start": v(41.57, -24) * mm, "end": v(46.2, -26.67) * mm, "construction": true});
            skPoint(sketch, "E28.24.8.0", {"position": v(44.03, -24.84) * mm});
            skPoint(sketch, "E28.25.8.0", {"position": v(39.11, -24.84) * mm});
            skPoint(sketch, "E28.26.8.0", {"position": v(41.57, -24) * mm});
            skLineSegment(sketch, "E28.27.8.0", {"start": v(41.57, -24) * mm, "end": v(37.17, -26.54) * mm, "construction": true});
            skArc(sketch, "E28.30.8.0", {"start": v(43.53, -25.7) * mm, "mid": v(44.17, -25.5) * mm, "end": v(44.03, -24.84) * mm});
            skPoint(sketch, "E28.34.8.0", {"position": v(39.6, -25.7) * mm});
            skLineSegment(sketch, "E28.35.8.0", {"start": v(39.6, -25.7) * mm, "end": v(37.32, -26.74) * mm});
            skLineSegment(sketch, "E28.38.8.0", {"start": v(39.11, -24.84) * mm, "end": v(37.07, -26.31) * mm});
            skPoint(sketch, "E28.41.8.0", {"position": v(43.53, -25.7) * mm});
            skLineSegment(sketch, "E28.42.8.0", {"start": v(42.07, -21.45) * mm, "end": v(41.82, -18.95) * mm});
            skLineSegment(sketch, "E28.45.8.0", {"start": v(43.53, -25.7) * mm, "end": v(45.82, -26.74) * mm});
            skArc(sketch, "E28.48.8.0", {"start": v(42.07, -21.45) * mm, "mid": v(41.57, -21) * mm, "end": v(41.07, -21.45) * mm});
            skPoint(sketch, "E28.52.8.0", {"position": v(43.53, -25.7) * mm});
            skPoint(sketch, "E28.53.8.0", {"position": v(42.07, -21.45) * mm});
            skPoint(sketch, "E28.54.8.0", {"position": v(39.11, -24.84) * mm});
            skArc(sketch, "E28.55.8.0", {"start": v(37.07, -26.31) * mm, "mid": v(37.17, -26.54) * mm, "end": v(37.32, -26.74) * mm});
            skArc(sketch, "E28.59.8.0", {"start": v(45.82, -26.74) * mm, "mid": v(45.97, -26.54) * mm, "end": v(46.07, -26.31) * mm});
            skArc(sketch, "E28.63.8.0", {"start": v(41.82, -18.95) * mm, "mid": v(41.57, -18.92) * mm, "end": v(41.32, -18.95) * mm});
            skLineSegment(sketch, "E28.67.8.0", {"start": v(41.57, -24) * mm, "end": v(41.57, -18.66) * mm, "construction": true});
            skPoint(sketch, "E28.0.8.1", {"position": v(41.07, -15.45) * mm});
            skLineSegment(sketch, "E28.1.8.1", {"start": v(41.57, -18) * mm, "end": v(36.94, -20.67) * mm, "construction": true});
            skLineSegment(sketch, "E28.4.8.1", {"start": v(44.03, -18.84) * mm, "end": v(46.07, -20.31) * mm});
            skPoint(sketch, "E28.7.8.1", {"position": v(42.07, -15.45) * mm});
            skArc(sketch, "E28.8.8.1", {"start": v(39.11, -18.84) * mm, "mid": v(38.97, -19.5) * mm, "end": v(39.6, -19.7) * mm});
            skLineSegment(sketch, "E28.12.8.1", {"start": v(41.57, -18) * mm, "end": v(41.57, -12.92) * mm, "construction": true});
            skLineSegment(sketch, "E28.15.8.1", {"start": v(41.57, -18) * mm, "end": v(45.97, -20.54) * mm, "construction": true});
            skLineSegment(sketch, "E28.18.8.1", {"start": v(41.07, -15.45) * mm, "end": v(41.32, -12.95) * mm});
            skLineSegment(sketch, "E28.21.8.1", {"start": v(41.57, -18) * mm, "end": v(46.2, -20.67) * mm, "construction": true});
            skPoint(sketch, "E28.24.8.1", {"position": v(44.03, -18.84) * mm});
            skPoint(sketch, "E28.25.8.1", {"position": v(39.11, -18.84) * mm});
            skPoint(sketch, "E28.26.8.1", {"position": v(41.57, -18) * mm});
            skLineSegment(sketch, "E28.27.8.1", {"start": v(41.57, -18) * mm, "end": v(37.17, -20.54) * mm, "construction": true});
            skArc(sketch, "E28.30.8.1", {"start": v(43.53, -19.7) * mm, "mid": v(44.17, -19.5) * mm, "end": v(44.03, -18.84) * mm});
            skPoint(sketch, "E28.34.8.1", {"position": v(39.6, -19.7) * mm});
            skLineSegment(sketch, "E28.35.8.1", {"start": v(39.6, -19.7) * mm, "end": v(37.32, -20.74) * mm});
            skLineSegment(sketch, "E28.38.8.1", {"start": v(39.11, -18.84) * mm, "end": v(37.07, -20.31) * mm});
            skPoint(sketch, "E28.41.8.1", {"position": v(43.53, -19.7) * mm});
            skLineSegment(sketch, "E28.42.8.1", {"start": v(42.07, -15.45) * mm, "end": v(41.82, -12.95) * mm});
            skLineSegment(sketch, "E28.45.8.1", {"start": v(43.53, -19.7) * mm, "end": v(45.82, -20.74) * mm});
            skArc(sketch, "E28.48.8.1", {"start": v(42.07, -15.45) * mm, "mid": v(41.57, -15) * mm, "end": v(41.07, -15.45) * mm});
            skPoint(sketch, "E28.52.8.1", {"position": v(43.53, -19.7) * mm});
            skPoint(sketch, "E28.53.8.1", {"position": v(42.07, -15.45) * mm});
            skPoint(sketch, "E28.54.8.1", {"position": v(39.11, -18.84) * mm});
            skArc(sketch, "E28.55.8.1", {"start": v(37.07, -20.31) * mm, "mid": v(37.17, -20.54) * mm, "end": v(37.32, -20.74) * mm});
            skArc(sketch, "E28.59.8.1", {"start": v(45.82, -20.74) * mm, "mid": v(45.97, -20.54) * mm, "end": v(46.07, -20.31) * mm});
            skArc(sketch, "E28.63.8.1", {"start": v(41.82, -12.95) * mm, "mid": v(41.57, -12.92) * mm, "end": v(41.32, -12.95) * mm});
            skLineSegment(sketch, "E28.67.8.1", {"start": v(41.57, -18) * mm, "end": v(41.57, -12.66) * mm, "construction": true});
            skPoint(sketch, "E28.0.9.0", {"position": v(46.27, -24.45) * mm});
            skLineSegment(sketch, "E28.1.9.0", {"start": v(46.77, -27) * mm, "end": v(42.14, -29.67) * mm, "construction": true});
            skLineSegment(sketch, "E28.4.9.0", {"start": v(49.22, -27.84) * mm, "end": v(51.26, -29.31) * mm});
            skPoint(sketch, "E28.7.9.0", {"position": v(47.26, -24.45) * mm});
            skArc(sketch, "E28.8.9.0", {"start": v(44.3, -27.84) * mm, "mid": v(44.17, -28.5) * mm, "end": v(44.8, -28.7) * mm});
            skLineSegment(sketch, "E28.12.9.0", {"start": v(46.77, -27) * mm, "end": v(46.77, -21.92) * mm, "construction": true});
            skLineSegment(sketch, "E28.15.9.0", {"start": v(46.77, -27) * mm, "end": v(51.17, -29.54) * mm, "construction": true});
            skLineSegment(sketch, "E28.18.9.0", {"start": v(46.27, -24.45) * mm, "end": v(46.52, -21.95) * mm});
            skLineSegment(sketch, "E28.21.9.0", {"start": v(46.77, -27) * mm, "end": v(51.4, -29.67) * mm, "construction": true});
            skPoint(sketch, "E28.24.9.0", {"position": v(49.22, -27.84) * mm});
            skPoint(sketch, "E28.25.9.0", {"position": v(44.3, -27.84) * mm});
            skPoint(sketch, "E28.26.9.0", {"position": v(46.77, -27) * mm});
            skLineSegment(sketch, "E28.27.9.0", {"start": v(46.77, -27) * mm, "end": v(42.37, -29.54) * mm, "construction": true});
            skArc(sketch, "E28.30.9.0", {"start": v(48.72, -28.7) * mm, "mid": v(49.36, -28.5) * mm, "end": v(49.22, -27.84) * mm});
            skPoint(sketch, "E28.34.9.0", {"position": v(44.8, -28.7) * mm});
            skLineSegment(sketch, "E28.35.9.0", {"start": v(44.8, -28.7) * mm, "end": v(42.52, -29.74) * mm});
            skLineSegment(sketch, "E28.38.9.0", {"start": v(44.3, -27.84) * mm, "end": v(42.27, -29.31) * mm});
            skPoint(sketch, "E28.41.9.0", {"position": v(48.72, -28.7) * mm});
            skLineSegment(sketch, "E28.42.9.0", {"start": v(47.26, -24.45) * mm, "end": v(47.01, -21.95) * mm});
            skLineSegment(sketch, "E28.45.9.0", {"start": v(48.72, -28.7) * mm, "end": v(51.02, -29.74) * mm});
            skArc(sketch, "E28.48.9.0", {"start": v(47.26, -24.45) * mm, "mid": v(46.77, -24) * mm, "end": v(46.27, -24.45) * mm});
            skPoint(sketch, "E28.52.9.0", {"position": v(48.72, -28.7) * mm});
            skPoint(sketch, "E28.53.9.0", {"position": v(47.26, -24.45) * mm});
            skPoint(sketch, "E28.54.9.0", {"position": v(44.3, -27.84) * mm});
            skArc(sketch, "E28.55.9.0", {"start": v(42.27, -29.31) * mm, "mid": v(42.37, -29.54) * mm, "end": v(42.52, -29.74) * mm});
            skArc(sketch, "E28.59.9.0", {"start": v(51.02, -29.74) * mm, "mid": v(51.17, -29.54) * mm, "end": v(51.26, -29.31) * mm});
            skArc(sketch, "E28.63.9.0", {"start": v(47.01, -21.95) * mm, "mid": v(46.77, -21.92) * mm, "end": v(46.52, -21.95) * mm});
            skLineSegment(sketch, "E28.67.9.0", {"start": v(46.77, -27) * mm, "end": v(46.77, -21.66) * mm, "construction": true});
            skPoint(sketch, "E28.0.9.1", {"position": v(46.27, -18.45) * mm});
            skLineSegment(sketch, "E28.1.9.1", {"start": v(46.77, -21) * mm, "end": v(42.14, -23.67) * mm, "construction": true});
            skLineSegment(sketch, "E28.4.9.1", {"start": v(49.22, -21.84) * mm, "end": v(51.26, -23.31) * mm});
            skPoint(sketch, "E28.7.9.1", {"position": v(47.26, -18.45) * mm});
            skArc(sketch, "E28.8.9.1", {"start": v(44.3, -21.84) * mm, "mid": v(44.17, -22.5) * mm, "end": v(44.8, -22.7) * mm});
            skLineSegment(sketch, "E28.12.9.1", {"start": v(46.77, -21) * mm, "end": v(46.77, -15.92) * mm, "construction": true});
            skLineSegment(sketch, "E28.15.9.1", {"start": v(46.77, -21) * mm, "end": v(51.17, -23.54) * mm, "construction": true});
            skLineSegment(sketch, "E28.18.9.1", {"start": v(46.27, -18.45) * mm, "end": v(46.52, -15.95) * mm});
            skLineSegment(sketch, "E28.21.9.1", {"start": v(46.77, -21) * mm, "end": v(51.4, -23.67) * mm, "construction": true});
            skPoint(sketch, "E28.24.9.1", {"position": v(49.22, -21.84) * mm});
            skPoint(sketch, "E28.25.9.1", {"position": v(44.3, -21.84) * mm});
            skPoint(sketch, "E28.26.9.1", {"position": v(46.77, -21) * mm});
            skLineSegment(sketch, "E28.27.9.1", {"start": v(46.77, -21) * mm, "end": v(42.37, -23.54) * mm, "construction": true});
            skArc(sketch, "E28.30.9.1", {"start": v(48.72, -22.7) * mm, "mid": v(49.36, -22.5) * mm, "end": v(49.22, -21.84) * mm});
            skPoint(sketch, "E28.34.9.1", {"position": v(44.8, -22.7) * mm});
            skLineSegment(sketch, "E28.35.9.1", {"start": v(44.8, -22.7) * mm, "end": v(42.52, -23.74) * mm});
            skLineSegment(sketch, "E28.38.9.1", {"start": v(44.3, -21.84) * mm, "end": v(42.27, -23.31) * mm});
            skPoint(sketch, "E28.41.9.1", {"position": v(48.72, -22.7) * mm});
            skLineSegment(sketch, "E28.42.9.1", {"start": v(47.26, -18.45) * mm, "end": v(47.01, -15.95) * mm});
            skLineSegment(sketch, "E28.45.9.1", {"start": v(48.72, -22.7) * mm, "end": v(51.02, -23.74) * mm});
            skArc(sketch, "E28.48.9.1", {"start": v(47.26, -18.45) * mm, "mid": v(46.77, -18) * mm, "end": v(46.27, -18.45) * mm});
            skPoint(sketch, "E28.52.9.1", {"position": v(48.72, -22.7) * mm});
            skPoint(sketch, "E28.53.9.1", {"position": v(47.26, -18.45) * mm});
            skPoint(sketch, "E28.54.9.1", {"position": v(44.3, -21.84) * mm});
            skArc(sketch, "E28.55.9.1", {"start": v(42.27, -23.31) * mm, "mid": v(42.37, -23.54) * mm, "end": v(42.52, -23.74) * mm});
            skArc(sketch, "E28.59.9.1", {"start": v(51.02, -23.74) * mm, "mid": v(51.17, -23.54) * mm, "end": v(51.26, -23.31) * mm});
            skArc(sketch, "E28.63.9.1", {"start": v(47.01, -15.95) * mm, "mid": v(46.77, -15.92) * mm, "end": v(46.52, -15.95) * mm});
            skLineSegment(sketch, "E28.67.9.1", {"start": v(46.77, -21) * mm, "end": v(46.77, -15.66) * mm, "construction": true});
            skPoint(sketch, "E29.0.0.2", {"position": v(-0.5, 14.55) * mm});
            skLineSegment(sketch, "E29.1.0.2", {"start": v(0, 12) * mm, "end": v(-4.63, 9.33) * mm, "construction": true});
            skLineSegment(sketch, "E29.4.0.2", {"start": v(2.46, 11.16) * mm, "end": v(4.5, 9.69) * mm});
            skPoint(sketch, "E29.7.0.2", {"position": v(0.5, 14.55) * mm});
            skArc(sketch, "E29.8.0.2", {"start": v(-2.46, 11.16) * mm, "mid": v(-2.6, 10.5) * mm, "end": v(-1.96, 10.3) * mm});
            skLineSegment(sketch, "E29.12.0.2", {"start": v(0, 12) * mm, "end": v(0, 17.08) * mm, "construction": true});
            skLineSegment(sketch, "E29.15.0.2", {"start": v(0, 12) * mm, "end": v(4.4, 9.46) * mm, "construction": true});
            skLineSegment(sketch, "E29.18.0.2", {"start": v(-0.5, 14.55) * mm, "end": v(-0.25, 17.05) * mm});
            skLineSegment(sketch, "E29.21.0.2", {"start": v(0, 12) * mm, "end": v(4.63, 9.33) * mm, "construction": true});
            skPoint(sketch, "E29.24.0.2", {"position": v(2.46, 11.16) * mm});
            skPoint(sketch, "E29.25.0.2", {"position": v(-2.46, 11.16) * mm});
            skPoint(sketch, "E29.26.0.2", {"position": v(0, 12) * mm});
            skLineSegment(sketch, "E29.27.0.2", {"start": v(0, 12) * mm, "end": v(-4.4, 9.46) * mm, "construction": true});
            skArc(sketch, "E29.30.0.2", {"start": v(1.96, 10.3) * mm, "mid": v(2.6, 10.5) * mm, "end": v(2.46, 11.16) * mm});
            skPoint(sketch, "E29.34.0.2", {"position": v(-1.96, 10.3) * mm});
            skLineSegment(sketch, "E29.35.0.2", {"start": v(-1.96, 10.3) * mm, "end": v(-4.25, 9.26) * mm});
            skLineSegment(sketch, "E29.38.0.2", {"start": v(-2.46, 11.16) * mm, "end": v(-4.5, 9.69) * mm});
            skPoint(sketch, "E29.41.0.2", {"position": v(1.96, 10.3) * mm});
            skLineSegment(sketch, "E29.42.0.2", {"start": v(0.5, 14.55) * mm, "end": v(0.25, 17.05) * mm});
            skLineSegment(sketch, "E29.45.0.2", {"start": v(1.96, 10.3) * mm, "end": v(4.25, 9.26) * mm});
            skArc(sketch, "E29.48.0.2", {"start": v(0.5, 14.55) * mm, "mid": v(0, 15) * mm, "end": v(-0.5, 14.55) * mm});
            skPoint(sketch, "E29.52.0.2", {"position": v(1.96, 10.3) * mm});
            skPoint(sketch, "E29.53.0.2", {"position": v(0.5, 14.55) * mm});
            skPoint(sketch, "E29.54.0.2", {"position": v(-2.46, 11.16) * mm});
            skArc(sketch, "E29.55.0.2", {"start": v(-4.5, 9.69) * mm, "mid": v(-4.4, 9.46) * mm, "end": v(-4.25, 9.26) * mm});
            skArc(sketch, "E29.59.0.2", {"start": v(4.25, 9.26) * mm, "mid": v(4.4, 9.46) * mm, "end": v(4.5, 9.69) * mm});
            skArc(sketch, "E29.63.0.2", {"start": v(0.25, 17.05) * mm, "mid": v(0, 17.08) * mm, "end": v(-0.25, 17.05) * mm});
            skLineSegment(sketch, "E29.67.0.2", {"start": v(0, 12) * mm, "end": v(0, 17.34) * mm, "construction": true});
            skPoint(sketch, "E29.0.0.3", {"position": v(-0.5, 20.55) * mm});
            skLineSegment(sketch, "E29.1.0.3", {"start": v(0, 18) * mm, "end": v(-4.63, 15.33) * mm, "construction": true});
            skLineSegment(sketch, "E29.4.0.3", {"start": v(2.46, 17.16) * mm, "end": v(4.5, 15.69) * mm});
            skPoint(sketch, "E29.7.0.3", {"position": v(0.5, 20.55) * mm});
            skArc(sketch, "E29.8.0.3", {"start": v(-2.46, 17.16) * mm, "mid": v(-2.6, 16.5) * mm, "end": v(-1.96, 16.3) * mm});
            skLineSegment(sketch, "E29.12.0.3", {"start": v(0, 18) * mm, "end": v(0, 23.08) * mm, "construction": true});
            skLineSegment(sketch, "E29.15.0.3", {"start": v(0, 18) * mm, "end": v(4.4, 15.46) * mm, "construction": true});
            skLineSegment(sketch, "E29.18.0.3", {"start": v(-0.5, 20.55) * mm, "end": v(-0.25, 23.05) * mm});
            skLineSegment(sketch, "E29.21.0.3", {"start": v(0, 18) * mm, "end": v(4.63, 15.33) * mm, "construction": true});
            skPoint(sketch, "E29.24.0.3", {"position": v(2.46, 17.16) * mm});
            skPoint(sketch, "E29.25.0.3", {"position": v(-2.46, 17.16) * mm});
            skPoint(sketch, "E29.26.0.3", {"position": v(0, 18) * mm});
            skLineSegment(sketch, "E29.27.0.3", {"start": v(0, 18) * mm, "end": v(-4.4, 15.46) * mm, "construction": true});
            skArc(sketch, "E29.30.0.3", {"start": v(1.96, 16.3) * mm, "mid": v(2.6, 16.5) * mm, "end": v(2.46, 17.16) * mm});
            skPoint(sketch, "E29.34.0.3", {"position": v(-1.96, 16.3) * mm});
            skLineSegment(sketch, "E29.35.0.3", {"start": v(-1.96, 16.3) * mm, "end": v(-4.25, 15.26) * mm});
            skLineSegment(sketch, "E29.38.0.3", {"start": v(-2.46, 17.16) * mm, "end": v(-4.5, 15.69) * mm});
            skPoint(sketch, "E29.41.0.3", {"position": v(1.96, 16.3) * mm});
            skLineSegment(sketch, "E29.42.0.3", {"start": v(0.5, 20.55) * mm, "end": v(0.25, 23.05) * mm});
            skLineSegment(sketch, "E29.45.0.3", {"start": v(1.96, 16.3) * mm, "end": v(4.25, 15.26) * mm});
            skArc(sketch, "E29.48.0.3", {"start": v(0.5, 20.55) * mm, "mid": v(0, 21) * mm, "end": v(-0.5, 20.55) * mm});
            skPoint(sketch, "E29.52.0.3", {"position": v(1.96, 16.3) * mm});
            skPoint(sketch, "E29.53.0.3", {"position": v(0.5, 20.55) * mm});
            skPoint(sketch, "E29.54.0.3", {"position": v(-2.46, 17.16) * mm});
            skArc(sketch, "E29.55.0.3", {"start": v(-4.5, 15.69) * mm, "mid": v(-4.4, 15.46) * mm, "end": v(-4.25, 15.26) * mm});
            skArc(sketch, "E29.59.0.3", {"start": v(4.25, 15.26) * mm, "mid": v(4.4, 15.46) * mm, "end": v(4.5, 15.69) * mm});
            skArc(sketch, "E29.63.0.3", {"start": v(0.25, 23.05) * mm, "mid": v(0, 23.08) * mm, "end": v(-0.25, 23.05) * mm});
            skLineSegment(sketch, "E29.67.0.3", {"start": v(0, 18) * mm, "end": v(0, 23.34) * mm, "construction": true});
            skPoint(sketch, "E29.0.0.4", {"position": v(-0.5, 26.55) * mm});
            skLineSegment(sketch, "E29.1.0.4", {"start": v(0, 24) * mm, "end": v(-4.63, 21.33) * mm, "construction": true});
            skLineSegment(sketch, "E29.4.0.4", {"start": v(2.46, 23.16) * mm, "end": v(4.5, 21.69) * mm});
            skPoint(sketch, "E29.7.0.4", {"position": v(0.5, 26.55) * mm});
            skArc(sketch, "E29.8.0.4", {"start": v(-2.46, 23.16) * mm, "mid": v(-2.6, 22.5) * mm, "end": v(-1.96, 22.3) * mm});
            skLineSegment(sketch, "E29.12.0.4", {"start": v(0, 24) * mm, "end": v(0, 29.08) * mm, "construction": true});
            skLineSegment(sketch, "E29.15.0.4", {"start": v(0, 24) * mm, "end": v(4.4, 21.46) * mm, "construction": true});
            skLineSegment(sketch, "E29.18.0.4", {"start": v(-0.5, 26.55) * mm, "end": v(-0.25, 29.05) * mm});
            skLineSegment(sketch, "E29.21.0.4", {"start": v(0, 24) * mm, "end": v(4.63, 21.33) * mm, "construction": true});
            skPoint(sketch, "E29.24.0.4", {"position": v(2.46, 23.16) * mm});
            skPoint(sketch, "E29.25.0.4", {"position": v(-2.46, 23.16) * mm});
            skPoint(sketch, "E29.26.0.4", {"position": v(0, 24) * mm});
            skLineSegment(sketch, "E29.27.0.4", {"start": v(0, 24) * mm, "end": v(-4.4, 21.46) * mm, "construction": true});
            skArc(sketch, "E29.30.0.4", {"start": v(1.96, 22.3) * mm, "mid": v(2.6, 22.5) * mm, "end": v(2.46, 23.16) * mm});
            skPoint(sketch, "E29.34.0.4", {"position": v(-1.96, 22.3) * mm});
            skLineSegment(sketch, "E29.35.0.4", {"start": v(-1.96, 22.3) * mm, "end": v(-4.25, 21.26) * mm});
            skLineSegment(sketch, "E29.38.0.4", {"start": v(-2.46, 23.16) * mm, "end": v(-4.5, 21.69) * mm});
            skPoint(sketch, "E29.41.0.4", {"position": v(1.96, 22.3) * mm});
            skLineSegment(sketch, "E29.42.0.4", {"start": v(0.5, 26.55) * mm, "end": v(0.25, 29.05) * mm});
            skLineSegment(sketch, "E29.45.0.4", {"start": v(1.96, 22.3) * mm, "end": v(4.25, 21.26) * mm});
            skArc(sketch, "E29.48.0.4", {"start": v(0.5, 26.55) * mm, "mid": v(0, 27) * mm, "end": v(-0.5, 26.55) * mm});
            skPoint(sketch, "E29.52.0.4", {"position": v(1.96, 22.3) * mm});
            skPoint(sketch, "E29.53.0.4", {"position": v(0.5, 26.55) * mm});
            skPoint(sketch, "E29.54.0.4", {"position": v(-2.46, 23.16) * mm});
            skArc(sketch, "E29.55.0.4", {"start": v(-4.5, 21.69) * mm, "mid": v(-4.4, 21.46) * mm, "end": v(-4.25, 21.26) * mm});
            skArc(sketch, "E29.59.0.4", {"start": v(4.25, 21.26) * mm, "mid": v(4.4, 21.46) * mm, "end": v(4.5, 21.69) * mm});
            skArc(sketch, "E29.63.0.4", {"start": v(0.25, 29.05) * mm, "mid": v(0, 29.08) * mm, "end": v(-0.25, 29.05) * mm});
            skLineSegment(sketch, "E29.67.0.4", {"start": v(0, 24) * mm, "end": v(0, 29.34) * mm, "construction": true});
            skPoint(sketch, "E29.0.0.5", {"position": v(-0.5, 32.55) * mm});
            skLineSegment(sketch, "E29.1.0.5", {"start": v(0, 30) * mm, "end": v(-4.63, 27.33) * mm, "construction": true});
            skLineSegment(sketch, "E29.4.0.5", {"start": v(2.46, 29.16) * mm, "end": v(4.5, 27.69) * mm});
            skPoint(sketch, "E29.7.0.5", {"position": v(0.5, 32.55) * mm});
            skArc(sketch, "E29.8.0.5", {"start": v(-2.46, 29.16) * mm, "mid": v(-2.6, 28.5) * mm, "end": v(-1.96, 28.3) * mm});
            skLineSegment(sketch, "E29.12.0.5", {"start": v(0, 30) * mm, "end": v(0, 35.08) * mm, "construction": true});
            skLineSegment(sketch, "E29.15.0.5", {"start": v(0, 30) * mm, "end": v(4.4, 27.46) * mm, "construction": true});
            skLineSegment(sketch, "E29.18.0.5", {"start": v(-0.5, 32.55) * mm, "end": v(-0.25, 35.05) * mm});
            skLineSegment(sketch, "E29.21.0.5", {"start": v(0, 30) * mm, "end": v(4.63, 27.33) * mm, "construction": true});
            skPoint(sketch, "E29.24.0.5", {"position": v(2.46, 29.16) * mm});
            skPoint(sketch, "E29.25.0.5", {"position": v(-2.46, 29.16) * mm});
            skPoint(sketch, "E29.26.0.5", {"position": v(0, 30) * mm});
            skLineSegment(sketch, "E29.27.0.5", {"start": v(0, 30) * mm, "end": v(-4.4, 27.46) * mm, "construction": true});
            skArc(sketch, "E29.30.0.5", {"start": v(1.96, 28.3) * mm, "mid": v(2.6, 28.5) * mm, "end": v(2.46, 29.16) * mm});
            skPoint(sketch, "E29.34.0.5", {"position": v(-1.96, 28.3) * mm});
            skLineSegment(sketch, "E29.35.0.5", {"start": v(-1.96, 28.3) * mm, "end": v(-4.25, 27.26) * mm});
            skLineSegment(sketch, "E29.38.0.5", {"start": v(-2.46, 29.16) * mm, "end": v(-4.5, 27.69) * mm});
            skPoint(sketch, "E29.41.0.5", {"position": v(1.96, 28.3) * mm});
            skLineSegment(sketch, "E29.42.0.5", {"start": v(0.5, 32.55) * mm, "end": v(0.25, 35.05) * mm});
            skLineSegment(sketch, "E29.45.0.5", {"start": v(1.96, 28.3) * mm, "end": v(4.25, 27.26) * mm});
            skArc(sketch, "E29.48.0.5", {"start": v(0.5, 32.55) * mm, "mid": v(0, 33) * mm, "end": v(-0.5, 32.55) * mm});
            skPoint(sketch, "E29.52.0.5", {"position": v(1.96, 28.3) * mm});
            skPoint(sketch, "E29.53.0.5", {"position": v(0.5, 32.55) * mm});
            skPoint(sketch, "E29.54.0.5", {"position": v(-2.46, 29.16) * mm});
            skArc(sketch, "E29.55.0.5", {"start": v(-4.5, 27.69) * mm, "mid": v(-4.4, 27.46) * mm, "end": v(-4.25, 27.26) * mm});
            skArc(sketch, "E29.59.0.5", {"start": v(4.25, 27.26) * mm, "mid": v(4.4, 27.46) * mm, "end": v(4.5, 27.69) * mm});
            skArc(sketch, "E29.63.0.5", {"start": v(0.25, 35.05) * mm, "mid": v(0, 35.08) * mm, "end": v(-0.25, 35.05) * mm});
            skLineSegment(sketch, "E29.67.0.5", {"start": v(0, 30) * mm, "end": v(0, 35.34) * mm, "construction": true});
            skPoint(sketch, "E29.0.0.6", {"position": v(-0.5, 38.55) * mm});
            skLineSegment(sketch, "E29.1.0.6", {"start": v(0, 36) * mm, "end": v(-4.63, 33.33) * mm, "construction": true});
            skLineSegment(sketch, "E29.4.0.6", {"start": v(2.46, 35.16) * mm, "end": v(4.5, 33.69) * mm});
            skPoint(sketch, "E29.7.0.6", {"position": v(0.5, 38.55) * mm});
            skArc(sketch, "E29.8.0.6", {"start": v(-2.46, 35.16) * mm, "mid": v(-2.6, 34.5) * mm, "end": v(-1.96, 34.3) * mm});
            skLineSegment(sketch, "E29.12.0.6", {"start": v(0, 36) * mm, "end": v(0, 41.08) * mm, "construction": true});
            skLineSegment(sketch, "E29.15.0.6", {"start": v(0, 36) * mm, "end": v(4.4, 33.46) * mm, "construction": true});
            skLineSegment(sketch, "E29.18.0.6", {"start": v(-0.5, 38.55) * mm, "end": v(-0.25, 41.05) * mm});
            skLineSegment(sketch, "E29.21.0.6", {"start": v(0, 36) * mm, "end": v(4.63, 33.33) * mm, "construction": true});
            skPoint(sketch, "E29.24.0.6", {"position": v(2.46, 35.16) * mm});
            skPoint(sketch, "E29.25.0.6", {"position": v(-2.46, 35.16) * mm});
            skPoint(sketch, "E29.26.0.6", {"position": v(0, 36) * mm});
            skLineSegment(sketch, "E29.27.0.6", {"start": v(0, 36) * mm, "end": v(-4.4, 33.46) * mm, "construction": true});
            skArc(sketch, "E29.30.0.6", {"start": v(1.96, 34.3) * mm, "mid": v(2.6, 34.5) * mm, "end": v(2.46, 35.16) * mm});
            skPoint(sketch, "E29.34.0.6", {"position": v(-1.96, 34.3) * mm});
            skLineSegment(sketch, "E29.35.0.6", {"start": v(-1.96, 34.3) * mm, "end": v(-4.25, 33.26) * mm});
            skLineSegment(sketch, "E29.38.0.6", {"start": v(-2.46, 35.16) * mm, "end": v(-4.5, 33.69) * mm});
            skPoint(sketch, "E29.41.0.6", {"position": v(1.96, 34.3) * mm});
            skLineSegment(sketch, "E29.42.0.6", {"start": v(0.5, 38.55) * mm, "end": v(0.25, 41.05) * mm});
            skLineSegment(sketch, "E29.45.0.6", {"start": v(1.96, 34.3) * mm, "end": v(4.25, 33.26) * mm});
            skArc(sketch, "E29.48.0.6", {"start": v(0.5, 38.55) * mm, "mid": v(0, 39) * mm, "end": v(-0.5, 38.55) * mm});
            skPoint(sketch, "E29.52.0.6", {"position": v(1.96, 34.3) * mm});
            skPoint(sketch, "E29.53.0.6", {"position": v(0.5, 38.55) * mm});
            skPoint(sketch, "E29.54.0.6", {"position": v(-2.46, 35.16) * mm});
            skArc(sketch, "E29.55.0.6", {"start": v(-4.5, 33.69) * mm, "mid": v(-4.4, 33.46) * mm, "end": v(-4.25, 33.26) * mm});
            skArc(sketch, "E29.59.0.6", {"start": v(4.25, 33.26) * mm, "mid": v(4.4, 33.46) * mm, "end": v(4.5, 33.69) * mm});
            skArc(sketch, "E29.63.0.6", {"start": v(0.25, 41.05) * mm, "mid": v(0, 41.08) * mm, "end": v(-0.25, 41.05) * mm});
            skLineSegment(sketch, "E29.67.0.6", {"start": v(0, 36) * mm, "end": v(0, 41.34) * mm, "construction": true});
            skPoint(sketch, "E29.0.0.7", {"position": v(-0.5, 44.55) * mm});
            skLineSegment(sketch, "E29.1.0.7", {"start": v(0, 42) * mm, "end": v(-4.63, 39.33) * mm, "construction": true});
            skLineSegment(sketch, "E29.4.0.7", {"start": v(2.46, 41.16) * mm, "end": v(4.5, 39.69) * mm});
            skPoint(sketch, "E29.7.0.7", {"position": v(0.5, 44.55) * mm});
            skArc(sketch, "E29.8.0.7", {"start": v(-2.46, 41.16) * mm, "mid": v(-2.6, 40.5) * mm, "end": v(-1.96, 40.3) * mm});
            skLineSegment(sketch, "E29.12.0.7", {"start": v(0, 42) * mm, "end": v(0, 47.08) * mm, "construction": true});
            skLineSegment(sketch, "E29.15.0.7", {"start": v(0, 42) * mm, "end": v(4.4, 39.46) * mm, "construction": true});
            skLineSegment(sketch, "E29.18.0.7", {"start": v(-0.5, 44.55) * mm, "end": v(-0.25, 47.05) * mm});
            skLineSegment(sketch, "E29.21.0.7", {"start": v(0, 42) * mm, "end": v(4.63, 39.33) * mm, "construction": true});
            skPoint(sketch, "E29.24.0.7", {"position": v(2.46, 41.16) * mm});
            skPoint(sketch, "E29.25.0.7", {"position": v(-2.46, 41.16) * mm});
            skPoint(sketch, "E29.26.0.7", {"position": v(0, 42) * mm});
            skLineSegment(sketch, "E29.27.0.7", {"start": v(0, 42) * mm, "end": v(-4.4, 39.46) * mm, "construction": true});
            skArc(sketch, "E29.30.0.7", {"start": v(1.96, 40.3) * mm, "mid": v(2.6, 40.5) * mm, "end": v(2.46, 41.16) * mm});
            skPoint(sketch, "E29.34.0.7", {"position": v(-1.96, 40.3) * mm});
            skLineSegment(sketch, "E29.35.0.7", {"start": v(-1.96, 40.3) * mm, "end": v(-4.25, 39.26) * mm});
            skLineSegment(sketch, "E29.38.0.7", {"start": v(-2.46, 41.16) * mm, "end": v(-4.5, 39.69) * mm});
            skPoint(sketch, "E29.41.0.7", {"position": v(1.96, 40.3) * mm});
            skLineSegment(sketch, "E29.42.0.7", {"start": v(0.5, 44.55) * mm, "end": v(0.25, 47.05) * mm});
            skLineSegment(sketch, "E29.45.0.7", {"start": v(1.96, 40.3) * mm, "end": v(4.25, 39.26) * mm});
            skArc(sketch, "E29.48.0.7", {"start": v(0.5, 44.55) * mm, "mid": v(0, 45) * mm, "end": v(-0.5, 44.55) * mm});
            skPoint(sketch, "E29.52.0.7", {"position": v(1.96, 40.3) * mm});
            skPoint(sketch, "E29.53.0.7", {"position": v(0.5, 44.55) * mm});
            skPoint(sketch, "E29.54.0.7", {"position": v(-2.46, 41.16) * mm});
            skArc(sketch, "E29.55.0.7", {"start": v(-4.5, 39.69) * mm, "mid": v(-4.4, 39.46) * mm, "end": v(-4.25, 39.26) * mm});
            skArc(sketch, "E29.59.0.7", {"start": v(4.25, 39.26) * mm, "mid": v(4.4, 39.46) * mm, "end": v(4.5, 39.69) * mm});
            skArc(sketch, "E29.63.0.7", {"start": v(0.25, 47.05) * mm, "mid": v(0, 47.08) * mm, "end": v(-0.25, 47.05) * mm});
            skLineSegment(sketch, "E29.67.0.7", {"start": v(0, 42) * mm, "end": v(0, 47.34) * mm, "construction": true});
            skPoint(sketch, "E29.0.1.2", {"position": v(4.7, 11.55) * mm});
            skLineSegment(sketch, "E29.1.1.2", {"start": v(5.2, 9) * mm, "end": v(0.57, 6.33) * mm, "construction": true});
            skLineSegment(sketch, "E29.4.1.2", {"start": v(7.65, 8.16) * mm, "end": v(9.7, 6.69) * mm});
            skPoint(sketch, "E29.7.1.2", {"position": v(5.7, 11.55) * mm});
            skArc(sketch, "E29.8.1.2", {"start": v(2.74, 8.16) * mm, "mid": v(2.6, 7.5) * mm, "end": v(3.24, 7.3) * mm});
            skLineSegment(sketch, "E29.12.1.2", {"start": v(5.2, 9) * mm, "end": v(5.2, 14.08) * mm, "construction": true});
            skLineSegment(sketch, "E29.15.1.2", {"start": v(5.2, 9) * mm, "end": v(9.6, 6.46) * mm, "construction": true});
            skLineSegment(sketch, "E29.18.1.2", {"start": v(4.7, 11.55) * mm, "end": v(4.95, 14.05) * mm});
            skLineSegment(sketch, "E29.21.1.2", {"start": v(5.2, 9) * mm, "end": v(9.82, 6.33) * mm, "construction": true});
            skPoint(sketch, "E29.24.1.2", {"position": v(7.65, 8.16) * mm});
            skPoint(sketch, "E29.25.1.2", {"position": v(2.74, 8.16) * mm});
            skPoint(sketch, "E29.26.1.2", {"position": v(5.2, 9) * mm});
            skLineSegment(sketch, "E29.27.1.2", {"start": v(5.2, 9) * mm, "end": v(0.8, 6.46) * mm, "construction": true});
            skArc(sketch, "E29.30.1.2", {"start": v(7.16, 7.3) * mm, "mid": v(7.8, 7.5) * mm, "end": v(7.65, 8.16) * mm});
            skPoint(sketch, "E29.34.1.2", {"position": v(3.24, 7.3) * mm});
            skLineSegment(sketch, "E29.35.1.2", {"start": v(3.24, 7.3) * mm, "end": v(0.95, 6.26) * mm});
            skLineSegment(sketch, "E29.38.1.2", {"start": v(2.74, 8.16) * mm, "end": v(0.7, 6.69) * mm});
            skPoint(sketch, "E29.41.1.2", {"position": v(7.16, 7.3) * mm});
            skLineSegment(sketch, "E29.42.1.2", {"start": v(5.7, 11.55) * mm, "end": v(5.44, 14.05) * mm});
            skLineSegment(sketch, "E29.45.1.2", {"start": v(7.16, 7.3) * mm, "end": v(9.45, 6.26) * mm});
            skArc(sketch, "E29.48.1.2", {"start": v(5.7, 11.55) * mm, "mid": v(5.2, 12) * mm, "end": v(4.7, 11.55) * mm});
            skPoint(sketch, "E29.52.1.2", {"position": v(7.16, 7.3) * mm});
            skPoint(sketch, "E29.53.1.2", {"position": v(5.7, 11.55) * mm});
            skPoint(sketch, "E29.54.1.2", {"position": v(2.74, 8.16) * mm});
            skArc(sketch, "E29.55.1.2", {"start": v(0.7, 6.69) * mm, "mid": v(0.8, 6.46) * mm, "end": v(0.95, 6.26) * mm});
            skArc(sketch, "E29.59.1.2", {"start": v(9.45, 6.26) * mm, "mid": v(9.6, 6.46) * mm, "end": v(9.7, 6.69) * mm});
            skArc(sketch, "E29.63.1.2", {"start": v(5.44, 14.05) * mm, "mid": v(5.2, 14.08) * mm, "end": v(4.95, 14.05) * mm});
            skLineSegment(sketch, "E29.67.1.2", {"start": v(5.2, 9) * mm, "end": v(5.2, 14.34) * mm, "construction": true});
            skPoint(sketch, "E29.0.1.3", {"position": v(4.7, 17.55) * mm});
            skLineSegment(sketch, "E29.1.1.3", {"start": v(5.2, 15) * mm, "end": v(0.57, 12.33) * mm, "construction": true});
            skLineSegment(sketch, "E29.4.1.3", {"start": v(7.65, 14.16) * mm, "end": v(9.7, 12.69) * mm});
            skPoint(sketch, "E29.7.1.3", {"position": v(5.7, 17.55) * mm});
            skArc(sketch, "E29.8.1.3", {"start": v(2.74, 14.16) * mm, "mid": v(2.6, 13.5) * mm, "end": v(3.24, 13.3) * mm});
            skLineSegment(sketch, "E29.12.1.3", {"start": v(5.2, 15) * mm, "end": v(5.2, 20.08) * mm, "construction": true});
            skLineSegment(sketch, "E29.15.1.3", {"start": v(5.2, 15) * mm, "end": v(9.6, 12.46) * mm, "construction": true});
            skLineSegment(sketch, "E29.18.1.3", {"start": v(4.7, 17.55) * mm, "end": v(4.95, 20.05) * mm});
            skLineSegment(sketch, "E29.21.1.3", {"start": v(5.2, 15) * mm, "end": v(9.82, 12.33) * mm, "construction": true});
            skPoint(sketch, "E29.24.1.3", {"position": v(7.65, 14.16) * mm});
            skPoint(sketch, "E29.25.1.3", {"position": v(2.74, 14.16) * mm});
            skPoint(sketch, "E29.26.1.3", {"position": v(5.2, 15) * mm});
            skLineSegment(sketch, "E29.27.1.3", {"start": v(5.2, 15) * mm, "end": v(0.8, 12.46) * mm, "construction": true});
            skArc(sketch, "E29.30.1.3", {"start": v(7.16, 13.3) * mm, "mid": v(7.8, 13.5) * mm, "end": v(7.65, 14.16) * mm});
            skPoint(sketch, "E29.34.1.3", {"position": v(3.24, 13.3) * mm});
            skLineSegment(sketch, "E29.35.1.3", {"start": v(3.24, 13.3) * mm, "end": v(0.95, 12.26) * mm});
            skLineSegment(sketch, "E29.38.1.3", {"start": v(2.74, 14.16) * mm, "end": v(0.7, 12.69) * mm});
            skPoint(sketch, "E29.41.1.3", {"position": v(7.16, 13.3) * mm});
            skLineSegment(sketch, "E29.42.1.3", {"start": v(5.7, 17.55) * mm, "end": v(5.44, 20.05) * mm});
            skLineSegment(sketch, "E29.45.1.3", {"start": v(7.16, 13.3) * mm, "end": v(9.45, 12.26) * mm});
            skArc(sketch, "E29.48.1.3", {"start": v(5.7, 17.55) * mm, "mid": v(5.2, 18) * mm, "end": v(4.7, 17.55) * mm});
            skPoint(sketch, "E29.52.1.3", {"position": v(7.16, 13.3) * mm});
            skPoint(sketch, "E29.53.1.3", {"position": v(5.7, 17.55) * mm});
            skPoint(sketch, "E29.54.1.3", {"position": v(2.74, 14.16) * mm});
            skArc(sketch, "E29.55.1.3", {"start": v(0.7, 12.69) * mm, "mid": v(0.8, 12.46) * mm, "end": v(0.95, 12.26) * mm});
            skArc(sketch, "E29.59.1.3", {"start": v(9.45, 12.26) * mm, "mid": v(9.6, 12.46) * mm, "end": v(9.7, 12.69) * mm});
            skArc(sketch, "E29.63.1.3", {"start": v(5.44, 20.05) * mm, "mid": v(5.2, 20.08) * mm, "end": v(4.95, 20.05) * mm});
            skLineSegment(sketch, "E29.67.1.3", {"start": v(5.2, 15) * mm, "end": v(5.2, 20.34) * mm, "construction": true});
            skPoint(sketch, "E29.0.1.4", {"position": v(4.7, 23.55) * mm});
            skLineSegment(sketch, "E29.1.1.4", {"start": v(5.2, 21) * mm, "end": v(0.57, 18.33) * mm, "construction": true});
            skLineSegment(sketch, "E29.4.1.4", {"start": v(7.65, 20.16) * mm, "end": v(9.7, 18.69) * mm});
            skPoint(sketch, "E29.7.1.4", {"position": v(5.7, 23.55) * mm});
            skArc(sketch, "E29.8.1.4", {"start": v(2.74, 20.16) * mm, "mid": v(2.6, 19.5) * mm, "end": v(3.24, 19.3) * mm});
            skLineSegment(sketch, "E29.12.1.4", {"start": v(5.2, 21) * mm, "end": v(5.2, 26.08) * mm, "construction": true});
            skLineSegment(sketch, "E29.15.1.4", {"start": v(5.2, 21) * mm, "end": v(9.6, 18.46) * mm, "construction": true});
            skLineSegment(sketch, "E29.18.1.4", {"start": v(4.7, 23.55) * mm, "end": v(4.95, 26.05) * mm});
            skLineSegment(sketch, "E29.21.1.4", {"start": v(5.2, 21) * mm, "end": v(9.82, 18.33) * mm, "construction": true});
            skPoint(sketch, "E29.24.1.4", {"position": v(7.65, 20.16) * mm});
            skPoint(sketch, "E29.25.1.4", {"position": v(2.74, 20.16) * mm});
            skPoint(sketch, "E29.26.1.4", {"position": v(5.2, 21) * mm});
            skLineSegment(sketch, "E29.27.1.4", {"start": v(5.2, 21) * mm, "end": v(0.8, 18.46) * mm, "construction": true});
            skArc(sketch, "E29.30.1.4", {"start": v(7.16, 19.3) * mm, "mid": v(7.8, 19.5) * mm, "end": v(7.65, 20.16) * mm});
            skPoint(sketch, "E29.34.1.4", {"position": v(3.24, 19.3) * mm});
            skLineSegment(sketch, "E29.35.1.4", {"start": v(3.24, 19.3) * mm, "end": v(0.95, 18.26) * mm});
            skLineSegment(sketch, "E29.38.1.4", {"start": v(2.74, 20.16) * mm, "end": v(0.7, 18.69) * mm});
            skPoint(sketch, "E29.41.1.4", {"position": v(7.16, 19.3) * mm});
            skLineSegment(sketch, "E29.42.1.4", {"start": v(5.7, 23.55) * mm, "end": v(5.44, 26.05) * mm});
            skLineSegment(sketch, "E29.45.1.4", {"start": v(7.16, 19.3) * mm, "end": v(9.45, 18.26) * mm});
            skArc(sketch, "E29.48.1.4", {"start": v(5.7, 23.55) * mm, "mid": v(5.2, 24) * mm, "end": v(4.7, 23.55) * mm});
            skPoint(sketch, "E29.52.1.4", {"position": v(7.16, 19.3) * mm});
            skPoint(sketch, "E29.53.1.4", {"position": v(5.7, 23.55) * mm});
            skPoint(sketch, "E29.54.1.4", {"position": v(2.74, 20.16) * mm});
            skArc(sketch, "E29.55.1.4", {"start": v(0.7, 18.69) * mm, "mid": v(0.8, 18.46) * mm, "end": v(0.95, 18.26) * mm});
            skArc(sketch, "E29.59.1.4", {"start": v(9.45, 18.26) * mm, "mid": v(9.6, 18.46) * mm, "end": v(9.7, 18.69) * mm});
            skArc(sketch, "E29.63.1.4", {"start": v(5.44, 26.05) * mm, "mid": v(5.2, 26.08) * mm, "end": v(4.95, 26.05) * mm});
            skLineSegment(sketch, "E29.67.1.4", {"start": v(5.2, 21) * mm, "end": v(5.2, 26.34) * mm, "construction": true});
            skPoint(sketch, "E29.0.1.5", {"position": v(4.7, 29.55) * mm});
            skLineSegment(sketch, "E29.1.1.5", {"start": v(5.2, 27) * mm, "end": v(0.57, 24.33) * mm, "construction": true});
            skLineSegment(sketch, "E29.4.1.5", {"start": v(7.65, 26.16) * mm, "end": v(9.7, 24.69) * mm});
            skPoint(sketch, "E29.7.1.5", {"position": v(5.7, 29.55) * mm});
            skArc(sketch, "E29.8.1.5", {"start": v(2.74, 26.16) * mm, "mid": v(2.6, 25.5) * mm, "end": v(3.24, 25.3) * mm});
            skLineSegment(sketch, "E29.12.1.5", {"start": v(5.2, 27) * mm, "end": v(5.2, 32.08) * mm, "construction": true});
            skLineSegment(sketch, "E29.15.1.5", {"start": v(5.2, 27) * mm, "end": v(9.6, 24.46) * mm, "construction": true});
            skLineSegment(sketch, "E29.18.1.5", {"start": v(4.7, 29.55) * mm, "end": v(4.95, 32.05) * mm});
            skLineSegment(sketch, "E29.21.1.5", {"start": v(5.2, 27) * mm, "end": v(9.82, 24.33) * mm, "construction": true});
            skPoint(sketch, "E29.24.1.5", {"position": v(7.65, 26.16) * mm});
            skPoint(sketch, "E29.25.1.5", {"position": v(2.74, 26.16) * mm});
            skPoint(sketch, "E29.26.1.5", {"position": v(5.2, 27) * mm});
            skLineSegment(sketch, "E29.27.1.5", {"start": v(5.2, 27) * mm, "end": v(0.8, 24.46) * mm, "construction": true});
            skArc(sketch, "E29.30.1.5", {"start": v(7.16, 25.3) * mm, "mid": v(7.8, 25.5) * mm, "end": v(7.65, 26.16) * mm});
            skPoint(sketch, "E29.34.1.5", {"position": v(3.24, 25.3) * mm});
            skLineSegment(sketch, "E29.35.1.5", {"start": v(3.24, 25.3) * mm, "end": v(0.95, 24.26) * mm});
            skLineSegment(sketch, "E29.38.1.5", {"start": v(2.74, 26.16) * mm, "end": v(0.7, 24.69) * mm});
            skPoint(sketch, "E29.41.1.5", {"position": v(7.16, 25.3) * mm});
            skLineSegment(sketch, "E29.42.1.5", {"start": v(5.7, 29.55) * mm, "end": v(5.44, 32.05) * mm});
            skLineSegment(sketch, "E29.45.1.5", {"start": v(7.16, 25.3) * mm, "end": v(9.45, 24.26) * mm});
            skArc(sketch, "E29.48.1.5", {"start": v(5.7, 29.55) * mm, "mid": v(5.2, 30) * mm, "end": v(4.7, 29.55) * mm});
            skPoint(sketch, "E29.52.1.5", {"position": v(7.16, 25.3) * mm});
            skPoint(sketch, "E29.53.1.5", {"position": v(5.7, 29.55) * mm});
            skPoint(sketch, "E29.54.1.5", {"position": v(2.74, 26.16) * mm});
            skArc(sketch, "E29.55.1.5", {"start": v(0.7, 24.69) * mm, "mid": v(0.8, 24.46) * mm, "end": v(0.95, 24.26) * mm});
            skArc(sketch, "E29.59.1.5", {"start": v(9.45, 24.26) * mm, "mid": v(9.6, 24.46) * mm, "end": v(9.7, 24.69) * mm});
            skArc(sketch, "E29.63.1.5", {"start": v(5.44, 32.05) * mm, "mid": v(5.2, 32.08) * mm, "end": v(4.95, 32.05) * mm});
            skLineSegment(sketch, "E29.67.1.5", {"start": v(5.2, 27) * mm, "end": v(5.2, 32.34) * mm, "construction": true});
            skPoint(sketch, "E29.0.1.6", {"position": v(4.7, 35.55) * mm});
            skLineSegment(sketch, "E29.1.1.6", {"start": v(5.2, 33) * mm, "end": v(0.57, 30.33) * mm, "construction": true});
            skLineSegment(sketch, "E29.4.1.6", {"start": v(7.65, 32.16) * mm, "end": v(9.7, 30.69) * mm});
            skPoint(sketch, "E29.7.1.6", {"position": v(5.7, 35.55) * mm});
            skArc(sketch, "E29.8.1.6", {"start": v(2.74, 32.16) * mm, "mid": v(2.6, 31.5) * mm, "end": v(3.24, 31.3) * mm});
            skLineSegment(sketch, "E29.12.1.6", {"start": v(5.2, 33) * mm, "end": v(5.2, 38.08) * mm, "construction": true});
            skLineSegment(sketch, "E29.15.1.6", {"start": v(5.2, 33) * mm, "end": v(9.6, 30.46) * mm, "construction": true});
            skLineSegment(sketch, "E29.18.1.6", {"start": v(4.7, 35.55) * mm, "end": v(4.95, 38.05) * mm});
            skLineSegment(sketch, "E29.21.1.6", {"start": v(5.2, 33) * mm, "end": v(9.82, 30.33) * mm, "construction": true});
            skPoint(sketch, "E29.24.1.6", {"position": v(7.65, 32.16) * mm});
            skPoint(sketch, "E29.25.1.6", {"position": v(2.74, 32.16) * mm});
            skPoint(sketch, "E29.26.1.6", {"position": v(5.2, 33) * mm});
            skLineSegment(sketch, "E29.27.1.6", {"start": v(5.2, 33) * mm, "end": v(0.8, 30.46) * mm, "construction": true});
            skArc(sketch, "E29.30.1.6", {"start": v(7.16, 31.3) * mm, "mid": v(7.8, 31.5) * mm, "end": v(7.65, 32.16) * mm});
            skPoint(sketch, "E29.34.1.6", {"position": v(3.24, 31.3) * mm});
            skLineSegment(sketch, "E29.35.1.6", {"start": v(3.24, 31.3) * mm, "end": v(0.95, 30.26) * mm});
            skLineSegment(sketch, "E29.38.1.6", {"start": v(2.74, 32.16) * mm, "end": v(0.7, 30.69) * mm});
            skPoint(sketch, "E29.41.1.6", {"position": v(7.16, 31.3) * mm});
            skLineSegment(sketch, "E29.42.1.6", {"start": v(5.7, 35.55) * mm, "end": v(5.44, 38.05) * mm});
            skLineSegment(sketch, "E29.45.1.6", {"start": v(7.16, 31.3) * mm, "end": v(9.45, 30.26) * mm});
            skArc(sketch, "E29.48.1.6", {"start": v(5.7, 35.55) * mm, "mid": v(5.2, 36) * mm, "end": v(4.7, 35.55) * mm});
            skPoint(sketch, "E29.52.1.6", {"position": v(7.16, 31.3) * mm});
            skPoint(sketch, "E29.53.1.6", {"position": v(5.7, 35.55) * mm});
            skPoint(sketch, "E29.54.1.6", {"position": v(2.74, 32.16) * mm});
            skArc(sketch, "E29.55.1.6", {"start": v(0.7, 30.69) * mm, "mid": v(0.8, 30.46) * mm, "end": v(0.95, 30.26) * mm});
            skArc(sketch, "E29.59.1.6", {"start": v(9.45, 30.26) * mm, "mid": v(9.6, 30.46) * mm, "end": v(9.7, 30.69) * mm});
            skArc(sketch, "E29.63.1.6", {"start": v(5.44, 38.05) * mm, "mid": v(5.2, 38.08) * mm, "end": v(4.95, 38.05) * mm});
            skLineSegment(sketch, "E29.67.1.6", {"start": v(5.2, 33) * mm, "end": v(5.2, 38.34) * mm, "construction": true});
            skPoint(sketch, "E29.0.1.7", {"position": v(4.7, 41.55) * mm});
            skLineSegment(sketch, "E29.1.1.7", {"start": v(5.2, 39) * mm, "end": v(0.57, 36.33) * mm, "construction": true});
            skLineSegment(sketch, "E29.4.1.7", {"start": v(7.65, 38.16) * mm, "end": v(9.7, 36.69) * mm});
            skPoint(sketch, "E29.7.1.7", {"position": v(5.7, 41.55) * mm});
            skArc(sketch, "E29.8.1.7", {"start": v(2.74, 38.16) * mm, "mid": v(2.6, 37.5) * mm, "end": v(3.24, 37.3) * mm});
            skLineSegment(sketch, "E29.12.1.7", {"start": v(5.2, 39) * mm, "end": v(5.2, 44.08) * mm, "construction": true});
            skLineSegment(sketch, "E29.15.1.7", {"start": v(5.2, 39) * mm, "end": v(9.6, 36.46) * mm, "construction": true});
            skLineSegment(sketch, "E29.18.1.7", {"start": v(4.7, 41.55) * mm, "end": v(4.95, 44.05) * mm});
            skLineSegment(sketch, "E29.21.1.7", {"start": v(5.2, 39) * mm, "end": v(9.82, 36.33) * mm, "construction": true});
            skPoint(sketch, "E29.24.1.7", {"position": v(7.65, 38.16) * mm});
            skPoint(sketch, "E29.25.1.7", {"position": v(2.74, 38.16) * mm});
            skPoint(sketch, "E29.26.1.7", {"position": v(5.2, 39) * mm});
            skLineSegment(sketch, "E29.27.1.7", {"start": v(5.2, 39) * mm, "end": v(0.8, 36.46) * mm, "construction": true});
            skArc(sketch, "E29.30.1.7", {"start": v(7.16, 37.3) * mm, "mid": v(7.8, 37.5) * mm, "end": v(7.65, 38.16) * mm});
            skPoint(sketch, "E29.34.1.7", {"position": v(3.24, 37.3) * mm});
            skLineSegment(sketch, "E29.35.1.7", {"start": v(3.24, 37.3) * mm, "end": v(0.95, 36.26) * mm});
            skLineSegment(sketch, "E29.38.1.7", {"start": v(2.74, 38.16) * mm, "end": v(0.7, 36.69) * mm});
            skPoint(sketch, "E29.41.1.7", {"position": v(7.16, 37.3) * mm});
            skLineSegment(sketch, "E29.42.1.7", {"start": v(5.7, 41.55) * mm, "end": v(5.44, 44.05) * mm});
            skLineSegment(sketch, "E29.45.1.7", {"start": v(7.16, 37.3) * mm, "end": v(9.45, 36.26) * mm});
            skArc(sketch, "E29.48.1.7", {"start": v(5.7, 41.55) * mm, "mid": v(5.2, 42) * mm, "end": v(4.7, 41.55) * mm});
            skPoint(sketch, "E29.52.1.7", {"position": v(7.16, 37.3) * mm});
            skPoint(sketch, "E29.53.1.7", {"position": v(5.7, 41.55) * mm});
            skPoint(sketch, "E29.54.1.7", {"position": v(2.74, 38.16) * mm});
            skArc(sketch, "E29.55.1.7", {"start": v(0.7, 36.69) * mm, "mid": v(0.8, 36.46) * mm, "end": v(0.95, 36.26) * mm});
            skArc(sketch, "E29.59.1.7", {"start": v(9.45, 36.26) * mm, "mid": v(9.6, 36.46) * mm, "end": v(9.7, 36.69) * mm});
            skArc(sketch, "E29.63.1.7", {"start": v(5.44, 44.05) * mm, "mid": v(5.2, 44.08) * mm, "end": v(4.95, 44.05) * mm});
            skLineSegment(sketch, "E29.67.1.7", {"start": v(5.2, 39) * mm, "end": v(5.2, 44.34) * mm, "construction": true});
            skPoint(sketch, "E29.0.2.2", {"position": v(9.9, 8.55) * mm});
            skLineSegment(sketch, "E29.1.2.2", {"start": v(10.4, 6) * mm, "end": v(5.77, 3.33) * mm, "construction": true});
            skLineSegment(sketch, "E29.4.2.2", {"start": v(12.85, 5.16) * mm, "end": v(14.89, 3.69) * mm});
            skPoint(sketch, "E29.7.2.2", {"position": v(10.89, 8.55) * mm});
            skArc(sketch, "E29.8.2.2", {"start": v(7.94, 5.16) * mm, "mid": v(7.8, 4.5) * mm, "end": v(8.43, 4.3) * mm});
            skLineSegment(sketch, "E29.12.2.2", {"start": v(10.4, 6) * mm, "end": v(10.4, 11.08) * mm, "construction": true});
            skLineSegment(sketch, "E29.15.2.2", {"start": v(10.4, 6) * mm, "end": v(14.8, 3.46) * mm, "construction": true});
            skLineSegment(sketch, "E29.18.2.2", {"start": v(9.9, 8.55) * mm, "end": v(10.15, 11.05) * mm});
            skLineSegment(sketch, "E29.21.2.2", {"start": v(10.4, 6) * mm, "end": v(15.02, 3.33) * mm, "construction": true});
            skPoint(sketch, "E29.24.2.2", {"position": v(12.85, 5.16) * mm});
            skPoint(sketch, "E29.25.2.2", {"position": v(7.94, 5.16) * mm});
            skPoint(sketch, "E29.26.2.2", {"position": v(10.4, 6) * mm});
            skLineSegment(sketch, "E29.27.2.2", {"start": v(10.4, 6) * mm, "end": v(6, 3.46) * mm, "construction": true});
            skArc(sketch, "E29.30.2.2", {"start": v(12.35, 4.3) * mm, "mid": v(13, 4.5) * mm, "end": v(12.85, 5.16) * mm});
            skPoint(sketch, "E29.34.2.2", {"position": v(8.43, 4.3) * mm});
            skLineSegment(sketch, "E29.35.2.2", {"start": v(8.43, 4.3) * mm, "end": v(6.14, 3.26) * mm});
            skLineSegment(sketch, "E29.38.2.2", {"start": v(7.94, 5.16) * mm, "end": v(5.9, 3.69) * mm});
            skPoint(sketch, "E29.41.2.2", {"position": v(12.35, 4.3) * mm});
            skLineSegment(sketch, "E29.42.2.2", {"start": v(10.89, 8.55) * mm, "end": v(10.64, 11.05) * mm});
            skLineSegment(sketch, "E29.45.2.2", {"start": v(12.35, 4.3) * mm, "end": v(14.64, 3.26) * mm});
            skArc(sketch, "E29.48.2.2", {"start": v(10.89, 8.55) * mm, "mid": v(10.4, 9) * mm, "end": v(9.9, 8.55) * mm});
            skPoint(sketch, "E29.52.2.2", {"position": v(12.35, 4.3) * mm});
            skPoint(sketch, "E29.53.2.2", {"position": v(10.89, 8.55) * mm});
            skPoint(sketch, "E29.54.2.2", {"position": v(7.94, 5.16) * mm});
            skArc(sketch, "E29.55.2.2", {"start": v(5.9, 3.69) * mm, "mid": v(6, 3.46) * mm, "end": v(6.14, 3.26) * mm});
            skArc(sketch, "E29.59.2.2", {"start": v(14.64, 3.26) * mm, "mid": v(14.8, 3.46) * mm, "end": v(14.89, 3.69) * mm});
            skArc(sketch, "E29.63.2.2", {"start": v(10.64, 11.05) * mm, "mid": v(10.4, 11.08) * mm, "end": v(10.15, 11.05) * mm});
            skLineSegment(sketch, "E29.67.2.2", {"start": v(10.4, 6) * mm, "end": v(10.4, 11.34) * mm, "construction": true});
            skPoint(sketch, "E29.0.2.3", {"position": v(9.9, 14.55) * mm});
            skLineSegment(sketch, "E29.1.2.3", {"start": v(10.4, 12) * mm, "end": v(5.77, 9.33) * mm, "construction": true});
            skLineSegment(sketch, "E29.4.2.3", {"start": v(12.85, 11.16) * mm, "end": v(14.89, 9.69) * mm});
            skPoint(sketch, "E29.7.2.3", {"position": v(10.89, 14.55) * mm});
            skArc(sketch, "E29.8.2.3", {"start": v(7.94, 11.16) * mm, "mid": v(7.8, 10.5) * mm, "end": v(8.43, 10.3) * mm});
            skLineSegment(sketch, "E29.12.2.3", {"start": v(10.4, 12) * mm, "end": v(10.4, 17.08) * mm, "construction": true});
            skLineSegment(sketch, "E29.15.2.3", {"start": v(10.4, 12) * mm, "end": v(14.8, 9.46) * mm, "construction": true});
            skLineSegment(sketch, "E29.18.2.3", {"start": v(9.9, 14.55) * mm, "end": v(10.15, 17.05) * mm});
            skLineSegment(sketch, "E29.21.2.3", {"start": v(10.4, 12) * mm, "end": v(15.02, 9.33) * mm, "construction": true});
            skPoint(sketch, "E29.24.2.3", {"position": v(12.85, 11.16) * mm});
            skPoint(sketch, "E29.25.2.3", {"position": v(7.94, 11.16) * mm});
            skPoint(sketch, "E29.26.2.3", {"position": v(10.4, 12) * mm});
            skLineSegment(sketch, "E29.27.2.3", {"start": v(10.4, 12) * mm, "end": v(6, 9.46) * mm, "construction": true});
            skArc(sketch, "E29.30.2.3", {"start": v(12.35, 10.3) * mm, "mid": v(13, 10.5) * mm, "end": v(12.85, 11.16) * mm});
            skPoint(sketch, "E29.34.2.3", {"position": v(8.43, 10.3) * mm});
            skLineSegment(sketch, "E29.35.2.3", {"start": v(8.43, 10.3) * mm, "end": v(6.14, 9.26) * mm});
            skLineSegment(sketch, "E29.38.2.3", {"start": v(7.94, 11.16) * mm, "end": v(5.9, 9.69) * mm});
            skPoint(sketch, "E29.41.2.3", {"position": v(12.35, 10.3) * mm});
            skLineSegment(sketch, "E29.42.2.3", {"start": v(10.89, 14.55) * mm, "end": v(10.64, 17.05) * mm});
            skLineSegment(sketch, "E29.45.2.3", {"start": v(12.35, 10.3) * mm, "end": v(14.64, 9.26) * mm});
            skArc(sketch, "E29.48.2.3", {"start": v(10.89, 14.55) * mm, "mid": v(10.4, 15) * mm, "end": v(9.9, 14.55) * mm});
            skPoint(sketch, "E29.52.2.3", {"position": v(12.35, 10.3) * mm});
            skPoint(sketch, "E29.53.2.3", {"position": v(10.89, 14.55) * mm});
            skPoint(sketch, "E29.54.2.3", {"position": v(7.94, 11.16) * mm});
            skArc(sketch, "E29.55.2.3", {"start": v(5.9, 9.69) * mm, "mid": v(6, 9.46) * mm, "end": v(6.14, 9.26) * mm});
            skArc(sketch, "E29.59.2.3", {"start": v(14.64, 9.26) * mm, "mid": v(14.8, 9.46) * mm, "end": v(14.89, 9.69) * mm});
            skArc(sketch, "E29.63.2.3", {"start": v(10.64, 17.05) * mm, "mid": v(10.4, 17.08) * mm, "end": v(10.15, 17.05) * mm});
            skLineSegment(sketch, "E29.67.2.3", {"start": v(10.4, 12) * mm, "end": v(10.4, 17.34) * mm, "construction": true});
            skPoint(sketch, "E29.0.2.4", {"position": v(9.9, 20.55) * mm});
            skLineSegment(sketch, "E29.1.2.4", {"start": v(10.4, 18) * mm, "end": v(5.77, 15.33) * mm, "construction": true});
            skLineSegment(sketch, "E29.4.2.4", {"start": v(12.85, 17.16) * mm, "end": v(14.89, 15.69) * mm});
            skPoint(sketch, "E29.7.2.4", {"position": v(10.89, 20.55) * mm});
            skArc(sketch, "E29.8.2.4", {"start": v(7.94, 17.16) * mm, "mid": v(7.8, 16.5) * mm, "end": v(8.43, 16.3) * mm});
            skLineSegment(sketch, "E29.12.2.4", {"start": v(10.4, 18) * mm, "end": v(10.4, 23.08) * mm, "construction": true});
            skLineSegment(sketch, "E29.15.2.4", {"start": v(10.4, 18) * mm, "end": v(14.8, 15.46) * mm, "construction": true});
            skLineSegment(sketch, "E29.18.2.4", {"start": v(9.9, 20.55) * mm, "end": v(10.15, 23.05) * mm});
            skLineSegment(sketch, "E29.21.2.4", {"start": v(10.4, 18) * mm, "end": v(15.02, 15.33) * mm, "construction": true});
            skPoint(sketch, "E29.24.2.4", {"position": v(12.85, 17.16) * mm});
            skPoint(sketch, "E29.25.2.4", {"position": v(7.94, 17.16) * mm});
            skPoint(sketch, "E29.26.2.4", {"position": v(10.4, 18) * mm});
            skLineSegment(sketch, "E29.27.2.4", {"start": v(10.4, 18) * mm, "end": v(6, 15.46) * mm, "construction": true});
            skArc(sketch, "E29.30.2.4", {"start": v(12.35, 16.3) * mm, "mid": v(13, 16.5) * mm, "end": v(12.85, 17.16) * mm});
            skPoint(sketch, "E29.34.2.4", {"position": v(8.43, 16.3) * mm});
            skLineSegment(sketch, "E29.35.2.4", {"start": v(8.43, 16.3) * mm, "end": v(6.14, 15.26) * mm});
            skLineSegment(sketch, "E29.38.2.4", {"start": v(7.94, 17.16) * mm, "end": v(5.9, 15.69) * mm});
            skPoint(sketch, "E29.41.2.4", {"position": v(12.35, 16.3) * mm});
            skLineSegment(sketch, "E29.42.2.4", {"start": v(10.89, 20.55) * mm, "end": v(10.64, 23.05) * mm});
            skLineSegment(sketch, "E29.45.2.4", {"start": v(12.35, 16.3) * mm, "end": v(14.64, 15.26) * mm});
            skArc(sketch, "E29.48.2.4", {"start": v(10.89, 20.55) * mm, "mid": v(10.4, 21) * mm, "end": v(9.9, 20.55) * mm});
            skPoint(sketch, "E29.52.2.4", {"position": v(12.35, 16.3) * mm});
            skPoint(sketch, "E29.53.2.4", {"position": v(10.89, 20.55) * mm});
            skPoint(sketch, "E29.54.2.4", {"position": v(7.94, 17.16) * mm});
            skArc(sketch, "E29.55.2.4", {"start": v(5.9, 15.69) * mm, "mid": v(6, 15.46) * mm, "end": v(6.14, 15.26) * mm});
            skArc(sketch, "E29.59.2.4", {"start": v(14.64, 15.26) * mm, "mid": v(14.8, 15.46) * mm, "end": v(14.89, 15.69) * mm});
            skArc(sketch, "E29.63.2.4", {"start": v(10.64, 23.05) * mm, "mid": v(10.4, 23.08) * mm, "end": v(10.15, 23.05) * mm});
            skLineSegment(sketch, "E29.67.2.4", {"start": v(10.4, 18) * mm, "end": v(10.4, 23.34) * mm, "construction": true});
            skPoint(sketch, "E29.0.2.5", {"position": v(9.9, 26.55) * mm});
            skLineSegment(sketch, "E29.1.2.5", {"start": v(10.4, 24) * mm, "end": v(5.77, 21.33) * mm, "construction": true});
            skLineSegment(sketch, "E29.4.2.5", {"start": v(12.85, 23.16) * mm, "end": v(14.89, 21.69) * mm});
            skPoint(sketch, "E29.7.2.5", {"position": v(10.89, 26.55) * mm});
            skArc(sketch, "E29.8.2.5", {"start": v(7.94, 23.16) * mm, "mid": v(7.8, 22.5) * mm, "end": v(8.43, 22.3) * mm});
            skLineSegment(sketch, "E29.12.2.5", {"start": v(10.4, 24) * mm, "end": v(10.4, 29.08) * mm, "construction": true});
            skLineSegment(sketch, "E29.15.2.5", {"start": v(10.4, 24) * mm, "end": v(14.8, 21.46) * mm, "construction": true});
            skLineSegment(sketch, "E29.18.2.5", {"start": v(9.9, 26.55) * mm, "end": v(10.15, 29.05) * mm});
            skLineSegment(sketch, "E29.21.2.5", {"start": v(10.4, 24) * mm, "end": v(15.02, 21.33) * mm, "construction": true});
            skPoint(sketch, "E29.24.2.5", {"position": v(12.85, 23.16) * mm});
            skPoint(sketch, "E29.25.2.5", {"position": v(7.94, 23.16) * mm});
            skPoint(sketch, "E29.26.2.5", {"position": v(10.4, 24) * mm});
            skLineSegment(sketch, "E29.27.2.5", {"start": v(10.4, 24) * mm, "end": v(6, 21.46) * mm, "construction": true});
            skArc(sketch, "E29.30.2.5", {"start": v(12.35, 22.3) * mm, "mid": v(13, 22.5) * mm, "end": v(12.85, 23.16) * mm});
            skPoint(sketch, "E29.34.2.5", {"position": v(8.43, 22.3) * mm});
            skLineSegment(sketch, "E29.35.2.5", {"start": v(8.43, 22.3) * mm, "end": v(6.14, 21.26) * mm});
            skLineSegment(sketch, "E29.38.2.5", {"start": v(7.94, 23.16) * mm, "end": v(5.9, 21.69) * mm});
            skPoint(sketch, "E29.41.2.5", {"position": v(12.35, 22.3) * mm});
            skLineSegment(sketch, "E29.42.2.5", {"start": v(10.89, 26.55) * mm, "end": v(10.64, 29.05) * mm});
            skLineSegment(sketch, "E29.45.2.5", {"start": v(12.35, 22.3) * mm, "end": v(14.64, 21.26) * mm});
            skArc(sketch, "E29.48.2.5", {"start": v(10.89, 26.55) * mm, "mid": v(10.4, 27) * mm, "end": v(9.9, 26.55) * mm});
            skPoint(sketch, "E29.52.2.5", {"position": v(12.35, 22.3) * mm});
            skPoint(sketch, "E29.53.2.5", {"position": v(10.89, 26.55) * mm});
            skPoint(sketch, "E29.54.2.5", {"position": v(7.94, 23.16) * mm});
            skArc(sketch, "E29.55.2.5", {"start": v(5.9, 21.69) * mm, "mid": v(6, 21.46) * mm, "end": v(6.14, 21.26) * mm});
            skArc(sketch, "E29.59.2.5", {"start": v(14.64, 21.26) * mm, "mid": v(14.8, 21.46) * mm, "end": v(14.89, 21.69) * mm});
            skArc(sketch, "E29.63.2.5", {"start": v(10.64, 29.05) * mm, "mid": v(10.4, 29.08) * mm, "end": v(10.15, 29.05) * mm});
            skLineSegment(sketch, "E29.67.2.5", {"start": v(10.4, 24) * mm, "end": v(10.4, 29.34) * mm, "construction": true});
            skPoint(sketch, "E29.0.2.6", {"position": v(9.9, 32.55) * mm});
            skLineSegment(sketch, "E29.1.2.6", {"start": v(10.4, 30) * mm, "end": v(5.77, 27.33) * mm, "construction": true});
            skLineSegment(sketch, "E29.4.2.6", {"start": v(12.85, 29.16) * mm, "end": v(14.89, 27.69) * mm});
            skPoint(sketch, "E29.7.2.6", {"position": v(10.89, 32.55) * mm});
            skArc(sketch, "E29.8.2.6", {"start": v(7.94, 29.16) * mm, "mid": v(7.8, 28.5) * mm, "end": v(8.43, 28.3) * mm});
            skLineSegment(sketch, "E29.12.2.6", {"start": v(10.4, 30) * mm, "end": v(10.4, 35.08) * mm, "construction": true});
            skLineSegment(sketch, "E29.15.2.6", {"start": v(10.4, 30) * mm, "end": v(14.8, 27.46) * mm, "construction": true});
            skLineSegment(sketch, "E29.18.2.6", {"start": v(9.9, 32.55) * mm, "end": v(10.15, 35.05) * mm});
            skLineSegment(sketch, "E29.21.2.6", {"start": v(10.4, 30) * mm, "end": v(15.02, 27.33) * mm, "construction": true});
            skPoint(sketch, "E29.24.2.6", {"position": v(12.85, 29.16) * mm});
            skPoint(sketch, "E29.25.2.6", {"position": v(7.94, 29.16) * mm});
            skPoint(sketch, "E29.26.2.6", {"position": v(10.4, 30) * mm});
            skLineSegment(sketch, "E29.27.2.6", {"start": v(10.4, 30) * mm, "end": v(6, 27.46) * mm, "construction": true});
            skArc(sketch, "E29.30.2.6", {"start": v(12.35, 28.3) * mm, "mid": v(13, 28.5) * mm, "end": v(12.85, 29.16) * mm});
            skPoint(sketch, "E29.34.2.6", {"position": v(8.43, 28.3) * mm});
            skLineSegment(sketch, "E29.35.2.6", {"start": v(8.43, 28.3) * mm, "end": v(6.14, 27.26) * mm});
            skLineSegment(sketch, "E29.38.2.6", {"start": v(7.94, 29.16) * mm, "end": v(5.9, 27.69) * mm});
            skPoint(sketch, "E29.41.2.6", {"position": v(12.35, 28.3) * mm});
            skLineSegment(sketch, "E29.42.2.6", {"start": v(10.89, 32.55) * mm, "end": v(10.64, 35.05) * mm});
            skLineSegment(sketch, "E29.45.2.6", {"start": v(12.35, 28.3) * mm, "end": v(14.64, 27.26) * mm});
            skArc(sketch, "E29.48.2.6", {"start": v(10.89, 32.55) * mm, "mid": v(10.4, 33) * mm, "end": v(9.9, 32.55) * mm});
            skPoint(sketch, "E29.52.2.6", {"position": v(12.35, 28.3) * mm});
            skPoint(sketch, "E29.53.2.6", {"position": v(10.89, 32.55) * mm});
            skPoint(sketch, "E29.54.2.6", {"position": v(7.94, 29.16) * mm});
            skArc(sketch, "E29.55.2.6", {"start": v(5.9, 27.69) * mm, "mid": v(6, 27.46) * mm, "end": v(6.14, 27.26) * mm});
            skArc(sketch, "E29.59.2.6", {"start": v(14.64, 27.26) * mm, "mid": v(14.8, 27.46) * mm, "end": v(14.89, 27.69) * mm});
            skArc(sketch, "E29.63.2.6", {"start": v(10.64, 35.05) * mm, "mid": v(10.4, 35.08) * mm, "end": v(10.15, 35.05) * mm});
            skLineSegment(sketch, "E29.67.2.6", {"start": v(10.4, 30) * mm, "end": v(10.4, 35.34) * mm, "construction": true});
            skPoint(sketch, "E29.0.2.7", {"position": v(9.9, 38.55) * mm});
            skLineSegment(sketch, "E29.1.2.7", {"start": v(10.4, 36) * mm, "end": v(5.77, 33.33) * mm, "construction": true});
            skLineSegment(sketch, "E29.4.2.7", {"start": v(12.85, 35.16) * mm, "end": v(14.89, 33.69) * mm});
            skPoint(sketch, "E29.7.2.7", {"position": v(10.89, 38.55) * mm});
            skArc(sketch, "E29.8.2.7", {"start": v(7.94, 35.16) * mm, "mid": v(7.8, 34.5) * mm, "end": v(8.43, 34.3) * mm});
            skLineSegment(sketch, "E29.12.2.7", {"start": v(10.4, 36) * mm, "end": v(10.4, 41.08) * mm, "construction": true});
            skLineSegment(sketch, "E29.15.2.7", {"start": v(10.4, 36) * mm, "end": v(14.8, 33.46) * mm, "construction": true});
            skLineSegment(sketch, "E29.18.2.7", {"start": v(9.9, 38.55) * mm, "end": v(10.15, 41.05) * mm});
            skLineSegment(sketch, "E29.21.2.7", {"start": v(10.4, 36) * mm, "end": v(15.02, 33.33) * mm, "construction": true});
            skPoint(sketch, "E29.24.2.7", {"position": v(12.85, 35.16) * mm});
            skPoint(sketch, "E29.25.2.7", {"position": v(7.94, 35.16) * mm});
            skPoint(sketch, "E29.26.2.7", {"position": v(10.4, 36) * mm});
            skLineSegment(sketch, "E29.27.2.7", {"start": v(10.4, 36) * mm, "end": v(6, 33.46) * mm, "construction": true});
            skArc(sketch, "E29.30.2.7", {"start": v(12.35, 34.3) * mm, "mid": v(13, 34.5) * mm, "end": v(12.85, 35.16) * mm});
            skPoint(sketch, "E29.34.2.7", {"position": v(8.43, 34.3) * mm});
            skLineSegment(sketch, "E29.35.2.7", {"start": v(8.43, 34.3) * mm, "end": v(6.14, 33.26) * mm});
            skLineSegment(sketch, "E29.38.2.7", {"start": v(7.94, 35.16) * mm, "end": v(5.9, 33.69) * mm});
            skPoint(sketch, "E29.41.2.7", {"position": v(12.35, 34.3) * mm});
            skLineSegment(sketch, "E29.42.2.7", {"start": v(10.89, 38.55) * mm, "end": v(10.64, 41.05) * mm});
            skLineSegment(sketch, "E29.45.2.7", {"start": v(12.35, 34.3) * mm, "end": v(14.64, 33.26) * mm});
            skArc(sketch, "E29.48.2.7", {"start": v(10.89, 38.55) * mm, "mid": v(10.4, 39) * mm, "end": v(9.9, 38.55) * mm});
            skPoint(sketch, "E29.52.2.7", {"position": v(12.35, 34.3) * mm});
            skPoint(sketch, "E29.53.2.7", {"position": v(10.89, 38.55) * mm});
            skPoint(sketch, "E29.54.2.7", {"position": v(7.94, 35.16) * mm});
            skArc(sketch, "E29.55.2.7", {"start": v(5.9, 33.69) * mm, "mid": v(6, 33.46) * mm, "end": v(6.14, 33.26) * mm});
            skArc(sketch, "E29.59.2.7", {"start": v(14.64, 33.26) * mm, "mid": v(14.8, 33.46) * mm, "end": v(14.89, 33.69) * mm});
            skArc(sketch, "E29.63.2.7", {"start": v(10.64, 41.05) * mm, "mid": v(10.4, 41.08) * mm, "end": v(10.15, 41.05) * mm});
            skLineSegment(sketch, "E29.67.2.7", {"start": v(10.4, 36) * mm, "end": v(10.4, 41.34) * mm, "construction": true});
            skPoint(sketch, "E29.0.3.2", {"position": v(15.1, 5.55) * mm});
            skLineSegment(sketch, "E29.1.3.2", {"start": v(15.59, 3) * mm, "end": v(10.96, 0.33) * mm, "construction": true});
            skLineSegment(sketch, "E29.4.3.2", {"start": v(18.05, 2.16) * mm, "end": v(20.08, 0.69) * mm});
            skPoint(sketch, "E29.7.3.2", {"position": v(16.09, 5.55) * mm});
            skArc(sketch, "E29.8.3.2", {"start": v(13.13, 2.16) * mm, "mid": v(13, 1.5) * mm, "end": v(13.63, 1.3) * mm});
            skLineSegment(sketch, "E29.12.3.2", {"start": v(15.59, 3) * mm, "end": v(15.59, 8.08) * mm, "construction": true});
            skLineSegment(sketch, "E29.15.3.2", {"start": v(15.59, 3) * mm, "end": v(19.99, 0.46) * mm, "construction": true});
            skLineSegment(sketch, "E29.18.3.2", {"start": v(15.1, 5.55) * mm, "end": v(15.34, 8.05) * mm});
            skLineSegment(sketch, "E29.21.3.2", {"start": v(15.59, 3) * mm, "end": v(20.22, 0.33) * mm, "construction": true});
            skPoint(sketch, "E29.24.3.2", {"position": v(18.05, 2.16) * mm});
            skPoint(sketch, "E29.25.3.2", {"position": v(13.13, 2.16) * mm});
            skPoint(sketch, "E29.26.3.2", {"position": v(15.59, 3) * mm});
            skLineSegment(sketch, "E29.27.3.2", {"start": v(15.59, 3) * mm, "end": v(11.19, 0.46) * mm, "construction": true});
            skArc(sketch, "E29.30.3.2", {"start": v(17.55, 1.3) * mm, "mid": v(18.19, 1.5) * mm, "end": v(18.05, 2.16) * mm});
            skPoint(sketch, "E29.34.3.2", {"position": v(13.63, 1.3) * mm});
            skLineSegment(sketch, "E29.35.3.2", {"start": v(13.63, 1.3) * mm, "end": v(11.34, 0.26) * mm});
            skLineSegment(sketch, "E29.38.3.2", {"start": v(13.13, 2.16) * mm, "end": v(11.1, 0.69) * mm});
            skPoint(sketch, "E29.41.3.2", {"position": v(17.55, 1.3) * mm});
            skLineSegment(sketch, "E29.42.3.2", {"start": v(16.09, 5.55) * mm, "end": v(15.83, 8.05) * mm});
            skLineSegment(sketch, "E29.45.3.2", {"start": v(17.55, 1.3) * mm, "end": v(19.84, 0.26) * mm});
            skArc(sketch, "E29.48.3.2", {"start": v(16.09, 5.55) * mm, "mid": v(15.59, 6) * mm, "end": v(15.1, 5.55) * mm});
            skPoint(sketch, "E29.52.3.2", {"position": v(17.55, 1.3) * mm});
            skPoint(sketch, "E29.53.3.2", {"position": v(16.09, 5.55) * mm});
            skPoint(sketch, "E29.54.3.2", {"position": v(13.13, 2.16) * mm});
            skArc(sketch, "E29.55.3.2", {"start": v(11.1, 0.69) * mm, "mid": v(11.19, 0.46) * mm, "end": v(11.34, 0.26) * mm});
            skArc(sketch, "E29.59.3.2", {"start": v(19.84, 0.26) * mm, "mid": v(19.99, 0.46) * mm, "end": v(20.08, 0.69) * mm});
            skArc(sketch, "E29.63.3.2", {"start": v(15.83, 8.05) * mm, "mid": v(15.59, 8.08) * mm, "end": v(15.34, 8.05) * mm});
            skLineSegment(sketch, "E29.67.3.2", {"start": v(15.59, 3) * mm, "end": v(15.59, 8.34) * mm, "construction": true});
            skPoint(sketch, "E29.0.3.3", {"position": v(15.1, 11.55) * mm});
            skLineSegment(sketch, "E29.1.3.3", {"start": v(15.59, 9) * mm, "end": v(10.96, 6.33) * mm, "construction": true});
            skLineSegment(sketch, "E29.4.3.3", {"start": v(18.05, 8.16) * mm, "end": v(20.08, 6.69) * mm});
            skPoint(sketch, "E29.7.3.3", {"position": v(16.09, 11.55) * mm});
            skArc(sketch, "E29.8.3.3", {"start": v(13.13, 8.16) * mm, "mid": v(13, 7.5) * mm, "end": v(13.63, 7.3) * mm});
            skLineSegment(sketch, "E29.12.3.3", {"start": v(15.59, 9) * mm, "end": v(15.59, 14.08) * mm, "construction": true});
            skLineSegment(sketch, "E29.15.3.3", {"start": v(15.59, 9) * mm, "end": v(19.99, 6.46) * mm, "construction": true});
            skLineSegment(sketch, "E29.18.3.3", {"start": v(15.1, 11.55) * mm, "end": v(15.34, 14.05) * mm});
            skLineSegment(sketch, "E29.21.3.3", {"start": v(15.59, 9) * mm, "end": v(20.22, 6.33) * mm, "construction": true});
            skPoint(sketch, "E29.24.3.3", {"position": v(18.05, 8.16) * mm});
            skPoint(sketch, "E29.25.3.3", {"position": v(13.13, 8.16) * mm});
            skPoint(sketch, "E29.26.3.3", {"position": v(15.59, 9) * mm});
            skLineSegment(sketch, "E29.27.3.3", {"start": v(15.59, 9) * mm, "end": v(11.19, 6.46) * mm, "construction": true});
            skArc(sketch, "E29.30.3.3", {"start": v(17.55, 7.3) * mm, "mid": v(18.19, 7.5) * mm, "end": v(18.05, 8.16) * mm});
            skPoint(sketch, "E29.34.3.3", {"position": v(13.63, 7.3) * mm});
            skLineSegment(sketch, "E29.35.3.3", {"start": v(13.63, 7.3) * mm, "end": v(11.34, 6.26) * mm});
            skLineSegment(sketch, "E29.38.3.3", {"start": v(13.13, 8.16) * mm, "end": v(11.1, 6.69) * mm});
            skPoint(sketch, "E29.41.3.3", {"position": v(17.55, 7.3) * mm});
            skLineSegment(sketch, "E29.42.3.3", {"start": v(16.09, 11.55) * mm, "end": v(15.83, 14.05) * mm});
            skLineSegment(sketch, "E29.45.3.3", {"start": v(17.55, 7.3) * mm, "end": v(19.84, 6.26) * mm});
            skArc(sketch, "E29.48.3.3", {"start": v(16.09, 11.55) * mm, "mid": v(15.59, 12) * mm, "end": v(15.1, 11.55) * mm});
            skPoint(sketch, "E29.52.3.3", {"position": v(17.55, 7.3) * mm});
            skPoint(sketch, "E29.53.3.3", {"position": v(16.09, 11.55) * mm});
            skPoint(sketch, "E29.54.3.3", {"position": v(13.13, 8.16) * mm});
            skArc(sketch, "E29.55.3.3", {"start": v(11.1, 6.69) * mm, "mid": v(11.19, 6.46) * mm, "end": v(11.34, 6.26) * mm});
            skArc(sketch, "E29.59.3.3", {"start": v(19.84, 6.26) * mm, "mid": v(19.99, 6.46) * mm, "end": v(20.08, 6.69) * mm});
            skArc(sketch, "E29.63.3.3", {"start": v(15.83, 14.05) * mm, "mid": v(15.59, 14.08) * mm, "end": v(15.34, 14.05) * mm});
            skLineSegment(sketch, "E29.67.3.3", {"start": v(15.59, 9) * mm, "end": v(15.59, 14.34) * mm, "construction": true});
            skPoint(sketch, "E29.0.3.4", {"position": v(15.1, 17.55) * mm});
            skLineSegment(sketch, "E29.1.3.4", {"start": v(15.59, 15) * mm, "end": v(10.96, 12.33) * mm, "construction": true});
            skLineSegment(sketch, "E29.4.3.4", {"start": v(18.05, 14.16) * mm, "end": v(20.08, 12.69) * mm});
            skPoint(sketch, "E29.7.3.4", {"position": v(16.09, 17.55) * mm});
            skArc(sketch, "E29.8.3.4", {"start": v(13.13, 14.16) * mm, "mid": v(13, 13.5) * mm, "end": v(13.63, 13.3) * mm});
            skLineSegment(sketch, "E29.12.3.4", {"start": v(15.59, 15) * mm, "end": v(15.59, 20.08) * mm, "construction": true});
            skLineSegment(sketch, "E29.15.3.4", {"start": v(15.59, 15) * mm, "end": v(19.99, 12.46) * mm, "construction": true});
            skLineSegment(sketch, "E29.18.3.4", {"start": v(15.1, 17.55) * mm, "end": v(15.34, 20.05) * mm});
            skLineSegment(sketch, "E29.21.3.4", {"start": v(15.59, 15) * mm, "end": v(20.22, 12.33) * mm, "construction": true});
            skPoint(sketch, "E29.24.3.4", {"position": v(18.05, 14.16) * mm});
            skPoint(sketch, "E29.25.3.4", {"position": v(13.13, 14.16) * mm});
            skPoint(sketch, "E29.26.3.4", {"position": v(15.59, 15) * mm});
            skLineSegment(sketch, "E29.27.3.4", {"start": v(15.59, 15) * mm, "end": v(11.19, 12.46) * mm, "construction": true});
            skArc(sketch, "E29.30.3.4", {"start": v(17.55, 13.3) * mm, "mid": v(18.19, 13.5) * mm, "end": v(18.05, 14.16) * mm});
            skPoint(sketch, "E29.34.3.4", {"position": v(13.63, 13.3) * mm});
            skLineSegment(sketch, "E29.35.3.4", {"start": v(13.63, 13.3) * mm, "end": v(11.34, 12.26) * mm});
            skLineSegment(sketch, "E29.38.3.4", {"start": v(13.13, 14.16) * mm, "end": v(11.1, 12.69) * mm});
            skPoint(sketch, "E29.41.3.4", {"position": v(17.55, 13.3) * mm});
            skLineSegment(sketch, "E29.42.3.4", {"start": v(16.09, 17.55) * mm, "end": v(15.83, 20.05) * mm});
            skLineSegment(sketch, "E29.45.3.4", {"start": v(17.55, 13.3) * mm, "end": v(19.84, 12.26) * mm});
            skArc(sketch, "E29.48.3.4", {"start": v(16.09, 17.55) * mm, "mid": v(15.59, 18) * mm, "end": v(15.1, 17.55) * mm});
            skPoint(sketch, "E29.52.3.4", {"position": v(17.55, 13.3) * mm});
            skPoint(sketch, "E29.53.3.4", {"position": v(16.09, 17.55) * mm});
            skPoint(sketch, "E29.54.3.4", {"position": v(13.13, 14.16) * mm});
            skArc(sketch, "E29.55.3.4", {"start": v(11.1, 12.69) * mm, "mid": v(11.19, 12.46) * mm, "end": v(11.34, 12.26) * mm});
            skArc(sketch, "E29.59.3.4", {"start": v(19.84, 12.26) * mm, "mid": v(19.99, 12.46) * mm, "end": v(20.08, 12.69) * mm});
            skArc(sketch, "E29.63.3.4", {"start": v(15.83, 20.05) * mm, "mid": v(15.59, 20.08) * mm, "end": v(15.34, 20.05) * mm});
            skLineSegment(sketch, "E29.67.3.4", {"start": v(15.59, 15) * mm, "end": v(15.59, 20.34) * mm, "construction": true});
            skPoint(sketch, "E29.0.3.5", {"position": v(15.1, 23.55) * mm});
            skLineSegment(sketch, "E29.1.3.5", {"start": v(15.59, 21) * mm, "end": v(10.96, 18.33) * mm, "construction": true});
            skLineSegment(sketch, "E29.4.3.5", {"start": v(18.05, 20.16) * mm, "end": v(20.08, 18.69) * mm});
            skPoint(sketch, "E29.7.3.5", {"position": v(16.09, 23.55) * mm});
            skArc(sketch, "E29.8.3.5", {"start": v(13.13, 20.16) * mm, "mid": v(13, 19.5) * mm, "end": v(13.63, 19.3) * mm});
            skLineSegment(sketch, "E29.12.3.5", {"start": v(15.59, 21) * mm, "end": v(15.59, 26.08) * mm, "construction": true});
            skLineSegment(sketch, "E29.15.3.5", {"start": v(15.59, 21) * mm, "end": v(19.99, 18.46) * mm, "construction": true});
            skLineSegment(sketch, "E29.18.3.5", {"start": v(15.1, 23.55) * mm, "end": v(15.34, 26.05) * mm});
            skLineSegment(sketch, "E29.21.3.5", {"start": v(15.59, 21) * mm, "end": v(20.22, 18.33) * mm, "construction": true});
            skPoint(sketch, "E29.24.3.5", {"position": v(18.05, 20.16) * mm});
            skPoint(sketch, "E29.25.3.5", {"position": v(13.13, 20.16) * mm});
            skPoint(sketch, "E29.26.3.5", {"position": v(15.59, 21) * mm});
            skLineSegment(sketch, "E29.27.3.5", {"start": v(15.59, 21) * mm, "end": v(11.19, 18.46) * mm, "construction": true});
            skArc(sketch, "E29.30.3.5", {"start": v(17.55, 19.3) * mm, "mid": v(18.19, 19.5) * mm, "end": v(18.05, 20.16) * mm});
            skPoint(sketch, "E29.34.3.5", {"position": v(13.63, 19.3) * mm});
            skLineSegment(sketch, "E29.35.3.5", {"start": v(13.63, 19.3) * mm, "end": v(11.34, 18.26) * mm});
            skLineSegment(sketch, "E29.38.3.5", {"start": v(13.13, 20.16) * mm, "end": v(11.1, 18.69) * mm});
            skPoint(sketch, "E29.41.3.5", {"position": v(17.55, 19.3) * mm});
            skLineSegment(sketch, "E29.42.3.5", {"start": v(16.09, 23.55) * mm, "end": v(15.83, 26.05) * mm});
            skLineSegment(sketch, "E29.45.3.5", {"start": v(17.55, 19.3) * mm, "end": v(19.84, 18.26) * mm});
            skArc(sketch, "E29.48.3.5", {"start": v(16.09, 23.55) * mm, "mid": v(15.59, 24) * mm, "end": v(15.1, 23.55) * mm});
            skPoint(sketch, "E29.52.3.5", {"position": v(17.55, 19.3) * mm});
            skPoint(sketch, "E29.53.3.5", {"position": v(16.09, 23.55) * mm});
            skPoint(sketch, "E29.54.3.5", {"position": v(13.13, 20.16) * mm});
            skArc(sketch, "E29.55.3.5", {"start": v(11.1, 18.69) * mm, "mid": v(11.19, 18.46) * mm, "end": v(11.34, 18.26) * mm});
            skArc(sketch, "E29.59.3.5", {"start": v(19.84, 18.26) * mm, "mid": v(19.99, 18.46) * mm, "end": v(20.08, 18.69) * mm});
            skArc(sketch, "E29.63.3.5", {"start": v(15.83, 26.05) * mm, "mid": v(15.59, 26.08) * mm, "end": v(15.34, 26.05) * mm});
            skLineSegment(sketch, "E29.67.3.5", {"start": v(15.59, 21) * mm, "end": v(15.59, 26.34) * mm, "construction": true});
            skPoint(sketch, "E29.0.3.6", {"position": v(15.1, 29.55) * mm});
            skLineSegment(sketch, "E29.1.3.6", {"start": v(15.59, 27) * mm, "end": v(10.96, 24.33) * mm, "construction": true});
            skLineSegment(sketch, "E29.4.3.6", {"start": v(18.05, 26.16) * mm, "end": v(20.08, 24.69) * mm});
            skPoint(sketch, "E29.7.3.6", {"position": v(16.09, 29.55) * mm});
            skArc(sketch, "E29.8.3.6", {"start": v(13.13, 26.16) * mm, "mid": v(13, 25.5) * mm, "end": v(13.63, 25.3) * mm});
            skLineSegment(sketch, "E29.12.3.6", {"start": v(15.59, 27) * mm, "end": v(15.59, 32.08) * mm, "construction": true});
            skLineSegment(sketch, "E29.15.3.6", {"start": v(15.59, 27) * mm, "end": v(19.99, 24.46) * mm, "construction": true});
            skLineSegment(sketch, "E29.18.3.6", {"start": v(15.1, 29.55) * mm, "end": v(15.34, 32.05) * mm});
            skLineSegment(sketch, "E29.21.3.6", {"start": v(15.59, 27) * mm, "end": v(20.22, 24.33) * mm, "construction": true});
            skPoint(sketch, "E29.24.3.6", {"position": v(18.05, 26.16) * mm});
            skPoint(sketch, "E29.25.3.6", {"position": v(13.13, 26.16) * mm});
            skPoint(sketch, "E29.26.3.6", {"position": v(15.59, 27) * mm});
            skLineSegment(sketch, "E29.27.3.6", {"start": v(15.59, 27) * mm, "end": v(11.19, 24.46) * mm, "construction": true});
            skArc(sketch, "E29.30.3.6", {"start": v(17.55, 25.3) * mm, "mid": v(18.19, 25.5) * mm, "end": v(18.05, 26.16) * mm});
            skPoint(sketch, "E29.34.3.6", {"position": v(13.63, 25.3) * mm});
            skLineSegment(sketch, "E29.35.3.6", {"start": v(13.63, 25.3) * mm, "end": v(11.34, 24.26) * mm});
            skLineSegment(sketch, "E29.38.3.6", {"start": v(13.13, 26.16) * mm, "end": v(11.1, 24.69) * mm});
            skPoint(sketch, "E29.41.3.6", {"position": v(17.55, 25.3) * mm});
            skLineSegment(sketch, "E29.42.3.6", {"start": v(16.09, 29.55) * mm, "end": v(15.83, 32.05) * mm});
            skLineSegment(sketch, "E29.45.3.6", {"start": v(17.55, 25.3) * mm, "end": v(19.84, 24.26) * mm});
            skArc(sketch, "E29.48.3.6", {"start": v(16.09, 29.55) * mm, "mid": v(15.59, 30) * mm, "end": v(15.1, 29.55) * mm});
            skPoint(sketch, "E29.52.3.6", {"position": v(17.55, 25.3) * mm});
            skPoint(sketch, "E29.53.3.6", {"position": v(16.09, 29.55) * mm});
            skPoint(sketch, "E29.54.3.6", {"position": v(13.13, 26.16) * mm});
            skArc(sketch, "E29.55.3.6", {"start": v(11.1, 24.69) * mm, "mid": v(11.19, 24.46) * mm, "end": v(11.34, 24.26) * mm});
            skArc(sketch, "E29.59.3.6", {"start": v(19.84, 24.26) * mm, "mid": v(19.99, 24.46) * mm, "end": v(20.08, 24.69) * mm});
            skArc(sketch, "E29.63.3.6", {"start": v(15.83, 32.05) * mm, "mid": v(15.59, 32.08) * mm, "end": v(15.34, 32.05) * mm});
            skLineSegment(sketch, "E29.67.3.6", {"start": v(15.59, 27) * mm, "end": v(15.59, 32.34) * mm, "construction": true});
            skPoint(sketch, "E29.0.3.7", {"position": v(15.1, 35.55) * mm});
            skLineSegment(sketch, "E29.1.3.7", {"start": v(15.59, 33) * mm, "end": v(10.96, 30.33) * mm, "construction": true});
            skLineSegment(sketch, "E29.4.3.7", {"start": v(18.05, 32.16) * mm, "end": v(20.08, 30.69) * mm});
            skPoint(sketch, "E29.7.3.7", {"position": v(16.09, 35.55) * mm});
            skArc(sketch, "E29.8.3.7", {"start": v(13.13, 32.16) * mm, "mid": v(13, 31.5) * mm, "end": v(13.63, 31.3) * mm});
            skLineSegment(sketch, "E29.12.3.7", {"start": v(15.59, 33) * mm, "end": v(15.59, 38.08) * mm, "construction": true});
            skLineSegment(sketch, "E29.15.3.7", {"start": v(15.59, 33) * mm, "end": v(19.99, 30.46) * mm, "construction": true});
            skLineSegment(sketch, "E29.18.3.7", {"start": v(15.1, 35.55) * mm, "end": v(15.34, 38.05) * mm});
            skLineSegment(sketch, "E29.21.3.7", {"start": v(15.59, 33) * mm, "end": v(20.22, 30.33) * mm, "construction": true});
            skPoint(sketch, "E29.24.3.7", {"position": v(18.05, 32.16) * mm});
            skPoint(sketch, "E29.25.3.7", {"position": v(13.13, 32.16) * mm});
            skPoint(sketch, "E29.26.3.7", {"position": v(15.59, 33) * mm});
            skLineSegment(sketch, "E29.27.3.7", {"start": v(15.59, 33) * mm, "end": v(11.19, 30.46) * mm, "construction": true});
            skArc(sketch, "E29.30.3.7", {"start": v(17.55, 31.3) * mm, "mid": v(18.19, 31.5) * mm, "end": v(18.05, 32.16) * mm});
            skPoint(sketch, "E29.34.3.7", {"position": v(13.63, 31.3) * mm});
            skLineSegment(sketch, "E29.35.3.7", {"start": v(13.63, 31.3) * mm, "end": v(11.34, 30.26) * mm});
            skLineSegment(sketch, "E29.38.3.7", {"start": v(13.13, 32.16) * mm, "end": v(11.1, 30.69) * mm});
            skPoint(sketch, "E29.41.3.7", {"position": v(17.55, 31.3) * mm});
            skLineSegment(sketch, "E29.42.3.7", {"start": v(16.09, 35.55) * mm, "end": v(15.83, 38.05) * mm});
            skLineSegment(sketch, "E29.45.3.7", {"start": v(17.55, 31.3) * mm, "end": v(19.84, 30.26) * mm});
            skArc(sketch, "E29.48.3.7", {"start": v(16.09, 35.55) * mm, "mid": v(15.59, 36) * mm, "end": v(15.1, 35.55) * mm});
            skPoint(sketch, "E29.52.3.7", {"position": v(17.55, 31.3) * mm});
            skPoint(sketch, "E29.53.3.7", {"position": v(16.09, 35.55) * mm});
            skPoint(sketch, "E29.54.3.7", {"position": v(13.13, 32.16) * mm});
            skArc(sketch, "E29.55.3.7", {"start": v(11.1, 30.69) * mm, "mid": v(11.19, 30.46) * mm, "end": v(11.34, 30.26) * mm});
            skArc(sketch, "E29.59.3.7", {"start": v(19.84, 30.26) * mm, "mid": v(19.99, 30.46) * mm, "end": v(20.08, 30.69) * mm});
            skArc(sketch, "E29.63.3.7", {"start": v(15.83, 38.05) * mm, "mid": v(15.59, 38.08) * mm, "end": v(15.34, 38.05) * mm});
            skLineSegment(sketch, "E29.67.3.7", {"start": v(15.59, 33) * mm, "end": v(15.59, 38.34) * mm, "construction": true});
            skPoint(sketch, "E29.0.4.2", {"position": v(20.29, 2.55) * mm});
            skLineSegment(sketch, "E29.1.4.2", {"start": v(20.78, 0) * mm, "end": v(16.16, -2.67) * mm, "construction": true});
            skLineSegment(sketch, "E29.4.4.2", {"start": v(23.24, -0.84) * mm, "end": v(25.28, -2.31) * mm});
            skPoint(sketch, "E29.7.4.2", {"position": v(21.28, 2.55) * mm});
            skArc(sketch, "E29.8.4.2", {"start": v(18.33, -0.84) * mm, "mid": v(18.19, -1.5) * mm, "end": v(18.82, -1.7) * mm});
            skLineSegment(sketch, "E29.12.4.2", {"start": v(20.78, 0) * mm, "end": v(20.78, 5.08) * mm, "construction": true});
            skLineSegment(sketch, "E29.15.4.2", {"start": v(20.78, 0) * mm, "end": v(25.18, -2.54) * mm, "construction": true});
            skLineSegment(sketch, "E29.18.4.2", {"start": v(20.29, 2.55) * mm, "end": v(20.54, 5.05) * mm});
            skLineSegment(sketch, "E29.21.4.2", {"start": v(20.78, 0) * mm, "end": v(25.41, -2.67) * mm, "construction": true});
            skPoint(sketch, "E29.24.4.2", {"position": v(23.24, -0.84) * mm});
            skPoint(sketch, "E29.25.4.2", {"position": v(18.33, -0.84) * mm});
            skPoint(sketch, "E29.26.4.2", {"position": v(20.78, 0) * mm});
            skLineSegment(sketch, "E29.27.4.2", {"start": v(20.78, 0) * mm, "end": v(16.38, -2.54) * mm, "construction": true});
            skArc(sketch, "E29.30.4.2", {"start": v(22.74, -1.7) * mm, "mid": v(23.38, -1.5) * mm, "end": v(23.24, -0.84) * mm});
            skPoint(sketch, "E29.34.4.2", {"position": v(18.82, -1.7) * mm});
            skLineSegment(sketch, "E29.35.4.2", {"start": v(18.82, -1.7) * mm, "end": v(16.53, -2.74) * mm});
            skLineSegment(sketch, "E29.38.4.2", {"start": v(18.33, -0.84) * mm, "end": v(16.29, -2.31) * mm});
            skPoint(sketch, "E29.41.4.2", {"position": v(22.74, -1.7) * mm});
            skLineSegment(sketch, "E29.42.4.2", {"start": v(21.28, 2.55) * mm, "end": v(21.03, 5.05) * mm});
            skLineSegment(sketch, "E29.45.4.2", {"start": v(22.74, -1.7) * mm, "end": v(25.03, -2.74) * mm});
            skArc(sketch, "E29.48.4.2", {"start": v(21.28, 2.55) * mm, "mid": v(20.78, 3) * mm, "end": v(20.29, 2.55) * mm});
            skPoint(sketch, "E29.52.4.2", {"position": v(22.74, -1.7) * mm});
            skPoint(sketch, "E29.53.4.2", {"position": v(21.28, 2.55) * mm});
            skPoint(sketch, "E29.54.4.2", {"position": v(18.33, -0.84) * mm});
            skArc(sketch, "E29.55.4.2", {"start": v(16.29, -2.31) * mm, "mid": v(16.38, -2.54) * mm, "end": v(16.53, -2.74) * mm});
            skArc(sketch, "E29.59.4.2", {"start": v(25.03, -2.74) * mm, "mid": v(25.18, -2.54) * mm, "end": v(25.28, -2.31) * mm});
            skArc(sketch, "E29.63.4.2", {"start": v(21.03, 5.05) * mm, "mid": v(20.78, 5.08) * mm, "end": v(20.54, 5.05) * mm});
            skLineSegment(sketch, "E29.67.4.2", {"start": v(20.78, 0) * mm, "end": v(20.78, 5.34) * mm, "construction": true});
            skPoint(sketch, "E29.0.4.3", {"position": v(20.29, 8.55) * mm});
            skLineSegment(sketch, "E29.1.4.3", {"start": v(20.78, 6) * mm, "end": v(16.16, 3.33) * mm, "construction": true});
            skLineSegment(sketch, "E29.4.4.3", {"start": v(23.24, 5.16) * mm, "end": v(25.28, 3.69) * mm});
            skPoint(sketch, "E29.7.4.3", {"position": v(21.28, 8.55) * mm});
            skArc(sketch, "E29.8.4.3", {"start": v(18.33, 5.16) * mm, "mid": v(18.19, 4.5) * mm, "end": v(18.82, 4.3) * mm});
            skLineSegment(sketch, "E29.12.4.3", {"start": v(20.78, 6) * mm, "end": v(20.78, 11.08) * mm, "construction": true});
            skLineSegment(sketch, "E29.15.4.3", {"start": v(20.78, 6) * mm, "end": v(25.18, 3.46) * mm, "construction": true});
            skLineSegment(sketch, "E29.18.4.3", {"start": v(20.29, 8.55) * mm, "end": v(20.54, 11.05) * mm});
            skLineSegment(sketch, "E29.21.4.3", {"start": v(20.78, 6) * mm, "end": v(25.41, 3.33) * mm, "construction": true});
            skPoint(sketch, "E29.24.4.3", {"position": v(23.24, 5.16) * mm});
            skPoint(sketch, "E29.25.4.3", {"position": v(18.33, 5.16) * mm});
            skPoint(sketch, "E29.26.4.3", {"position": v(20.78, 6) * mm});
            skLineSegment(sketch, "E29.27.4.3", {"start": v(20.78, 6) * mm, "end": v(16.38, 3.46) * mm, "construction": true});
            skArc(sketch, "E29.30.4.3", {"start": v(22.74, 4.3) * mm, "mid": v(23.38, 4.5) * mm, "end": v(23.24, 5.16) * mm});
            skPoint(sketch, "E29.34.4.3", {"position": v(18.82, 4.3) * mm});
            skLineSegment(sketch, "E29.35.4.3", {"start": v(18.82, 4.3) * mm, "end": v(16.53, 3.26) * mm});
            skLineSegment(sketch, "E29.38.4.3", {"start": v(18.33, 5.16) * mm, "end": v(16.29, 3.69) * mm});
            skPoint(sketch, "E29.41.4.3", {"position": v(22.74, 4.3) * mm});
            skLineSegment(sketch, "E29.42.4.3", {"start": v(21.28, 8.55) * mm, "end": v(21.03, 11.05) * mm});
            skLineSegment(sketch, "E29.45.4.3", {"start": v(22.74, 4.3) * mm, "end": v(25.03, 3.26) * mm});
            skArc(sketch, "E29.48.4.3", {"start": v(21.28, 8.55) * mm, "mid": v(20.78, 9) * mm, "end": v(20.29, 8.55) * mm});
            skPoint(sketch, "E29.52.4.3", {"position": v(22.74, 4.3) * mm});
            skPoint(sketch, "E29.53.4.3", {"position": v(21.28, 8.55) * mm});
            skPoint(sketch, "E29.54.4.3", {"position": v(18.33, 5.16) * mm});
            skArc(sketch, "E29.55.4.3", {"start": v(16.29, 3.69) * mm, "mid": v(16.38, 3.46) * mm, "end": v(16.53, 3.26) * mm});
            skArc(sketch, "E29.59.4.3", {"start": v(25.03, 3.26) * mm, "mid": v(25.18, 3.46) * mm, "end": v(25.28, 3.69) * mm});
            skArc(sketch, "E29.63.4.3", {"start": v(21.03, 11.05) * mm, "mid": v(20.78, 11.08) * mm, "end": v(20.54, 11.05) * mm});
            skLineSegment(sketch, "E29.67.4.3", {"start": v(20.78, 6) * mm, "end": v(20.78, 11.34) * mm, "construction": true});
            skPoint(sketch, "E29.0.4.4", {"position": v(20.29, 14.55) * mm});
            skLineSegment(sketch, "E29.1.4.4", {"start": v(20.78, 12) * mm, "end": v(16.16, 9.33) * mm, "construction": true});
            skLineSegment(sketch, "E29.4.4.4", {"start": v(23.24, 11.16) * mm, "end": v(25.28, 9.69) * mm});
            skPoint(sketch, "E29.7.4.4", {"position": v(21.28, 14.55) * mm});
            skArc(sketch, "E29.8.4.4", {"start": v(18.33, 11.16) * mm, "mid": v(18.19, 10.5) * mm, "end": v(18.82, 10.3) * mm});
            skLineSegment(sketch, "E29.12.4.4", {"start": v(20.78, 12) * mm, "end": v(20.78, 17.08) * mm, "construction": true});
            skLineSegment(sketch, "E29.15.4.4", {"start": v(20.78, 12) * mm, "end": v(25.18, 9.46) * mm, "construction": true});
            skLineSegment(sketch, "E29.18.4.4", {"start": v(20.29, 14.55) * mm, "end": v(20.54, 17.05) * mm});
            skLineSegment(sketch, "E29.21.4.4", {"start": v(20.78, 12) * mm, "end": v(25.41, 9.33) * mm, "construction": true});
            skPoint(sketch, "E29.24.4.4", {"position": v(23.24, 11.16) * mm});
            skPoint(sketch, "E29.25.4.4", {"position": v(18.33, 11.16) * mm});
            skPoint(sketch, "E29.26.4.4", {"position": v(20.78, 12) * mm});
            skLineSegment(sketch, "E29.27.4.4", {"start": v(20.78, 12) * mm, "end": v(16.38, 9.46) * mm, "construction": true});
            skArc(sketch, "E29.30.4.4", {"start": v(22.74, 10.3) * mm, "mid": v(23.38, 10.5) * mm, "end": v(23.24, 11.16) * mm});
            skPoint(sketch, "E29.34.4.4", {"position": v(18.82, 10.3) * mm});
            skLineSegment(sketch, "E29.35.4.4", {"start": v(18.82, 10.3) * mm, "end": v(16.53, 9.26) * mm});
            skLineSegment(sketch, "E29.38.4.4", {"start": v(18.33, 11.16) * mm, "end": v(16.29, 9.69) * mm});
            skPoint(sketch, "E29.41.4.4", {"position": v(22.74, 10.3) * mm});
            skLineSegment(sketch, "E29.42.4.4", {"start": v(21.28, 14.55) * mm, "end": v(21.03, 17.05) * mm});
            skLineSegment(sketch, "E29.45.4.4", {"start": v(22.74, 10.3) * mm, "end": v(25.03, 9.26) * mm});
            skArc(sketch, "E29.48.4.4", {"start": v(21.28, 14.55) * mm, "mid": v(20.78, 15) * mm, "end": v(20.29, 14.55) * mm});
            skPoint(sketch, "E29.52.4.4", {"position": v(22.74, 10.3) * mm});
            skPoint(sketch, "E29.53.4.4", {"position": v(21.28, 14.55) * mm});
            skPoint(sketch, "E29.54.4.4", {"position": v(18.33, 11.16) * mm});
            skArc(sketch, "E29.55.4.4", {"start": v(16.29, 9.69) * mm, "mid": v(16.38, 9.46) * mm, "end": v(16.53, 9.26) * mm});
            skArc(sketch, "E29.59.4.4", {"start": v(25.03, 9.26) * mm, "mid": v(25.18, 9.46) * mm, "end": v(25.28, 9.69) * mm});
            skArc(sketch, "E29.63.4.4", {"start": v(21.03, 17.05) * mm, "mid": v(20.78, 17.08) * mm, "end": v(20.54, 17.05) * mm});
            skLineSegment(sketch, "E29.67.4.4", {"start": v(20.78, 12) * mm, "end": v(20.78, 17.34) * mm, "construction": true});
            skPoint(sketch, "E29.0.4.5", {"position": v(20.29, 20.55) * mm});
            skLineSegment(sketch, "E29.1.4.5", {"start": v(20.78, 18) * mm, "end": v(16.16, 15.33) * mm, "construction": true});
            skLineSegment(sketch, "E29.4.4.5", {"start": v(23.24, 17.16) * mm, "end": v(25.28, 15.69) * mm});
            skPoint(sketch, "E29.7.4.5", {"position": v(21.28, 20.55) * mm});
            skArc(sketch, "E29.8.4.5", {"start": v(18.33, 17.16) * mm, "mid": v(18.19, 16.5) * mm, "end": v(18.82, 16.3) * mm});
            skLineSegment(sketch, "E29.12.4.5", {"start": v(20.78, 18) * mm, "end": v(20.78, 23.08) * mm, "construction": true});
            skLineSegment(sketch, "E29.15.4.5", {"start": v(20.78, 18) * mm, "end": v(25.18, 15.46) * mm, "construction": true});
            skLineSegment(sketch, "E29.18.4.5", {"start": v(20.29, 20.55) * mm, "end": v(20.54, 23.05) * mm});
            skLineSegment(sketch, "E29.21.4.5", {"start": v(20.78, 18) * mm, "end": v(25.41, 15.33) * mm, "construction": true});
            skPoint(sketch, "E29.24.4.5", {"position": v(23.24, 17.16) * mm});
            skPoint(sketch, "E29.25.4.5", {"position": v(18.33, 17.16) * mm});
            skPoint(sketch, "E29.26.4.5", {"position": v(20.78, 18) * mm});
            skLineSegment(sketch, "E29.27.4.5", {"start": v(20.78, 18) * mm, "end": v(16.38, 15.46) * mm, "construction": true});
            skArc(sketch, "E29.30.4.5", {"start": v(22.74, 16.3) * mm, "mid": v(23.38, 16.5) * mm, "end": v(23.24, 17.16) * mm});
            skPoint(sketch, "E29.34.4.5", {"position": v(18.82, 16.3) * mm});
            skLineSegment(sketch, "E29.35.4.5", {"start": v(18.82, 16.3) * mm, "end": v(16.53, 15.26) * mm});
            skLineSegment(sketch, "E29.38.4.5", {"start": v(18.33, 17.16) * mm, "end": v(16.29, 15.69) * mm});
            skPoint(sketch, "E29.41.4.5", {"position": v(22.74, 16.3) * mm});
            skLineSegment(sketch, "E29.42.4.5", {"start": v(21.28, 20.55) * mm, "end": v(21.03, 23.05) * mm});
            skLineSegment(sketch, "E29.45.4.5", {"start": v(22.74, 16.3) * mm, "end": v(25.03, 15.26) * mm});
            skArc(sketch, "E29.48.4.5", {"start": v(21.28, 20.55) * mm, "mid": v(20.78, 21) * mm, "end": v(20.29, 20.55) * mm});
            skPoint(sketch, "E29.52.4.5", {"position": v(22.74, 16.3) * mm});
            skPoint(sketch, "E29.53.4.5", {"position": v(21.28, 20.55) * mm});
            skPoint(sketch, "E29.54.4.5", {"position": v(18.33, 17.16) * mm});
            skArc(sketch, "E29.55.4.5", {"start": v(16.29, 15.69) * mm, "mid": v(16.38, 15.46) * mm, "end": v(16.53, 15.26) * mm});
            skArc(sketch, "E29.59.4.5", {"start": v(25.03, 15.26) * mm, "mid": v(25.18, 15.46) * mm, "end": v(25.28, 15.69) * mm});
            skArc(sketch, "E29.63.4.5", {"start": v(21.03, 23.05) * mm, "mid": v(20.78, 23.08) * mm, "end": v(20.54, 23.05) * mm});
            skLineSegment(sketch, "E29.67.4.5", {"start": v(20.78, 18) * mm, "end": v(20.78, 23.34) * mm, "construction": true});
            skPoint(sketch, "E29.0.4.6", {"position": v(20.29, 26.55) * mm});
            skLineSegment(sketch, "E29.1.4.6", {"start": v(20.78, 24) * mm, "end": v(16.16, 21.33) * mm, "construction": true});
            skLineSegment(sketch, "E29.4.4.6", {"start": v(23.24, 23.16) * mm, "end": v(25.28, 21.69) * mm});
            skPoint(sketch, "E29.7.4.6", {"position": v(21.28, 26.55) * mm});
            skArc(sketch, "E29.8.4.6", {"start": v(18.33, 23.16) * mm, "mid": v(18.19, 22.5) * mm, "end": v(18.82, 22.3) * mm});
            skLineSegment(sketch, "E29.12.4.6", {"start": v(20.78, 24) * mm, "end": v(20.78, 29.08) * mm, "construction": true});
            skLineSegment(sketch, "E29.15.4.6", {"start": v(20.78, 24) * mm, "end": v(25.18, 21.46) * mm, "construction": true});
            skLineSegment(sketch, "E29.18.4.6", {"start": v(20.29, 26.55) * mm, "end": v(20.54, 29.05) * mm});
            skLineSegment(sketch, "E29.21.4.6", {"start": v(20.78, 24) * mm, "end": v(25.41, 21.33) * mm, "construction": true});
            skPoint(sketch, "E29.24.4.6", {"position": v(23.24, 23.16) * mm});
            skPoint(sketch, "E29.25.4.6", {"position": v(18.33, 23.16) * mm});
            skPoint(sketch, "E29.26.4.6", {"position": v(20.78, 24) * mm});
            skLineSegment(sketch, "E29.27.4.6", {"start": v(20.78, 24) * mm, "end": v(16.38, 21.46) * mm, "construction": true});
            skArc(sketch, "E29.30.4.6", {"start": v(22.74, 22.3) * mm, "mid": v(23.38, 22.5) * mm, "end": v(23.24, 23.16) * mm});
            skPoint(sketch, "E29.34.4.6", {"position": v(18.82, 22.3) * mm});
            skLineSegment(sketch, "E29.35.4.6", {"start": v(18.82, 22.3) * mm, "end": v(16.53, 21.26) * mm});
            skLineSegment(sketch, "E29.38.4.6", {"start": v(18.33, 23.16) * mm, "end": v(16.29, 21.69) * mm});
            skPoint(sketch, "E29.41.4.6", {"position": v(22.74, 22.3) * mm});
            skLineSegment(sketch, "E29.42.4.6", {"start": v(21.28, 26.55) * mm, "end": v(21.03, 29.05) * mm});
            skLineSegment(sketch, "E29.45.4.6", {"start": v(22.74, 22.3) * mm, "end": v(25.03, 21.26) * mm});
            skArc(sketch, "E29.48.4.6", {"start": v(21.28, 26.55) * mm, "mid": v(20.78, 27) * mm, "end": v(20.29, 26.55) * mm});
            skPoint(sketch, "E29.52.4.6", {"position": v(22.74, 22.3) * mm});
            skPoint(sketch, "E29.53.4.6", {"position": v(21.28, 26.55) * mm});
            skPoint(sketch, "E29.54.4.6", {"position": v(18.33, 23.16) * mm});
            skArc(sketch, "E29.55.4.6", {"start": v(16.29, 21.69) * mm, "mid": v(16.38, 21.46) * mm, "end": v(16.53, 21.26) * mm});
            skArc(sketch, "E29.59.4.6", {"start": v(25.03, 21.26) * mm, "mid": v(25.18, 21.46) * mm, "end": v(25.28, 21.69) * mm});
            skArc(sketch, "E29.63.4.6", {"start": v(21.03, 29.05) * mm, "mid": v(20.78, 29.08) * mm, "end": v(20.54, 29.05) * mm});
            skLineSegment(sketch, "E29.67.4.6", {"start": v(20.78, 24) * mm, "end": v(20.78, 29.34) * mm, "construction": true});
            skPoint(sketch, "E29.0.4.7", {"position": v(20.29, 32.55) * mm});
            skLineSegment(sketch, "E29.1.4.7", {"start": v(20.78, 30) * mm, "end": v(16.16, 27.33) * mm, "construction": true});
            skLineSegment(sketch, "E29.4.4.7", {"start": v(23.24, 29.16) * mm, "end": v(25.28, 27.69) * mm});
            skPoint(sketch, "E29.7.4.7", {"position": v(21.28, 32.55) * mm});
            skArc(sketch, "E29.8.4.7", {"start": v(18.33, 29.16) * mm, "mid": v(18.19, 28.5) * mm, "end": v(18.82, 28.3) * mm});
            skLineSegment(sketch, "E29.12.4.7", {"start": v(20.78, 30) * mm, "end": v(20.78, 35.08) * mm, "construction": true});
            skLineSegment(sketch, "E29.15.4.7", {"start": v(20.78, 30) * mm, "end": v(25.18, 27.46) * mm, "construction": true});
            skLineSegment(sketch, "E29.18.4.7", {"start": v(20.29, 32.55) * mm, "end": v(20.54, 35.05) * mm});
            skLineSegment(sketch, "E29.21.4.7", {"start": v(20.78, 30) * mm, "end": v(25.41, 27.33) * mm, "construction": true});
            skPoint(sketch, "E29.24.4.7", {"position": v(23.24, 29.16) * mm});
            skPoint(sketch, "E29.25.4.7", {"position": v(18.33, 29.16) * mm});
            skPoint(sketch, "E29.26.4.7", {"position": v(20.78, 30) * mm});
            skLineSegment(sketch, "E29.27.4.7", {"start": v(20.78, 30) * mm, "end": v(16.38, 27.46) * mm, "construction": true});
            skArc(sketch, "E29.30.4.7", {"start": v(22.74, 28.3) * mm, "mid": v(23.38, 28.5) * mm, "end": v(23.24, 29.16) * mm});
            skPoint(sketch, "E29.34.4.7", {"position": v(18.82, 28.3) * mm});
            skLineSegment(sketch, "E29.35.4.7", {"start": v(18.82, 28.3) * mm, "end": v(16.53, 27.26) * mm});
            skLineSegment(sketch, "E29.38.4.7", {"start": v(18.33, 29.16) * mm, "end": v(16.29, 27.69) * mm});
            skPoint(sketch, "E29.41.4.7", {"position": v(22.74, 28.3) * mm});
            skLineSegment(sketch, "E29.42.4.7", {"start": v(21.28, 32.55) * mm, "end": v(21.03, 35.05) * mm});
            skLineSegment(sketch, "E29.45.4.7", {"start": v(22.74, 28.3) * mm, "end": v(25.03, 27.26) * mm});
            skArc(sketch, "E29.48.4.7", {"start": v(21.28, 32.55) * mm, "mid": v(20.78, 33) * mm, "end": v(20.29, 32.55) * mm});
            skPoint(sketch, "E29.52.4.7", {"position": v(22.74, 28.3) * mm});
            skPoint(sketch, "E29.53.4.7", {"position": v(21.28, 32.55) * mm});
            skPoint(sketch, "E29.54.4.7", {"position": v(18.33, 29.16) * mm});
            skArc(sketch, "E29.55.4.7", {"start": v(16.29, 27.69) * mm, "mid": v(16.38, 27.46) * mm, "end": v(16.53, 27.26) * mm});
            skArc(sketch, "E29.59.4.7", {"start": v(25.03, 27.26) * mm, "mid": v(25.18, 27.46) * mm, "end": v(25.28, 27.69) * mm});
            skArc(sketch, "E29.63.4.7", {"start": v(21.03, 35.05) * mm, "mid": v(20.78, 35.08) * mm, "end": v(20.54, 35.05) * mm});
            skLineSegment(sketch, "E29.67.4.7", {"start": v(20.78, 30) * mm, "end": v(20.78, 35.34) * mm, "construction": true});
            skPoint(sketch, "E29.0.5.2", {"position": v(25.48, -0.45) * mm});
            skLineSegment(sketch, "E29.1.5.2", {"start": v(25.98, -3) * mm, "end": v(21.35, -5.67) * mm, "construction": true});
            skLineSegment(sketch, "E29.4.5.2", {"start": v(28.44, -3.84) * mm, "end": v(30.48, -5.31) * mm});
            skPoint(sketch, "E29.7.5.2", {"position": v(26.48, -0.45) * mm});
            skArc(sketch, "E29.8.5.2", {"start": v(23.52, -3.84) * mm, "mid": v(23.38, -4.5) * mm, "end": v(24.02, -4.7) * mm});
            skLineSegment(sketch, "E29.12.5.2", {"start": v(25.98, -3) * mm, "end": v(25.98, 2.08) * mm, "construction": true});
            skLineSegment(sketch, "E29.15.5.2", {"start": v(25.98, -3) * mm, "end": v(30.38, -5.54) * mm, "construction": true});
            skLineSegment(sketch, "E29.18.5.2", {"start": v(25.48, -0.45) * mm, "end": v(25.73, 2.05) * mm});
            skLineSegment(sketch, "E29.21.5.2", {"start": v(25.98, -3) * mm, "end": v(30.6, -5.67) * mm, "construction": true});
            skPoint(sketch, "E29.24.5.2", {"position": v(28.44, -3.84) * mm});
            skPoint(sketch, "E29.25.5.2", {"position": v(23.52, -3.84) * mm});
            skPoint(sketch, "E29.26.5.2", {"position": v(25.98, -3) * mm});
            skLineSegment(sketch, "E29.27.5.2", {"start": v(25.98, -3) * mm, "end": v(21.58, -5.54) * mm, "construction": true});
            skArc(sketch, "E29.30.5.2", {"start": v(27.94, -4.7) * mm, "mid": v(28.58, -4.5) * mm, "end": v(28.44, -3.84) * mm});
            skPoint(sketch, "E29.34.5.2", {"position": v(24.02, -4.7) * mm});
            skLineSegment(sketch, "E29.35.5.2", {"start": v(24.02, -4.7) * mm, "end": v(21.73, -5.74) * mm});
            skLineSegment(sketch, "E29.38.5.2", {"start": v(23.52, -3.84) * mm, "end": v(21.48, -5.31) * mm});
            skPoint(sketch, "E29.41.5.2", {"position": v(27.94, -4.7) * mm});
            skLineSegment(sketch, "E29.42.5.2", {"start": v(26.48, -0.45) * mm, "end": v(26.23, 2.05) * mm});
            skLineSegment(sketch, "E29.45.5.2", {"start": v(27.94, -4.7) * mm, "end": v(30.23, -5.74) * mm});
            skArc(sketch, "E29.48.5.2", {"start": v(26.48, -0.45) * mm, "mid": v(25.98, 0) * mm, "end": v(25.48, -0.45) * mm});
            skPoint(sketch, "E29.52.5.2", {"position": v(27.94, -4.7) * mm});
            skPoint(sketch, "E29.53.5.2", {"position": v(26.48, -0.45) * mm});
            skPoint(sketch, "E29.54.5.2", {"position": v(23.52, -3.84) * mm});
            skArc(sketch, "E29.55.5.2", {"start": v(21.48, -5.31) * mm, "mid": v(21.58, -5.54) * mm, "end": v(21.73, -5.74) * mm});
            skArc(sketch, "E29.59.5.2", {"start": v(30.23, -5.74) * mm, "mid": v(30.38, -5.54) * mm, "end": v(30.48, -5.31) * mm});
            skArc(sketch, "E29.63.5.2", {"start": v(26.23, 2.05) * mm, "mid": v(25.98, 2.08) * mm, "end": v(25.73, 2.05) * mm});
            skLineSegment(sketch, "E29.67.5.2", {"start": v(25.98, -3) * mm, "end": v(25.98, 2.34) * mm, "construction": true});
            skPoint(sketch, "E29.0.5.3", {"position": v(25.48, 5.55) * mm});
            skLineSegment(sketch, "E29.1.5.3", {"start": v(25.98, 3) * mm, "end": v(21.35, 0.33) * mm, "construction": true});
            skLineSegment(sketch, "E29.4.5.3", {"start": v(28.44, 2.16) * mm, "end": v(30.48, 0.69) * mm});
            skPoint(sketch, "E29.7.5.3", {"position": v(26.48, 5.55) * mm});
            skArc(sketch, "E29.8.5.3", {"start": v(23.52, 2.16) * mm, "mid": v(23.38, 1.5) * mm, "end": v(24.02, 1.3) * mm});
            skLineSegment(sketch, "E29.12.5.3", {"start": v(25.98, 3) * mm, "end": v(25.98, 8.08) * mm, "construction": true});
            skLineSegment(sketch, "E29.15.5.3", {"start": v(25.98, 3) * mm, "end": v(30.38, 0.46) * mm, "construction": true});
            skLineSegment(sketch, "E29.18.5.3", {"start": v(25.48, 5.55) * mm, "end": v(25.73, 8.05) * mm});
            skLineSegment(sketch, "E29.21.5.3", {"start": v(25.98, 3) * mm, "end": v(30.6, 0.33) * mm, "construction": true});
            skPoint(sketch, "E29.24.5.3", {"position": v(28.44, 2.16) * mm});
            skPoint(sketch, "E29.25.5.3", {"position": v(23.52, 2.16) * mm});
            skPoint(sketch, "E29.26.5.3", {"position": v(25.98, 3) * mm});
            skLineSegment(sketch, "E29.27.5.3", {"start": v(25.98, 3) * mm, "end": v(21.58, 0.46) * mm, "construction": true});
            skArc(sketch, "E29.30.5.3", {"start": v(27.94, 1.3) * mm, "mid": v(28.58, 1.5) * mm, "end": v(28.44, 2.16) * mm});
            skPoint(sketch, "E29.34.5.3", {"position": v(24.02, 1.3) * mm});
            skLineSegment(sketch, "E29.35.5.3", {"start": v(24.02, 1.3) * mm, "end": v(21.73, 0.26) * mm});
            skLineSegment(sketch, "E29.38.5.3", {"start": v(23.52, 2.16) * mm, "end": v(21.48, 0.69) * mm});
            skPoint(sketch, "E29.41.5.3", {"position": v(27.94, 1.3) * mm});
            skLineSegment(sketch, "E29.42.5.3", {"start": v(26.48, 5.55) * mm, "end": v(26.23, 8.05) * mm});
            skLineSegment(sketch, "E29.45.5.3", {"start": v(27.94, 1.3) * mm, "end": v(30.23, 0.26) * mm});
            skArc(sketch, "E29.48.5.3", {"start": v(26.48, 5.55) * mm, "mid": v(25.98, 6) * mm, "end": v(25.48, 5.55) * mm});
            skPoint(sketch, "E29.52.5.3", {"position": v(27.94, 1.3) * mm});
            skPoint(sketch, "E29.53.5.3", {"position": v(26.48, 5.55) * mm});
            skPoint(sketch, "E29.54.5.3", {"position": v(23.52, 2.16) * mm});
            skArc(sketch, "E29.55.5.3", {"start": v(21.48, 0.69) * mm, "mid": v(21.58, 0.46) * mm, "end": v(21.73, 0.26) * mm});
            skArc(sketch, "E29.59.5.3", {"start": v(30.23, 0.26) * mm, "mid": v(30.38, 0.46) * mm, "end": v(30.48, 0.69) * mm});
            skArc(sketch, "E29.63.5.3", {"start": v(26.23, 8.05) * mm, "mid": v(25.98, 8.08) * mm, "end": v(25.73, 8.05) * mm});
            skLineSegment(sketch, "E29.67.5.3", {"start": v(25.98, 3) * mm, "end": v(25.98, 8.34) * mm, "construction": true});
            skPoint(sketch, "E29.0.5.4", {"position": v(25.48, 11.55) * mm});
            skLineSegment(sketch, "E29.1.5.4", {"start": v(25.98, 9) * mm, "end": v(21.35, 6.33) * mm, "construction": true});
            skLineSegment(sketch, "E29.4.5.4", {"start": v(28.44, 8.16) * mm, "end": v(30.48, 6.69) * mm});
            skPoint(sketch, "E29.7.5.4", {"position": v(26.48, 11.55) * mm});
            skArc(sketch, "E29.8.5.4", {"start": v(23.52, 8.16) * mm, "mid": v(23.38, 7.5) * mm, "end": v(24.02, 7.3) * mm});
            skLineSegment(sketch, "E29.12.5.4", {"start": v(25.98, 9) * mm, "end": v(25.98, 14.08) * mm, "construction": true});
            skLineSegment(sketch, "E29.15.5.4", {"start": v(25.98, 9) * mm, "end": v(30.38, 6.46) * mm, "construction": true});
            skLineSegment(sketch, "E29.18.5.4", {"start": v(25.48, 11.55) * mm, "end": v(25.73, 14.05) * mm});
            skLineSegment(sketch, "E29.21.5.4", {"start": v(25.98, 9) * mm, "end": v(30.6, 6.33) * mm, "construction": true});
            skPoint(sketch, "E29.24.5.4", {"position": v(28.44, 8.16) * mm});
            skPoint(sketch, "E29.25.5.4", {"position": v(23.52, 8.16) * mm});
            skPoint(sketch, "E29.26.5.4", {"position": v(25.98, 9) * mm});
            skLineSegment(sketch, "E29.27.5.4", {"start": v(25.98, 9) * mm, "end": v(21.58, 6.46) * mm, "construction": true});
            skArc(sketch, "E29.30.5.4", {"start": v(27.94, 7.3) * mm, "mid": v(28.58, 7.5) * mm, "end": v(28.44, 8.16) * mm});
            skPoint(sketch, "E29.34.5.4", {"position": v(24.02, 7.3) * mm});
            skLineSegment(sketch, "E29.35.5.4", {"start": v(24.02, 7.3) * mm, "end": v(21.73, 6.26) * mm});
            skLineSegment(sketch, "E29.38.5.4", {"start": v(23.52, 8.16) * mm, "end": v(21.48, 6.69) * mm});
            skPoint(sketch, "E29.41.5.4", {"position": v(27.94, 7.3) * mm});
            skLineSegment(sketch, "E29.42.5.4", {"start": v(26.48, 11.55) * mm, "end": v(26.23, 14.05) * mm});
            skLineSegment(sketch, "E29.45.5.4", {"start": v(27.94, 7.3) * mm, "end": v(30.23, 6.26) * mm});
            skArc(sketch, "E29.48.5.4", {"start": v(26.48, 11.55) * mm, "mid": v(25.98, 12) * mm, "end": v(25.48, 11.55) * mm});
            skPoint(sketch, "E29.52.5.4", {"position": v(27.94, 7.3) * mm});
            skPoint(sketch, "E29.53.5.4", {"position": v(26.48, 11.55) * mm});
            skPoint(sketch, "E29.54.5.4", {"position": v(23.52, 8.16) * mm});
            skArc(sketch, "E29.55.5.4", {"start": v(21.48, 6.69) * mm, "mid": v(21.58, 6.46) * mm, "end": v(21.73, 6.26) * mm});
            skArc(sketch, "E29.59.5.4", {"start": v(30.23, 6.26) * mm, "mid": v(30.38, 6.46) * mm, "end": v(30.48, 6.69) * mm});
            skArc(sketch, "E29.63.5.4", {"start": v(26.23, 14.05) * mm, "mid": v(25.98, 14.08) * mm, "end": v(25.73, 14.05) * mm});
            skLineSegment(sketch, "E29.67.5.4", {"start": v(25.98, 9) * mm, "end": v(25.98, 14.34) * mm, "construction": true});
            skPoint(sketch, "E29.0.5.5", {"position": v(25.48, 17.55) * mm});
            skLineSegment(sketch, "E29.1.5.5", {"start": v(25.98, 15) * mm, "end": v(21.35, 12.33) * mm, "construction": true});
            skLineSegment(sketch, "E29.4.5.5", {"start": v(28.44, 14.16) * mm, "end": v(30.48, 12.69) * mm});
            skPoint(sketch, "E29.7.5.5", {"position": v(26.48, 17.55) * mm});
            skArc(sketch, "E29.8.5.5", {"start": v(23.52, 14.16) * mm, "mid": v(23.38, 13.5) * mm, "end": v(24.02, 13.3) * mm});
            skLineSegment(sketch, "E29.12.5.5", {"start": v(25.98, 15) * mm, "end": v(25.98, 20.08) * mm, "construction": true});
            skLineSegment(sketch, "E29.15.5.5", {"start": v(25.98, 15) * mm, "end": v(30.38, 12.46) * mm, "construction": true});
            skLineSegment(sketch, "E29.18.5.5", {"start": v(25.48, 17.55) * mm, "end": v(25.73, 20.05) * mm});
            skLineSegment(sketch, "E29.21.5.5", {"start": v(25.98, 15) * mm, "end": v(30.6, 12.33) * mm, "construction": true});
            skPoint(sketch, "E29.24.5.5", {"position": v(28.44, 14.16) * mm});
            skPoint(sketch, "E29.25.5.5", {"position": v(23.52, 14.16) * mm});
            skPoint(sketch, "E29.26.5.5", {"position": v(25.98, 15) * mm});
            skLineSegment(sketch, "E29.27.5.5", {"start": v(25.98, 15) * mm, "end": v(21.58, 12.46) * mm, "construction": true});
            skArc(sketch, "E29.30.5.5", {"start": v(27.94, 13.3) * mm, "mid": v(28.58, 13.5) * mm, "end": v(28.44, 14.16) * mm});
            skPoint(sketch, "E29.34.5.5", {"position": v(24.02, 13.3) * mm});
            skLineSegment(sketch, "E29.35.5.5", {"start": v(24.02, 13.3) * mm, "end": v(21.73, 12.26) * mm});
            skLineSegment(sketch, "E29.38.5.5", {"start": v(23.52, 14.16) * mm, "end": v(21.48, 12.69) * mm});
            skPoint(sketch, "E29.41.5.5", {"position": v(27.94, 13.3) * mm});
            skLineSegment(sketch, "E29.42.5.5", {"start": v(26.48, 17.55) * mm, "end": v(26.23, 20.05) * mm});
            skLineSegment(sketch, "E29.45.5.5", {"start": v(27.94, 13.3) * mm, "end": v(30.23, 12.26) * mm});
            skArc(sketch, "E29.48.5.5", {"start": v(26.48, 17.55) * mm, "mid": v(25.98, 18) * mm, "end": v(25.48, 17.55) * mm});
            skPoint(sketch, "E29.52.5.5", {"position": v(27.94, 13.3) * mm});
            skPoint(sketch, "E29.53.5.5", {"position": v(26.48, 17.55) * mm});
            skPoint(sketch, "E29.54.5.5", {"position": v(23.52, 14.16) * mm});
            skArc(sketch, "E29.55.5.5", {"start": v(21.48, 12.69) * mm, "mid": v(21.58, 12.46) * mm, "end": v(21.73, 12.26) * mm});
            skArc(sketch, "E29.59.5.5", {"start": v(30.23, 12.26) * mm, "mid": v(30.38, 12.46) * mm, "end": v(30.48, 12.69) * mm});
            skArc(sketch, "E29.63.5.5", {"start": v(26.23, 20.05) * mm, "mid": v(25.98, 20.08) * mm, "end": v(25.73, 20.05) * mm});
            skLineSegment(sketch, "E29.67.5.5", {"start": v(25.98, 15) * mm, "end": v(25.98, 20.34) * mm, "construction": true});
            skPoint(sketch, "E29.0.5.6", {"position": v(25.48, 23.55) * mm});
            skLineSegment(sketch, "E29.1.5.6", {"start": v(25.98, 21) * mm, "end": v(21.35, 18.33) * mm, "construction": true});
            skLineSegment(sketch, "E29.4.5.6", {"start": v(28.44, 20.16) * mm, "end": v(30.48, 18.69) * mm});
            skPoint(sketch, "E29.7.5.6", {"position": v(26.48, 23.55) * mm});
            skArc(sketch, "E29.8.5.6", {"start": v(23.52, 20.16) * mm, "mid": v(23.38, 19.5) * mm, "end": v(24.02, 19.3) * mm});
            skLineSegment(sketch, "E29.12.5.6", {"start": v(25.98, 21) * mm, "end": v(25.98, 26.08) * mm, "construction": true});
            skLineSegment(sketch, "E29.15.5.6", {"start": v(25.98, 21) * mm, "end": v(30.38, 18.46) * mm, "construction": true});
            skLineSegment(sketch, "E29.18.5.6", {"start": v(25.48, 23.55) * mm, "end": v(25.73, 26.05) * mm});
            skLineSegment(sketch, "E29.21.5.6", {"start": v(25.98, 21) * mm, "end": v(30.6, 18.33) * mm, "construction": true});
            skPoint(sketch, "E29.24.5.6", {"position": v(28.44, 20.16) * mm});
            skPoint(sketch, "E29.25.5.6", {"position": v(23.52, 20.16) * mm});
            skPoint(sketch, "E29.26.5.6", {"position": v(25.98, 21) * mm});
            skLineSegment(sketch, "E29.27.5.6", {"start": v(25.98, 21) * mm, "end": v(21.58, 18.46) * mm, "construction": true});
            skArc(sketch, "E29.30.5.6", {"start": v(27.94, 19.3) * mm, "mid": v(28.58, 19.5) * mm, "end": v(28.44, 20.16) * mm});
            skPoint(sketch, "E29.34.5.6", {"position": v(24.02, 19.3) * mm});
            skLineSegment(sketch, "E29.35.5.6", {"start": v(24.02, 19.3) * mm, "end": v(21.73, 18.26) * mm});
            skLineSegment(sketch, "E29.38.5.6", {"start": v(23.52, 20.16) * mm, "end": v(21.48, 18.69) * mm});
            skPoint(sketch, "E29.41.5.6", {"position": v(27.94, 19.3) * mm});
            skLineSegment(sketch, "E29.42.5.6", {"start": v(26.48, 23.55) * mm, "end": v(26.23, 26.05) * mm});
            skLineSegment(sketch, "E29.45.5.6", {"start": v(27.94, 19.3) * mm, "end": v(30.23, 18.26) * mm});
            skArc(sketch, "E29.48.5.6", {"start": v(26.48, 23.55) * mm, "mid": v(25.98, 24) * mm, "end": v(25.48, 23.55) * mm});
            skPoint(sketch, "E29.52.5.6", {"position": v(27.94, 19.3) * mm});
            skPoint(sketch, "E29.53.5.6", {"position": v(26.48, 23.55) * mm});
            skPoint(sketch, "E29.54.5.6", {"position": v(23.52, 20.16) * mm});
            skArc(sketch, "E29.55.5.6", {"start": v(21.48, 18.69) * mm, "mid": v(21.58, 18.46) * mm, "end": v(21.73, 18.26) * mm});
            skArc(sketch, "E29.59.5.6", {"start": v(30.23, 18.26) * mm, "mid": v(30.38, 18.46) * mm, "end": v(30.48, 18.69) * mm});
            skArc(sketch, "E29.63.5.6", {"start": v(26.23, 26.05) * mm, "mid": v(25.98, 26.08) * mm, "end": v(25.73, 26.05) * mm});
            skLineSegment(sketch, "E29.67.5.6", {"start": v(25.98, 21) * mm, "end": v(25.98, 26.34) * mm, "construction": true});
            skPoint(sketch, "E29.0.5.7", {"position": v(25.48, 29.55) * mm});
            skLineSegment(sketch, "E29.1.5.7", {"start": v(25.98, 27) * mm, "end": v(21.35, 24.33) * mm, "construction": true});
            skLineSegment(sketch, "E29.4.5.7", {"start": v(28.44, 26.16) * mm, "end": v(30.48, 24.69) * mm});
            skPoint(sketch, "E29.7.5.7", {"position": v(26.48, 29.55) * mm});
            skArc(sketch, "E29.8.5.7", {"start": v(23.52, 26.16) * mm, "mid": v(23.38, 25.5) * mm, "end": v(24.02, 25.3) * mm});
            skLineSegment(sketch, "E29.12.5.7", {"start": v(25.98, 27) * mm, "end": v(25.98, 32.08) * mm, "construction": true});
            skLineSegment(sketch, "E29.15.5.7", {"start": v(25.98, 27) * mm, "end": v(30.38, 24.46) * mm, "construction": true});
            skLineSegment(sketch, "E29.18.5.7", {"start": v(25.48, 29.55) * mm, "end": v(25.73, 32.05) * mm});
            skLineSegment(sketch, "E29.21.5.7", {"start": v(25.98, 27) * mm, "end": v(30.6, 24.33) * mm, "construction": true});
            skPoint(sketch, "E29.24.5.7", {"position": v(28.44, 26.16) * mm});
            skPoint(sketch, "E29.25.5.7", {"position": v(23.52, 26.16) * mm});
            skPoint(sketch, "E29.26.5.7", {"position": v(25.98, 27) * mm});
            skLineSegment(sketch, "E29.27.5.7", {"start": v(25.98, 27) * mm, "end": v(21.58, 24.46) * mm, "construction": true});
            skArc(sketch, "E29.30.5.7", {"start": v(27.94, 25.3) * mm, "mid": v(28.58, 25.5) * mm, "end": v(28.44, 26.16) * mm});
            skPoint(sketch, "E29.34.5.7", {"position": v(24.02, 25.3) * mm});
            skLineSegment(sketch, "E29.35.5.7", {"start": v(24.02, 25.3) * mm, "end": v(21.73, 24.26) * mm});
            skLineSegment(sketch, "E29.38.5.7", {"start": v(23.52, 26.16) * mm, "end": v(21.48, 24.69) * mm});
            skPoint(sketch, "E29.41.5.7", {"position": v(27.94, 25.3) * mm});
            skLineSegment(sketch, "E29.42.5.7", {"start": v(26.48, 29.55) * mm, "end": v(26.23, 32.05) * mm});
            skLineSegment(sketch, "E29.45.5.7", {"start": v(27.94, 25.3) * mm, "end": v(30.23, 24.26) * mm});
            skArc(sketch, "E29.48.5.7", {"start": v(26.48, 29.55) * mm, "mid": v(25.98, 30) * mm, "end": v(25.48, 29.55) * mm});
            skPoint(sketch, "E29.52.5.7", {"position": v(27.94, 25.3) * mm});
            skPoint(sketch, "E29.53.5.7", {"position": v(26.48, 29.55) * mm});
            skPoint(sketch, "E29.54.5.7", {"position": v(23.52, 26.16) * mm});
            skArc(sketch, "E29.55.5.7", {"start": v(21.48, 24.69) * mm, "mid": v(21.58, 24.46) * mm, "end": v(21.73, 24.26) * mm});
            skArc(sketch, "E29.59.5.7", {"start": v(30.23, 24.26) * mm, "mid": v(30.38, 24.46) * mm, "end": v(30.48, 24.69) * mm});
            skArc(sketch, "E29.63.5.7", {"start": v(26.23, 32.05) * mm, "mid": v(25.98, 32.08) * mm, "end": v(25.73, 32.05) * mm});
            skLineSegment(sketch, "E29.67.5.7", {"start": v(25.98, 27) * mm, "end": v(25.98, 32.34) * mm, "construction": true});
            skPoint(sketch, "E29.0.6.2", {"position": v(30.68, -3.45) * mm});
            skLineSegment(sketch, "E29.1.6.2", {"start": v(31.18, -6) * mm, "end": v(26.55, -8.67) * mm, "construction": true});
            skLineSegment(sketch, "E29.4.6.2", {"start": v(33.63, -6.84) * mm, "end": v(35.67, -8.31) * mm});
            skPoint(sketch, "E29.7.6.2", {"position": v(31.67, -3.45) * mm});
            skArc(sketch, "E29.8.6.2", {"start": v(28.72, -6.84) * mm, "mid": v(28.58, -7.5) * mm, "end": v(29.22, -7.7) * mm});
            skLineSegment(sketch, "E29.12.6.2", {"start": v(31.18, -6) * mm, "end": v(31.18, -0.92) * mm, "construction": true});
            skLineSegment(sketch, "E29.15.6.2", {"start": v(31.18, -6) * mm, "end": v(35.58, -8.54) * mm, "construction": true});
            skLineSegment(sketch, "E29.18.6.2", {"start": v(30.68, -3.45) * mm, "end": v(30.93, -0.95) * mm});
            skLineSegment(sketch, "E29.21.6.2", {"start": v(31.18, -6) * mm, "end": v(35.8, -8.67) * mm, "construction": true});
            skPoint(sketch, "E29.24.6.2", {"position": v(33.63, -6.84) * mm});
            skPoint(sketch, "E29.25.6.2", {"position": v(28.72, -6.84) * mm});
            skPoint(sketch, "E29.26.6.2", {"position": v(31.18, -6) * mm});
            skLineSegment(sketch, "E29.27.6.2", {"start": v(31.18, -6) * mm, "end": v(26.78, -8.54) * mm, "construction": true});
            skArc(sketch, "E29.30.6.2", {"start": v(33.14, -7.7) * mm, "mid": v(33.77, -7.5) * mm, "end": v(33.63, -6.84) * mm});
            skPoint(sketch, "E29.34.6.2", {"position": v(29.22, -7.7) * mm});
            skLineSegment(sketch, "E29.35.6.2", {"start": v(29.22, -7.7) * mm, "end": v(26.93, -8.74) * mm});
            skLineSegment(sketch, "E29.38.6.2", {"start": v(28.72, -6.84) * mm, "end": v(26.68, -8.31) * mm});
            skPoint(sketch, "E29.41.6.2", {"position": v(33.14, -7.7) * mm});
            skLineSegment(sketch, "E29.42.6.2", {"start": v(31.67, -3.45) * mm, "end": v(31.42, -0.95) * mm});
            skLineSegment(sketch, "E29.45.6.2", {"start": v(33.14, -7.7) * mm, "end": v(35.43, -8.74) * mm});
            skArc(sketch, "E29.48.6.2", {"start": v(31.67, -3.45) * mm, "mid": v(31.18, -3) * mm, "end": v(30.68, -3.45) * mm});
            skPoint(sketch, "E29.52.6.2", {"position": v(33.14, -7.7) * mm});
            skPoint(sketch, "E29.53.6.2", {"position": v(31.67, -3.45) * mm});
            skPoint(sketch, "E29.54.6.2", {"position": v(28.72, -6.84) * mm});
            skArc(sketch, "E29.55.6.2", {"start": v(26.68, -8.31) * mm, "mid": v(26.78, -8.54) * mm, "end": v(26.93, -8.74) * mm});
            skArc(sketch, "E29.59.6.2", {"start": v(35.43, -8.74) * mm, "mid": v(35.58, -8.54) * mm, "end": v(35.67, -8.31) * mm});
            skArc(sketch, "E29.63.6.2", {"start": v(31.42, -0.95) * mm, "mid": v(31.18, -0.92) * mm, "end": v(30.93, -0.95) * mm});
            skLineSegment(sketch, "E29.67.6.2", {"start": v(31.18, -6) * mm, "end": v(31.18, -0.66) * mm, "construction": true});
            skPoint(sketch, "E29.0.6.3", {"position": v(30.68, 2.55) * mm});
            skLineSegment(sketch, "E29.1.6.3", {"start": v(31.18, 0) * mm, "end": v(26.55, -2.67) * mm, "construction": true});
            skLineSegment(sketch, "E29.4.6.3", {"start": v(33.63, -0.84) * mm, "end": v(35.67, -2.31) * mm});
            skPoint(sketch, "E29.7.6.3", {"position": v(31.67, 2.55) * mm});
            skArc(sketch, "E29.8.6.3", {"start": v(28.72, -0.84) * mm, "mid": v(28.58, -1.5) * mm, "end": v(29.22, -1.7) * mm});
            skLineSegment(sketch, "E29.12.6.3", {"start": v(31.18, 0) * mm, "end": v(31.18, 5.08) * mm, "construction": true});
            skLineSegment(sketch, "E29.15.6.3", {"start": v(31.18, 0) * mm, "end": v(35.58, -2.54) * mm, "construction": true});
            skLineSegment(sketch, "E29.18.6.3", {"start": v(30.68, 2.55) * mm, "end": v(30.93, 5.05) * mm});
            skLineSegment(sketch, "E29.21.6.3", {"start": v(31.18, 0) * mm, "end": v(35.8, -2.67) * mm, "construction": true});
            skPoint(sketch, "E29.24.6.3", {"position": v(33.63, -0.84) * mm});
            skPoint(sketch, "E29.25.6.3", {"position": v(28.72, -0.84) * mm});
            skPoint(sketch, "E29.26.6.3", {"position": v(31.18, 0) * mm});
            skLineSegment(sketch, "E29.27.6.3", {"start": v(31.18, 0) * mm, "end": v(26.78, -2.54) * mm, "construction": true});
            skArc(sketch, "E29.30.6.3", {"start": v(33.14, -1.7) * mm, "mid": v(33.77, -1.5) * mm, "end": v(33.63, -0.84) * mm});
            skPoint(sketch, "E29.34.6.3", {"position": v(29.22, -1.7) * mm});
            skLineSegment(sketch, "E29.35.6.3", {"start": v(29.22, -1.7) * mm, "end": v(26.93, -2.74) * mm});
            skLineSegment(sketch, "E29.38.6.3", {"start": v(28.72, -0.84) * mm, "end": v(26.68, -2.31) * mm});
            skPoint(sketch, "E29.41.6.3", {"position": v(33.14, -1.7) * mm});
            skLineSegment(sketch, "E29.42.6.3", {"start": v(31.67, 2.55) * mm, "end": v(31.42, 5.05) * mm});
            skLineSegment(sketch, "E29.45.6.3", {"start": v(33.14, -1.7) * mm, "end": v(35.43, -2.74) * mm});
            skArc(sketch, "E29.48.6.3", {"start": v(31.67, 2.55) * mm, "mid": v(31.18, 3) * mm, "end": v(30.68, 2.55) * mm});
            skPoint(sketch, "E29.52.6.3", {"position": v(33.14, -1.7) * mm});
            skPoint(sketch, "E29.53.6.3", {"position": v(31.67, 2.55) * mm});
            skPoint(sketch, "E29.54.6.3", {"position": v(28.72, -0.84) * mm});
            skArc(sketch, "E29.55.6.3", {"start": v(26.68, -2.31) * mm, "mid": v(26.78, -2.54) * mm, "end": v(26.93, -2.74) * mm});
            skArc(sketch, "E29.59.6.3", {"start": v(35.43, -2.74) * mm, "mid": v(35.58, -2.54) * mm, "end": v(35.67, -2.31) * mm});
            skArc(sketch, "E29.63.6.3", {"start": v(31.42, 5.05) * mm, "mid": v(31.18, 5.08) * mm, "end": v(30.93, 5.05) * mm});
            skLineSegment(sketch, "E29.67.6.3", {"start": v(31.18, 0) * mm, "end": v(31.18, 5.34) * mm, "construction": true});
            skPoint(sketch, "E29.0.6.4", {"position": v(30.68, 8.55) * mm});
            skLineSegment(sketch, "E29.1.6.4", {"start": v(31.18, 6) * mm, "end": v(26.55, 3.33) * mm, "construction": true});
            skLineSegment(sketch, "E29.4.6.4", {"start": v(33.63, 5.16) * mm, "end": v(35.67, 3.69) * mm});
            skPoint(sketch, "E29.7.6.4", {"position": v(31.67, 8.55) * mm});
            skArc(sketch, "E29.8.6.4", {"start": v(28.72, 5.16) * mm, "mid": v(28.58, 4.5) * mm, "end": v(29.22, 4.3) * mm});
            skLineSegment(sketch, "E29.12.6.4", {"start": v(31.18, 6) * mm, "end": v(31.18, 11.08) * mm, "construction": true});
            skLineSegment(sketch, "E29.15.6.4", {"start": v(31.18, 6) * mm, "end": v(35.58, 3.46) * mm, "construction": true});
            skLineSegment(sketch, "E29.18.6.4", {"start": v(30.68, 8.55) * mm, "end": v(30.93, 11.05) * mm});
            skLineSegment(sketch, "E29.21.6.4", {"start": v(31.18, 6) * mm, "end": v(35.8, 3.33) * mm, "construction": true});
            skPoint(sketch, "E29.24.6.4", {"position": v(33.63, 5.16) * mm});
            skPoint(sketch, "E29.25.6.4", {"position": v(28.72, 5.16) * mm});
            skPoint(sketch, "E29.26.6.4", {"position": v(31.18, 6) * mm});
            skLineSegment(sketch, "E29.27.6.4", {"start": v(31.18, 6) * mm, "end": v(26.78, 3.46) * mm, "construction": true});
            skArc(sketch, "E29.30.6.4", {"start": v(33.14, 4.3) * mm, "mid": v(33.77, 4.5) * mm, "end": v(33.63, 5.16) * mm});
            skPoint(sketch, "E29.34.6.4", {"position": v(29.22, 4.3) * mm});
            skLineSegment(sketch, "E29.35.6.4", {"start": v(29.22, 4.3) * mm, "end": v(26.93, 3.26) * mm});
            skLineSegment(sketch, "E29.38.6.4", {"start": v(28.72, 5.16) * mm, "end": v(26.68, 3.69) * mm});
            skPoint(sketch, "E29.41.6.4", {"position": v(33.14, 4.3) * mm});
            skLineSegment(sketch, "E29.42.6.4", {"start": v(31.67, 8.55) * mm, "end": v(31.42, 11.05) * mm});
            skLineSegment(sketch, "E29.45.6.4", {"start": v(33.14, 4.3) * mm, "end": v(35.43, 3.26) * mm});
            skArc(sketch, "E29.48.6.4", {"start": v(31.67, 8.55) * mm, "mid": v(31.18, 9) * mm, "end": v(30.68, 8.55) * mm});
            skPoint(sketch, "E29.52.6.4", {"position": v(33.14, 4.3) * mm});
            skPoint(sketch, "E29.53.6.4", {"position": v(31.67, 8.55) * mm});
            skPoint(sketch, "E29.54.6.4", {"position": v(28.72, 5.16) * mm});
            skArc(sketch, "E29.55.6.4", {"start": v(26.68, 3.69) * mm, "mid": v(26.78, 3.46) * mm, "end": v(26.93, 3.26) * mm});
            skArc(sketch, "E29.59.6.4", {"start": v(35.43, 3.26) * mm, "mid": v(35.58, 3.46) * mm, "end": v(35.67, 3.69) * mm});
            skArc(sketch, "E29.63.6.4", {"start": v(31.42, 11.05) * mm, "mid": v(31.18, 11.08) * mm, "end": v(30.93, 11.05) * mm});
            skLineSegment(sketch, "E29.67.6.4", {"start": v(31.18, 6) * mm, "end": v(31.18, 11.34) * mm, "construction": true});
            skPoint(sketch, "E29.0.6.5", {"position": v(30.68, 14.55) * mm});
            skLineSegment(sketch, "E29.1.6.5", {"start": v(31.18, 12) * mm, "end": v(26.55, 9.33) * mm, "construction": true});
            skLineSegment(sketch, "E29.4.6.5", {"start": v(33.63, 11.16) * mm, "end": v(35.67, 9.69) * mm});
            skPoint(sketch, "E29.7.6.5", {"position": v(31.67, 14.55) * mm});
            skArc(sketch, "E29.8.6.5", {"start": v(28.72, 11.16) * mm, "mid": v(28.58, 10.5) * mm, "end": v(29.22, 10.3) * mm});
            skLineSegment(sketch, "E29.12.6.5", {"start": v(31.18, 12) * mm, "end": v(31.18, 17.08) * mm, "construction": true});
            skLineSegment(sketch, "E29.15.6.5", {"start": v(31.18, 12) * mm, "end": v(35.58, 9.46) * mm, "construction": true});
            skLineSegment(sketch, "E29.18.6.5", {"start": v(30.68, 14.55) * mm, "end": v(30.93, 17.05) * mm});
            skLineSegment(sketch, "E29.21.6.5", {"start": v(31.18, 12) * mm, "end": v(35.8, 9.33) * mm, "construction": true});
            skPoint(sketch, "E29.24.6.5", {"position": v(33.63, 11.16) * mm});
            skPoint(sketch, "E29.25.6.5", {"position": v(28.72, 11.16) * mm});
            skPoint(sketch, "E29.26.6.5", {"position": v(31.18, 12) * mm});
            skLineSegment(sketch, "E29.27.6.5", {"start": v(31.18, 12) * mm, "end": v(26.78, 9.46) * mm, "construction": true});
            skArc(sketch, "E29.30.6.5", {"start": v(33.14, 10.3) * mm, "mid": v(33.77, 10.5) * mm, "end": v(33.63, 11.16) * mm});
            skPoint(sketch, "E29.34.6.5", {"position": v(29.22, 10.3) * mm});
            skLineSegment(sketch, "E29.35.6.5", {"start": v(29.22, 10.3) * mm, "end": v(26.93, 9.26) * mm});
            skLineSegment(sketch, "E29.38.6.5", {"start": v(28.72, 11.16) * mm, "end": v(26.68, 9.69) * mm});
            skPoint(sketch, "E29.41.6.5", {"position": v(33.14, 10.3) * mm});
            skLineSegment(sketch, "E29.42.6.5", {"start": v(31.67, 14.55) * mm, "end": v(31.42, 17.05) * mm});
            skLineSegment(sketch, "E29.45.6.5", {"start": v(33.14, 10.3) * mm, "end": v(35.43, 9.26) * mm});
            skArc(sketch, "E29.48.6.5", {"start": v(31.67, 14.55) * mm, "mid": v(31.18, 15) * mm, "end": v(30.68, 14.55) * mm});
            skPoint(sketch, "E29.52.6.5", {"position": v(33.14, 10.3) * mm});
            skPoint(sketch, "E29.53.6.5", {"position": v(31.67, 14.55) * mm});
            skPoint(sketch, "E29.54.6.5", {"position": v(28.72, 11.16) * mm});
            skArc(sketch, "E29.55.6.5", {"start": v(26.68, 9.69) * mm, "mid": v(26.78, 9.46) * mm, "end": v(26.93, 9.26) * mm});
            skArc(sketch, "E29.59.6.5", {"start": v(35.43, 9.26) * mm, "mid": v(35.58, 9.46) * mm, "end": v(35.67, 9.69) * mm});
            skArc(sketch, "E29.63.6.5", {"start": v(31.42, 17.05) * mm, "mid": v(31.18, 17.08) * mm, "end": v(30.93, 17.05) * mm});
            skLineSegment(sketch, "E29.67.6.5", {"start": v(31.18, 12) * mm, "end": v(31.18, 17.34) * mm, "construction": true});
            skPoint(sketch, "E29.0.6.6", {"position": v(30.68, 20.55) * mm});
            skLineSegment(sketch, "E29.1.6.6", {"start": v(31.18, 18) * mm, "end": v(26.55, 15.33) * mm, "construction": true});
            skLineSegment(sketch, "E29.4.6.6", {"start": v(33.63, 17.16) * mm, "end": v(35.67, 15.69) * mm});
            skPoint(sketch, "E29.7.6.6", {"position": v(31.67, 20.55) * mm});
            skArc(sketch, "E29.8.6.6", {"start": v(28.72, 17.16) * mm, "mid": v(28.58, 16.5) * mm, "end": v(29.22, 16.3) * mm});
            skLineSegment(sketch, "E29.12.6.6", {"start": v(31.18, 18) * mm, "end": v(31.18, 23.08) * mm, "construction": true});
            skLineSegment(sketch, "E29.15.6.6", {"start": v(31.18, 18) * mm, "end": v(35.58, 15.46) * mm, "construction": true});
            skLineSegment(sketch, "E29.18.6.6", {"start": v(30.68, 20.55) * mm, "end": v(30.93, 23.05) * mm});
            skLineSegment(sketch, "E29.21.6.6", {"start": v(31.18, 18) * mm, "end": v(35.8, 15.33) * mm, "construction": true});
            skPoint(sketch, "E29.24.6.6", {"position": v(33.63, 17.16) * mm});
            skPoint(sketch, "E29.25.6.6", {"position": v(28.72, 17.16) * mm});
            skPoint(sketch, "E29.26.6.6", {"position": v(31.18, 18) * mm});
            skLineSegment(sketch, "E29.27.6.6", {"start": v(31.18, 18) * mm, "end": v(26.78, 15.46) * mm, "construction": true});
            skArc(sketch, "E29.30.6.6", {"start": v(33.14, 16.3) * mm, "mid": v(33.77, 16.5) * mm, "end": v(33.63, 17.16) * mm});
            skPoint(sketch, "E29.34.6.6", {"position": v(29.22, 16.3) * mm});
            skLineSegment(sketch, "E29.35.6.6", {"start": v(29.22, 16.3) * mm, "end": v(26.93, 15.26) * mm});
            skLineSegment(sketch, "E29.38.6.6", {"start": v(28.72, 17.16) * mm, "end": v(26.68, 15.69) * mm});
            skPoint(sketch, "E29.41.6.6", {"position": v(33.14, 16.3) * mm});
            skLineSegment(sketch, "E29.42.6.6", {"start": v(31.67, 20.55) * mm, "end": v(31.42, 23.05) * mm});
            skLineSegment(sketch, "E29.45.6.6", {"start": v(33.14, 16.3) * mm, "end": v(35.43, 15.26) * mm});
            skArc(sketch, "E29.48.6.6", {"start": v(31.67, 20.55) * mm, "mid": v(31.18, 21) * mm, "end": v(30.68, 20.55) * mm});
            skPoint(sketch, "E29.52.6.6", {"position": v(33.14, 16.3) * mm});
            skPoint(sketch, "E29.53.6.6", {"position": v(31.67, 20.55) * mm});
            skPoint(sketch, "E29.54.6.6", {"position": v(28.72, 17.16) * mm});
            skArc(sketch, "E29.55.6.6", {"start": v(26.68, 15.69) * mm, "mid": v(26.78, 15.46) * mm, "end": v(26.93, 15.26) * mm});
            skArc(sketch, "E29.59.6.6", {"start": v(35.43, 15.26) * mm, "mid": v(35.58, 15.46) * mm, "end": v(35.67, 15.69) * mm});
            skArc(sketch, "E29.63.6.6", {"start": v(31.42, 23.05) * mm, "mid": v(31.18, 23.08) * mm, "end": v(30.93, 23.05) * mm});
            skLineSegment(sketch, "E29.67.6.6", {"start": v(31.18, 18) * mm, "end": v(31.18, 23.34) * mm, "construction": true});
            skPoint(sketch, "E29.0.6.7", {"position": v(30.68, 26.55) * mm});
            skLineSegment(sketch, "E29.1.6.7", {"start": v(31.18, 24) * mm, "end": v(26.55, 21.33) * mm, "construction": true});
            skLineSegment(sketch, "E29.4.6.7", {"start": v(33.63, 23.16) * mm, "end": v(35.67, 21.69) * mm});
            skPoint(sketch, "E29.7.6.7", {"position": v(31.67, 26.55) * mm});
            skArc(sketch, "E29.8.6.7", {"start": v(28.72, 23.16) * mm, "mid": v(28.58, 22.5) * mm, "end": v(29.22, 22.3) * mm});
            skLineSegment(sketch, "E29.12.6.7", {"start": v(31.18, 24) * mm, "end": v(31.18, 29.08) * mm, "construction": true});
            skLineSegment(sketch, "E29.15.6.7", {"start": v(31.18, 24) * mm, "end": v(35.58, 21.46) * mm, "construction": true});
            skLineSegment(sketch, "E29.18.6.7", {"start": v(30.68, 26.55) * mm, "end": v(30.93, 29.05) * mm});
            skLineSegment(sketch, "E29.21.6.7", {"start": v(31.18, 24) * mm, "end": v(35.8, 21.33) * mm, "construction": true});
            skPoint(sketch, "E29.24.6.7", {"position": v(33.63, 23.16) * mm});
            skPoint(sketch, "E29.25.6.7", {"position": v(28.72, 23.16) * mm});
            skPoint(sketch, "E29.26.6.7", {"position": v(31.18, 24) * mm});
            skLineSegment(sketch, "E29.27.6.7", {"start": v(31.18, 24) * mm, "end": v(26.78, 21.46) * mm, "construction": true});
            skArc(sketch, "E29.30.6.7", {"start": v(33.14, 22.3) * mm, "mid": v(33.77, 22.5) * mm, "end": v(33.63, 23.16) * mm});
            skPoint(sketch, "E29.34.6.7", {"position": v(29.22, 22.3) * mm});
            skLineSegment(sketch, "E29.35.6.7", {"start": v(29.22, 22.3) * mm, "end": v(26.93, 21.26) * mm});
            skLineSegment(sketch, "E29.38.6.7", {"start": v(28.72, 23.16) * mm, "end": v(26.68, 21.69) * mm});
            skPoint(sketch, "E29.41.6.7", {"position": v(33.14, 22.3) * mm});
            skLineSegment(sketch, "E29.42.6.7", {"start": v(31.67, 26.55) * mm, "end": v(31.42, 29.05) * mm});
            skLineSegment(sketch, "E29.45.6.7", {"start": v(33.14, 22.3) * mm, "end": v(35.43, 21.26) * mm});
            skArc(sketch, "E29.48.6.7", {"start": v(31.67, 26.55) * mm, "mid": v(31.18, 27) * mm, "end": v(30.68, 26.55) * mm});
            skPoint(sketch, "E29.52.6.7", {"position": v(33.14, 22.3) * mm});
            skPoint(sketch, "E29.53.6.7", {"position": v(31.67, 26.55) * mm});
            skPoint(sketch, "E29.54.6.7", {"position": v(28.72, 23.16) * mm});
            skArc(sketch, "E29.55.6.7", {"start": v(26.68, 21.69) * mm, "mid": v(26.78, 21.46) * mm, "end": v(26.93, 21.26) * mm});
            skArc(sketch, "E29.59.6.7", {"start": v(35.43, 21.26) * mm, "mid": v(35.58, 21.46) * mm, "end": v(35.67, 21.69) * mm});
            skArc(sketch, "E29.63.6.7", {"start": v(31.42, 29.05) * mm, "mid": v(31.18, 29.08) * mm, "end": v(30.93, 29.05) * mm});
            skLineSegment(sketch, "E29.67.6.7", {"start": v(31.18, 24) * mm, "end": v(31.18, 29.34) * mm, "construction": true});
            skPoint(sketch, "E29.0.7.2", {"position": v(35.88, -6.45) * mm});
            skLineSegment(sketch, "E29.1.7.2", {"start": v(36.37, -9) * mm, "end": v(31.75, -11.67) * mm, "construction": true});
            skLineSegment(sketch, "E29.4.7.2", {"start": v(38.83, -9.84) * mm, "end": v(40.87, -11.31) * mm});
            skPoint(sketch, "E29.7.7.2", {"position": v(36.87, -6.45) * mm});
            skArc(sketch, "E29.8.7.2", {"start": v(33.92, -9.84) * mm, "mid": v(33.77, -10.5) * mm, "end": v(34.41, -10.7) * mm});
            skLineSegment(sketch, "E29.12.7.2", {"start": v(36.37, -9) * mm, "end": v(36.37, -3.92) * mm, "construction": true});
            skLineSegment(sketch, "E29.15.7.2", {"start": v(36.37, -9) * mm, "end": v(40.77, -11.54) * mm, "construction": true});
            skLineSegment(sketch, "E29.18.7.2", {"start": v(35.88, -6.45) * mm, "end": v(36.13, -3.95) * mm});
            skLineSegment(sketch, "E29.21.7.2", {"start": v(36.37, -9) * mm, "end": v(41, -11.67) * mm, "construction": true});
            skPoint(sketch, "E29.24.7.2", {"position": v(38.83, -9.84) * mm});
            skPoint(sketch, "E29.25.7.2", {"position": v(33.92, -9.84) * mm});
            skPoint(sketch, "E29.26.7.2", {"position": v(36.37, -9) * mm});
            skLineSegment(sketch, "E29.27.7.2", {"start": v(36.37, -9) * mm, "end": v(31.97, -11.54) * mm, "construction": true});
            skArc(sketch, "E29.30.7.2", {"start": v(38.33, -10.7) * mm, "mid": v(38.97, -10.5) * mm, "end": v(38.83, -9.84) * mm});
            skPoint(sketch, "E29.34.7.2", {"position": v(34.41, -10.7) * mm});
            skLineSegment(sketch, "E29.35.7.2", {"start": v(34.41, -10.7) * mm, "end": v(32.12, -11.74) * mm});
            skLineSegment(sketch, "E29.38.7.2", {"start": v(33.92, -9.84) * mm, "end": v(31.88, -11.31) * mm});
            skPoint(sketch, "E29.41.7.2", {"position": v(38.33, -10.7) * mm});
            skLineSegment(sketch, "E29.42.7.2", {"start": v(36.87, -6.45) * mm, "end": v(36.62, -3.95) * mm});
            skLineSegment(sketch, "E29.45.7.2", {"start": v(38.33, -10.7) * mm, "end": v(40.62, -11.74) * mm});
            skArc(sketch, "E29.48.7.2", {"start": v(36.87, -6.45) * mm, "mid": v(36.37, -6) * mm, "end": v(35.88, -6.45) * mm});
            skPoint(sketch, "E29.52.7.2", {"position": v(38.33, -10.7) * mm});
            skPoint(sketch, "E29.53.7.2", {"position": v(36.87, -6.45) * mm});
            skPoint(sketch, "E29.54.7.2", {"position": v(33.92, -9.84) * mm});
            skArc(sketch, "E29.55.7.2", {"start": v(31.88, -11.31) * mm, "mid": v(31.97, -11.54) * mm, "end": v(32.12, -11.74) * mm});
            skArc(sketch, "E29.59.7.2", {"start": v(40.62, -11.74) * mm, "mid": v(40.77, -11.54) * mm, "end": v(40.87, -11.31) * mm});
            skArc(sketch, "E29.63.7.2", {"start": v(36.62, -3.95) * mm, "mid": v(36.37, -3.92) * mm, "end": v(36.13, -3.95) * mm});
            skLineSegment(sketch, "E29.67.7.2", {"start": v(36.37, -9) * mm, "end": v(36.37, -3.66) * mm, "construction": true});
            skPoint(sketch, "E29.0.7.3", {"position": v(35.88, -0.45) * mm});
            skLineSegment(sketch, "E29.1.7.3", {"start": v(36.37, -3) * mm, "end": v(31.75, -5.67) * mm, "construction": true});
            skLineSegment(sketch, "E29.4.7.3", {"start": v(38.83, -3.84) * mm, "end": v(40.87, -5.31) * mm});
            skPoint(sketch, "E29.7.7.3", {"position": v(36.87, -0.45) * mm});
            skArc(sketch, "E29.8.7.3", {"start": v(33.92, -3.84) * mm, "mid": v(33.77, -4.5) * mm, "end": v(34.41, -4.7) * mm});
            skLineSegment(sketch, "E29.12.7.3", {"start": v(36.37, -3) * mm, "end": v(36.37, 2.08) * mm, "construction": true});
            skLineSegment(sketch, "E29.15.7.3", {"start": v(36.37, -3) * mm, "end": v(40.77, -5.54) * mm, "construction": true});
            skLineSegment(sketch, "E29.18.7.3", {"start": v(35.88, -0.45) * mm, "end": v(36.13, 2.05) * mm});
            skLineSegment(sketch, "E29.21.7.3", {"start": v(36.37, -3) * mm, "end": v(41, -5.67) * mm, "construction": true});
            skPoint(sketch, "E29.24.7.3", {"position": v(38.83, -3.84) * mm});
            skPoint(sketch, "E29.25.7.3", {"position": v(33.92, -3.84) * mm});
            skPoint(sketch, "E29.26.7.3", {"position": v(36.37, -3) * mm});
            skLineSegment(sketch, "E29.27.7.3", {"start": v(36.37, -3) * mm, "end": v(31.97, -5.54) * mm, "construction": true});
            skArc(sketch, "E29.30.7.3", {"start": v(38.33, -4.7) * mm, "mid": v(38.97, -4.5) * mm, "end": v(38.83, -3.84) * mm});
            skPoint(sketch, "E29.34.7.3", {"position": v(34.41, -4.7) * mm});
            skLineSegment(sketch, "E29.35.7.3", {"start": v(34.41, -4.7) * mm, "end": v(32.12, -5.74) * mm});
            skLineSegment(sketch, "E29.38.7.3", {"start": v(33.92, -3.84) * mm, "end": v(31.88, -5.31) * mm});
            skPoint(sketch, "E29.41.7.3", {"position": v(38.33, -4.7) * mm});
            skLineSegment(sketch, "E29.42.7.3", {"start": v(36.87, -0.45) * mm, "end": v(36.62, 2.05) * mm});
            skLineSegment(sketch, "E29.45.7.3", {"start": v(38.33, -4.7) * mm, "end": v(40.62, -5.74) * mm});
            skArc(sketch, "E29.48.7.3", {"start": v(36.87, -0.45) * mm, "mid": v(36.37, 0) * mm, "end": v(35.88, -0.45) * mm});
            skPoint(sketch, "E29.52.7.3", {"position": v(38.33, -4.7) * mm});
            skPoint(sketch, "E29.53.7.3", {"position": v(36.87, -0.45) * mm});
            skPoint(sketch, "E29.54.7.3", {"position": v(33.92, -3.84) * mm});
            skArc(sketch, "E29.55.7.3", {"start": v(31.88, -5.31) * mm, "mid": v(31.97, -5.54) * mm, "end": v(32.12, -5.74) * mm});
            skArc(sketch, "E29.59.7.3", {"start": v(40.62, -5.74) * mm, "mid": v(40.77, -5.54) * mm, "end": v(40.87, -5.31) * mm});
            skArc(sketch, "E29.63.7.3", {"start": v(36.62, 2.05) * mm, "mid": v(36.37, 2.08) * mm, "end": v(36.13, 2.05) * mm});
            skLineSegment(sketch, "E29.67.7.3", {"start": v(36.37, -3) * mm, "end": v(36.37, 2.34) * mm, "construction": true});
            skPoint(sketch, "E29.0.7.4", {"position": v(35.88, 5.55) * mm});
            skLineSegment(sketch, "E29.1.7.4", {"start": v(36.37, 3) * mm, "end": v(31.75, 0.33) * mm, "construction": true});
            skLineSegment(sketch, "E29.4.7.4", {"start": v(38.83, 2.16) * mm, "end": v(40.87, 0.69) * mm});
            skPoint(sketch, "E29.7.7.4", {"position": v(36.87, 5.55) * mm});
            skArc(sketch, "E29.8.7.4", {"start": v(33.92, 2.16) * mm, "mid": v(33.77, 1.5) * mm, "end": v(34.41, 1.3) * mm});
            skLineSegment(sketch, "E29.12.7.4", {"start": v(36.37, 3) * mm, "end": v(36.37, 8.08) * mm, "construction": true});
            skLineSegment(sketch, "E29.15.7.4", {"start": v(36.37, 3) * mm, "end": v(40.77, 0.46) * mm, "construction": true});
            skLineSegment(sketch, "E29.18.7.4", {"start": v(35.88, 5.55) * mm, "end": v(36.13, 8.05) * mm});
            skLineSegment(sketch, "E29.21.7.4", {"start": v(36.37, 3) * mm, "end": v(41, 0.33) * mm, "construction": true});
            skPoint(sketch, "E29.24.7.4", {"position": v(38.83, 2.16) * mm});
            skPoint(sketch, "E29.25.7.4", {"position": v(33.92, 2.16) * mm});
            skPoint(sketch, "E29.26.7.4", {"position": v(36.37, 3) * mm});
            skLineSegment(sketch, "E29.27.7.4", {"start": v(36.37, 3) * mm, "end": v(31.97, 0.46) * mm, "construction": true});
            skArc(sketch, "E29.30.7.4", {"start": v(38.33, 1.3) * mm, "mid": v(38.97, 1.5) * mm, "end": v(38.83, 2.16) * mm});
            skPoint(sketch, "E29.34.7.4", {"position": v(34.41, 1.3) * mm});
            skLineSegment(sketch, "E29.35.7.4", {"start": v(34.41, 1.3) * mm, "end": v(32.12, 0.26) * mm});
            skLineSegment(sketch, "E29.38.7.4", {"start": v(33.92, 2.16) * mm, "end": v(31.88, 0.69) * mm});
            skPoint(sketch, "E29.41.7.4", {"position": v(38.33, 1.3) * mm});
            skLineSegment(sketch, "E29.42.7.4", {"start": v(36.87, 5.55) * mm, "end": v(36.62, 8.05) * mm});
            skLineSegment(sketch, "E29.45.7.4", {"start": v(38.33, 1.3) * mm, "end": v(40.62, 0.26) * mm});
            skArc(sketch, "E29.48.7.4", {"start": v(36.87, 5.55) * mm, "mid": v(36.37, 6) * mm, "end": v(35.88, 5.55) * mm});
            skPoint(sketch, "E29.52.7.4", {"position": v(38.33, 1.3) * mm});
            skPoint(sketch, "E29.53.7.4", {"position": v(36.87, 5.55) * mm});
            skPoint(sketch, "E29.54.7.4", {"position": v(33.92, 2.16) * mm});
            skArc(sketch, "E29.55.7.4", {"start": v(31.88, 0.69) * mm, "mid": v(31.97, 0.46) * mm, "end": v(32.12, 0.26) * mm});
            skArc(sketch, "E29.59.7.4", {"start": v(40.62, 0.26) * mm, "mid": v(40.77, 0.46) * mm, "end": v(40.87, 0.69) * mm});
            skArc(sketch, "E29.63.7.4", {"start": v(36.62, 8.05) * mm, "mid": v(36.37, 8.08) * mm, "end": v(36.13, 8.05) * mm});
            skLineSegment(sketch, "E29.67.7.4", {"start": v(36.37, 3) * mm, "end": v(36.37, 8.34) * mm, "construction": true});
            skPoint(sketch, "E29.0.7.5", {"position": v(35.88, 11.55) * mm});
            skLineSegment(sketch, "E29.1.7.5", {"start": v(36.37, 9) * mm, "end": v(31.75, 6.33) * mm, "construction": true});
            skLineSegment(sketch, "E29.4.7.5", {"start": v(38.83, 8.16) * mm, "end": v(40.87, 6.69) * mm});
            skPoint(sketch, "E29.7.7.5", {"position": v(36.87, 11.55) * mm});
            skArc(sketch, "E29.8.7.5", {"start": v(33.92, 8.16) * mm, "mid": v(33.77, 7.5) * mm, "end": v(34.41, 7.3) * mm});
            skLineSegment(sketch, "E29.12.7.5", {"start": v(36.37, 9) * mm, "end": v(36.37, 14.08) * mm, "construction": true});
            skLineSegment(sketch, "E29.15.7.5", {"start": v(36.37, 9) * mm, "end": v(40.77, 6.46) * mm, "construction": true});
            skLineSegment(sketch, "E29.18.7.5", {"start": v(35.88, 11.55) * mm, "end": v(36.13, 14.05) * mm});
            skLineSegment(sketch, "E29.21.7.5", {"start": v(36.37, 9) * mm, "end": v(41, 6.33) * mm, "construction": true});
            skPoint(sketch, "E29.24.7.5", {"position": v(38.83, 8.16) * mm});
            skPoint(sketch, "E29.25.7.5", {"position": v(33.92, 8.16) * mm});
            skPoint(sketch, "E29.26.7.5", {"position": v(36.37, 9) * mm});
            skLineSegment(sketch, "E29.27.7.5", {"start": v(36.37, 9) * mm, "end": v(31.97, 6.46) * mm, "construction": true});
            skArc(sketch, "E29.30.7.5", {"start": v(38.33, 7.3) * mm, "mid": v(38.97, 7.5) * mm, "end": v(38.83, 8.16) * mm});
            skPoint(sketch, "E29.34.7.5", {"position": v(34.41, 7.3) * mm});
            skLineSegment(sketch, "E29.35.7.5", {"start": v(34.41, 7.3) * mm, "end": v(32.12, 6.26) * mm});
            skLineSegment(sketch, "E29.38.7.5", {"start": v(33.92, 8.16) * mm, "end": v(31.88, 6.69) * mm});
            skPoint(sketch, "E29.41.7.5", {"position": v(38.33, 7.3) * mm});
            skLineSegment(sketch, "E29.42.7.5", {"start": v(36.87, 11.55) * mm, "end": v(36.62, 14.05) * mm});
            skLineSegment(sketch, "E29.45.7.5", {"start": v(38.33, 7.3) * mm, "end": v(40.62, 6.26) * mm});
            skArc(sketch, "E29.48.7.5", {"start": v(36.87, 11.55) * mm, "mid": v(36.37, 12) * mm, "end": v(35.88, 11.55) * mm});
            skPoint(sketch, "E29.52.7.5", {"position": v(38.33, 7.3) * mm});
            skPoint(sketch, "E29.53.7.5", {"position": v(36.87, 11.55) * mm});
            skPoint(sketch, "E29.54.7.5", {"position": v(33.92, 8.16) * mm});
            skArc(sketch, "E29.55.7.5", {"start": v(31.88, 6.69) * mm, "mid": v(31.97, 6.46) * mm, "end": v(32.12, 6.26) * mm});
            skArc(sketch, "E29.59.7.5", {"start": v(40.62, 6.26) * mm, "mid": v(40.77, 6.46) * mm, "end": v(40.87, 6.69) * mm});
            skArc(sketch, "E29.63.7.5", {"start": v(36.62, 14.05) * mm, "mid": v(36.37, 14.08) * mm, "end": v(36.13, 14.05) * mm});
            skLineSegment(sketch, "E29.67.7.5", {"start": v(36.37, 9) * mm, "end": v(36.37, 14.34) * mm, "construction": true});
            skPoint(sketch, "E29.0.7.6", {"position": v(35.88, 17.55) * mm});
            skLineSegment(sketch, "E29.1.7.6", {"start": v(36.37, 15) * mm, "end": v(31.75, 12.33) * mm, "construction": true});
            skLineSegment(sketch, "E29.4.7.6", {"start": v(38.83, 14.16) * mm, "end": v(40.87, 12.69) * mm});
            skPoint(sketch, "E29.7.7.6", {"position": v(36.87, 17.55) * mm});
            skArc(sketch, "E29.8.7.6", {"start": v(33.92, 14.16) * mm, "mid": v(33.77, 13.5) * mm, "end": v(34.41, 13.3) * mm});
            skLineSegment(sketch, "E29.12.7.6", {"start": v(36.37, 15) * mm, "end": v(36.37, 20.08) * mm, "construction": true});
            skLineSegment(sketch, "E29.15.7.6", {"start": v(36.37, 15) * mm, "end": v(40.77, 12.46) * mm, "construction": true});
            skLineSegment(sketch, "E29.18.7.6", {"start": v(35.88, 17.55) * mm, "end": v(36.13, 20.05) * mm});
            skLineSegment(sketch, "E29.21.7.6", {"start": v(36.37, 15) * mm, "end": v(41, 12.33) * mm, "construction": true});
            skPoint(sketch, "E29.24.7.6", {"position": v(38.83, 14.16) * mm});
            skPoint(sketch, "E29.25.7.6", {"position": v(33.92, 14.16) * mm});
            skPoint(sketch, "E29.26.7.6", {"position": v(36.37, 15) * mm});
            skLineSegment(sketch, "E29.27.7.6", {"start": v(36.37, 15) * mm, "end": v(31.97, 12.46) * mm, "construction": true});
            skArc(sketch, "E29.30.7.6", {"start": v(38.33, 13.3) * mm, "mid": v(38.97, 13.5) * mm, "end": v(38.83, 14.16) * mm});
            skPoint(sketch, "E29.34.7.6", {"position": v(34.41, 13.3) * mm});
            skLineSegment(sketch, "E29.35.7.6", {"start": v(34.41, 13.3) * mm, "end": v(32.12, 12.26) * mm});
            skLineSegment(sketch, "E29.38.7.6", {"start": v(33.92, 14.16) * mm, "end": v(31.88, 12.69) * mm});
            skPoint(sketch, "E29.41.7.6", {"position": v(38.33, 13.3) * mm});
            skLineSegment(sketch, "E29.42.7.6", {"start": v(36.87, 17.55) * mm, "end": v(36.62, 20.05) * mm});
            skLineSegment(sketch, "E29.45.7.6", {"start": v(38.33, 13.3) * mm, "end": v(40.62, 12.26) * mm});
            skArc(sketch, "E29.48.7.6", {"start": v(36.87, 17.55) * mm, "mid": v(36.37, 18) * mm, "end": v(35.88, 17.55) * mm});
            skPoint(sketch, "E29.52.7.6", {"position": v(38.33, 13.3) * mm});
            skPoint(sketch, "E29.53.7.6", {"position": v(36.87, 17.55) * mm});
            skPoint(sketch, "E29.54.7.6", {"position": v(33.92, 14.16) * mm});
            skArc(sketch, "E29.55.7.6", {"start": v(31.88, 12.69) * mm, "mid": v(31.97, 12.46) * mm, "end": v(32.12, 12.26) * mm});
            skArc(sketch, "E29.59.7.6", {"start": v(40.62, 12.26) * mm, "mid": v(40.77, 12.46) * mm, "end": v(40.87, 12.69) * mm});
            skArc(sketch, "E29.63.7.6", {"start": v(36.62, 20.05) * mm, "mid": v(36.37, 20.08) * mm, "end": v(36.13, 20.05) * mm});
            skLineSegment(sketch, "E29.67.7.6", {"start": v(36.37, 15) * mm, "end": v(36.37, 20.34) * mm, "construction": true});
            skPoint(sketch, "E29.0.7.7", {"position": v(35.88, 23.55) * mm});
            skLineSegment(sketch, "E29.1.7.7", {"start": v(36.37, 21) * mm, "end": v(31.75, 18.33) * mm, "construction": true});
            skLineSegment(sketch, "E29.4.7.7", {"start": v(38.83, 20.16) * mm, "end": v(40.87, 18.69) * mm});
            skPoint(sketch, "E29.7.7.7", {"position": v(36.87, 23.55) * mm});
            skArc(sketch, "E29.8.7.7", {"start": v(33.92, 20.16) * mm, "mid": v(33.77, 19.5) * mm, "end": v(34.41, 19.3) * mm});
            skLineSegment(sketch, "E29.12.7.7", {"start": v(36.37, 21) * mm, "end": v(36.37, 26.08) * mm, "construction": true});
            skLineSegment(sketch, "E29.15.7.7", {"start": v(36.37, 21) * mm, "end": v(40.77, 18.46) * mm, "construction": true});
            skLineSegment(sketch, "E29.18.7.7", {"start": v(35.88, 23.55) * mm, "end": v(36.13, 26.05) * mm});
            skLineSegment(sketch, "E29.21.7.7", {"start": v(36.37, 21) * mm, "end": v(41, 18.33) * mm, "construction": true});
            skPoint(sketch, "E29.24.7.7", {"position": v(38.83, 20.16) * mm});
            skPoint(sketch, "E29.25.7.7", {"position": v(33.92, 20.16) * mm});
            skPoint(sketch, "E29.26.7.7", {"position": v(36.37, 21) * mm});
            skLineSegment(sketch, "E29.27.7.7", {"start": v(36.37, 21) * mm, "end": v(31.97, 18.46) * mm, "construction": true});
            skArc(sketch, "E29.30.7.7", {"start": v(38.33, 19.3) * mm, "mid": v(38.97, 19.5) * mm, "end": v(38.83, 20.16) * mm});
            skPoint(sketch, "E29.34.7.7", {"position": v(34.41, 19.3) * mm});
            skLineSegment(sketch, "E29.35.7.7", {"start": v(34.41, 19.3) * mm, "end": v(32.12, 18.26) * mm});
            skLineSegment(sketch, "E29.38.7.7", {"start": v(33.92, 20.16) * mm, "end": v(31.88, 18.69) * mm});
            skPoint(sketch, "E29.41.7.7", {"position": v(38.33, 19.3) * mm});
            skLineSegment(sketch, "E29.42.7.7", {"start": v(36.87, 23.55) * mm, "end": v(36.62, 26.05) * mm});
            skLineSegment(sketch, "E29.45.7.7", {"start": v(38.33, 19.3) * mm, "end": v(40.62, 18.26) * mm});
            skArc(sketch, "E29.48.7.7", {"start": v(36.87, 23.55) * mm, "mid": v(36.37, 24) * mm, "end": v(35.88, 23.55) * mm});
            skPoint(sketch, "E29.52.7.7", {"position": v(38.33, 19.3) * mm});
            skPoint(sketch, "E29.53.7.7", {"position": v(36.87, 23.55) * mm});
            skPoint(sketch, "E29.54.7.7", {"position": v(33.92, 20.16) * mm});
            skArc(sketch, "E29.55.7.7", {"start": v(31.88, 18.69) * mm, "mid": v(31.97, 18.46) * mm, "end": v(32.12, 18.26) * mm});
            skArc(sketch, "E29.59.7.7", {"start": v(40.62, 18.26) * mm, "mid": v(40.77, 18.46) * mm, "end": v(40.87, 18.69) * mm});
            skArc(sketch, "E29.63.7.7", {"start": v(36.62, 26.05) * mm, "mid": v(36.37, 26.08) * mm, "end": v(36.13, 26.05) * mm});
            skLineSegment(sketch, "E29.67.7.7", {"start": v(36.37, 21) * mm, "end": v(36.37, 26.34) * mm, "construction": true});
            skPoint(sketch, "E29.0.8.2", {"position": v(41.07, -9.45) * mm});
            skLineSegment(sketch, "E29.1.8.2", {"start": v(41.57, -12) * mm, "end": v(36.94, -14.67) * mm, "construction": true});
            skLineSegment(sketch, "E29.4.8.2", {"start": v(44.03, -12.84) * mm, "end": v(46.07, -14.31) * mm});
            skPoint(sketch, "E29.7.8.2", {"position": v(42.07, -9.45) * mm});
            skArc(sketch, "E29.8.8.2", {"start": v(39.11, -12.84) * mm, "mid": v(38.97, -13.5) * mm, "end": v(39.6, -13.7) * mm});
            skLineSegment(sketch, "E29.12.8.2", {"start": v(41.57, -12) * mm, "end": v(41.57, -6.92) * mm, "construction": true});
            skLineSegment(sketch, "E29.15.8.2", {"start": v(41.57, -12) * mm, "end": v(45.97, -14.54) * mm, "construction": true});
            skLineSegment(sketch, "E29.18.8.2", {"start": v(41.07, -9.45) * mm, "end": v(41.32, -6.95) * mm});
            skLineSegment(sketch, "E29.21.8.2", {"start": v(41.57, -12) * mm, "end": v(46.2, -14.67) * mm, "construction": true});
            skPoint(sketch, "E29.24.8.2", {"position": v(44.03, -12.84) * mm});
            skPoint(sketch, "E29.25.8.2", {"position": v(39.11, -12.84) * mm});
            skPoint(sketch, "E29.26.8.2", {"position": v(41.57, -12) * mm});
            skLineSegment(sketch, "E29.27.8.2", {"start": v(41.57, -12) * mm, "end": v(37.17, -14.54) * mm, "construction": true});
            skArc(sketch, "E29.30.8.2", {"start": v(43.53, -13.7) * mm, "mid": v(44.17, -13.5) * mm, "end": v(44.03, -12.84) * mm});
            skPoint(sketch, "E29.34.8.2", {"position": v(39.6, -13.7) * mm});
            skLineSegment(sketch, "E29.35.8.2", {"start": v(39.6, -13.7) * mm, "end": v(37.32, -14.74) * mm});
            skLineSegment(sketch, "E29.38.8.2", {"start": v(39.11, -12.84) * mm, "end": v(37.07, -14.31) * mm});
            skPoint(sketch, "E29.41.8.2", {"position": v(43.53, -13.7) * mm});
            skLineSegment(sketch, "E29.42.8.2", {"start": v(42.07, -9.45) * mm, "end": v(41.82, -6.95) * mm});
            skLineSegment(sketch, "E29.45.8.2", {"start": v(43.53, -13.7) * mm, "end": v(45.82, -14.74) * mm});
            skArc(sketch, "E29.48.8.2", {"start": v(42.07, -9.45) * mm, "mid": v(41.57, -9) * mm, "end": v(41.07, -9.45) * mm});
            skPoint(sketch, "E29.52.8.2", {"position": v(43.53, -13.7) * mm});
            skPoint(sketch, "E29.53.8.2", {"position": v(42.07, -9.45) * mm});
            skPoint(sketch, "E29.54.8.2", {"position": v(39.11, -12.84) * mm});
            skArc(sketch, "E29.55.8.2", {"start": v(37.07, -14.31) * mm, "mid": v(37.17, -14.54) * mm, "end": v(37.32, -14.74) * mm});
            skArc(sketch, "E29.59.8.2", {"start": v(45.82, -14.74) * mm, "mid": v(45.97, -14.54) * mm, "end": v(46.07, -14.31) * mm});
            skArc(sketch, "E29.63.8.2", {"start": v(41.82, -6.95) * mm, "mid": v(41.57, -6.92) * mm, "end": v(41.32, -6.95) * mm});
            skLineSegment(sketch, "E29.67.8.2", {"start": v(41.57, -12) * mm, "end": v(41.57, -6.66) * mm, "construction": true});
            skPoint(sketch, "E29.0.8.3", {"position": v(41.07, -3.45) * mm});
            skLineSegment(sketch, "E29.1.8.3", {"start": v(41.57, -6) * mm, "end": v(36.94, -8.67) * mm, "construction": true});
            skLineSegment(sketch, "E29.4.8.3", {"start": v(44.03, -6.84) * mm, "end": v(46.07, -8.31) * mm});
            skPoint(sketch, "E29.7.8.3", {"position": v(42.07, -3.45) * mm});
            skArc(sketch, "E29.8.8.3", {"start": v(39.11, -6.84) * mm, "mid": v(38.97, -7.5) * mm, "end": v(39.6, -7.7) * mm});
            skLineSegment(sketch, "E29.12.8.3", {"start": v(41.57, -6) * mm, "end": v(41.57, -0.92) * mm, "construction": true});
            skLineSegment(sketch, "E29.15.8.3", {"start": v(41.57, -6) * mm, "end": v(45.97, -8.54) * mm, "construction": true});
            skLineSegment(sketch, "E29.18.8.3", {"start": v(41.07, -3.45) * mm, "end": v(41.32, -0.95) * mm});
            skLineSegment(sketch, "E29.21.8.3", {"start": v(41.57, -6) * mm, "end": v(46.2, -8.67) * mm, "construction": true});
            skPoint(sketch, "E29.24.8.3", {"position": v(44.03, -6.84) * mm});
            skPoint(sketch, "E29.25.8.3", {"position": v(39.11, -6.84) * mm});
            skPoint(sketch, "E29.26.8.3", {"position": v(41.57, -6) * mm});
            skLineSegment(sketch, "E29.27.8.3", {"start": v(41.57, -6) * mm, "end": v(37.17, -8.54) * mm, "construction": true});
            skArc(sketch, "E29.30.8.3", {"start": v(43.53, -7.7) * mm, "mid": v(44.17, -7.5) * mm, "end": v(44.03, -6.84) * mm});
            skPoint(sketch, "E29.34.8.3", {"position": v(39.6, -7.7) * mm});
            skLineSegment(sketch, "E29.35.8.3", {"start": v(39.6, -7.7) * mm, "end": v(37.32, -8.74) * mm});
            skLineSegment(sketch, "E29.38.8.3", {"start": v(39.11, -6.84) * mm, "end": v(37.07, -8.31) * mm});
            skPoint(sketch, "E29.41.8.3", {"position": v(43.53, -7.7) * mm});
            skLineSegment(sketch, "E29.42.8.3", {"start": v(42.07, -3.45) * mm, "end": v(41.82, -0.95) * mm});
            skLineSegment(sketch, "E29.45.8.3", {"start": v(43.53, -7.7) * mm, "end": v(45.82, -8.74) * mm});
            skArc(sketch, "E29.48.8.3", {"start": v(42.07, -3.45) * mm, "mid": v(41.57, -3) * mm, "end": v(41.07, -3.45) * mm});
            skPoint(sketch, "E29.52.8.3", {"position": v(43.53, -7.7) * mm});
            skPoint(sketch, "E29.53.8.3", {"position": v(42.07, -3.45) * mm});
            skPoint(sketch, "E29.54.8.3", {"position": v(39.11, -6.84) * mm});
            skArc(sketch, "E29.55.8.3", {"start": v(37.07, -8.31) * mm, "mid": v(37.17, -8.54) * mm, "end": v(37.32, -8.74) * mm});
            skArc(sketch, "E29.59.8.3", {"start": v(45.82, -8.74) * mm, "mid": v(45.97, -8.54) * mm, "end": v(46.07, -8.31) * mm});
            skArc(sketch, "E29.63.8.3", {"start": v(41.82, -0.95) * mm, "mid": v(41.57, -0.92) * mm, "end": v(41.32, -0.95) * mm});
            skLineSegment(sketch, "E29.67.8.3", {"start": v(41.57, -6) * mm, "end": v(41.57, -0.66) * mm, "construction": true});
            skPoint(sketch, "E29.0.8.4", {"position": v(41.07, 2.55) * mm});
            skLineSegment(sketch, "E29.1.8.4", {"start": v(41.57, 0) * mm, "end": v(36.94, -2.67) * mm, "construction": true});
            skLineSegment(sketch, "E29.4.8.4", {"start": v(44.03, -0.84) * mm, "end": v(46.07, -2.31) * mm});
            skPoint(sketch, "E29.7.8.4", {"position": v(42.07, 2.55) * mm});
            skArc(sketch, "E29.8.8.4", {"start": v(39.11, -0.84) * mm, "mid": v(38.97, -1.5) * mm, "end": v(39.6, -1.7) * mm});
            skLineSegment(sketch, "E29.12.8.4", {"start": v(41.57, 0) * mm, "end": v(41.57, 5.08) * mm, "construction": true});
            skLineSegment(sketch, "E29.15.8.4", {"start": v(41.57, 0) * mm, "end": v(45.97, -2.54) * mm, "construction": true});
            skLineSegment(sketch, "E29.18.8.4", {"start": v(41.07, 2.55) * mm, "end": v(41.32, 5.05) * mm});
            skLineSegment(sketch, "E29.21.8.4", {"start": v(41.57, 0) * mm, "end": v(46.2, -2.67) * mm, "construction": true});
            skPoint(sketch, "E29.24.8.4", {"position": v(44.03, -0.84) * mm});
            skPoint(sketch, "E29.25.8.4", {"position": v(39.11, -0.84) * mm});
            skPoint(sketch, "E29.26.8.4", {"position": v(41.57, 0) * mm});
            skLineSegment(sketch, "E29.27.8.4", {"start": v(41.57, 0) * mm, "end": v(37.17, -2.54) * mm, "construction": true});
            skArc(sketch, "E29.30.8.4", {"start": v(43.53, -1.7) * mm, "mid": v(44.17, -1.5) * mm, "end": v(44.03, -0.84) * mm});
            skPoint(sketch, "E29.34.8.4", {"position": v(39.6, -1.7) * mm});
            skLineSegment(sketch, "E29.35.8.4", {"start": v(39.6, -1.7) * mm, "end": v(37.32, -2.74) * mm});
            skLineSegment(sketch, "E29.38.8.4", {"start": v(39.11, -0.84) * mm, "end": v(37.07, -2.31) * mm});
            skPoint(sketch, "E29.41.8.4", {"position": v(43.53, -1.7) * mm});
            skLineSegment(sketch, "E29.42.8.4", {"start": v(42.07, 2.55) * mm, "end": v(41.82, 5.05) * mm});
            skLineSegment(sketch, "E29.45.8.4", {"start": v(43.53, -1.7) * mm, "end": v(45.82, -2.74) * mm});
            skArc(sketch, "E29.48.8.4", {"start": v(42.07, 2.55) * mm, "mid": v(41.57, 3) * mm, "end": v(41.07, 2.55) * mm});
            skPoint(sketch, "E29.52.8.4", {"position": v(43.53, -1.7) * mm});
            skPoint(sketch, "E29.53.8.4", {"position": v(42.07, 2.55) * mm});
            skPoint(sketch, "E29.54.8.4", {"position": v(39.11, -0.84) * mm});
            skArc(sketch, "E29.55.8.4", {"start": v(37.07, -2.31) * mm, "mid": v(37.17, -2.54) * mm, "end": v(37.32, -2.74) * mm});
            skArc(sketch, "E29.59.8.4", {"start": v(45.82, -2.74) * mm, "mid": v(45.97, -2.54) * mm, "end": v(46.07, -2.31) * mm});
            skArc(sketch, "E29.63.8.4", {"start": v(41.82, 5.05) * mm, "mid": v(41.57, 5.08) * mm, "end": v(41.32, 5.05) * mm});
            skLineSegment(sketch, "E29.67.8.4", {"start": v(41.57, 0) * mm, "end": v(41.57, 5.34) * mm, "construction": true});
            skPoint(sketch, "E29.0.8.5", {"position": v(41.07, 8.55) * mm});
            skLineSegment(sketch, "E29.1.8.5", {"start": v(41.57, 6) * mm, "end": v(36.94, 3.33) * mm, "construction": true});
            skLineSegment(sketch, "E29.4.8.5", {"start": v(44.03, 5.16) * mm, "end": v(46.07, 3.69) * mm});
            skPoint(sketch, "E29.7.8.5", {"position": v(42.07, 8.55) * mm});
            skArc(sketch, "E29.8.8.5", {"start": v(39.11, 5.16) * mm, "mid": v(38.97, 4.5) * mm, "end": v(39.6, 4.3) * mm});
            skLineSegment(sketch, "E29.12.8.5", {"start": v(41.57, 6) * mm, "end": v(41.57, 11.08) * mm, "construction": true});
            skLineSegment(sketch, "E29.15.8.5", {"start": v(41.57, 6) * mm, "end": v(45.97, 3.46) * mm, "construction": true});
            skLineSegment(sketch, "E29.18.8.5", {"start": v(41.07, 8.55) * mm, "end": v(41.32, 11.05) * mm});
            skLineSegment(sketch, "E29.21.8.5", {"start": v(41.57, 6) * mm, "end": v(46.2, 3.33) * mm, "construction": true});
            skPoint(sketch, "E29.24.8.5", {"position": v(44.03, 5.16) * mm});
            skPoint(sketch, "E29.25.8.5", {"position": v(39.11, 5.16) * mm});
            skPoint(sketch, "E29.26.8.5", {"position": v(41.57, 6) * mm});
            skLineSegment(sketch, "E29.27.8.5", {"start": v(41.57, 6) * mm, "end": v(37.17, 3.46) * mm, "construction": true});
            skArc(sketch, "E29.30.8.5", {"start": v(43.53, 4.3) * mm, "mid": v(44.17, 4.5) * mm, "end": v(44.03, 5.16) * mm});
            skPoint(sketch, "E29.34.8.5", {"position": v(39.6, 4.3) * mm});
            skLineSegment(sketch, "E29.35.8.5", {"start": v(39.6, 4.3) * mm, "end": v(37.32, 3.26) * mm});
            skLineSegment(sketch, "E29.38.8.5", {"start": v(39.11, 5.16) * mm, "end": v(37.07, 3.69) * mm});
            skPoint(sketch, "E29.41.8.5", {"position": v(43.53, 4.3) * mm});
            skLineSegment(sketch, "E29.42.8.5", {"start": v(42.07, 8.55) * mm, "end": v(41.82, 11.05) * mm});
            skLineSegment(sketch, "E29.45.8.5", {"start": v(43.53, 4.3) * mm, "end": v(45.82, 3.26) * mm});
            skArc(sketch, "E29.48.8.5", {"start": v(42.07, 8.55) * mm, "mid": v(41.57, 9) * mm, "end": v(41.07, 8.55) * mm});
            skPoint(sketch, "E29.52.8.5", {"position": v(43.53, 4.3) * mm});
            skPoint(sketch, "E29.53.8.5", {"position": v(42.07, 8.55) * mm});
            skPoint(sketch, "E29.54.8.5", {"position": v(39.11, 5.16) * mm});
            skArc(sketch, "E29.55.8.5", {"start": v(37.07, 3.69) * mm, "mid": v(37.17, 3.46) * mm, "end": v(37.32, 3.26) * mm});
            skArc(sketch, "E29.59.8.5", {"start": v(45.82, 3.26) * mm, "mid": v(45.97, 3.46) * mm, "end": v(46.07, 3.69) * mm});
            skArc(sketch, "E29.63.8.5", {"start": v(41.82, 11.05) * mm, "mid": v(41.57, 11.08) * mm, "end": v(41.32, 11.05) * mm});
            skLineSegment(sketch, "E29.67.8.5", {"start": v(41.57, 6) * mm, "end": v(41.57, 11.34) * mm, "construction": true});
            skPoint(sketch, "E29.0.8.6", {"position": v(41.07, 14.55) * mm});
            skLineSegment(sketch, "E29.1.8.6", {"start": v(41.57, 12) * mm, "end": v(36.94, 9.33) * mm, "construction": true});
            skLineSegment(sketch, "E29.4.8.6", {"start": v(44.03, 11.16) * mm, "end": v(46.07, 9.69) * mm});
            skPoint(sketch, "E29.7.8.6", {"position": v(42.07, 14.55) * mm});
            skArc(sketch, "E29.8.8.6", {"start": v(39.11, 11.16) * mm, "mid": v(38.97, 10.5) * mm, "end": v(39.6, 10.3) * mm});
            skLineSegment(sketch, "E29.12.8.6", {"start": v(41.57, 12) * mm, "end": v(41.57, 17.08) * mm, "construction": true});
            skLineSegment(sketch, "E29.15.8.6", {"start": v(41.57, 12) * mm, "end": v(45.97, 9.46) * mm, "construction": true});
            skLineSegment(sketch, "E29.18.8.6", {"start": v(41.07, 14.55) * mm, "end": v(41.32, 17.05) * mm});
            skLineSegment(sketch, "E29.21.8.6", {"start": v(41.57, 12) * mm, "end": v(46.2, 9.33) * mm, "construction": true});
            skPoint(sketch, "E29.24.8.6", {"position": v(44.03, 11.16) * mm});
            skPoint(sketch, "E29.25.8.6", {"position": v(39.11, 11.16) * mm});
            skPoint(sketch, "E29.26.8.6", {"position": v(41.57, 12) * mm});
            skLineSegment(sketch, "E29.27.8.6", {"start": v(41.57, 12) * mm, "end": v(37.17, 9.46) * mm, "construction": true});
            skArc(sketch, "E29.30.8.6", {"start": v(43.53, 10.3) * mm, "mid": v(44.17, 10.5) * mm, "end": v(44.03, 11.16) * mm});
            skPoint(sketch, "E29.34.8.6", {"position": v(39.6, 10.3) * mm});
            skLineSegment(sketch, "E29.35.8.6", {"start": v(39.6, 10.3) * mm, "end": v(37.32, 9.26) * mm});
            skLineSegment(sketch, "E29.38.8.6", {"start": v(39.11, 11.16) * mm, "end": v(37.07, 9.69) * mm});
            skPoint(sketch, "E29.41.8.6", {"position": v(43.53, 10.3) * mm});
            skLineSegment(sketch, "E29.42.8.6", {"start": v(42.07, 14.55) * mm, "end": v(41.82, 17.05) * mm});
            skLineSegment(sketch, "E29.45.8.6", {"start": v(43.53, 10.3) * mm, "end": v(45.82, 9.26) * mm});
            skArc(sketch, "E29.48.8.6", {"start": v(42.07, 14.55) * mm, "mid": v(41.57, 15) * mm, "end": v(41.07, 14.55) * mm});
            skPoint(sketch, "E29.52.8.6", {"position": v(43.53, 10.3) * mm});
            skPoint(sketch, "E29.53.8.6", {"position": v(42.07, 14.55) * mm});
            skPoint(sketch, "E29.54.8.6", {"position": v(39.11, 11.16) * mm});
            skArc(sketch, "E29.55.8.6", {"start": v(37.07, 9.69) * mm, "mid": v(37.17, 9.46) * mm, "end": v(37.32, 9.26) * mm});
            skArc(sketch, "E29.59.8.6", {"start": v(45.82, 9.26) * mm, "mid": v(45.97, 9.46) * mm, "end": v(46.07, 9.69) * mm});
            skArc(sketch, "E29.63.8.6", {"start": v(41.82, 17.05) * mm, "mid": v(41.57, 17.08) * mm, "end": v(41.32, 17.05) * mm});
            skLineSegment(sketch, "E29.67.8.6", {"start": v(41.57, 12) * mm, "end": v(41.57, 17.34) * mm, "construction": true});
            skPoint(sketch, "E29.0.8.7", {"position": v(41.07, 20.55) * mm});
            skLineSegment(sketch, "E29.1.8.7", {"start": v(41.57, 18) * mm, "end": v(36.94, 15.33) * mm, "construction": true});
            skLineSegment(sketch, "E29.4.8.7", {"start": v(44.03, 17.16) * mm, "end": v(46.07, 15.69) * mm});
            skPoint(sketch, "E29.7.8.7", {"position": v(42.07, 20.55) * mm});
            skArc(sketch, "E29.8.8.7", {"start": v(39.11, 17.16) * mm, "mid": v(38.97, 16.5) * mm, "end": v(39.6, 16.3) * mm});
            skLineSegment(sketch, "E29.12.8.7", {"start": v(41.57, 18) * mm, "end": v(41.57, 23.08) * mm, "construction": true});
            skLineSegment(sketch, "E29.15.8.7", {"start": v(41.57, 18) * mm, "end": v(45.97, 15.46) * mm, "construction": true});
            skLineSegment(sketch, "E29.18.8.7", {"start": v(41.07, 20.55) * mm, "end": v(41.32, 23.05) * mm});
            skLineSegment(sketch, "E29.21.8.7", {"start": v(41.57, 18) * mm, "end": v(46.2, 15.33) * mm, "construction": true});
            skPoint(sketch, "E29.24.8.7", {"position": v(44.03, 17.16) * mm});
            skPoint(sketch, "E29.25.8.7", {"position": v(39.11, 17.16) * mm});
            skPoint(sketch, "E29.26.8.7", {"position": v(41.57, 18) * mm});
            skLineSegment(sketch, "E29.27.8.7", {"start": v(41.57, 18) * mm, "end": v(37.17, 15.46) * mm, "construction": true});
            skArc(sketch, "E29.30.8.7", {"start": v(43.53, 16.3) * mm, "mid": v(44.17, 16.5) * mm, "end": v(44.03, 17.16) * mm});
            skPoint(sketch, "E29.34.8.7", {"position": v(39.6, 16.3) * mm});
            skLineSegment(sketch, "E29.35.8.7", {"start": v(39.6, 16.3) * mm, "end": v(37.32, 15.26) * mm});
            skLineSegment(sketch, "E29.38.8.7", {"start": v(39.11, 17.16) * mm, "end": v(37.07, 15.69) * mm});
            skPoint(sketch, "E29.41.8.7", {"position": v(43.53, 16.3) * mm});
            skLineSegment(sketch, "E29.42.8.7", {"start": v(42.07, 20.55) * mm, "end": v(41.82, 23.05) * mm});
            skLineSegment(sketch, "E29.45.8.7", {"start": v(43.53, 16.3) * mm, "end": v(45.82, 15.26) * mm});
            skArc(sketch, "E29.48.8.7", {"start": v(42.07, 20.55) * mm, "mid": v(41.57, 21) * mm, "end": v(41.07, 20.55) * mm});
            skPoint(sketch, "E29.52.8.7", {"position": v(43.53, 16.3) * mm});
            skPoint(sketch, "E29.53.8.7", {"position": v(42.07, 20.55) * mm});
            skPoint(sketch, "E29.54.8.7", {"position": v(39.11, 17.16) * mm});
            skArc(sketch, "E29.55.8.7", {"start": v(37.07, 15.69) * mm, "mid": v(37.17, 15.46) * mm, "end": v(37.32, 15.26) * mm});
            skArc(sketch, "E29.59.8.7", {"start": v(45.82, 15.26) * mm, "mid": v(45.97, 15.46) * mm, "end": v(46.07, 15.69) * mm});
            skArc(sketch, "E29.63.8.7", {"start": v(41.82, 23.05) * mm, "mid": v(41.57, 23.08) * mm, "end": v(41.32, 23.05) * mm});
            skLineSegment(sketch, "E29.67.8.7", {"start": v(41.57, 18) * mm, "end": v(41.57, 23.34) * mm, "construction": true});
            skPoint(sketch, "E29.0.9.2", {"position": v(46.27, -12.45) * mm});
            skLineSegment(sketch, "E29.1.9.2", {"start": v(46.77, -15) * mm, "end": v(42.14, -17.67) * mm, "construction": true});
            skLineSegment(sketch, "E29.4.9.2", {"start": v(49.22, -15.84) * mm, "end": v(51.26, -17.31) * mm});
            skPoint(sketch, "E29.7.9.2", {"position": v(47.26, -12.45) * mm});
            skArc(sketch, "E29.8.9.2", {"start": v(44.3, -15.84) * mm, "mid": v(44.17, -16.5) * mm, "end": v(44.8, -16.7) * mm});
            skLineSegment(sketch, "E29.12.9.2", {"start": v(46.77, -15) * mm, "end": v(46.77, -9.92) * mm, "construction": true});
            skLineSegment(sketch, "E29.15.9.2", {"start": v(46.77, -15) * mm, "end": v(51.17, -17.54) * mm, "construction": true});
            skLineSegment(sketch, "E29.18.9.2", {"start": v(46.27, -12.45) * mm, "end": v(46.52, -9.95) * mm});
            skLineSegment(sketch, "E29.21.9.2", {"start": v(46.77, -15) * mm, "end": v(51.4, -17.67) * mm, "construction": true});
            skPoint(sketch, "E29.24.9.2", {"position": v(49.22, -15.84) * mm});
            skPoint(sketch, "E29.25.9.2", {"position": v(44.3, -15.84) * mm});
            skPoint(sketch, "E29.26.9.2", {"position": v(46.77, -15) * mm});
            skLineSegment(sketch, "E29.27.9.2", {"start": v(46.77, -15) * mm, "end": v(42.37, -17.54) * mm, "construction": true});
            skArc(sketch, "E29.30.9.2", {"start": v(48.72, -16.7) * mm, "mid": v(49.36, -16.5) * mm, "end": v(49.22, -15.84) * mm});
            skPoint(sketch, "E29.34.9.2", {"position": v(44.8, -16.7) * mm});
            skLineSegment(sketch, "E29.35.9.2", {"start": v(44.8, -16.7) * mm, "end": v(42.52, -17.74) * mm});
            skLineSegment(sketch, "E29.38.9.2", {"start": v(44.3, -15.84) * mm, "end": v(42.27, -17.31) * mm});
            skPoint(sketch, "E29.41.9.2", {"position": v(48.72, -16.7) * mm});
            skLineSegment(sketch, "E29.42.9.2", {"start": v(47.26, -12.45) * mm, "end": v(47.01, -9.95) * mm});
            skLineSegment(sketch, "E29.45.9.2", {"start": v(48.72, -16.7) * mm, "end": v(51.02, -17.74) * mm});
            skArc(sketch, "E29.48.9.2", {"start": v(47.26, -12.45) * mm, "mid": v(46.77, -12) * mm, "end": v(46.27, -12.45) * mm});
            skPoint(sketch, "E29.52.9.2", {"position": v(48.72, -16.7) * mm});
            skPoint(sketch, "E29.53.9.2", {"position": v(47.26, -12.45) * mm});
            skPoint(sketch, "E29.54.9.2", {"position": v(44.3, -15.84) * mm});
            skArc(sketch, "E29.55.9.2", {"start": v(42.27, -17.31) * mm, "mid": v(42.37, -17.54) * mm, "end": v(42.52, -17.74) * mm});
            skArc(sketch, "E29.59.9.2", {"start": v(51.02, -17.74) * mm, "mid": v(51.17, -17.54) * mm, "end": v(51.26, -17.31) * mm});
            skArc(sketch, "E29.63.9.2", {"start": v(47.01, -9.95) * mm, "mid": v(46.77, -9.92) * mm, "end": v(46.52, -9.95) * mm});
            skLineSegment(sketch, "E29.67.9.2", {"start": v(46.77, -15) * mm, "end": v(46.77, -9.66) * mm, "construction": true});
            skPoint(sketch, "E29.0.9.3", {"position": v(46.27, -6.45) * mm});
            skLineSegment(sketch, "E29.1.9.3", {"start": v(46.77, -9) * mm, "end": v(42.14, -11.67) * mm, "construction": true});
            skLineSegment(sketch, "E29.4.9.3", {"start": v(49.22, -9.84) * mm, "end": v(51.26, -11.31) * mm});
            skPoint(sketch, "E29.7.9.3", {"position": v(47.26, -6.45) * mm});
            skArc(sketch, "E29.8.9.3", {"start": v(44.3, -9.84) * mm, "mid": v(44.17, -10.5) * mm, "end": v(44.8, -10.7) * mm});
            skLineSegment(sketch, "E29.12.9.3", {"start": v(46.77, -9) * mm, "end": v(46.77, -3.92) * mm, "construction": true});
            skLineSegment(sketch, "E29.15.9.3", {"start": v(46.77, -9) * mm, "end": v(51.17, -11.54) * mm, "construction": true});
            skLineSegment(sketch, "E29.18.9.3", {"start": v(46.27, -6.45) * mm, "end": v(46.52, -3.95) * mm});
            skLineSegment(sketch, "E29.21.9.3", {"start": v(46.77, -9) * mm, "end": v(51.4, -11.67) * mm, "construction": true});
            skPoint(sketch, "E29.24.9.3", {"position": v(49.22, -9.84) * mm});
            skPoint(sketch, "E29.25.9.3", {"position": v(44.3, -9.84) * mm});
            skPoint(sketch, "E29.26.9.3", {"position": v(46.77, -9) * mm});
            skLineSegment(sketch, "E29.27.9.3", {"start": v(46.77, -9) * mm, "end": v(42.37, -11.54) * mm, "construction": true});
            skArc(sketch, "E29.30.9.3", {"start": v(48.72, -10.7) * mm, "mid": v(49.36, -10.5) * mm, "end": v(49.22, -9.84) * mm});
            skPoint(sketch, "E29.34.9.3", {"position": v(44.8, -10.7) * mm});
            skLineSegment(sketch, "E29.35.9.3", {"start": v(44.8, -10.7) * mm, "end": v(42.52, -11.74) * mm});
            skLineSegment(sketch, "E29.38.9.3", {"start": v(44.3, -9.84) * mm, "end": v(42.27, -11.31) * mm});
            skPoint(sketch, "E29.41.9.3", {"position": v(48.72, -10.7) * mm});
            skLineSegment(sketch, "E29.42.9.3", {"start": v(47.26, -6.45) * mm, "end": v(47.01, -3.95) * mm});
            skLineSegment(sketch, "E29.45.9.3", {"start": v(48.72, -10.7) * mm, "end": v(51.02, -11.74) * mm});
            skArc(sketch, "E29.48.9.3", {"start": v(47.26, -6.45) * mm, "mid": v(46.77, -6) * mm, "end": v(46.27, -6.45) * mm});
            skPoint(sketch, "E29.52.9.3", {"position": v(48.72, -10.7) * mm});
            skPoint(sketch, "E29.53.9.3", {"position": v(47.26, -6.45) * mm});
            skPoint(sketch, "E29.54.9.3", {"position": v(44.3, -9.84) * mm});
            skArc(sketch, "E29.55.9.3", {"start": v(42.27, -11.31) * mm, "mid": v(42.37, -11.54) * mm, "end": v(42.52, -11.74) * mm});
            skArc(sketch, "E29.59.9.3", {"start": v(51.02, -11.74) * mm, "mid": v(51.17, -11.54) * mm, "end": v(51.26, -11.31) * mm});
            skArc(sketch, "E29.63.9.3", {"start": v(47.01, -3.95) * mm, "mid": v(46.77, -3.92) * mm, "end": v(46.52, -3.95) * mm});
            skLineSegment(sketch, "E29.67.9.3", {"start": v(46.77, -9) * mm, "end": v(46.77, -3.66) * mm, "construction": true});
            skPoint(sketch, "E29.0.9.4", {"position": v(46.27, -0.45) * mm});
            skLineSegment(sketch, "E29.1.9.4", {"start": v(46.77, -3) * mm, "end": v(42.14, -5.67) * mm, "construction": true});
            skLineSegment(sketch, "E29.4.9.4", {"start": v(49.22, -3.84) * mm, "end": v(51.26, -5.31) * mm});
            skPoint(sketch, "E29.7.9.4", {"position": v(47.26, -0.45) * mm});
            skArc(sketch, "E29.8.9.4", {"start": v(44.3, -3.84) * mm, "mid": v(44.17, -4.5) * mm, "end": v(44.8, -4.7) * mm});
            skLineSegment(sketch, "E29.12.9.4", {"start": v(46.77, -3) * mm, "end": v(46.77, 2.08) * mm, "construction": true});
            skLineSegment(sketch, "E29.15.9.4", {"start": v(46.77, -3) * mm, "end": v(51.17, -5.54) * mm, "construction": true});
            skLineSegment(sketch, "E29.18.9.4", {"start": v(46.27, -0.45) * mm, "end": v(46.52, 2.05) * mm});
            skLineSegment(sketch, "E29.21.9.4", {"start": v(46.77, -3) * mm, "end": v(51.4, -5.67) * mm, "construction": true});
            skPoint(sketch, "E29.24.9.4", {"position": v(49.22, -3.84) * mm});
            skPoint(sketch, "E29.25.9.4", {"position": v(44.3, -3.84) * mm});
            skPoint(sketch, "E29.26.9.4", {"position": v(46.77, -3) * mm});
            skLineSegment(sketch, "E29.27.9.4", {"start": v(46.77, -3) * mm, "end": v(42.37, -5.54) * mm, "construction": true});
            skArc(sketch, "E29.30.9.4", {"start": v(48.72, -4.7) * mm, "mid": v(49.36, -4.5) * mm, "end": v(49.22, -3.84) * mm});
            skPoint(sketch, "E29.34.9.4", {"position": v(44.8, -4.7) * mm});
            skLineSegment(sketch, "E29.35.9.4", {"start": v(44.8, -4.7) * mm, "end": v(42.52, -5.74) * mm});
            skLineSegment(sketch, "E29.38.9.4", {"start": v(44.3, -3.84) * mm, "end": v(42.27, -5.31) * mm});
            skPoint(sketch, "E29.41.9.4", {"position": v(48.72, -4.7) * mm});
            skLineSegment(sketch, "E29.42.9.4", {"start": v(47.26, -0.45) * mm, "end": v(47.01, 2.05) * mm});
            skLineSegment(sketch, "E29.45.9.4", {"start": v(48.72, -4.7) * mm, "end": v(51.02, -5.74) * mm});
            skArc(sketch, "E29.48.9.4", {"start": v(47.26, -0.45) * mm, "mid": v(46.77, 0) * mm, "end": v(46.27, -0.45) * mm});
            skPoint(sketch, "E29.52.9.4", {"position": v(48.72, -4.7) * mm});
            skPoint(sketch, "E29.53.9.4", {"position": v(47.26, -0.45) * mm});
            skPoint(sketch, "E29.54.9.4", {"position": v(44.3, -3.84) * mm});
            skArc(sketch, "E29.55.9.4", {"start": v(42.27, -5.31) * mm, "mid": v(42.37, -5.54) * mm, "end": v(42.52, -5.74) * mm});
            skArc(sketch, "E29.59.9.4", {"start": v(51.02, -5.74) * mm, "mid": v(51.17, -5.54) * mm, "end": v(51.26, -5.31) * mm});
            skArc(sketch, "E29.63.9.4", {"start": v(47.01, 2.05) * mm, "mid": v(46.77, 2.08) * mm, "end": v(46.52, 2.05) * mm});
            skLineSegment(sketch, "E29.67.9.4", {"start": v(46.77, -3) * mm, "end": v(46.77, 2.34) * mm, "construction": true});
            skPoint(sketch, "E29.0.9.5", {"position": v(46.27, 5.55) * mm});
            skLineSegment(sketch, "E29.1.9.5", {"start": v(46.77, 3) * mm, "end": v(42.14, 0.33) * mm, "construction": true});
            skLineSegment(sketch, "E29.4.9.5", {"start": v(49.22, 2.16) * mm, "end": v(51.26, 0.69) * mm});
            skPoint(sketch, "E29.7.9.5", {"position": v(47.26, 5.55) * mm});
            skArc(sketch, "E29.8.9.5", {"start": v(44.3, 2.16) * mm, "mid": v(44.17, 1.5) * mm, "end": v(44.8, 1.3) * mm});
            skLineSegment(sketch, "E29.12.9.5", {"start": v(46.77, 3) * mm, "end": v(46.77, 8.08) * mm, "construction": true});
            skLineSegment(sketch, "E29.15.9.5", {"start": v(46.77, 3) * mm, "end": v(51.17, 0.46) * mm, "construction": true});
            skLineSegment(sketch, "E29.18.9.5", {"start": v(46.27, 5.55) * mm, "end": v(46.52, 8.05) * mm});
            skLineSegment(sketch, "E29.21.9.5", {"start": v(46.77, 3) * mm, "end": v(51.4, 0.33) * mm, "construction": true});
            skPoint(sketch, "E29.24.9.5", {"position": v(49.22, 2.16) * mm});
            skPoint(sketch, "E29.25.9.5", {"position": v(44.3, 2.16) * mm});
            skPoint(sketch, "E29.26.9.5", {"position": v(46.77, 3) * mm});
            skLineSegment(sketch, "E29.27.9.5", {"start": v(46.77, 3) * mm, "end": v(42.37, 0.46) * mm, "construction": true});
            skArc(sketch, "E29.30.9.5", {"start": v(48.72, 1.3) * mm, "mid": v(49.36, 1.5) * mm, "end": v(49.22, 2.16) * mm});
            skPoint(sketch, "E29.34.9.5", {"position": v(44.8, 1.3) * mm});
            skLineSegment(sketch, "E29.35.9.5", {"start": v(44.8, 1.3) * mm, "end": v(42.52, 0.26) * mm});
            skLineSegment(sketch, "E29.38.9.5", {"start": v(44.3, 2.16) * mm, "end": v(42.27, 0.69) * mm});
            skPoint(sketch, "E29.41.9.5", {"position": v(48.72, 1.3) * mm});
            skLineSegment(sketch, "E29.42.9.5", {"start": v(47.26, 5.55) * mm, "end": v(47.01, 8.05) * mm});
            skLineSegment(sketch, "E29.45.9.5", {"start": v(48.72, 1.3) * mm, "end": v(51.02, 0.26) * mm});
            skArc(sketch, "E29.48.9.5", {"start": v(47.26, 5.55) * mm, "mid": v(46.77, 6) * mm, "end": v(46.27, 5.55) * mm});
            skPoint(sketch, "E29.52.9.5", {"position": v(48.72, 1.3) * mm});
            skPoint(sketch, "E29.53.9.5", {"position": v(47.26, 5.55) * mm});
            skPoint(sketch, "E29.54.9.5", {"position": v(44.3, 2.16) * mm});
            skArc(sketch, "E29.55.9.5", {"start": v(42.27, 0.69) * mm, "mid": v(42.37, 0.46) * mm, "end": v(42.52, 0.26) * mm});
            skArc(sketch, "E29.59.9.5", {"start": v(51.02, 0.26) * mm, "mid": v(51.17, 0.46) * mm, "end": v(51.26, 0.69) * mm});
            skArc(sketch, "E29.63.9.5", {"start": v(47.01, 8.05) * mm, "mid": v(46.77, 8.08) * mm, "end": v(46.52, 8.05) * mm});
            skLineSegment(sketch, "E29.67.9.5", {"start": v(46.77, 3) * mm, "end": v(46.77, 8.34) * mm, "construction": true});
            skPoint(sketch, "E29.0.9.6", {"position": v(46.27, 11.55) * mm});
            skLineSegment(sketch, "E29.1.9.6", {"start": v(46.77, 9) * mm, "end": v(42.14, 6.33) * mm, "construction": true});
            skLineSegment(sketch, "E29.4.9.6", {"start": v(49.22, 8.16) * mm, "end": v(51.26, 6.69) * mm});
            skPoint(sketch, "E29.7.9.6", {"position": v(47.26, 11.55) * mm});
            skArc(sketch, "E29.8.9.6", {"start": v(44.3, 8.16) * mm, "mid": v(44.17, 7.5) * mm, "end": v(44.8, 7.3) * mm});
            skLineSegment(sketch, "E29.12.9.6", {"start": v(46.77, 9) * mm, "end": v(46.77, 14.08) * mm, "construction": true});
            skLineSegment(sketch, "E29.15.9.6", {"start": v(46.77, 9) * mm, "end": v(51.17, 6.46) * mm, "construction": true});
            skLineSegment(sketch, "E29.18.9.6", {"start": v(46.27, 11.55) * mm, "end": v(46.52, 14.05) * mm});
            skLineSegment(sketch, "E29.21.9.6", {"start": v(46.77, 9) * mm, "end": v(51.4, 6.33) * mm, "construction": true});
            skPoint(sketch, "E29.24.9.6", {"position": v(49.22, 8.16) * mm});
            skPoint(sketch, "E29.25.9.6", {"position": v(44.3, 8.16) * mm});
            skPoint(sketch, "E29.26.9.6", {"position": v(46.77, 9) * mm});
            skLineSegment(sketch, "E29.27.9.6", {"start": v(46.77, 9) * mm, "end": v(42.37, 6.46) * mm, "construction": true});
            skArc(sketch, "E29.30.9.6", {"start": v(48.72, 7.3) * mm, "mid": v(49.36, 7.5) * mm, "end": v(49.22, 8.16) * mm});
            skPoint(sketch, "E29.34.9.6", {"position": v(44.8, 7.3) * mm});
            skLineSegment(sketch, "E29.35.9.6", {"start": v(44.8, 7.3) * mm, "end": v(42.52, 6.26) * mm});
            skLineSegment(sketch, "E29.38.9.6", {"start": v(44.3, 8.16) * mm, "end": v(42.27, 6.69) * mm});
            skPoint(sketch, "E29.41.9.6", {"position": v(48.72, 7.3) * mm});
            skLineSegment(sketch, "E29.42.9.6", {"start": v(47.26, 11.55) * mm, "end": v(47.01, 14.05) * mm});
            skLineSegment(sketch, "E29.45.9.6", {"start": v(48.72, 7.3) * mm, "end": v(51.02, 6.26) * mm});
            skArc(sketch, "E29.48.9.6", {"start": v(47.26, 11.55) * mm, "mid": v(46.77, 12) * mm, "end": v(46.27, 11.55) * mm});
            skPoint(sketch, "E29.52.9.6", {"position": v(48.72, 7.3) * mm});
            skPoint(sketch, "E29.53.9.6", {"position": v(47.26, 11.55) * mm});
            skPoint(sketch, "E29.54.9.6", {"position": v(44.3, 8.16) * mm});
            skArc(sketch, "E29.55.9.6", {"start": v(42.27, 6.69) * mm, "mid": v(42.37, 6.46) * mm, "end": v(42.52, 6.26) * mm});
            skArc(sketch, "E29.59.9.6", {"start": v(51.02, 6.26) * mm, "mid": v(51.17, 6.46) * mm, "end": v(51.26, 6.69) * mm});
            skArc(sketch, "E29.63.9.6", {"start": v(47.01, 14.05) * mm, "mid": v(46.77, 14.08) * mm, "end": v(46.52, 14.05) * mm});
            skLineSegment(sketch, "E29.67.9.6", {"start": v(46.77, 9) * mm, "end": v(46.77, 14.34) * mm, "construction": true});
            skPoint(sketch, "E29.0.9.7", {"position": v(46.27, 17.55) * mm});
            skLineSegment(sketch, "E29.1.9.7", {"start": v(46.77, 15) * mm, "end": v(42.14, 12.33) * mm, "construction": true});
            skLineSegment(sketch, "E29.4.9.7", {"start": v(49.22, 14.16) * mm, "end": v(51.26, 12.69) * mm});
            skPoint(sketch, "E29.7.9.7", {"position": v(47.26, 17.55) * mm});
            skArc(sketch, "E29.8.9.7", {"start": v(44.3, 14.16) * mm, "mid": v(44.17, 13.5) * mm, "end": v(44.8, 13.3) * mm});
            skLineSegment(sketch, "E29.12.9.7", {"start": v(46.77, 15) * mm, "end": v(46.77, 20.08) * mm, "construction": true});
            skLineSegment(sketch, "E29.15.9.7", {"start": v(46.77, 15) * mm, "end": v(51.17, 12.46) * mm, "construction": true});
            skLineSegment(sketch, "E29.18.9.7", {"start": v(46.27, 17.55) * mm, "end": v(46.52, 20.05) * mm});
            skLineSegment(sketch, "E29.21.9.7", {"start": v(46.77, 15) * mm, "end": v(51.4, 12.33) * mm, "construction": true});
            skPoint(sketch, "E29.24.9.7", {"position": v(49.22, 14.16) * mm});
            skPoint(sketch, "E29.25.9.7", {"position": v(44.3, 14.16) * mm});
            skPoint(sketch, "E29.26.9.7", {"position": v(46.77, 15) * mm});
            skLineSegment(sketch, "E29.27.9.7", {"start": v(46.77, 15) * mm, "end": v(42.37, 12.46) * mm, "construction": true});
            skArc(sketch, "E29.30.9.7", {"start": v(48.72, 13.3) * mm, "mid": v(49.36, 13.5) * mm, "end": v(49.22, 14.16) * mm});
            skPoint(sketch, "E29.34.9.7", {"position": v(44.8, 13.3) * mm});
            skLineSegment(sketch, "E29.35.9.7", {"start": v(44.8, 13.3) * mm, "end": v(42.52, 12.26) * mm});
            skLineSegment(sketch, "E29.38.9.7", {"start": v(44.3, 14.16) * mm, "end": v(42.27, 12.69) * mm});
            skPoint(sketch, "E29.41.9.7", {"position": v(48.72, 13.3) * mm});
            skLineSegment(sketch, "E29.42.9.7", {"start": v(47.26, 17.55) * mm, "end": v(47.01, 20.05) * mm});
            skLineSegment(sketch, "E29.45.9.7", {"start": v(48.72, 13.3) * mm, "end": v(51.02, 12.26) * mm});
            skArc(sketch, "E29.48.9.7", {"start": v(47.26, 17.55) * mm, "mid": v(46.77, 18) * mm, "end": v(46.27, 17.55) * mm});
            skPoint(sketch, "E29.52.9.7", {"position": v(48.72, 13.3) * mm});
            skPoint(sketch, "E29.53.9.7", {"position": v(47.26, 17.55) * mm});
            skPoint(sketch, "E29.54.9.7", {"position": v(44.3, 14.16) * mm});
            skArc(sketch, "E29.55.9.7", {"start": v(42.27, 12.69) * mm, "mid": v(42.37, 12.46) * mm, "end": v(42.52, 12.26) * mm});
            skArc(sketch, "E29.59.9.7", {"start": v(51.02, 12.26) * mm, "mid": v(51.17, 12.46) * mm, "end": v(51.26, 12.69) * mm});
            skArc(sketch, "E29.63.9.7", {"start": v(47.01, 20.05) * mm, "mid": v(46.77, 20.08) * mm, "end": v(46.52, 20.05) * mm});
            skLineSegment(sketch, "E29.67.9.7", {"start": v(46.77, 15) * mm, "end": v(46.77, 20.34) * mm, "construction": true});
            skSolve(sketch);
        }
        {
            var Q0;
            Q0 = qSketchRegion(id + "F4", true);
            extrude(context, id + "F5", {"entities" : qUnion([Q0]), "operationType" : NewBodyOperationType.REMOVE, "oppositeDirection" : true, "depth" : 0.5 * mm});
        }
    });
